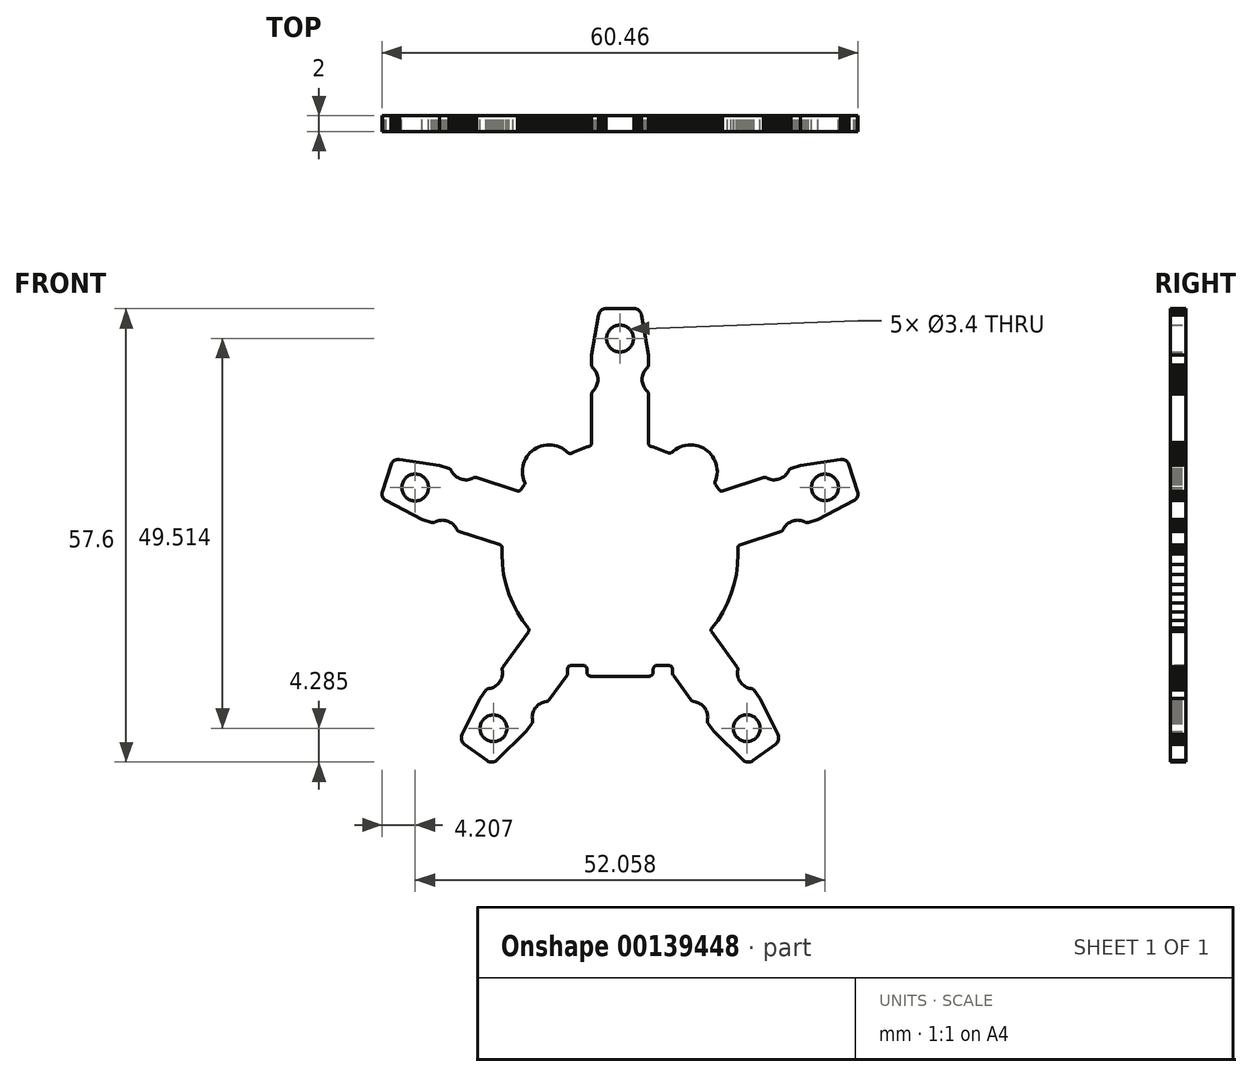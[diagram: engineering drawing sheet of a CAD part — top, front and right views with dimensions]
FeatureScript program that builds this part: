
annotation { "Feature Type Name" : "Feature", "Feature Type Description" : "" }
export const myFeature = defineFeature(function(context is Context, id is Id, definition is map)
    precondition{}
    {
        {
            var Q0;
            Q0=qCreatedBy(makeId("Front.planeOp"),FACE);
            var sketch = newSketch(context, id + "F0", { "sketchPlane" : qUnion([Q0])});
            skLineSegment(sketch, "E0", {"start": v(30.22, 5.42) * mm, "end": v(30.18, 5.6) * mm});
            skLineSegment(sketch, "E1", {"start": v(30.18, 5.6) * mm, "end": v(29.1, 8.94) * mm});
            skLineSegment(sketch, "E2", {"start": v(29.1, 8.94) * mm, "end": v(29.03, 9.1) * mm});
            skLineSegment(sketch, "E3", {"start": v(29.03, 9.1) * mm, "end": v(28.93, 9.25) * mm});
            skLineSegment(sketch, "E4", {"start": v(28.93, 9.25) * mm, "end": v(28.81, 9.38) * mm});
            skLineSegment(sketch, "E5", {"start": v(28.81, 9.38) * mm, "end": v(28.67, 9.48) * mm});
            skLineSegment(sketch, "E6", {"start": v(28.67, 9.48) * mm, "end": v(28.52, 9.56) * mm});
            skLineSegment(sketch, "E7", {"start": v(28.52, 9.56) * mm, "end": v(28.36, 9.6) * mm});
            skLineSegment(sketch, "E8", {"start": v(28.36, 9.6) * mm, "end": v(28.18, 9.63) * mm});
            skLineSegment(sketch, "E9", {"start": v(28.18, 9.63) * mm, "end": v(28, 9.62) * mm});
            skLineSegment(sketch, "E10", {"start": v(28, 9.62) * mm, "end": v(22.92, 8.87) * mm});
            skLineSegment(sketch, "E11", {"start": v(22.92, 8.87) * mm, "end": v(21.71, 8.48) * mm});
            skLineSegment(sketch, "E12", {"start": v(21.71, 8.48) * mm, "end": v(21.66, 8.46) * mm});
            skLineSegment(sketch, "E13", {"start": v(21.66, 8.46) * mm, "end": v(21.62, 8.44) * mm});
            skLineSegment(sketch, "E14", {"start": v(21.62, 8.44) * mm, "end": v(21.58, 8.4) * mm});
            skLineSegment(sketch, "E15", {"start": v(21.58, 8.4) * mm, "end": v(21.54, 8.38) * mm});
            skLineSegment(sketch, "E16", {"start": v(21.54, 8.38) * mm, "end": v(21.5, 8.34) * mm});
            skLineSegment(sketch, "E17", {"start": v(21.5, 8.34) * mm, "end": v(21.47, 8.3) * mm});
            skLineSegment(sketch, "E18", {"start": v(21.47, 8.3) * mm, "end": v(21.44, 8.26) * mm});
            skLineSegment(sketch, "E19", {"start": v(21.44, 8.26) * mm, "end": v(21.32, 8.03) * mm});
            skLineSegment(sketch, "E20", {"start": v(21.32, 8.03) * mm, "end": v(21.2, 7.86) * mm});
            skLineSegment(sketch, "E21", {"start": v(21.2, 7.86) * mm, "end": v(21.07, 7.7) * mm});
            skLineSegment(sketch, "E22", {"start": v(21.07, 7.7) * mm, "end": v(20.92, 7.56) * mm});
            skLineSegment(sketch, "E23", {"start": v(20.92, 7.56) * mm, "end": v(20.77, 7.43) * mm});
            skLineSegment(sketch, "E24", {"start": v(20.77, 7.43) * mm, "end": v(20.6, 7.32) * mm});
            skLineSegment(sketch, "E25", {"start": v(20.6, 7.32) * mm, "end": v(20.4, 7.22) * mm});
            skLineSegment(sketch, "E26", {"start": v(20.4, 7.22) * mm, "end": v(20.22, 7.15) * mm});
            skLineSegment(sketch, "E27", {"start": v(20.22, 7.15) * mm, "end": v(20.02, 7.1) * mm});
            skLineSegment(sketch, "E28", {"start": v(20.02, 7.1) * mm, "end": v(19.81, 7.06) * mm});
            skLineSegment(sketch, "E29", {"start": v(19.81, 7.06) * mm, "end": v(19.6, 7.05) * mm});
            skLineSegment(sketch, "E30", {"start": v(19.6, 7.05) * mm, "end": v(19.4, 7.06) * mm});
            skLineSegment(sketch, "E31", {"start": v(19.4, 7.06) * mm, "end": v(19.2, 7.1) * mm});
            skLineSegment(sketch, "E32", {"start": v(19.2, 7.1) * mm, "end": v(19, 7.14) * mm});
            skLineSegment(sketch, "E33", {"start": v(19, 7.14) * mm, "end": v(18.8, 7.21) * mm});
            skLineSegment(sketch, "E34", {"start": v(18.8, 7.21) * mm, "end": v(18.58, 7.33) * mm});
            skLineSegment(sketch, "E35", {"start": v(18.58, 7.33) * mm, "end": v(18.53, 7.35) * mm});
            skLineSegment(sketch, "E36", {"start": v(18.53, 7.35) * mm, "end": v(18.48, 7.36) * mm});
            skLineSegment(sketch, "E37", {"start": v(18.48, 7.36) * mm, "end": v(18.43, 7.37) * mm});
            skLineSegment(sketch, "E38", {"start": v(18.43, 7.37) * mm, "end": v(18.38, 7.37) * mm});
            skLineSegment(sketch, "E39", {"start": v(18.38, 7.37) * mm, "end": v(18.33, 7.37) * mm});
            skLineSegment(sketch, "E40", {"start": v(18.33, 7.37) * mm, "end": v(18.28, 7.36) * mm});
            skLineSegment(sketch, "E41", {"start": v(18.28, 7.36) * mm, "end": v(18.23, 7.34) * mm});
            skLineSegment(sketch, "E42", {"start": v(18.23, 7.34) * mm, "end": v(13.03, 5.66) * mm});
            skLineSegment(sketch, "E43", {"start": v(13.03, 5.66) * mm, "end": v(13, 5.65) * mm});
            skLineSegment(sketch, "E44", {"start": v(13, 5.65) * mm, "end": v(12.96, 5.65) * mm});
            skLineSegment(sketch, "E45", {"start": v(12.96, 5.65) * mm, "end": v(12.92, 5.64) * mm});
            skLineSegment(sketch, "E46", {"start": v(12.92, 5.64) * mm, "end": v(12.88, 5.64) * mm});
            skLineSegment(sketch, "E47", {"start": v(12.88, 5.64) * mm, "end": v(12.83, 5.64) * mm});
            skLineSegment(sketch, "E48", {"start": v(12.83, 5.64) * mm, "end": v(12.8, 5.64) * mm});
            skLineSegment(sketch, "E49", {"start": v(12.8, 5.64) * mm, "end": v(12.76, 5.65) * mm});
            skLineSegment(sketch, "E50", {"start": v(12.76, 5.65) * mm, "end": v(12.73, 5.66) * mm});
            skLineSegment(sketch, "E51", {"start": v(12.73, 5.66) * mm, "end": v(12.7, 5.68) * mm});
            skLineSegment(sketch, "E52", {"start": v(12.7, 5.68) * mm, "end": v(12.67, 5.7) * mm});
            skLineSegment(sketch, "E53", {"start": v(12.67, 5.7) * mm, "end": v(12.65, 5.72) * mm});
            skLineSegment(sketch, "E54", {"start": v(12.65, 5.72) * mm, "end": v(12.63, 5.74) * mm});
            skLineSegment(sketch, "E55", {"start": v(12.63, 5.74) * mm, "end": v(12.6, 5.77) * mm});
            skLineSegment(sketch, "E56", {"start": v(12.6, 5.77) * mm, "end": v(12.59, 5.8) * mm});
            skLineSegment(sketch, "E57", {"start": v(12.59, 5.8) * mm, "end": v(12.4, 6.07) * mm});
            skLineSegment(sketch, "E58", {"start": v(12.4, 6.07) * mm, "end": v(12.1, 6.48) * mm});
            skLineSegment(sketch, "E59", {"start": v(12.1, 6.48) * mm, "end": v(12.1, 6.5) * mm});
            skLineSegment(sketch, "E60", {"start": v(12.1, 6.5) * mm, "end": v(12.09, 6.52) * mm});
            skLineSegment(sketch, "E61", {"start": v(12.09, 6.52) * mm, "end": v(12.08, 6.54) * mm});
            skLineSegment(sketch, "E62", {"start": v(12.08, 6.54) * mm, "end": v(12.07, 6.56) * mm});
            skLineSegment(sketch, "E63", {"start": v(12.07, 6.56) * mm, "end": v(12.06, 6.58) * mm});
            skLineSegment(sketch, "E64", {"start": v(12.06, 6.58) * mm, "end": v(12.06, 6.6) * mm});
            skLineSegment(sketch, "E65", {"start": v(12.06, 6.6) * mm, "end": v(12.06, 6.63) * mm});
            skLineSegment(sketch, "E66", {"start": v(12.06, 6.63) * mm, "end": v(12.05, 6.65) * mm});
            skLineSegment(sketch, "E67", {"start": v(12.05, 6.65) * mm, "end": v(12.05, 6.67) * mm});
            skLineSegment(sketch, "E68", {"start": v(12.05, 6.67) * mm, "end": v(12.06, 6.7) * mm});
            skLineSegment(sketch, "E69", {"start": v(12.06, 6.7) * mm, "end": v(12.06, 6.71) * mm});
            skLineSegment(sketch, "E70", {"start": v(12.06, 6.71) * mm, "end": v(12.06, 6.73) * mm});
            skLineSegment(sketch, "E71", {"start": v(12.06, 6.73) * mm, "end": v(12.06, 6.73) * mm});
            skLineSegment(sketch, "E72", {"start": v(12.06, 6.73) * mm, "end": v(12.09, 6.78) * mm});
            skLineSegment(sketch, "E73", {"start": v(12.09, 6.78) * mm, "end": v(12.2, 7.09) * mm});
            skLineSegment(sketch, "E74", {"start": v(12.2, 7.09) * mm, "end": v(12.28, 7.42) * mm});
            skLineSegment(sketch, "E75", {"start": v(12.28, 7.42) * mm, "end": v(12.34, 7.75) * mm});
            skLineSegment(sketch, "E76", {"start": v(12.34, 7.75) * mm, "end": v(12.35, 8.1) * mm});
            skLineSegment(sketch, "E77", {"start": v(12.35, 8.1) * mm, "end": v(12.34, 8.45) * mm});
            skLineSegment(sketch, "E78", {"start": v(12.34, 8.45) * mm, "end": v(12.28, 8.79) * mm});
            skLineSegment(sketch, "E79", {"start": v(12.28, 8.79) * mm, "end": v(12.2, 9.11) * mm});
            skLineSegment(sketch, "E80", {"start": v(12.2, 9.11) * mm, "end": v(12.09, 9.42) * mm});
            skLineSegment(sketch, "E81", {"start": v(12.09, 9.42) * mm, "end": v(11.94, 9.72) * mm});
            skLineSegment(sketch, "E82", {"start": v(11.94, 9.72) * mm, "end": v(11.77, 10) * mm});
            skLineSegment(sketch, "E83", {"start": v(11.77, 10) * mm, "end": v(11.58, 10.26) * mm});
            skLineSegment(sketch, "E84", {"start": v(11.58, 10.26) * mm, "end": v(11.36, 10.5) * mm});
            skLineSegment(sketch, "E85", {"start": v(11.36, 10.5) * mm, "end": v(11.12, 10.72) * mm});
            skLineSegment(sketch, "E86", {"start": v(11.12, 10.72) * mm, "end": v(10.85, 10.92) * mm});
            skLineSegment(sketch, "E87", {"start": v(10.85, 10.92) * mm, "end": v(10.57, 11.09) * mm});
            skLineSegment(sketch, "E88", {"start": v(10.57, 11.09) * mm, "end": v(10.28, 11.23) * mm});
            skLineSegment(sketch, "E89", {"start": v(10.28, 11.23) * mm, "end": v(9.96, 11.35) * mm});
            skLineSegment(sketch, "E90", {"start": v(9.96, 11.35) * mm, "end": v(9.64, 11.43) * mm});
            skLineSegment(sketch, "E91", {"start": v(9.64, 11.43) * mm, "end": v(9.3, 11.48) * mm});
            skLineSegment(sketch, "E92", {"start": v(9.3, 11.48) * mm, "end": v(8.95, 11.5) * mm});
            skLineSegment(sketch, "E93", {"start": v(8.95, 11.5) * mm, "end": v(8.6, 11.48) * mm});
            skLineSegment(sketch, "E94", {"start": v(8.6, 11.48) * mm, "end": v(8.27, 11.43) * mm});
            skLineSegment(sketch, "E95", {"start": v(8.27, 11.43) * mm, "end": v(7.94, 11.35) * mm});
            skLineSegment(sketch, "E96", {"start": v(7.94, 11.35) * mm, "end": v(7.63, 11.23) * mm});
            skLineSegment(sketch, "E97", {"start": v(7.63, 11.23) * mm, "end": v(7.33, 11.1) * mm});
            skLineSegment(sketch, "E98", {"start": v(7.33, 11.1) * mm, "end": v(7.05, 10.92) * mm});
            skLineSegment(sketch, "E99", {"start": v(7.05, 10.92) * mm, "end": v(6.8, 10.72) * mm});
            skLineSegment(sketch, "E100", {"start": v(6.8, 10.72) * mm, "end": v(6.63, 10.58) * mm});
            skLineSegment(sketch, "E101", {"start": v(6.63, 10.58) * mm, "end": v(6.55, 10.51) * mm});
            skLineSegment(sketch, "E102", {"start": v(6.55, 10.51) * mm, "end": v(6.47, 10.47) * mm});
            skLineSegment(sketch, "E103", {"start": v(6.47, 10.47) * mm, "end": v(6.37, 10.44) * mm});
            skLineSegment(sketch, "E104", {"start": v(6.37, 10.44) * mm, "end": v(6.27, 10.43) * mm});
            skLineSegment(sketch, "E105", {"start": v(6.27, 10.43) * mm, "end": v(6.17, 10.44) * mm});
            skLineSegment(sketch, "E106", {"start": v(6.17, 10.44) * mm, "end": v(6.08, 10.47) * mm});
            skLineSegment(sketch, "E107", {"start": v(6.08, 10.47) * mm, "end": v(6.02, 10.5) * mm});
            skLineSegment(sketch, "E108", {"start": v(6.02, 10.5) * mm, "end": v(5.84, 10.58) * mm});
            skLineSegment(sketch, "E109", {"start": v(5.84, 10.58) * mm, "end": v(5.53, 10.72) * mm});
            skLineSegment(sketch, "E110", {"start": v(5.53, 10.72) * mm, "end": v(5.2, 10.85) * mm});
            skLineSegment(sketch, "E111", {"start": v(5.2, 10.85) * mm, "end": v(4.88, 10.97) * mm});
            skLineSegment(sketch, "E112", {"start": v(4.88, 10.97) * mm, "end": v(4.56, 11.1) * mm});
            skLineSegment(sketch, "E113", {"start": v(4.56, 11.1) * mm, "end": v(4.22, 11.2) * mm});
            skLineSegment(sketch, "E114", {"start": v(4.22, 11.2) * mm, "end": v(4.02, 11.26) * mm});
            skLineSegment(sketch, "E115", {"start": v(4.02, 11.26) * mm, "end": v(3.9, 11.29) * mm});
            skLineSegment(sketch, "E116", {"start": v(3.9, 11.29) * mm, "end": v(3.82, 11.34) * mm});
            skLineSegment(sketch, "E117", {"start": v(3.82, 11.34) * mm, "end": v(3.75, 11.4) * mm});
            skLineSegment(sketch, "E118", {"start": v(3.75, 11.4) * mm, "end": v(3.68, 11.47) * mm});
            skLineSegment(sketch, "E119", {"start": v(3.68, 11.47) * mm, "end": v(3.64, 11.56) * mm});
            skLineSegment(sketch, "E120", {"start": v(3.64, 11.56) * mm, "end": v(3.6, 11.65) * mm});
            skLineSegment(sketch, "E121", {"start": v(3.6, 11.65) * mm, "end": v(3.6, 11.76) * mm});
            skLineSegment(sketch, "E122", {"start": v(3.6, 11.76) * mm, "end": v(3.6, 17.97) * mm});
            skLineSegment(sketch, "E123", {"start": v(3.6, 17.97) * mm, "end": v(3.6, 18.02) * mm});
            skLineSegment(sketch, "E124", {"start": v(3.6, 18.02) * mm, "end": v(3.59, 18.07) * mm});
            skLineSegment(sketch, "E125", {"start": v(3.59, 18.07) * mm, "end": v(3.58, 18.12) * mm});
            skLineSegment(sketch, "E126", {"start": v(3.58, 18.12) * mm, "end": v(3.56, 18.17) * mm});
            skLineSegment(sketch, "E127", {"start": v(3.56, 18.17) * mm, "end": v(3.54, 18.21) * mm});
            skLineSegment(sketch, "E128", {"start": v(3.54, 18.21) * mm, "end": v(3.5, 18.26) * mm});
            skLineSegment(sketch, "E129", {"start": v(3.5, 18.26) * mm, "end": v(3.48, 18.3) * mm});
            skLineSegment(sketch, "E130", {"start": v(3.48, 18.3) * mm, "end": v(3.3, 18.48) * mm});
            skLineSegment(sketch, "E131", {"start": v(3.3, 18.48) * mm, "end": v(3.17, 18.65) * mm});
            skLineSegment(sketch, "E132", {"start": v(3.17, 18.65) * mm, "end": v(3.06, 18.82) * mm});
            skLineSegment(sketch, "E133", {"start": v(3.06, 18.82) * mm, "end": v(2.97, 19) * mm});
            skLineSegment(sketch, "E134", {"start": v(2.97, 19) * mm, "end": v(2.9, 19.2) * mm});
            skLineSegment(sketch, "E135", {"start": v(2.9, 19.2) * mm, "end": v(2.84, 19.4) * mm});
            skLineSegment(sketch, "E136", {"start": v(2.84, 19.4) * mm, "end": v(2.81, 19.6) * mm});
            skLineSegment(sketch, "E137", {"start": v(2.81, 19.6) * mm, "end": v(2.8, 19.8) * mm});
            skLineSegment(sketch, "E138", {"start": v(2.8, 19.8) * mm, "end": v(2.81, 20) * mm});
            skLineSegment(sketch, "E139", {"start": v(2.81, 20) * mm, "end": v(2.84, 20.21) * mm});
            skLineSegment(sketch, "E140", {"start": v(2.84, 20.21) * mm, "end": v(2.9, 20.41) * mm});
            skLineSegment(sketch, "E141", {"start": v(2.9, 20.41) * mm, "end": v(2.97, 20.6) * mm});
            skLineSegment(sketch, "E142", {"start": v(2.97, 20.6) * mm, "end": v(3.06, 20.78) * mm});
            skLineSegment(sketch, "E143", {"start": v(3.06, 20.78) * mm, "end": v(3.17, 20.96) * mm});
            skLineSegment(sketch, "E144", {"start": v(3.17, 20.96) * mm, "end": v(3.3, 21.12) * mm});
            skLineSegment(sketch, "E145", {"start": v(3.3, 21.12) * mm, "end": v(3.48, 21.3) * mm});
            skLineSegment(sketch, "E146", {"start": v(3.48, 21.3) * mm, "end": v(3.5, 21.35) * mm});
            skLineSegment(sketch, "E147", {"start": v(3.5, 21.35) * mm, "end": v(3.54, 21.39) * mm});
            skLineSegment(sketch, "E148", {"start": v(3.54, 21.39) * mm, "end": v(3.56, 21.44) * mm});
            skLineSegment(sketch, "E149", {"start": v(3.56, 21.44) * mm, "end": v(3.58, 21.48) * mm});
            skLineSegment(sketch, "E150", {"start": v(3.58, 21.48) * mm, "end": v(3.59, 21.53) * mm});
            skLineSegment(sketch, "E151", {"start": v(3.59, 21.53) * mm, "end": v(3.6, 21.58) * mm});
            skLineSegment(sketch, "E152", {"start": v(3.6, 21.58) * mm, "end": v(3.6, 21.63) * mm});
            skLineSegment(sketch, "E153", {"start": v(3.6, 21.63) * mm, "end": v(3.6, 22.9) * mm});
            skLineSegment(sketch, "E154", {"start": v(3.6, 22.9) * mm, "end": v(2.74, 27.97) * mm});
            skLineSegment(sketch, "E155", {"start": v(2.74, 27.97) * mm, "end": v(2.7, 28.14) * mm});
            skLineSegment(sketch, "E156", {"start": v(2.7, 28.14) * mm, "end": v(2.62, 28.3) * mm});
            skLineSegment(sketch, "E157", {"start": v(2.62, 28.3) * mm, "end": v(2.52, 28.44) * mm});
            skLineSegment(sketch, "E158", {"start": v(2.52, 28.44) * mm, "end": v(2.4, 28.57) * mm});
            skLineSegment(sketch, "E159", {"start": v(2.4, 28.57) * mm, "end": v(2.26, 28.67) * mm});
            skLineSegment(sketch, "E160", {"start": v(2.26, 28.67) * mm, "end": v(2.1, 28.74) * mm});
            skLineSegment(sketch, "E161", {"start": v(2.1, 28.74) * mm, "end": v(1.93, 28.79) * mm});
            skLineSegment(sketch, "E162", {"start": v(1.93, 28.79) * mm, "end": v(1.76, 28.8) * mm});
            skLineSegment(sketch, "E163", {"start": v(1.76, 28.8) * mm, "end": v(-1.4, 28.8) * mm});
            skLineSegment(sketch, "E164", {"start": v(-1.4, 28.8) * mm, "end": v(1.6, 28.8) * mm});
            skLineSegment(sketch, "E165", {"start": v(-1.4, 28.8) * mm, "end": v(-1.7, 28.8) * mm});
            skLineSegment(sketch, "E166", {"start": v(-1.7, 28.8) * mm, "end": v(-1.76, 28.8) * mm});
            skLineSegment(sketch, "E167", {"start": v(-1.76, 28.8) * mm, "end": v(-1.93, 28.79) * mm});
            skLineSegment(sketch, "E168", {"start": v(-1.93, 28.79) * mm, "end": v(-2.1, 28.74) * mm});
            skLineSegment(sketch, "E169", {"start": v(-2.1, 28.74) * mm, "end": v(-2.26, 28.67) * mm});
            skLineSegment(sketch, "E170", {"start": v(-2.26, 28.67) * mm, "end": v(-2.4, 28.57) * mm});
            skLineSegment(sketch, "E171", {"start": v(-2.4, 28.57) * mm, "end": v(-2.52, 28.44) * mm});
            skLineSegment(sketch, "E172", {"start": v(-2.52, 28.44) * mm, "end": v(-2.62, 28.3) * mm});
            skLineSegment(sketch, "E173", {"start": v(-2.62, 28.3) * mm, "end": v(-2.7, 28.14) * mm});
            skLineSegment(sketch, "E174", {"start": v(-2.7, 28.14) * mm, "end": v(-2.74, 27.97) * mm});
            skLineSegment(sketch, "E175", {"start": v(-2.74, 27.97) * mm, "end": v(-3.6, 22.9) * mm});
            skLineSegment(sketch, "E176", {"start": v(-3.6, 22.9) * mm, "end": v(-3.6, 21.63) * mm});
            skLineSegment(sketch, "E177", {"start": v(-3.6, 21.63) * mm, "end": v(-3.6, 21.58) * mm});
            skLineSegment(sketch, "E178", {"start": v(-3.6, 21.58) * mm, "end": v(-3.59, 21.53) * mm});
            skLineSegment(sketch, "E179", {"start": v(-3.59, 21.53) * mm, "end": v(-3.58, 21.48) * mm});
            skLineSegment(sketch, "E180", {"start": v(-3.58, 21.48) * mm, "end": v(-3.56, 21.44) * mm});
            skLineSegment(sketch, "E181", {"start": v(-3.56, 21.44) * mm, "end": v(-3.53, 21.39) * mm});
            skLineSegment(sketch, "E182", {"start": v(-3.53, 21.39) * mm, "end": v(-3.5, 21.35) * mm});
            skLineSegment(sketch, "E183", {"start": v(-3.5, 21.35) * mm, "end": v(-3.48, 21.3) * mm});
            skLineSegment(sketch, "E184", {"start": v(-3.48, 21.3) * mm, "end": v(-3.3, 21.12) * mm});
            skLineSegment(sketch, "E185", {"start": v(-3.3, 21.12) * mm, "end": v(-3.17, 20.96) * mm});
            skLineSegment(sketch, "E186", {"start": v(-3.17, 20.96) * mm, "end": v(-3.06, 20.78) * mm});
            skLineSegment(sketch, "E187", {"start": v(-3.06, 20.78) * mm, "end": v(-2.97, 20.6) * mm});
            skLineSegment(sketch, "E188", {"start": v(-2.97, 20.6) * mm, "end": v(-2.9, 20.41) * mm});
            skLineSegment(sketch, "E189", {"start": v(-2.9, 20.41) * mm, "end": v(-2.84, 20.21) * mm});
            skLineSegment(sketch, "E190", {"start": v(-2.84, 20.21) * mm, "end": v(-2.8, 20) * mm});
            skLineSegment(sketch, "E191", {"start": v(-2.8, 20) * mm, "end": v(-2.8, 19.8) * mm});
            skLineSegment(sketch, "E192", {"start": v(-2.8, 19.8) * mm, "end": v(-2.8, 19.6) * mm});
            skLineSegment(sketch, "E193", {"start": v(-2.8, 19.6) * mm, "end": v(-2.84, 19.4) * mm});
            skLineSegment(sketch, "E194", {"start": v(-2.84, 19.4) * mm, "end": v(-2.9, 19.2) * mm});
            skLineSegment(sketch, "E195", {"start": v(-2.9, 19.2) * mm, "end": v(-2.97, 19) * mm});
            skLineSegment(sketch, "E196", {"start": v(-2.97, 19) * mm, "end": v(-3.06, 18.82) * mm});
            skLineSegment(sketch, "E197", {"start": v(-3.06, 18.82) * mm, "end": v(-3.17, 18.65) * mm});
            skLineSegment(sketch, "E198", {"start": v(-3.17, 18.65) * mm, "end": v(-3.3, 18.48) * mm});
            skLineSegment(sketch, "E199", {"start": v(-3.3, 18.48) * mm, "end": v(-3.48, 18.3) * mm});
            skLineSegment(sketch, "E200", {"start": v(-3.48, 18.3) * mm, "end": v(-3.5, 18.26) * mm});
            skLineSegment(sketch, "E201", {"start": v(-3.5, 18.26) * mm, "end": v(-3.53, 18.21) * mm});
            skLineSegment(sketch, "E202", {"start": v(-3.53, 18.21) * mm, "end": v(-3.56, 18.17) * mm});
            skLineSegment(sketch, "E203", {"start": v(-3.56, 18.17) * mm, "end": v(-3.58, 18.12) * mm});
            skLineSegment(sketch, "E204", {"start": v(-3.58, 18.12) * mm, "end": v(-3.59, 18.07) * mm});
            skLineSegment(sketch, "E205", {"start": v(-3.59, 18.07) * mm, "end": v(-3.6, 18.02) * mm});
            skLineSegment(sketch, "E206", {"start": v(-3.6, 18.02) * mm, "end": v(-3.6, 17.97) * mm});
            skLineSegment(sketch, "E207", {"start": v(-3.6, 17.97) * mm, "end": v(-3.6, 11.83) * mm});
            skLineSegment(sketch, "E208", {"start": v(-3.6, 11.83) * mm, "end": v(-3.6, 11.66) * mm});
            skLineSegment(sketch, "E209", {"start": v(-3.6, 11.66) * mm, "end": v(-3.63, 11.56) * mm});
            skLineSegment(sketch, "E210", {"start": v(-3.63, 11.56) * mm, "end": v(-3.68, 11.48) * mm});
            skLineSegment(sketch, "E211", {"start": v(-3.68, 11.48) * mm, "end": v(-3.74, 11.4) * mm});
            skLineSegment(sketch, "E212", {"start": v(-3.74, 11.4) * mm, "end": v(-3.81, 11.34) * mm});
            skLineSegment(sketch, "E213", {"start": v(-3.81, 11.34) * mm, "end": v(-3.9, 11.3) * mm});
            skLineSegment(sketch, "E214", {"start": v(-3.9, 11.3) * mm, "end": v(-3.94, 11.28) * mm});
            skLineSegment(sketch, "E215", {"start": v(-3.94, 11.28) * mm, "end": v(-3.94, 11.28) * mm});
            skLineSegment(sketch, "E216", {"start": v(-3.94, 11.28) * mm, "end": v(-4, 11.27) * mm});
            skLineSegment(sketch, "E217", {"start": v(-4, 11.27) * mm, "end": v(-4.22, 11.2) * mm});
            skLineSegment(sketch, "E218", {"start": v(-4.22, 11.2) * mm, "end": v(-4.55, 11.1) * mm});
            skLineSegment(sketch, "E219", {"start": v(-4.55, 11.1) * mm, "end": v(-4.88, 10.97) * mm});
            skLineSegment(sketch, "E220", {"start": v(-4.88, 10.97) * mm, "end": v(-5.2, 10.85) * mm});
            skLineSegment(sketch, "E221", {"start": v(-5.2, 10.85) * mm, "end": v(-5.53, 10.72) * mm});
            skLineSegment(sketch, "E222", {"start": v(-5.53, 10.72) * mm, "end": v(-5.84, 10.58) * mm});
            skLineSegment(sketch, "E223", {"start": v(-5.84, 10.58) * mm, "end": v(-6.12, 10.45) * mm});
            skLineSegment(sketch, "E224", {"start": v(-6.12, 10.45) * mm, "end": v(-6.12, 10.45) * mm});
            skLineSegment(sketch, "E225", {"start": v(-6.12, 10.45) * mm, "end": v(-6.22, 10.42) * mm});
            skLineSegment(sketch, "E226", {"start": v(-6.22, 10.42) * mm, "end": v(-6.32, 10.41) * mm});
            skLineSegment(sketch, "E227", {"start": v(-6.32, 10.41) * mm, "end": v(-6.42, 10.42) * mm});
            skLineSegment(sketch, "E228", {"start": v(-6.42, 10.42) * mm, "end": v(-6.51, 10.45) * mm});
            skLineSegment(sketch, "E229", {"start": v(-6.51, 10.45) * mm, "end": v(-6.6, 10.5) * mm});
            skLineSegment(sketch, "E230", {"start": v(-6.6, 10.5) * mm, "end": v(-6.66, 10.55) * mm});
            skLineSegment(sketch, "E231", {"start": v(-6.66, 10.55) * mm, "end": v(-6.66, 10.55) * mm});
            skLineSegment(sketch, "E232", {"start": v(-6.66, 10.55) * mm, "end": v(-6.85, 10.72) * mm});
            skLineSegment(sketch, "E233", {"start": v(-6.85, 10.72) * mm, "end": v(-7.12, 10.92) * mm});
            skLineSegment(sketch, "E234", {"start": v(-7.12, 10.92) * mm, "end": v(-7.4, 11.09) * mm});
            skLineSegment(sketch, "E235", {"start": v(-7.4, 11.09) * mm, "end": v(-7.7, 11.23) * mm});
            skLineSegment(sketch, "E236", {"start": v(-7.7, 11.23) * mm, "end": v(-8, 11.35) * mm});
            skLineSegment(sketch, "E237", {"start": v(-8, 11.35) * mm, "end": v(-8.33, 11.43) * mm});
            skLineSegment(sketch, "E238", {"start": v(-8.33, 11.43) * mm, "end": v(-8.67, 11.48) * mm});
            skLineSegment(sketch, "E239", {"start": v(-8.67, 11.48) * mm, "end": v(-9.02, 11.5) * mm});
            skLineSegment(sketch, "E240", {"start": v(-9.02, 11.5) * mm, "end": v(-9.36, 11.48) * mm});
            skLineSegment(sketch, "E241", {"start": v(-9.36, 11.48) * mm, "end": v(-9.7, 11.43) * mm});
            skLineSegment(sketch, "E242", {"start": v(-9.7, 11.43) * mm, "end": v(-10.03, 11.35) * mm});
            skLineSegment(sketch, "E243", {"start": v(-10.03, 11.35) * mm, "end": v(-10.34, 11.23) * mm});
            skLineSegment(sketch, "E244", {"start": v(-10.34, 11.23) * mm, "end": v(-10.64, 11.09) * mm});
            skLineSegment(sketch, "E245", {"start": v(-10.64, 11.09) * mm, "end": v(-10.92, 10.92) * mm});
            skLineSegment(sketch, "E246", {"start": v(-10.92, 10.92) * mm, "end": v(-11.18, 10.72) * mm});
            skLineSegment(sketch, "E247", {"start": v(-11.18, 10.72) * mm, "end": v(-11.42, 10.5) * mm});
            skLineSegment(sketch, "E248", {"start": v(-11.42, 10.5) * mm, "end": v(-11.64, 10.26) * mm});
            skLineSegment(sketch, "E249", {"start": v(-11.64, 10.26) * mm, "end": v(-11.84, 10) * mm});
            skLineSegment(sketch, "E250", {"start": v(-11.84, 10) * mm, "end": v(-12, 9.72) * mm});
            skLineSegment(sketch, "E251", {"start": v(-12, 9.72) * mm, "end": v(-12.15, 9.42) * mm});
            skLineSegment(sketch, "E252", {"start": v(-12.15, 9.42) * mm, "end": v(-12.26, 9.11) * mm});
            skLineSegment(sketch, "E253", {"start": v(-12.26, 9.11) * mm, "end": v(-12.35, 8.79) * mm});
            skLineSegment(sketch, "E254", {"start": v(-12.35, 8.79) * mm, "end": v(-12.4, 8.45) * mm});
            skLineSegment(sketch, "E255", {"start": v(-12.4, 8.45) * mm, "end": v(-12.42, 8.1) * mm});
            skLineSegment(sketch, "E256", {"start": v(-12.42, 8.1) * mm, "end": v(-12.4, 7.75) * mm});
            skLineSegment(sketch, "E257", {"start": v(-12.4, 7.75) * mm, "end": v(-12.35, 7.42) * mm});
            skLineSegment(sketch, "E258", {"start": v(-12.35, 7.42) * mm, "end": v(-12.26, 7.09) * mm});
            skLineSegment(sketch, "E259", {"start": v(-12.26, 7.09) * mm, "end": v(-12.15, 6.78) * mm});
            skLineSegment(sketch, "E260", {"start": v(-12.15, 6.78) * mm, "end": v(-12.1, 6.67) * mm});
            skLineSegment(sketch, "E261", {"start": v(-12.1, 6.67) * mm, "end": v(-12.1, 6.67) * mm});
            skLineSegment(sketch, "E262", {"start": v(-12.1, 6.67) * mm, "end": v(-12.1, 6.64) * mm});
            skLineSegment(sketch, "E263", {"start": v(-12.1, 6.64) * mm, "end": v(-12.1, 6.61) * mm});
            skLineSegment(sketch, "E264", {"start": v(-12.1, 6.61) * mm, "end": v(-12.1, 6.58) * mm});
            skLineSegment(sketch, "E265", {"start": v(-12.1, 6.58) * mm, "end": v(-12.1, 6.56) * mm});
            skLineSegment(sketch, "E266", {"start": v(-12.1, 6.56) * mm, "end": v(-12.1, 6.53) * mm});
            skLineSegment(sketch, "E267", {"start": v(-12.1, 6.53) * mm, "end": v(-12.1, 6.51) * mm});
            skLineSegment(sketch, "E268", {"start": v(-12.1, 6.51) * mm, "end": v(-12.11, 6.5) * mm});
            skLineSegment(sketch, "E269", {"start": v(-12.11, 6.5) * mm, "end": v(-12.12, 6.47) * mm});
            skLineSegment(sketch, "E270", {"start": v(-12.12, 6.47) * mm, "end": v(-12.13, 6.45) * mm});
            skLineSegment(sketch, "E271", {"start": v(-12.13, 6.45) * mm, "end": v(-12.15, 6.43) * mm});
            skLineSegment(sketch, "E272", {"start": v(-12.15, 6.43) * mm, "end": v(-12.44, 6) * mm});
            skLineSegment(sketch, "E273", {"start": v(-12.44, 6) * mm, "end": v(-12.56, 5.83) * mm});
            skLineSegment(sketch, "E274", {"start": v(-12.56, 5.83) * mm, "end": v(-12.58, 5.8) * mm});
            skLineSegment(sketch, "E275", {"start": v(-12.58, 5.8) * mm, "end": v(-12.6, 5.77) * mm});
            skLineSegment(sketch, "E276", {"start": v(-12.6, 5.77) * mm, "end": v(-12.63, 5.74) * mm});
            skLineSegment(sketch, "E277", {"start": v(-12.63, 5.74) * mm, "end": v(-12.66, 5.71) * mm});
            skLineSegment(sketch, "E278", {"start": v(-12.66, 5.71) * mm, "end": v(-12.69, 5.7) * mm});
            skLineSegment(sketch, "E279", {"start": v(-12.69, 5.7) * mm, "end": v(-12.72, 5.67) * mm});
            skLineSegment(sketch, "E280", {"start": v(-12.72, 5.67) * mm, "end": v(-12.76, 5.66) * mm});
            skLineSegment(sketch, "E281", {"start": v(-12.76, 5.66) * mm, "end": v(-12.8, 5.65) * mm});
            skLineSegment(sketch, "E282", {"start": v(-12.8, 5.65) * mm, "end": v(-12.84, 5.64) * mm});
            skLineSegment(sketch, "E283", {"start": v(-12.84, 5.64) * mm, "end": v(-12.88, 5.64) * mm});
            skLineSegment(sketch, "E284", {"start": v(-12.88, 5.64) * mm, "end": v(-12.93, 5.65) * mm});
            skLineSegment(sketch, "E285", {"start": v(-12.93, 5.65) * mm, "end": v(-13, 5.65) * mm});
            skLineSegment(sketch, "E286", {"start": v(-13, 5.65) * mm, "end": v(-13.03, 5.66) * mm});
            skLineSegment(sketch, "E287", {"start": v(-13.03, 5.66) * mm, "end": v(-18.23, 7.34) * mm});
            skLineSegment(sketch, "E288", {"start": v(-18.23, 7.34) * mm, "end": v(-18.28, 7.36) * mm});
            skLineSegment(sketch, "E289", {"start": v(-18.28, 7.36) * mm, "end": v(-18.33, 7.37) * mm});
            skLineSegment(sketch, "E290", {"start": v(-18.33, 7.37) * mm, "end": v(-18.38, 7.37) * mm});
            skLineSegment(sketch, "E291", {"start": v(-18.38, 7.37) * mm, "end": v(-18.43, 7.37) * mm});
            skLineSegment(sketch, "E292", {"start": v(-18.43, 7.37) * mm, "end": v(-18.48, 7.36) * mm});
            skLineSegment(sketch, "E293", {"start": v(-18.48, 7.36) * mm, "end": v(-18.53, 7.35) * mm});
            skLineSegment(sketch, "E294", {"start": v(-18.53, 7.35) * mm, "end": v(-18.58, 7.33) * mm});
            skLineSegment(sketch, "E295", {"start": v(-18.58, 7.33) * mm, "end": v(-18.8, 7.21) * mm});
            skLineSegment(sketch, "E296", {"start": v(-18.8, 7.21) * mm, "end": v(-19, 7.14) * mm});
            skLineSegment(sketch, "E297", {"start": v(-19, 7.14) * mm, "end": v(-19.2, 7.1) * mm});
            skLineSegment(sketch, "E298", {"start": v(-19.2, 7.1) * mm, "end": v(-19.4, 7.06) * mm});
            skLineSegment(sketch, "E299", {"start": v(-19.4, 7.06) * mm, "end": v(-19.6, 7.05) * mm});
            skLineSegment(sketch, "E300", {"start": v(-19.6, 7.05) * mm, "end": v(-19.81, 7.06) * mm});
            skLineSegment(sketch, "E301", {"start": v(-19.81, 7.06) * mm, "end": v(-20.02, 7.1) * mm});
            skLineSegment(sketch, "E302", {"start": v(-20.02, 7.1) * mm, "end": v(-20.22, 7.15) * mm});
            skLineSegment(sketch, "E303", {"start": v(-20.22, 7.15) * mm, "end": v(-20.4, 7.22) * mm});
            skLineSegment(sketch, "E304", {"start": v(-20.4, 7.22) * mm, "end": v(-20.6, 7.32) * mm});
            skLineSegment(sketch, "E305", {"start": v(-20.6, 7.32) * mm, "end": v(-20.77, 7.43) * mm});
            skLineSegment(sketch, "E306", {"start": v(-20.77, 7.43) * mm, "end": v(-20.92, 7.56) * mm});
            skLineSegment(sketch, "E307", {"start": v(-20.92, 7.56) * mm, "end": v(-21.07, 7.7) * mm});
            skLineSegment(sketch, "E308", {"start": v(-21.07, 7.7) * mm, "end": v(-21.2, 7.86) * mm});
            skLineSegment(sketch, "E309", {"start": v(-21.2, 7.86) * mm, "end": v(-21.32, 8.03) * mm});
            skLineSegment(sketch, "E310", {"start": v(-21.32, 8.03) * mm, "end": v(-21.44, 8.26) * mm});
            skLineSegment(sketch, "E311", {"start": v(-21.44, 8.26) * mm, "end": v(-21.47, 8.3) * mm});
            skLineSegment(sketch, "E312", {"start": v(-21.47, 8.3) * mm, "end": v(-21.5, 8.34) * mm});
            skLineSegment(sketch, "E313", {"start": v(-21.5, 8.34) * mm, "end": v(-21.53, 8.38) * mm});
            skLineSegment(sketch, "E314", {"start": v(-21.53, 8.38) * mm, "end": v(-21.57, 8.4) * mm});
            skLineSegment(sketch, "E315", {"start": v(-21.57, 8.4) * mm, "end": v(-21.62, 8.44) * mm});
            skLineSegment(sketch, "E316", {"start": v(-21.62, 8.44) * mm, "end": v(-21.66, 8.46) * mm});
            skLineSegment(sketch, "E317", {"start": v(-21.66, 8.46) * mm, "end": v(-21.71, 8.48) * mm});
            skLineSegment(sketch, "E318", {"start": v(-21.71, 8.48) * mm, "end": v(-22.92, 8.87) * mm});
            skLineSegment(sketch, "E319", {"start": v(-22.92, 8.87) * mm, "end": v(-28, 9.62) * mm});
            skLineSegment(sketch, "E320", {"start": v(-28, 9.62) * mm, "end": v(-28.18, 9.63) * mm});
            skLineSegment(sketch, "E321", {"start": v(-28.18, 9.63) * mm, "end": v(-28.36, 9.6) * mm});
            skLineSegment(sketch, "E322", {"start": v(-28.36, 9.6) * mm, "end": v(-28.52, 9.56) * mm});
            skLineSegment(sketch, "E323", {"start": v(-28.52, 9.56) * mm, "end": v(-28.67, 9.48) * mm});
            skLineSegment(sketch, "E324", {"start": v(-28.67, 9.48) * mm, "end": v(-28.81, 9.37) * mm});
            skLineSegment(sketch, "E325", {"start": v(-28.81, 9.37) * mm, "end": v(-28.93, 9.25) * mm});
            skLineSegment(sketch, "E326", {"start": v(-28.93, 9.25) * mm, "end": v(-29.03, 9.1) * mm});
            skLineSegment(sketch, "E327", {"start": v(-29.03, 9.1) * mm, "end": v(-29.1, 8.94) * mm});
            skLineSegment(sketch, "E328", {"start": v(-29.1, 8.94) * mm, "end": v(-30.18, 5.6) * mm});
            skLineSegment(sketch, "E329", {"start": v(-30.18, 5.6) * mm, "end": v(-30.22, 5.42) * mm});
            skLineSegment(sketch, "E330", {"start": v(-30.22, 5.42) * mm, "end": v(-30.23, 5.25) * mm});
            skLineSegment(sketch, "E331", {"start": v(-30.23, 5.25) * mm, "end": v(-30.2, 5.08) * mm});
            skLineSegment(sketch, "E332", {"start": v(-30.2, 5.08) * mm, "end": v(-30.16, 4.91) * mm});
            skLineSegment(sketch, "E333", {"start": v(-30.16, 4.91) * mm, "end": v(-30.08, 4.76) * mm});
            skLineSegment(sketch, "E334", {"start": v(-30.08, 4.76) * mm, "end": v(-29.98, 4.62) * mm});
            skLineSegment(sketch, "E335", {"start": v(-29.98, 4.62) * mm, "end": v(-29.85, 4.5) * mm});
            skLineSegment(sketch, "E336", {"start": v(-29.85, 4.5) * mm, "end": v(-29.7, 4.4) * mm});
            skLineSegment(sketch, "E337", {"start": v(-29.7, 4.4) * mm, "end": v(-25.14, 2.02) * mm});
            skLineSegment(sketch, "E338", {"start": v(-25.14, 2.02) * mm, "end": v(-23.94, 1.63) * mm});
            skLineSegment(sketch, "E339", {"start": v(-23.94, 1.63) * mm, "end": v(-23.89, 1.62) * mm});
            skLineSegment(sketch, "E340", {"start": v(-23.89, 1.62) * mm, "end": v(-23.84, 1.6) * mm});
            skLineSegment(sketch, "E341", {"start": v(-23.84, 1.6) * mm, "end": v(-23.79, 1.6) * mm});
            skLineSegment(sketch, "E342", {"start": v(-23.79, 1.6) * mm, "end": v(-23.73, 1.6) * mm});
            skLineSegment(sketch, "E343", {"start": v(-23.73, 1.6) * mm, "end": v(-23.68, 1.61) * mm});
            skLineSegment(sketch, "E344", {"start": v(-23.68, 1.61) * mm, "end": v(-23.63, 1.63) * mm});
            skLineSegment(sketch, "E345", {"start": v(-23.63, 1.63) * mm, "end": v(-23.59, 1.65) * mm});
            skLineSegment(sketch, "E346", {"start": v(-23.59, 1.65) * mm, "end": v(-23.35, 1.76) * mm});
            skLineSegment(sketch, "E347", {"start": v(-23.35, 1.76) * mm, "end": v(-23.16, 1.83) * mm});
            skLineSegment(sketch, "E348", {"start": v(-23.16, 1.83) * mm, "end": v(-22.96, 1.88) * mm});
            skLineSegment(sketch, "E349", {"start": v(-22.96, 1.88) * mm, "end": v(-22.76, 1.91) * mm});
            skLineSegment(sketch, "E350", {"start": v(-22.76, 1.91) * mm, "end": v(-22.55, 1.92) * mm});
            skLineSegment(sketch, "E351", {"start": v(-22.55, 1.92) * mm, "end": v(-22.35, 1.91) * mm});
            skLineSegment(sketch, "E352", {"start": v(-22.35, 1.91) * mm, "end": v(-22.15, 1.88) * mm});
            skLineSegment(sketch, "E353", {"start": v(-22.15, 1.88) * mm, "end": v(-21.95, 1.82) * mm});
            skLineSegment(sketch, "E354", {"start": v(-21.95, 1.82) * mm, "end": v(-21.75, 1.75) * mm});
            skLineSegment(sketch, "E355", {"start": v(-21.75, 1.75) * mm, "end": v(-21.57, 1.66) * mm});
            skLineSegment(sketch, "E356", {"start": v(-21.57, 1.66) * mm, "end": v(-21.4, 1.55) * mm});
            skLineSegment(sketch, "E357", {"start": v(-21.4, 1.55) * mm, "end": v(-21.24, 1.42) * mm});
            skLineSegment(sketch, "E358", {"start": v(-21.24, 1.42) * mm, "end": v(-21.1, 1.27) * mm});
            skLineSegment(sketch, "E359", {"start": v(-21.1, 1.27) * mm, "end": v(-20.96, 1.12) * mm});
            skLineSegment(sketch, "E360", {"start": v(-20.96, 1.12) * mm, "end": v(-20.85, 0.95) * mm});
            skLineSegment(sketch, "E361", {"start": v(-20.85, 0.95) * mm, "end": v(-20.72, 0.72) * mm});
            skLineSegment(sketch, "E362", {"start": v(-20.72, 0.72) * mm, "end": v(-20.7, 0.67) * mm});
            skLineSegment(sketch, "E363", {"start": v(-20.7, 0.67) * mm, "end": v(-20.66, 0.63) * mm});
            skLineSegment(sketch, "E364", {"start": v(-20.66, 0.63) * mm, "end": v(-20.63, 0.6) * mm});
            skLineSegment(sketch, "E365", {"start": v(-20.63, 0.6) * mm, "end": v(-20.59, 0.57) * mm});
            skLineSegment(sketch, "E366", {"start": v(-20.59, 0.57) * mm, "end": v(-20.54, 0.54) * mm});
            skLineSegment(sketch, "E367", {"start": v(-20.54, 0.54) * mm, "end": v(-20.5, 0.52) * mm});
            skLineSegment(sketch, "E368", {"start": v(-20.5, 0.52) * mm, "end": v(-20.45, 0.5) * mm});
            skLineSegment(sketch, "E369", {"start": v(-20.45, 0.5) * mm, "end": v(-15.32, -1.17) * mm});
            skLineSegment(sketch, "E370", {"start": v(-15.32, -1.17) * mm, "end": v(-15.3, -1.18) * mm});
            skLineSegment(sketch, "E371", {"start": v(-15.3, -1.18) * mm, "end": v(-15.25, -1.2) * mm});
            skLineSegment(sketch, "E372", {"start": v(-15.25, -1.2) * mm, "end": v(-15.21, -1.21) * mm});
            skLineSegment(sketch, "E373", {"start": v(-15.21, -1.21) * mm, "end": v(-15.16, -1.23) * mm});
            skLineSegment(sketch, "E374", {"start": v(-15.16, -1.23) * mm, "end": v(-15.12, -1.26) * mm});
            skLineSegment(sketch, "E375", {"start": v(-15.12, -1.26) * mm, "end": v(-15.08, -1.29) * mm});
            skLineSegment(sketch, "E376", {"start": v(-15.08, -1.29) * mm, "end": v(-15.05, -1.32) * mm});
            skLineSegment(sketch, "E377", {"start": v(-15.05, -1.32) * mm, "end": v(-15.03, -1.35) * mm});
            skLineSegment(sketch, "E378", {"start": v(-15.03, -1.35) * mm, "end": v(-15.01, -1.39) * mm});
            skLineSegment(sketch, "E379", {"start": v(-15.01, -1.39) * mm, "end": v(-15, -1.43) * mm});
            skLineSegment(sketch, "E380", {"start": v(-15, -1.43) * mm, "end": v(-14.99, -1.46) * mm});
            skLineSegment(sketch, "E381", {"start": v(-14.99, -1.46) * mm, "end": v(-14.98, -1.5) * mm});
            skLineSegment(sketch, "E382", {"start": v(-14.98, -1.5) * mm, "end": v(-14.98, -1.54) * mm});
            skLineSegment(sketch, "E383", {"start": v(-14.98, -1.54) * mm, "end": v(-14.98, -1.58) * mm});
            skLineSegment(sketch, "E384", {"start": v(-14.98, -1.58) * mm, "end": v(-15, -2.18) * mm});
            skLineSegment(sketch, "E385", {"start": v(-15, -2.18) * mm, "end": v(-15, -2.36) * mm});
            skLineSegment(sketch, "E386", {"start": v(-15, -2.36) * mm, "end": v(-14.94, -3.7) * mm});
            skLineSegment(sketch, "E387", {"start": v(-14.94, -3.7) * mm, "end": v(-14.77, -5) * mm});
            skLineSegment(sketch, "E388", {"start": v(-14.77, -5) * mm, "end": v(-14.49, -6.26) * mm});
            skLineSegment(sketch, "E389", {"start": v(-14.49, -6.26) * mm, "end": v(-14.1, -7.48) * mm});
            skLineSegment(sketch, "E390", {"start": v(-14.1, -7.48) * mm, "end": v(-13.62, -8.65) * mm});
            skLineSegment(sketch, "E391", {"start": v(-13.62, -8.65) * mm, "end": v(-13.04, -9.77) * mm});
            skLineSegment(sketch, "E392", {"start": v(-13.04, -9.77) * mm, "end": v(-12.38, -10.84) * mm});
            skLineSegment(sketch, "E393", {"start": v(-12.38, -10.84) * mm, "end": v(-11.6, -11.86) * mm});
            skLineSegment(sketch, "E394", {"start": v(-11.6, -11.86) * mm, "end": v(-11.6, -11.88) * mm});
            skLineSegment(sketch, "E395", {"start": v(-11.6, -11.88) * mm, "end": v(-11.59, -11.9) * mm});
            skLineSegment(sketch, "E396", {"start": v(-11.59, -11.9) * mm, "end": v(-11.58, -11.93) * mm});
            skLineSegment(sketch, "E397", {"start": v(-11.58, -11.93) * mm, "end": v(-11.57, -11.95) * mm});
            skLineSegment(sketch, "E398", {"start": v(-11.57, -11.95) * mm, "end": v(-11.57, -11.98) * mm});
            skLineSegment(sketch, "E399", {"start": v(-11.57, -11.98) * mm, "end": v(-11.57, -12) * mm});
            skLineSegment(sketch, "E400", {"start": v(-11.57, -12) * mm, "end": v(-11.57, -12.03) * mm});
            skLineSegment(sketch, "E401", {"start": v(-11.57, -12.03) * mm, "end": v(-11.57, -12.06) * mm});
            skLineSegment(sketch, "E402", {"start": v(-11.57, -12.06) * mm, "end": v(-11.58, -12.1) * mm});
            skLineSegment(sketch, "E403", {"start": v(-11.58, -12.1) * mm, "end": v(-11.6, -12.14) * mm});
            skLineSegment(sketch, "E404", {"start": v(-11.6, -12.14) * mm, "end": v(-11.6, -12.18) * mm});
            skLineSegment(sketch, "E405", {"start": v(-11.6, -12.18) * mm, "end": v(-11.62, -12.22) * mm});
            skLineSegment(sketch, "E406", {"start": v(-11.62, -12.22) * mm, "end": v(-11.65, -12.27) * mm});
            skLineSegment(sketch, "E407", {"start": v(-11.65, -12.27) * mm, "end": v(-11.65, -12.28) * mm});
            skLineSegment(sketch, "E408", {"start": v(-11.65, -12.28) * mm, "end": v(-14.87, -16.7) * mm});
            skLineSegment(sketch, "E409", {"start": v(-14.87, -16.7) * mm, "end": v(-14.9, -16.75) * mm});
            skLineSegment(sketch, "E410", {"start": v(-14.9, -16.75) * mm, "end": v(-14.92, -16.8) * mm});
            skLineSegment(sketch, "E411", {"start": v(-14.92, -16.8) * mm, "end": v(-14.94, -16.84) * mm});
            skLineSegment(sketch, "E412", {"start": v(-14.94, -16.84) * mm, "end": v(-14.95, -16.89) * mm});
            skLineSegment(sketch, "E413", {"start": v(-14.95, -16.89) * mm, "end": v(-14.96, -16.94) * mm});
            skLineSegment(sketch, "E414", {"start": v(-14.96, -16.94) * mm, "end": v(-14.96, -16.99) * mm});
            skLineSegment(sketch, "E415", {"start": v(-14.96, -16.99) * mm, "end": v(-14.96, -17.04) * mm});
            skLineSegment(sketch, "E416", {"start": v(-14.96, -17.04) * mm, "end": v(-14.92, -17.3) * mm});
            skLineSegment(sketch, "E417", {"start": v(-14.92, -17.3) * mm, "end": v(-14.92, -17.5) * mm});
            skLineSegment(sketch, "E418", {"start": v(-14.92, -17.5) * mm, "end": v(-14.93, -17.7) * mm});
            skLineSegment(sketch, "E419", {"start": v(-14.93, -17.7) * mm, "end": v(-14.96, -17.9) * mm});
            skLineSegment(sketch, "E420", {"start": v(-14.96, -17.9) * mm, "end": v(-15.02, -18.1) * mm});
            skLineSegment(sketch, "E421", {"start": v(-15.02, -18.1) * mm, "end": v(-15.1, -18.3) * mm});
            skLineSegment(sketch, "E422", {"start": v(-15.1, -18.3) * mm, "end": v(-15.18, -18.48) * mm});
            skLineSegment(sketch, "E423", {"start": v(-15.18, -18.48) * mm, "end": v(-15.3, -18.65) * mm});
            skLineSegment(sketch, "E424", {"start": v(-15.3, -18.65) * mm, "end": v(-15.43, -18.82) * mm});
            skLineSegment(sketch, "E425", {"start": v(-15.43, -18.82) * mm, "end": v(-15.57, -18.96) * mm});
            skLineSegment(sketch, "E426", {"start": v(-15.57, -18.96) * mm, "end": v(-15.73, -19.1) * mm});
            skLineSegment(sketch, "E427", {"start": v(-15.73, -19.1) * mm, "end": v(-15.9, -19.2) * mm});
            skLineSegment(sketch, "E428", {"start": v(-15.9, -19.2) * mm, "end": v(-16.08, -19.3) * mm});
            skLineSegment(sketch, "E429", {"start": v(-16.08, -19.3) * mm, "end": v(-16.27, -19.37) * mm});
            skLineSegment(sketch, "E430", {"start": v(-16.27, -19.37) * mm, "end": v(-16.47, -19.43) * mm});
            skLineSegment(sketch, "E431", {"start": v(-16.47, -19.43) * mm, "end": v(-16.73, -19.47) * mm});
            skLineSegment(sketch, "E432", {"start": v(-16.73, -19.47) * mm, "end": v(-16.78, -19.49) * mm});
            skLineSegment(sketch, "E433", {"start": v(-16.78, -19.49) * mm, "end": v(-16.83, -19.5) * mm});
            skLineSegment(sketch, "E434", {"start": v(-16.83, -19.5) * mm, "end": v(-16.87, -19.53) * mm});
            skLineSegment(sketch, "E435", {"start": v(-16.87, -19.53) * mm, "end": v(-16.91, -19.56) * mm});
            skLineSegment(sketch, "E436", {"start": v(-16.91, -19.56) * mm, "end": v(-16.95, -19.6) * mm});
            skLineSegment(sketch, "E437", {"start": v(-16.95, -19.6) * mm, "end": v(-16.99, -19.63) * mm});
            skLineSegment(sketch, "E438", {"start": v(-16.99, -19.63) * mm, "end": v(-17.02, -19.67) * mm});
            skLineSegment(sketch, "E439", {"start": v(-17.02, -19.67) * mm, "end": v(-17.77, -20.7) * mm});
            skLineSegment(sketch, "E440", {"start": v(-17.77, -20.7) * mm, "end": v(-20.05, -25.3) * mm});
            skLineSegment(sketch, "E441", {"start": v(-20.05, -25.3) * mm, "end": v(-20.12, -25.46) * mm});
            skLineSegment(sketch, "E442", {"start": v(-20.12, -25.46) * mm, "end": v(-20.15, -25.64) * mm});
            skLineSegment(sketch, "E443", {"start": v(-20.15, -25.64) * mm, "end": v(-20.15, -25.8) * mm});
            skLineSegment(sketch, "E444", {"start": v(-20.15, -25.8) * mm, "end": v(-20.13, -25.98) * mm});
            skLineSegment(sketch, "E445", {"start": v(-20.13, -25.98) * mm, "end": v(-20.07, -26.14) * mm});
            skLineSegment(sketch, "E446", {"start": v(-20.07, -26.14) * mm, "end": v(-19.99, -26.3) * mm});
            skLineSegment(sketch, "E447", {"start": v(-19.99, -26.3) * mm, "end": v(-19.88, -26.43) * mm});
            skLineSegment(sketch, "E448", {"start": v(-19.88, -26.43) * mm, "end": v(-19.74, -26.55) * mm});
            skLineSegment(sketch, "E449", {"start": v(-19.74, -26.55) * mm, "end": v(-16.9, -28.61) * mm});
            skLineSegment(sketch, "E450", {"start": v(-16.9, -28.61) * mm, "end": v(-16.75, -28.7) * mm});
            skLineSegment(sketch, "E451", {"start": v(-16.75, -28.7) * mm, "end": v(-16.58, -28.77) * mm});
            skLineSegment(sketch, "E452", {"start": v(-16.58, -28.77) * mm, "end": v(-16.41, -28.8) * mm});
            skLineSegment(sketch, "E453", {"start": v(-16.41, -28.8) * mm, "end": v(-16.24, -28.8) * mm});
            skLineSegment(sketch, "E454", {"start": v(-16.24, -28.8) * mm, "end": v(-16.07, -28.78) * mm});
            skLineSegment(sketch, "E455", {"start": v(-16.07, -28.78) * mm, "end": v(-15.9, -28.72) * mm});
            skLineSegment(sketch, "E456", {"start": v(-15.9, -28.72) * mm, "end": v(-15.75, -28.63) * mm});
            skLineSegment(sketch, "E457", {"start": v(-15.75, -28.63) * mm, "end": v(-15.61, -28.52) * mm});
            skLineSegment(sketch, "E458", {"start": v(-15.61, -28.52) * mm, "end": v(-11.94, -24.92) * mm});
            skLineSegment(sketch, "E459", {"start": v(-11.94, -24.92) * mm, "end": v(-11.2, -23.9) * mm});
            skLineSegment(sketch, "E460", {"start": v(-11.2, -23.9) * mm, "end": v(-11.17, -23.86) * mm});
            skLineSegment(sketch, "E461", {"start": v(-11.17, -23.86) * mm, "end": v(-11.15, -23.81) * mm});
            skLineSegment(sketch, "E462", {"start": v(-11.15, -23.81) * mm, "end": v(-11.13, -23.76) * mm});
            skLineSegment(sketch, "E463", {"start": v(-11.13, -23.76) * mm, "end": v(-11.11, -23.71) * mm});
            skLineSegment(sketch, "E464", {"start": v(-11.11, -23.71) * mm, "end": v(-11.1, -23.66) * mm});
            skLineSegment(sketch, "E465", {"start": v(-11.1, -23.66) * mm, "end": v(-11.1, -23.61) * mm});
            skLineSegment(sketch, "E466", {"start": v(-11.1, -23.61) * mm, "end": v(-11.1, -23.56) * mm});
            skLineSegment(sketch, "E467", {"start": v(-11.1, -23.56) * mm, "end": v(-11.14, -23.3) * mm});
            skLineSegment(sketch, "E468", {"start": v(-11.14, -23.3) * mm, "end": v(-11.15, -23.1) * mm});
            skLineSegment(sketch, "E469", {"start": v(-11.15, -23.1) * mm, "end": v(-11.14, -22.9) * mm});
            skLineSegment(sketch, "E470", {"start": v(-11.14, -22.9) * mm, "end": v(-11.1, -22.7) * mm});
            skLineSegment(sketch, "E471", {"start": v(-11.1, -22.7) * mm, "end": v(-11.05, -22.5) * mm});
            skLineSegment(sketch, "E472", {"start": v(-11.05, -22.5) * mm, "end": v(-10.97, -22.3) * mm});
            skLineSegment(sketch, "E473", {"start": v(-10.97, -22.3) * mm, "end": v(-10.88, -22.12) * mm});
            skLineSegment(sketch, "E474", {"start": v(-10.88, -22.12) * mm, "end": v(-10.77, -21.95) * mm});
            skLineSegment(sketch, "E475", {"start": v(-10.77, -21.95) * mm, "end": v(-10.64, -21.78) * mm});
            skLineSegment(sketch, "E476", {"start": v(-10.64, -21.78) * mm, "end": v(-10.5, -21.64) * mm});
            skLineSegment(sketch, "E477", {"start": v(-10.5, -21.64) * mm, "end": v(-10.33, -21.51) * mm});
            skLineSegment(sketch, "E478", {"start": v(-10.33, -21.51) * mm, "end": v(-10.16, -21.4) * mm});
            skLineSegment(sketch, "E479", {"start": v(-10.16, -21.4) * mm, "end": v(-9.98, -21.3) * mm});
            skLineSegment(sketch, "E480", {"start": v(-9.98, -21.3) * mm, "end": v(-9.79, -21.23) * mm});
            skLineSegment(sketch, "E481", {"start": v(-9.79, -21.23) * mm, "end": v(-9.6, -21.17) * mm});
            skLineSegment(sketch, "E482", {"start": v(-9.6, -21.17) * mm, "end": v(-9.34, -21.13) * mm});
            skLineSegment(sketch, "E483", {"start": v(-9.34, -21.13) * mm, "end": v(-9.29, -21.11) * mm});
            skLineSegment(sketch, "E484", {"start": v(-9.29, -21.11) * mm, "end": v(-9.24, -21.1) * mm});
            skLineSegment(sketch, "E485", {"start": v(-9.24, -21.1) * mm, "end": v(-9.2, -21.07) * mm});
            skLineSegment(sketch, "E486", {"start": v(-9.2, -21.07) * mm, "end": v(-9.15, -21.04) * mm});
            skLineSegment(sketch, "E487", {"start": v(-9.15, -21.04) * mm, "end": v(-9.11, -21.01) * mm});
            skLineSegment(sketch, "E488", {"start": v(-9.11, -21.01) * mm, "end": v(-9.07, -20.97) * mm});
            skLineSegment(sketch, "E489", {"start": v(-9.07, -20.97) * mm, "end": v(-9.04, -20.93) * mm});
            skLineSegment(sketch, "E490", {"start": v(-9.04, -20.93) * mm, "end": v(-6.75, -17.8) * mm});
            skLineSegment(sketch, "E491", {"start": v(-6.75, -17.8) * mm, "end": v(-6.7, -17.7) * mm});
            skLineSegment(sketch, "E492", {"start": v(-6.7, -17.7) * mm, "end": v(-6.67, -17.6) * mm});
            skLineSegment(sketch, "E493", {"start": v(-6.67, -17.6) * mm, "end": v(-6.66, -17.52) * mm});
            skLineSegment(sketch, "E494", {"start": v(-6.66, -17.52) * mm, "end": v(-6.66, -17.02) * mm});
            skLineSegment(sketch, "E495", {"start": v(-6.66, -17.02) * mm, "end": v(-6.65, -16.9) * mm});
            skLineSegment(sketch, "E496", {"start": v(-6.65, -16.9) * mm, "end": v(-6.62, -16.8) * mm});
            skLineSegment(sketch, "E497", {"start": v(-6.62, -16.8) * mm, "end": v(-6.58, -16.72) * mm});
            skLineSegment(sketch, "E498", {"start": v(-6.58, -16.72) * mm, "end": v(-6.52, -16.65) * mm});
            skLineSegment(sketch, "E499", {"start": v(-6.52, -16.65) * mm, "end": v(-6.44, -16.59) * mm});
            skLineSegment(sketch, "E500", {"start": v(-6.44, -16.59) * mm, "end": v(-6.36, -16.54) * mm});
            skLineSegment(sketch, "E501", {"start": v(-6.36, -16.54) * mm, "end": v(-6.26, -16.51) * mm});
            skLineSegment(sketch, "E502", {"start": v(-6.26, -16.51) * mm, "end": v(-6.18, -16.5) * mm});
            skLineSegment(sketch, "E503", {"start": v(-6.18, -16.5) * mm, "end": v(-4.7, -16.5) * mm});
            skLineSegment(sketch, "E504", {"start": v(-4.7, -16.5) * mm, "end": v(-4.7, -16.5) * mm});
            skLineSegment(sketch, "E505", {"start": v(-4.7, -16.5) * mm, "end": v(-4.6, -16.51) * mm});
            skLineSegment(sketch, "E506", {"start": v(-4.6, -16.51) * mm, "end": v(-4.51, -16.54) * mm});
            skLineSegment(sketch, "E507", {"start": v(-4.51, -16.54) * mm, "end": v(-4.43, -16.59) * mm});
            skLineSegment(sketch, "E508", {"start": v(-4.43, -16.59) * mm, "end": v(-4.35, -16.65) * mm});
            skLineSegment(sketch, "E509", {"start": v(-4.35, -16.65) * mm, "end": v(-4.3, -16.72) * mm});
            skLineSegment(sketch, "E510", {"start": v(-4.3, -16.72) * mm, "end": v(-4.24, -16.8) * mm});
            skLineSegment(sketch, "E511", {"start": v(-4.24, -16.8) * mm, "end": v(-4.21, -16.9) * mm});
            skLineSegment(sketch, "E512", {"start": v(-4.21, -16.9) * mm, "end": v(-4.2, -17.05) * mm});
            skLineSegment(sketch, "E513", {"start": v(-4.2, -17.05) * mm, "end": v(-4.2, -17.37) * mm});
            skLineSegment(sketch, "E514", {"start": v(-4.2, -17.37) * mm, "end": v(-4.2, -17.5) * mm});
            skLineSegment(sketch, "E515", {"start": v(-4.2, -17.5) * mm, "end": v(-4.17, -17.59) * mm});
            skLineSegment(sketch, "E516", {"start": v(-4.17, -17.59) * mm, "end": v(-4.12, -17.67) * mm});
            skLineSegment(sketch, "E517", {"start": v(-4.12, -17.67) * mm, "end": v(-4.06, -17.75) * mm});
            skLineSegment(sketch, "E518", {"start": v(-4.06, -17.75) * mm, "end": v(-3.99, -17.8) * mm});
            skLineSegment(sketch, "E519", {"start": v(-3.99, -17.8) * mm, "end": v(-3.9, -17.85) * mm});
            skLineSegment(sketch, "E520", {"start": v(-3.9, -17.85) * mm, "end": v(-3.8, -17.88) * mm});
            skLineSegment(sketch, "E521", {"start": v(-3.8, -17.88) * mm, "end": v(-3.7, -17.9) * mm});
            skLineSegment(sketch, "E522", {"start": v(-3.7, -17.9) * mm, "end": v(3.71, -17.9) * mm});
            skLineSegment(sketch, "E523", {"start": v(3.71, -17.9) * mm, "end": v(3.81, -17.89) * mm});
            skLineSegment(sketch, "E524", {"start": v(3.81, -17.89) * mm, "end": v(3.9, -17.86) * mm});
            skLineSegment(sketch, "E525", {"start": v(3.9, -17.86) * mm, "end": v(4, -17.81) * mm});
            skLineSegment(sketch, "E526", {"start": v(4, -17.81) * mm, "end": v(4.06, -17.75) * mm});
            skLineSegment(sketch, "E527", {"start": v(4.06, -17.75) * mm, "end": v(4.13, -17.68) * mm});
            skLineSegment(sketch, "E528", {"start": v(4.13, -17.68) * mm, "end": v(4.17, -17.6) * mm});
            skLineSegment(sketch, "E529", {"start": v(4.17, -17.6) * mm, "end": v(4.2, -17.5) * mm});
            skLineSegment(sketch, "E530", {"start": v(4.2, -17.5) * mm, "end": v(4.21, -17.37) * mm});
            skLineSegment(sketch, "E531", {"start": v(4.21, -17.37) * mm, "end": v(4.21, -17) * mm});
            skLineSegment(sketch, "E532", {"start": v(4.21, -17) * mm, "end": v(4.22, -16.9) * mm});
            skLineSegment(sketch, "E533", {"start": v(4.22, -16.9) * mm, "end": v(4.25, -16.8) * mm});
            skLineSegment(sketch, "E534", {"start": v(4.25, -16.8) * mm, "end": v(4.3, -16.72) * mm});
            skLineSegment(sketch, "E535", {"start": v(4.3, -16.72) * mm, "end": v(4.36, -16.64) * mm});
            skLineSegment(sketch, "E536", {"start": v(4.36, -16.64) * mm, "end": v(4.43, -16.58) * mm});
            skLineSegment(sketch, "E537", {"start": v(4.43, -16.58) * mm, "end": v(4.52, -16.54) * mm});
            skLineSegment(sketch, "E538", {"start": v(4.52, -16.54) * mm, "end": v(4.6, -16.5) * mm});
            skLineSegment(sketch, "E539", {"start": v(4.6, -16.5) * mm, "end": v(4.71, -16.5) * mm});
            skLineSegment(sketch, "E540", {"start": v(4.71, -16.5) * mm, "end": v(4.71, -16.5) * mm});
            skLineSegment(sketch, "E541", {"start": v(4.71, -16.5) * mm, "end": v(6.16, -16.5) * mm});
            skLineSegment(sketch, "E542", {"start": v(6.16, -16.5) * mm, "end": v(6.16, -16.5) * mm});
            skLineSegment(sketch, "E543", {"start": v(6.16, -16.5) * mm, "end": v(6.26, -16.5) * mm});
            skLineSegment(sketch, "E544", {"start": v(6.26, -16.5) * mm, "end": v(6.35, -16.54) * mm});
            skLineSegment(sketch, "E545", {"start": v(6.35, -16.54) * mm, "end": v(6.44, -16.58) * mm});
            skLineSegment(sketch, "E546", {"start": v(6.44, -16.58) * mm, "end": v(6.51, -16.64) * mm});
            skLineSegment(sketch, "E547", {"start": v(6.51, -16.64) * mm, "end": v(6.57, -16.72) * mm});
            skLineSegment(sketch, "E548", {"start": v(6.57, -16.72) * mm, "end": v(6.62, -16.8) * mm});
            skLineSegment(sketch, "E549", {"start": v(6.62, -16.8) * mm, "end": v(6.65, -16.9) * mm});
            skLineSegment(sketch, "E550", {"start": v(6.65, -16.9) * mm, "end": v(6.66, -17) * mm});
            skLineSegment(sketch, "E551", {"start": v(6.66, -17) * mm, "end": v(6.66, -17) * mm});
            skLineSegment(sketch, "E552", {"start": v(6.66, -17) * mm, "end": v(6.66, -17.52) * mm});
            skLineSegment(sketch, "E553", {"start": v(6.66, -17.52) * mm, "end": v(6.67, -17.6) * mm});
            skLineSegment(sketch, "E554", {"start": v(6.67, -17.6) * mm, "end": v(6.7, -17.7) * mm});
            skLineSegment(sketch, "E555", {"start": v(6.7, -17.7) * mm, "end": v(6.75, -17.79) * mm});
            skLineSegment(sketch, "E556", {"start": v(6.75, -17.79) * mm, "end": v(6.76, -17.8) * mm});
            skLineSegment(sketch, "E557", {"start": v(6.76, -17.8) * mm, "end": v(9.04, -20.93) * mm});
            skLineSegment(sketch, "E558", {"start": v(9.04, -20.93) * mm, "end": v(9.07, -20.97) * mm});
            skLineSegment(sketch, "E559", {"start": v(9.07, -20.97) * mm, "end": v(9.1, -21) * mm});
            skLineSegment(sketch, "E560", {"start": v(9.1, -21) * mm, "end": v(9.15, -21.04) * mm});
            skLineSegment(sketch, "E561", {"start": v(9.15, -21.04) * mm, "end": v(9.2, -21.07) * mm});
            skLineSegment(sketch, "E562", {"start": v(9.2, -21.07) * mm, "end": v(9.24, -21.1) * mm});
            skLineSegment(sketch, "E563", {"start": v(9.24, -21.1) * mm, "end": v(9.29, -21.1) * mm});
            skLineSegment(sketch, "E564", {"start": v(9.29, -21.1) * mm, "end": v(9.33, -21.12) * mm});
            skLineSegment(sketch, "E565", {"start": v(9.33, -21.12) * mm, "end": v(9.59, -21.17) * mm});
            skLineSegment(sketch, "E566", {"start": v(9.59, -21.17) * mm, "end": v(9.79, -21.22) * mm});
            skLineSegment(sketch, "E567", {"start": v(9.79, -21.22) * mm, "end": v(9.98, -21.3) * mm});
            skLineSegment(sketch, "E568", {"start": v(9.98, -21.3) * mm, "end": v(10.16, -21.4) * mm});
            skLineSegment(sketch, "E569", {"start": v(10.16, -21.4) * mm, "end": v(10.33, -21.5) * mm});
            skLineSegment(sketch, "E570", {"start": v(10.33, -21.5) * mm, "end": v(10.49, -21.64) * mm});
            skLineSegment(sketch, "E571", {"start": v(10.49, -21.64) * mm, "end": v(10.63, -21.78) * mm});
            skLineSegment(sketch, "E572", {"start": v(10.63, -21.78) * mm, "end": v(10.77, -21.94) * mm});
            skLineSegment(sketch, "E573", {"start": v(10.77, -21.94) * mm, "end": v(10.88, -22.12) * mm});
            skLineSegment(sketch, "E574", {"start": v(10.88, -22.12) * mm, "end": v(10.97, -22.3) * mm});
            skLineSegment(sketch, "E575", {"start": v(10.97, -22.3) * mm, "end": v(11.05, -22.5) * mm});
            skLineSegment(sketch, "E576", {"start": v(11.05, -22.5) * mm, "end": v(11.1, -22.69) * mm});
            skLineSegment(sketch, "E577", {"start": v(11.1, -22.69) * mm, "end": v(11.13, -22.89) * mm});
            skLineSegment(sketch, "E578", {"start": v(11.13, -22.89) * mm, "end": v(11.15, -23.1) * mm});
            skLineSegment(sketch, "E579", {"start": v(11.15, -23.1) * mm, "end": v(11.14, -23.3) * mm});
            skLineSegment(sketch, "E580", {"start": v(11.14, -23.3) * mm, "end": v(11.1, -23.56) * mm});
            skLineSegment(sketch, "E581", {"start": v(11.1, -23.56) * mm, "end": v(11.1, -23.6) * mm});
            skLineSegment(sketch, "E582", {"start": v(11.1, -23.6) * mm, "end": v(11.1, -23.66) * mm});
            skLineSegment(sketch, "E583", {"start": v(11.1, -23.66) * mm, "end": v(11.11, -23.7) * mm});
            skLineSegment(sketch, "E584", {"start": v(11.11, -23.7) * mm, "end": v(11.13, -23.76) * mm});
            skLineSegment(sketch, "E585", {"start": v(11.13, -23.76) * mm, "end": v(11.14, -23.8) * mm});
            skLineSegment(sketch, "E586", {"start": v(11.14, -23.8) * mm, "end": v(11.17, -23.85) * mm});
            skLineSegment(sketch, "E587", {"start": v(11.17, -23.85) * mm, "end": v(11.2, -23.9) * mm});
            skLineSegment(sketch, "E588", {"start": v(11.2, -23.9) * mm, "end": v(11.94, -24.92) * mm});
            skLineSegment(sketch, "E589", {"start": v(11.94, -24.92) * mm, "end": v(15.61, -28.51) * mm});
            skLineSegment(sketch, "E590", {"start": v(15.61, -28.51) * mm, "end": v(15.75, -28.63) * mm});
            skLineSegment(sketch, "E591", {"start": v(15.75, -28.63) * mm, "end": v(15.9, -28.71) * mm});
            skLineSegment(sketch, "E592", {"start": v(15.9, -28.71) * mm, "end": v(16.07, -28.77) * mm});
            skLineSegment(sketch, "E593", {"start": v(16.07, -28.77) * mm, "end": v(16.24, -28.8) * mm});
            skLineSegment(sketch, "E594", {"start": v(16.24, -28.8) * mm, "end": v(16.41, -28.8) * mm});
            skLineSegment(sketch, "E595", {"start": v(16.41, -28.8) * mm, "end": v(16.58, -28.76) * mm});
            skLineSegment(sketch, "E596", {"start": v(16.58, -28.76) * mm, "end": v(16.75, -28.7) * mm});
            skLineSegment(sketch, "E597", {"start": v(16.75, -28.7) * mm, "end": v(16.9, -28.6) * mm});
            skLineSegment(sketch, "E598", {"start": v(16.9, -28.6) * mm, "end": v(19.74, -26.55) * mm});
            skLineSegment(sketch, "E599", {"start": v(19.74, -26.55) * mm, "end": v(19.88, -26.43) * mm});
            skLineSegment(sketch, "E600", {"start": v(19.88, -26.43) * mm, "end": v(19.99, -26.3) * mm});
            skLineSegment(sketch, "E601", {"start": v(19.99, -26.3) * mm, "end": v(20.07, -26.14) * mm});
            skLineSegment(sketch, "E602", {"start": v(20.07, -26.14) * mm, "end": v(20.12, -25.97) * mm});
            skLineSegment(sketch, "E603", {"start": v(20.12, -25.97) * mm, "end": v(20.15, -25.8) * mm});
            skLineSegment(sketch, "E604", {"start": v(20.15, -25.8) * mm, "end": v(20.15, -25.63) * mm});
            skLineSegment(sketch, "E605", {"start": v(20.15, -25.63) * mm, "end": v(20.11, -25.46) * mm});
            skLineSegment(sketch, "E606", {"start": v(20.11, -25.46) * mm, "end": v(20.05, -25.3) * mm});
            skLineSegment(sketch, "E607", {"start": v(20.05, -25.3) * mm, "end": v(17.76, -20.69) * mm});
            skLineSegment(sketch, "E608", {"start": v(17.76, -20.69) * mm, "end": v(17.02, -19.66) * mm});
            skLineSegment(sketch, "E609", {"start": v(17.02, -19.66) * mm, "end": v(16.99, -19.62) * mm});
            skLineSegment(sketch, "E610", {"start": v(16.99, -19.62) * mm, "end": v(16.95, -19.59) * mm});
            skLineSegment(sketch, "E611", {"start": v(16.95, -19.59) * mm, "end": v(16.91, -19.55) * mm});
            skLineSegment(sketch, "E612", {"start": v(16.91, -19.55) * mm, "end": v(16.87, -19.53) * mm});
            skLineSegment(sketch, "E613", {"start": v(16.87, -19.53) * mm, "end": v(16.82, -19.5) * mm});
            skLineSegment(sketch, "E614", {"start": v(16.82, -19.5) * mm, "end": v(16.78, -19.48) * mm});
            skLineSegment(sketch, "E615", {"start": v(16.78, -19.48) * mm, "end": v(16.73, -19.47) * mm});
            skLineSegment(sketch, "E616", {"start": v(16.73, -19.47) * mm, "end": v(16.47, -19.42) * mm});
            skLineSegment(sketch, "E617", {"start": v(16.47, -19.42) * mm, "end": v(16.27, -19.37) * mm});
            skLineSegment(sketch, "E618", {"start": v(16.27, -19.37) * mm, "end": v(16.08, -19.3) * mm});
            skLineSegment(sketch, "E619", {"start": v(16.08, -19.3) * mm, "end": v(15.9, -19.2) * mm});
            skLineSegment(sketch, "E620", {"start": v(15.9, -19.2) * mm, "end": v(15.73, -19.09) * mm});
            skLineSegment(sketch, "E621", {"start": v(15.73, -19.09) * mm, "end": v(15.57, -18.96) * mm});
            skLineSegment(sketch, "E622", {"start": v(15.57, -18.96) * mm, "end": v(15.43, -18.81) * mm});
            skLineSegment(sketch, "E623", {"start": v(15.43, -18.81) * mm, "end": v(15.3, -18.65) * mm});
            skLineSegment(sketch, "E624", {"start": v(15.3, -18.65) * mm, "end": v(15.18, -18.48) * mm});
            skLineSegment(sketch, "E625", {"start": v(15.18, -18.48) * mm, "end": v(15.09, -18.3) * mm});
            skLineSegment(sketch, "E626", {"start": v(15.09, -18.3) * mm, "end": v(15.01, -18.1) * mm});
            skLineSegment(sketch, "E627", {"start": v(15.01, -18.1) * mm, "end": v(14.96, -17.9) * mm});
            skLineSegment(sketch, "E628", {"start": v(14.96, -17.9) * mm, "end": v(14.93, -17.7) * mm});
            skLineSegment(sketch, "E629", {"start": v(14.93, -17.7) * mm, "end": v(14.91, -17.5) * mm});
            skLineSegment(sketch, "E630", {"start": v(14.91, -17.5) * mm, "end": v(14.92, -17.3) * mm});
            skLineSegment(sketch, "E631", {"start": v(14.92, -17.3) * mm, "end": v(14.96, -17.04) * mm});
            skLineSegment(sketch, "E632", {"start": v(14.96, -17.04) * mm, "end": v(14.96, -16.98) * mm});
            skLineSegment(sketch, "E633", {"start": v(14.96, -16.98) * mm, "end": v(14.96, -16.93) * mm});
            skLineSegment(sketch, "E634", {"start": v(14.96, -16.93) * mm, "end": v(14.95, -16.88) * mm});
            skLineSegment(sketch, "E635", {"start": v(14.95, -16.88) * mm, "end": v(14.94, -16.83) * mm});
            skLineSegment(sketch, "E636", {"start": v(14.94, -16.83) * mm, "end": v(14.92, -16.79) * mm});
            skLineSegment(sketch, "E637", {"start": v(14.92, -16.79) * mm, "end": v(14.9, -16.74) * mm});
            skLineSegment(sketch, "E638", {"start": v(14.9, -16.74) * mm, "end": v(14.87, -16.7) * mm});
            skLineSegment(sketch, "E639", {"start": v(14.87, -16.7) * mm, "end": v(11.63, -12.24) * mm});
            skLineSegment(sketch, "E640", {"start": v(11.63, -12.24) * mm, "end": v(11.6, -12.2) * mm});
            skLineSegment(sketch, "E641", {"start": v(11.6, -12.2) * mm, "end": v(11.6, -12.16) * mm});
            skLineSegment(sketch, "E642", {"start": v(11.6, -12.16) * mm, "end": v(11.58, -12.13) * mm});
            skLineSegment(sketch, "E643", {"start": v(11.58, -12.13) * mm, "end": v(11.57, -12.1) * mm});
            skLineSegment(sketch, "E644", {"start": v(11.57, -12.1) * mm, "end": v(11.57, -12.06) * mm});
            skLineSegment(sketch, "E645", {"start": v(11.57, -12.06) * mm, "end": v(11.57, -12.04) * mm});
            skLineSegment(sketch, "E646", {"start": v(11.57, -12.04) * mm, "end": v(11.57, -12) * mm});
            skLineSegment(sketch, "E647", {"start": v(11.57, -12) * mm, "end": v(11.57, -11.96) * mm});
            skLineSegment(sketch, "E648", {"start": v(11.57, -11.96) * mm, "end": v(11.58, -11.93) * mm});
            skLineSegment(sketch, "E649", {"start": v(11.58, -11.93) * mm, "end": v(11.6, -11.9) * mm});
            skLineSegment(sketch, "E650", {"start": v(11.6, -11.9) * mm, "end": v(11.6, -11.87) * mm});
            skLineSegment(sketch, "E651", {"start": v(11.6, -11.87) * mm, "end": v(11.63, -11.84) * mm});
            skLineSegment(sketch, "E652", {"start": v(11.63, -11.84) * mm, "end": v(11.65, -11.81) * mm});
            skLineSegment(sketch, "E653", {"start": v(11.65, -11.81) * mm, "end": v(11.67, -11.78) * mm});
            skLineSegment(sketch, "E654", {"start": v(11.67, -11.78) * mm, "end": v(12.41, -10.79) * mm});
            skLineSegment(sketch, "E655", {"start": v(12.41, -10.79) * mm, "end": v(13.07, -9.73) * mm});
            skLineSegment(sketch, "E656", {"start": v(13.07, -9.73) * mm, "end": v(13.64, -8.61) * mm});
            skLineSegment(sketch, "E657", {"start": v(13.64, -8.61) * mm, "end": v(14.12, -7.45) * mm});
            skLineSegment(sketch, "E658", {"start": v(14.12, -7.45) * mm, "end": v(14.5, -6.23) * mm});
            skLineSegment(sketch, "E659", {"start": v(14.5, -6.23) * mm, "end": v(14.77, -4.98) * mm});
            skLineSegment(sketch, "E660", {"start": v(14.77, -4.98) * mm, "end": v(14.94, -3.69) * mm});
            skLineSegment(sketch, "E661", {"start": v(14.94, -3.69) * mm, "end": v(15, -2.36) * mm});
            skLineSegment(sketch, "E662", {"start": v(15, -2.36) * mm, "end": v(15, -2) * mm});
            skLineSegment(sketch, "E663", {"start": v(15, -2) * mm, "end": v(14.98, -1.58) * mm});
            skLineSegment(sketch, "E664", {"start": v(14.98, -1.58) * mm, "end": v(14.98, -1.55) * mm});
            skLineSegment(sketch, "E665", {"start": v(14.98, -1.55) * mm, "end": v(14.98, -1.5) * mm});
            skLineSegment(sketch, "E666", {"start": v(14.98, -1.5) * mm, "end": v(14.99, -1.47) * mm});
            skLineSegment(sketch, "E667", {"start": v(14.99, -1.47) * mm, "end": v(15, -1.43) * mm});
            skLineSegment(sketch, "E668", {"start": v(15, -1.43) * mm, "end": v(15, -1.4) * mm});
            skLineSegment(sketch, "E669", {"start": v(15, -1.4) * mm, "end": v(15.02, -1.36) * mm});
            skLineSegment(sketch, "E670", {"start": v(15.02, -1.36) * mm, "end": v(15.04, -1.33) * mm});
            skLineSegment(sketch, "E671", {"start": v(15.04, -1.33) * mm, "end": v(15.06, -1.3) * mm});
            skLineSegment(sketch, "E672", {"start": v(15.06, -1.3) * mm, "end": v(15.1, -1.28) * mm});
            skLineSegment(sketch, "E673", {"start": v(15.1, -1.28) * mm, "end": v(15.12, -1.26) * mm});
            skLineSegment(sketch, "E674", {"start": v(15.12, -1.26) * mm, "end": v(15.15, -1.24) * mm});
            skLineSegment(sketch, "E675", {"start": v(15.15, -1.24) * mm, "end": v(15.18, -1.22) * mm});
            skLineSegment(sketch, "E676", {"start": v(15.18, -1.22) * mm, "end": v(15.2, -1.21) * mm});
            skLineSegment(sketch, "E677", {"start": v(15.2, -1.21) * mm, "end": v(15.23, -1.2) * mm});
            skLineSegment(sketch, "E678", {"start": v(15.23, -1.2) * mm, "end": v(20.45, 0.5) * mm});
            skLineSegment(sketch, "E679", {"start": v(20.45, 0.5) * mm, "end": v(20.5, 0.52) * mm});
            skLineSegment(sketch, "E680", {"start": v(20.5, 0.52) * mm, "end": v(20.54, 0.54) * mm});
            skLineSegment(sketch, "E681", {"start": v(20.54, 0.54) * mm, "end": v(20.59, 0.57) * mm});
            skLineSegment(sketch, "E682", {"start": v(20.59, 0.57) * mm, "end": v(20.63, 0.6) * mm});
            skLineSegment(sketch, "E683", {"start": v(20.63, 0.6) * mm, "end": v(20.66, 0.63) * mm});
            skLineSegment(sketch, "E684", {"start": v(20.66, 0.63) * mm, "end": v(20.7, 0.67) * mm});
            skLineSegment(sketch, "E685", {"start": v(20.7, 0.67) * mm, "end": v(20.73, 0.72) * mm});
            skLineSegment(sketch, "E686", {"start": v(20.73, 0.72) * mm, "end": v(20.85, 0.95) * mm});
            skLineSegment(sketch, "E687", {"start": v(20.85, 0.95) * mm, "end": v(20.96, 1.12) * mm});
            skLineSegment(sketch, "E688", {"start": v(20.96, 1.12) * mm, "end": v(21.1, 1.27) * mm});
            skLineSegment(sketch, "E689", {"start": v(21.1, 1.27) * mm, "end": v(21.24, 1.42) * mm});
            skLineSegment(sketch, "E690", {"start": v(21.24, 1.42) * mm, "end": v(21.4, 1.55) * mm});
            skLineSegment(sketch, "E691", {"start": v(21.4, 1.55) * mm, "end": v(21.57, 1.66) * mm});
            skLineSegment(sketch, "E692", {"start": v(21.57, 1.66) * mm, "end": v(21.75, 1.75) * mm});
            skLineSegment(sketch, "E693", {"start": v(21.75, 1.75) * mm, "end": v(21.95, 1.82) * mm});
            skLineSegment(sketch, "E694", {"start": v(21.95, 1.82) * mm, "end": v(22.15, 1.88) * mm});
            skLineSegment(sketch, "E695", {"start": v(22.15, 1.88) * mm, "end": v(22.35, 1.91) * mm});
            skLineSegment(sketch, "E696", {"start": v(22.35, 1.91) * mm, "end": v(22.55, 1.92) * mm});
            skLineSegment(sketch, "E697", {"start": v(22.55, 1.92) * mm, "end": v(22.76, 1.91) * mm});
            skLineSegment(sketch, "E698", {"start": v(22.76, 1.91) * mm, "end": v(22.96, 1.88) * mm});
            skLineSegment(sketch, "E699", {"start": v(22.96, 1.88) * mm, "end": v(23.16, 1.83) * mm});
            skLineSegment(sketch, "E700", {"start": v(23.16, 1.83) * mm, "end": v(23.35, 1.76) * mm});
            skLineSegment(sketch, "E701", {"start": v(23.35, 1.76) * mm, "end": v(23.59, 1.65) * mm});
            skLineSegment(sketch, "E702", {"start": v(23.59, 1.65) * mm, "end": v(23.63, 1.63) * mm});
            skLineSegment(sketch, "E703", {"start": v(23.63, 1.63) * mm, "end": v(23.68, 1.61) * mm});
            skLineSegment(sketch, "E704", {"start": v(23.68, 1.61) * mm, "end": v(23.73, 1.6) * mm});
            skLineSegment(sketch, "E705", {"start": v(23.73, 1.6) * mm, "end": v(23.79, 1.6) * mm});
            skLineSegment(sketch, "E706", {"start": v(23.79, 1.6) * mm, "end": v(23.84, 1.6) * mm});
            skLineSegment(sketch, "E707", {"start": v(23.84, 1.6) * mm, "end": v(23.89, 1.62) * mm});
            skLineSegment(sketch, "E708", {"start": v(23.89, 1.62) * mm, "end": v(23.94, 1.63) * mm});
            skLineSegment(sketch, "E709", {"start": v(23.94, 1.63) * mm, "end": v(25.14, 2.02) * mm});
            skLineSegment(sketch, "E710", {"start": v(25.14, 2.02) * mm, "end": v(29.7, 4.4) * mm});
            skLineSegment(sketch, "E711", {"start": v(29.7, 4.4) * mm, "end": v(29.85, 4.5) * mm});
            skLineSegment(sketch, "E712", {"start": v(29.85, 4.5) * mm, "end": v(29.98, 4.62) * mm});
            skLineSegment(sketch, "E713", {"start": v(29.98, 4.62) * mm, "end": v(30.08, 4.76) * mm});
            skLineSegment(sketch, "E714", {"start": v(30.08, 4.76) * mm, "end": v(30.16, 4.91) * mm});
            skLineSegment(sketch, "E715", {"start": v(30.16, 4.91) * mm, "end": v(30.2, 5.08) * mm});
            skLineSegment(sketch, "E716", {"start": v(30.2, 5.08) * mm, "end": v(30.23, 5.25) * mm});
            skLineSegment(sketch, "E717", {"start": v(30.23, 5.25) * mm, "end": v(30.22, 5.42) * mm});
            skLineSegment(sketch, "E718", {"start": v(-6.23, -2.28) * mm, "end": v(-6.23, -1.51) * mm});
            skArc(sketch, "E719", {"start": v(-6.23, -1.51) * mm, "mid": v(-6.26, -1.45) * mm, "end": v(-6.31, -1.43) * mm});
            skLineSegment(sketch, "E720", {"start": v(-6.31, -1.43) * mm, "end": v(-7.19, -1.43) * mm});
            skArc(sketch, "E721", {"start": v(-7.19, -1.43) * mm, "mid": v(-7.24, -1.45) * mm, "end": v(-7.27, -1.51) * mm});
            skLineSegment(sketch, "E722", {"start": v(-7.27, -1.51) * mm, "end": v(-7.27, -2.28) * mm});
            skArc(sketch, "E723", {"start": v(-7.27, -2.28) * mm, "mid": v(-7.24, -2.34) * mm, "end": v(-7.19, -2.37) * mm});
            skLineSegment(sketch, "E724", {"start": v(-7.19, -2.37) * mm, "end": v(-6.31, -2.37) * mm});
            skArc(sketch, "E725", {"start": v(-6.31, -2.37) * mm, "mid": v(-6.26, -2.34) * mm, "end": v(-6.23, -2.28) * mm});
            skLineSegment(sketch, "E726", {"start": v(-4.53, -2.28) * mm, "end": v(-4.53, -1.51) * mm});
            skArc(sketch, "E727", {"start": v(-4.53, -1.51) * mm, "mid": v(-4.56, -1.45) * mm, "end": v(-4.61, -1.43) * mm});
            skLineSegment(sketch, "E728", {"start": v(-4.61, -1.43) * mm, "end": v(-5.49, -1.43) * mm});
            skArc(sketch, "E729", {"start": v(-5.49, -1.43) * mm, "mid": v(-5.54, -1.45) * mm, "end": v(-5.57, -1.51) * mm});
            skLineSegment(sketch, "E730", {"start": v(-5.57, -1.51) * mm, "end": v(-5.57, -2.28) * mm});
            skArc(sketch, "E731", {"start": v(-5.57, -2.28) * mm, "mid": v(-5.54, -2.34) * mm, "end": v(-5.49, -2.37) * mm});
            skLineSegment(sketch, "E732", {"start": v(-5.49, -2.37) * mm, "end": v(-4.61, -2.37) * mm});
            skArc(sketch, "E733", {"start": v(-4.61, -2.37) * mm, "mid": v(-4.56, -2.34) * mm, "end": v(-4.53, -2.28) * mm});
            skLineSegment(sketch, "E734", {"start": v(-6.27, 1.37) * mm, "end": v(-6.27, 2.14) * mm});
            skArc(sketch, "E735", {"start": v(-6.27, 2.14) * mm, "mid": v(-6.3, 2.2) * mm, "end": v(-6.35, 2.22) * mm});
            skLineSegment(sketch, "E736", {"start": v(-6.35, 2.22) * mm, "end": v(-7.23, 2.22) * mm});
            skArc(sketch, "E737", {"start": v(-7.23, 2.22) * mm, "mid": v(-7.28, 2.2) * mm, "end": v(-7.3, 2.14) * mm});
            skLineSegment(sketch, "E738", {"start": v(-7.3, 2.14) * mm, "end": v(-7.3, 1.37) * mm});
            skArc(sketch, "E739", {"start": v(-7.3, 1.37) * mm, "mid": v(-7.28, 1.3) * mm, "end": v(-7.23, 1.28) * mm});
            skLineSegment(sketch, "E740", {"start": v(-7.23, 1.28) * mm, "end": v(-6.35, 1.28) * mm});
            skArc(sketch, "E741", {"start": v(-6.35, 1.28) * mm, "mid": v(-6.3, 1.3) * mm, "end": v(-6.27, 1.37) * mm});
            skLineSegment(sketch, "E742", {"start": v(-4.57, 1.37) * mm, "end": v(-4.57, 2.14) * mm});
            skArc(sketch, "E743", {"start": v(-4.57, 2.14) * mm, "mid": v(-4.6, 2.2) * mm, "end": v(-4.65, 2.22) * mm});
            skLineSegment(sketch, "E744", {"start": v(-4.65, 2.22) * mm, "end": v(-5.53, 2.22) * mm});
            skArc(sketch, "E745", {"start": v(-5.53, 2.22) * mm, "mid": v(-5.58, 2.2) * mm, "end": v(-5.6, 2.14) * mm});
            skLineSegment(sketch, "E746", {"start": v(-5.6, 2.14) * mm, "end": v(-5.6, 1.37) * mm});
            skArc(sketch, "E747", {"start": v(-5.6, 1.37) * mm, "mid": v(-5.58, 1.3) * mm, "end": v(-5.53, 1.28) * mm});
            skLineSegment(sketch, "E748", {"start": v(-5.53, 1.28) * mm, "end": v(-4.65, 1.28) * mm});
            skArc(sketch, "E749", {"start": v(-4.65, 1.28) * mm, "mid": v(-4.6, 1.3) * mm, "end": v(-4.57, 1.37) * mm});
            skLineSegment(sketch, "E750", {"start": v(8.02, -5.3) * mm, "end": v(8.02, -6.07) * mm});
            skArc(sketch, "E751", {"start": v(8.02, -6.07) * mm, "mid": v(8.05, -6.13) * mm, "end": v(8.1, -6.16) * mm});
            skLineSegment(sketch, "E752", {"start": v(8.1, -6.16) * mm, "end": v(8.98, -6.16) * mm});
            skArc(sketch, "E753", {"start": v(8.98, -6.16) * mm, "mid": v(9.03, -6.13) * mm, "end": v(9.06, -6.07) * mm});
            skLineSegment(sketch, "E754", {"start": v(9.06, -6.07) * mm, "end": v(9.06, -5.3) * mm});
            skArc(sketch, "E755", {"start": v(9.06, -5.3) * mm, "mid": v(9.03, -5.24) * mm, "end": v(8.98, -5.22) * mm});
            skLineSegment(sketch, "E756", {"start": v(8.98, -5.22) * mm, "end": v(8.1, -5.22) * mm});
            skArc(sketch, "E757", {"start": v(8.1, -5.22) * mm, "mid": v(8.05, -5.24) * mm, "end": v(8.02, -5.3) * mm});
            skLineSegment(sketch, "E758", {"start": v(6.32, -5.3) * mm, "end": v(6.32, -6.07) * mm});
            skArc(sketch, "E759", {"start": v(6.32, -6.07) * mm, "mid": v(6.35, -6.13) * mm, "end": v(6.4, -6.16) * mm});
            skLineSegment(sketch, "E760", {"start": v(6.4, -6.16) * mm, "end": v(7.28, -6.16) * mm});
            skArc(sketch, "E761", {"start": v(7.28, -6.16) * mm, "mid": v(7.33, -6.13) * mm, "end": v(7.36, -6.07) * mm});
            skLineSegment(sketch, "E762", {"start": v(7.36, -6.07) * mm, "end": v(7.36, -5.3) * mm});
            skArc(sketch, "E763", {"start": v(7.36, -5.3) * mm, "mid": v(7.33, -5.24) * mm, "end": v(7.28, -5.22) * mm});
            skLineSegment(sketch, "E764", {"start": v(7.28, -5.22) * mm, "end": v(6.4, -5.22) * mm});
            skArc(sketch, "E765", {"start": v(6.4, -5.22) * mm, "mid": v(6.35, -5.24) * mm, "end": v(6.32, -5.3) * mm});
            skLineSegment(sketch, "E766", {"start": v(-2.19, -9.57) * mm, "end": v(-1.41, -9.57) * mm});
            skArc(sketch, "E767", {"start": v(-1.41, -9.57) * mm, "mid": v(-1.36, -9.54) * mm, "end": v(-1.33, -9.48) * mm});
            skLineSegment(sketch, "E768", {"start": v(-1.33, -9.48) * mm, "end": v(-1.33, -8.61) * mm});
            skArc(sketch, "E769", {"start": v(-1.33, -8.61) * mm, "mid": v(-1.36, -8.55) * mm, "end": v(-1.41, -8.53) * mm});
            skLineSegment(sketch, "E770", {"start": v(-1.41, -8.53) * mm, "end": v(-2.19, -8.53) * mm});
            skArc(sketch, "E771", {"start": v(-2.19, -8.53) * mm, "mid": v(-2.24, -8.55) * mm, "end": v(-2.27, -8.61) * mm});
            skLineSegment(sketch, "E772", {"start": v(-2.27, -8.61) * mm, "end": v(-2.27, -9.48) * mm});
            skArc(sketch, "E773", {"start": v(-2.27, -9.48) * mm, "mid": v(-2.24, -9.54) * mm, "end": v(-2.19, -9.57) * mm});
            skLineSegment(sketch, "E774", {"start": v(-2.19, -11.27) * mm, "end": v(-1.41, -11.27) * mm});
            skArc(sketch, "E775", {"start": v(-1.41, -11.27) * mm, "mid": v(-1.36, -11.24) * mm, "end": v(-1.33, -11.18) * mm});
            skLineSegment(sketch, "E776", {"start": v(-1.33, -11.18) * mm, "end": v(-1.33, -10.31) * mm});
            skArc(sketch, "E777", {"start": v(-1.33, -10.31) * mm, "mid": v(-1.36, -10.25) * mm, "end": v(-1.41, -10.23) * mm});
            skLineSegment(sketch, "E778", {"start": v(-1.41, -10.23) * mm, "end": v(-2.19, -10.23) * mm});
            skArc(sketch, "E779", {"start": v(-2.19, -10.23) * mm, "mid": v(-2.24, -10.25) * mm, "end": v(-2.27, -10.31) * mm});
            skLineSegment(sketch, "E780", {"start": v(-2.27, -10.31) * mm, "end": v(-2.27, -11.18) * mm});
            skArc(sketch, "E781", {"start": v(-2.27, -11.18) * mm, "mid": v(-2.24, -11.24) * mm, "end": v(-2.19, -11.27) * mm});
            skLineSegment(sketch, "E782", {"start": v(-0.37, -9.59) * mm, "end": v(0.4, -9.59) * mm});
            skArc(sketch, "E783", {"start": v(0.4, -9.59) * mm, "mid": v(0.46, -9.56) * mm, "end": v(0.49, -9.5) * mm});
            skLineSegment(sketch, "E784", {"start": v(0.49, -9.5) * mm, "end": v(0.49, -8.63) * mm});
            skArc(sketch, "E785", {"start": v(0.49, -8.63) * mm, "mid": v(0.46, -8.57) * mm, "end": v(0.4, -8.55) * mm});
            skLineSegment(sketch, "E786", {"start": v(0.4, -8.55) * mm, "end": v(-0.37, -8.55) * mm});
            skArc(sketch, "E787", {"start": v(-0.37, -8.55) * mm, "mid": v(-0.42, -8.57) * mm, "end": v(-0.45, -8.63) * mm});
            skLineSegment(sketch, "E788", {"start": v(-0.45, -8.63) * mm, "end": v(-0.45, -9.5) * mm});
            skArc(sketch, "E789", {"start": v(-0.45, -9.5) * mm, "mid": v(-0.42, -9.56) * mm, "end": v(-0.37, -9.59) * mm});
            skLineSegment(sketch, "E790", {"start": v(-0.37, -11.29) * mm, "end": v(0.4, -11.29) * mm});
            skArc(sketch, "E791", {"start": v(0.4, -11.29) * mm, "mid": v(0.46, -11.26) * mm, "end": v(0.49, -11.2) * mm});
            skLineSegment(sketch, "E792", {"start": v(0.49, -11.2) * mm, "end": v(0.49, -10.33) * mm});
            skArc(sketch, "E793", {"start": v(0.49, -10.33) * mm, "mid": v(0.46, -10.27) * mm, "end": v(0.4, -10.25) * mm});
            skLineSegment(sketch, "E794", {"start": v(0.4, -10.25) * mm, "end": v(-0.37, -10.25) * mm});
            skArc(sketch, "E795", {"start": v(-0.37, -10.25) * mm, "mid": v(-0.42, -10.27) * mm, "end": v(-0.45, -10.33) * mm});
            skLineSegment(sketch, "E796", {"start": v(-0.45, -10.33) * mm, "end": v(-0.45, -11.2) * mm});
            skArc(sketch, "E797", {"start": v(-0.45, -11.2) * mm, "mid": v(-0.42, -11.26) * mm, "end": v(-0.37, -11.29) * mm});
            skLineSegment(sketch, "E798", {"start": v(-2.25, 18.36) * mm, "end": v(-2.23, 14.76) * mm});
            skArc(sketch, "E799", {"start": v(-2.36, 14.76) * mm, "mid": v(-2.23, 14.63) * mm, "end": v(-2.1, 14.76) * mm});
            skArc(sketch, "E800", {"start": v(-2.12, 18.36) * mm, "mid": v(-2.25, 18.48) * mm, "end": v(-2.37, 18.36) * mm});
            skLineSegment(sketch, "E801", {"start": v(-2.23, 14.76) * mm, "end": v(-2.2, 14.53) * mm});
            skArc(sketch, "E802", {"start": v(-2.32, 14.51) * mm, "mid": v(-2.18, 14.4) * mm, "end": v(-2.07, 14.55) * mm});
            skArc(sketch, "E803", {"start": v(-2.1, 14.78) * mm, "mid": v(-2.25, 14.88) * mm, "end": v(-2.36, 14.74) * mm});
            skLineSegment(sketch, "E804", {"start": v(-2.2, 14.53) * mm, "end": v(-2.14, 14.32) * mm});
            skArc(sketch, "E805", {"start": v(-2.26, 14.29) * mm, "mid": v(-2.11, 14.2) * mm, "end": v(-2.02, 14.35) * mm});
            skArc(sketch, "E806", {"start": v(-2.08, 14.56) * mm, "mid": v(-2.23, 14.65) * mm, "end": v(-2.32, 14.5) * mm});
            skLineSegment(sketch, "E807", {"start": v(-2.14, 14.32) * mm, "end": v(-2.06, 14.11) * mm});
            skArc(sketch, "E808", {"start": v(-2.18, 14.07) * mm, "mid": v(-2.02, 14) * mm, "end": v(-1.95, 14.16) * mm});
            skArc(sketch, "E809", {"start": v(-2.02, 14.36) * mm, "mid": v(-2.19, 14.43) * mm, "end": v(-2.26, 14.27) * mm});
            skLineSegment(sketch, "E810", {"start": v(-2.06, 14.11) * mm, "end": v(-1.97, 13.92) * mm});
            skArc(sketch, "E811", {"start": v(-2.08, 13.86) * mm, "mid": v(-1.91, 13.8) * mm, "end": v(-1.86, 13.97) * mm});
            skArc(sketch, "E812", {"start": v(-1.95, 14.17) * mm, "mid": v(-2.12, 14.22) * mm, "end": v(-2.18, 14.06) * mm});
            skLineSegment(sketch, "E813", {"start": v(-1.97, 13.92) * mm, "end": v(-1.86, 13.73) * mm});
            skArc(sketch, "E814", {"start": v(-1.96, 13.67) * mm, "mid": v(-1.8, 13.62) * mm, "end": v(-1.75, 13.8) * mm});
            skArc(sketch, "E815", {"start": v(-1.86, 13.98) * mm, "mid": v(-2.03, 14.02) * mm, "end": v(-2.08, 13.85) * mm});
            skLineSegment(sketch, "E816", {"start": v(-1.86, 13.73) * mm, "end": v(-1.72, 13.56) * mm});
            skArc(sketch, "E817", {"start": v(-1.82, 13.48) * mm, "mid": v(-1.65, 13.46) * mm, "end": v(-1.63, 13.63) * mm});
            skArc(sketch, "E818", {"start": v(-1.76, 13.8) * mm, "mid": v(-1.93, 13.83) * mm, "end": v(-1.96, 13.66) * mm});
            skLineSegment(sketch, "E819", {"start": v(-1.72, 13.56) * mm, "end": v(-1.58, 13.4) * mm});
            skArc(sketch, "E820", {"start": v(-1.67, 13.31) * mm, "mid": v(-1.5, 13.3) * mm, "end": v(-1.49, 13.48) * mm});
            skArc(sketch, "E821", {"start": v(-1.63, 13.64) * mm, "mid": v(-1.8, 13.65) * mm, "end": v(-1.82, 13.47) * mm});
            skLineSegment(sketch, "E822", {"start": v(-1.58, 13.4) * mm, "end": v(-1.42, 13.25) * mm});
            skArc(sketch, "E823", {"start": v(-1.5, 13.16) * mm, "mid": v(-1.33, 13.17) * mm, "end": v(-1.33, 13.35) * mm});
            skArc(sketch, "E824", {"start": v(-1.5, 13.5) * mm, "mid": v(-1.67, 13.48) * mm, "end": v(-1.66, 13.3) * mm});
            skLineSegment(sketch, "E825", {"start": v(-1.42, 13.25) * mm, "end": v(-1.24, 13.13) * mm});
            skArc(sketch, "E826", {"start": v(-1.32, 13.03) * mm, "mid": v(-1.14, 13.05) * mm, "end": v(-1.17, 13.23) * mm});
            skArc(sketch, "E827", {"start": v(-1.34, 13.36) * mm, "mid": v(-1.52, 13.33) * mm, "end": v(-1.5, 13.15) * mm});
            skLineSegment(sketch, "E828", {"start": v(-1.24, 13.13) * mm, "end": v(-1.06, 13.01) * mm});
            skArc(sketch, "E829", {"start": v(-1.12, 12.9) * mm, "mid": v(-0.95, 12.95) * mm, "end": v(-1, 13.12) * mm});
            skArc(sketch, "E830", {"start": v(-1.18, 13.23) * mm, "mid": v(-1.35, 13.2) * mm, "end": v(-1.3, 13.02) * mm});
            skLineSegment(sketch, "E831", {"start": v(-1.06, 13.01) * mm, "end": v(-0.86, 12.92) * mm});
            skArc(sketch, "E832", {"start": v(-0.91, 12.8) * mm, "mid": v(-0.75, 12.87) * mm, "end": v(-0.8, 13.03) * mm});
            skArc(sketch, "E833", {"start": v(-1, 13.13) * mm, "mid": v(-1.17, 13.07) * mm, "end": v(-1.11, 12.9) * mm});
            skLineSegment(sketch, "E834", {"start": v(-0.86, 12.92) * mm, "end": v(-0.65, 12.85) * mm});
            skArc(sketch, "E835", {"start": v(-0.7, 12.73) * mm, "mid": v(-0.54, 12.8) * mm, "end": v(-0.61, 12.96) * mm});
            skArc(sketch, "E836", {"start": v(-0.82, 13.04) * mm, "mid": v(-0.98, 12.96) * mm, "end": v(-0.9, 12.8) * mm});
            skLineSegment(sketch, "E837", {"start": v(-0.65, 12.85) * mm, "end": v(-0.44, 12.8) * mm});
            skArc(sketch, "E838", {"start": v(-0.47, 12.67) * mm, "mid": v(-0.32, 12.76) * mm, "end": v(-0.4, 12.91) * mm});
            skArc(sketch, "E839", {"start": v(-0.62, 12.97) * mm, "mid": v(-0.77, 12.88) * mm, "end": v(-0.68, 12.72) * mm});
            skLineSegment(sketch, "E840", {"start": v(-0.44, 12.8) * mm, "end": v(-0.21, 12.76) * mm});
            skArc(sketch, "E841", {"start": v(-0.23, 12.64) * mm, "mid": v(-0.1, 12.74) * mm, "end": v(-0.2, 12.88) * mm});
            skArc(sketch, "E842", {"start": v(-0.42, 12.92) * mm, "mid": v(-0.56, 12.8) * mm, "end": v(-0.46, 12.67) * mm});
            skLineSegment(sketch, "E843", {"start": v(-0.21, 12.76) * mm, "end": v(0, 12.75) * mm});
            skArc(sketch, "E844", {"start": v(0, 12.62) * mm, "mid": v(0.13, 12.74) * mm, "end": v(0, 12.87) * mm});
            skArc(sketch, "E845", {"start": v(-0.2, 12.88) * mm, "mid": v(-0.34, 12.76) * mm, "end": v(-0.22, 12.63) * mm});
            skLineSegment(sketch, "E846", {"start": v(0, 12.75) * mm, "end": v(0.25, 12.76) * mm});
            skArc(sketch, "E847", {"start": v(0.25, 12.64) * mm, "mid": v(0.37, 12.77) * mm, "end": v(0.24, 12.89) * mm});
            skArc(sketch, "E848", {"start": v(0, 12.87) * mm, "mid": v(-0.12, 12.74) * mm, "end": v(0, 12.62) * mm});
            skLineSegment(sketch, "E849", {"start": v(0.25, 12.76) * mm, "end": v(0.47, 12.8) * mm});
            skArc(sketch, "E850", {"start": v(0.49, 12.67) * mm, "mid": v(0.6, 12.82) * mm, "end": v(0.45, 12.92) * mm});
            skArc(sketch, "E851", {"start": v(0.23, 12.88) * mm, "mid": v(0.12, 12.74) * mm, "end": v(0.27, 12.64) * mm});
            skLineSegment(sketch, "E852", {"start": v(0.47, 12.8) * mm, "end": v(0.69, 12.85) * mm});
            skArc(sketch, "E853", {"start": v(0.72, 12.73) * mm, "mid": v(0.8, 12.88) * mm, "end": v(0.65, 12.97) * mm});
            skArc(sketch, "E854", {"start": v(0.44, 12.92) * mm, "mid": v(0.35, 12.76) * mm, "end": v(0.5, 12.68) * mm});
            skLineSegment(sketch, "E855", {"start": v(0.69, 12.85) * mm, "end": v(0.9, 12.93) * mm});
            skArc(sketch, "E856", {"start": v(0.93, 12.81) * mm, "mid": v(1, 12.97) * mm, "end": v(0.85, 13.05) * mm});
            skArc(sketch, "E857", {"start": v(0.64, 12.97) * mm, "mid": v(0.57, 12.8) * mm, "end": v(0.73, 12.74) * mm});
            skLineSegment(sketch, "E858", {"start": v(0.9, 12.93) * mm, "end": v(1.09, 13.03) * mm});
            skArc(sketch, "E859", {"start": v(1.14, 12.91) * mm, "mid": v(1.2, 13.08) * mm, "end": v(1.03, 13.14) * mm});
            skArc(sketch, "E860", {"start": v(0.84, 13.04) * mm, "mid": v(0.78, 12.88) * mm, "end": v(0.95, 12.82) * mm});
            skLineSegment(sketch, "E861", {"start": v(1.09, 13.03) * mm, "end": v(1.27, 13.14) * mm});
            skArc(sketch, "E862", {"start": v(1.34, 13.03) * mm, "mid": v(1.38, 13.2) * mm, "end": v(1.2, 13.25) * mm});
            skArc(sketch, "E863", {"start": v(1.02, 13.13) * mm, "mid": v(0.98, 12.96) * mm, "end": v(1.15, 12.92) * mm});
            skLineSegment(sketch, "E864", {"start": v(1.27, 13.14) * mm, "end": v(1.44, 13.27) * mm});
            skArc(sketch, "E865", {"start": v(1.52, 13.17) * mm, "mid": v(1.54, 13.35) * mm, "end": v(1.37, 13.37) * mm});
            skArc(sketch, "E866", {"start": v(1.2, 13.24) * mm, "mid": v(1.17, 13.06) * mm, "end": v(1.35, 13.04) * mm});
            skLineSegment(sketch, "E867", {"start": v(1.44, 13.27) * mm, "end": v(1.6, 13.42) * mm});
            skArc(sketch, "E868", {"start": v(1.69, 13.32) * mm, "mid": v(1.7, 13.5) * mm, "end": v(1.52, 13.5) * mm});
            skArc(sketch, "E869", {"start": v(1.36, 13.36) * mm, "mid": v(1.35, 13.19) * mm, "end": v(1.53, 13.18) * mm});
            skLineSegment(sketch, "E870", {"start": v(1.6, 13.42) * mm, "end": v(1.75, 13.58) * mm});
            skArc(sketch, "E871", {"start": v(1.84, 13.5) * mm, "mid": v(1.83, 13.67) * mm, "end": v(1.65, 13.66) * mm});
            skArc(sketch, "E872", {"start": v(1.51, 13.5) * mm, "mid": v(1.52, 13.32) * mm, "end": v(1.7, 13.33) * mm});
            skLineSegment(sketch, "E873", {"start": v(1.75, 13.58) * mm, "end": v(1.88, 13.75) * mm});
            skArc(sketch, "E874", {"start": v(1.98, 13.68) * mm, "mid": v(1.95, 13.85) * mm, "end": v(1.78, 13.82) * mm});
            skArc(sketch, "E875", {"start": v(1.65, 13.65) * mm, "mid": v(1.67, 13.48) * mm, "end": v(1.85, 13.5) * mm});
            skLineSegment(sketch, "E876", {"start": v(1.88, 13.75) * mm, "end": v(1.99, 13.94) * mm});
            skArc(sketch, "E877", {"start": v(2.1, 13.87) * mm, "mid": v(2.05, 14.04) * mm, "end": v(1.88, 14) * mm});
            skArc(sketch, "E878", {"start": v(1.77, 13.81) * mm, "mid": v(1.81, 13.64) * mm, "end": v(1.98, 13.69) * mm});
            skLineSegment(sketch, "E879", {"start": v(1.99, 13.94) * mm, "end": v(2.08, 14.13) * mm});
            skArc(sketch, "E880", {"start": v(2.2, 14.08) * mm, "mid": v(2.14, 14.25) * mm, "end": v(1.97, 14.19) * mm});
            skArc(sketch, "E881", {"start": v(1.88, 14) * mm, "mid": v(1.94, 13.82) * mm, "end": v(2.1, 13.88) * mm});
            skLineSegment(sketch, "E882", {"start": v(2.08, 14.13) * mm, "end": v(2.16, 14.34) * mm});
            skArc(sketch, "E883", {"start": v(2.27, 14.3) * mm, "mid": v(2.2, 14.46) * mm, "end": v(2.04, 14.38) * mm});
            skArc(sketch, "E884", {"start": v(1.96, 14.18) * mm, "mid": v(2.04, 14.02) * mm, "end": v(2.2, 14.1) * mm});
            skLineSegment(sketch, "E885", {"start": v(2.16, 14.34) * mm, "end": v(2.21, 14.56) * mm});
            skArc(sketch, "E886", {"start": v(2.33, 14.53) * mm, "mid": v(2.24, 14.68) * mm, "end": v(2.09, 14.59) * mm});
            skArc(sketch, "E887", {"start": v(2.04, 14.37) * mm, "mid": v(2.13, 14.22) * mm, "end": v(2.28, 14.31) * mm});
            skLineSegment(sketch, "E888", {"start": v(2.21, 14.56) * mm, "end": v(2.24, 14.78) * mm});
            skArc(sketch, "E889", {"start": v(2.37, 14.76) * mm, "mid": v(2.26, 14.9) * mm, "end": v(2.12, 14.8) * mm});
            skArc(sketch, "E890", {"start": v(2.09, 14.58) * mm, "mid": v(2.2, 14.43) * mm, "end": v(2.33, 14.54) * mm});
            skLineSegment(sketch, "E891", {"start": v(2.24, 14.78) * mm, "end": v(2.25, 15.03) * mm});
            skArc(sketch, "E892", {"start": v(2.38, 15.02) * mm, "mid": v(2.26, 15.15) * mm, "end": v(2.13, 15.03) * mm});
            skArc(sketch, "E893", {"start": v(2.12, 14.79) * mm, "mid": v(2.24, 14.66) * mm, "end": v(2.37, 14.78) * mm});
            skLineSegment(sketch, "E894", {"start": v(2.25, 15.03) * mm, "end": v(2.25, 18.36) * mm});
            skArc(sketch, "E895", {"start": v(2.38, 18.36) * mm, "mid": v(2.25, 18.48) * mm, "end": v(2.13, 18.36) * mm});
            skArc(sketch, "E896", {"start": v(2.13, 15.03) * mm, "mid": v(2.25, 14.9) * mm, "end": v(2.38, 15.03) * mm});
            skLineSegment(sketch, "E897", {"start": v(2.25, 18.36) * mm, "end": v(1.53, 20.57) * mm});
            skArc(sketch, "E898", {"start": v(1.65, 20.61) * mm, "mid": v(1.5, 20.7) * mm, "end": v(1.41, 20.54) * mm});
            skArc(sketch, "E899", {"start": v(2.14, 18.32) * mm, "mid": v(2.3, 18.24) * mm, "end": v(2.37, 18.4) * mm});
            skLineSegment(sketch, "E900", {"start": v(1.53, 20.57) * mm, "end": v(0.96, 21.46) * mm});
            skArc(sketch, "E901", {"start": v(1.06, 21.53) * mm, "mid": v(0.9, 21.56) * mm, "end": v(0.85, 21.4) * mm});
            skArc(sketch, "E902", {"start": v(1.43, 20.5) * mm, "mid": v(1.6, 20.47) * mm, "end": v(1.64, 20.64) * mm});
            skLineSegment(sketch, "E903", {"start": v(0.96, 21.46) * mm, "end": v(-0.95, 21.46) * mm});
            skArc(sketch, "E904", {"start": v(-0.95, 21.58) * mm, "mid": v(-1.07, 21.46) * mm, "end": v(-0.95, 21.33) * mm});
            skArc(sketch, "E905", {"start": v(0.96, 21.33) * mm, "mid": v(1.08, 21.46) * mm, "end": v(0.96, 21.58) * mm});
            skLineSegment(sketch, "E906", {"start": v(-0.95, 21.46) * mm, "end": v(-1.52, 20.57) * mm});
            skArc(sketch, "E907", {"start": v(-1.63, 20.64) * mm, "mid": v(-1.6, 20.47) * mm, "end": v(-1.42, 20.5) * mm});
            skArc(sketch, "E908", {"start": v(-0.84, 21.4) * mm, "mid": v(-0.88, 21.56) * mm, "end": v(-1.05, 21.53) * mm});
            skLineSegment(sketch, "E909", {"start": v(-1.52, 20.57) * mm, "end": v(-2.25, 18.36) * mm});
            skArc(sketch, "E910", {"start": v(-2.36, 18.4) * mm, "mid": v(-2.28, 18.24) * mm, "end": v(-2.13, 18.32) * mm});
            skArc(sketch, "E911", {"start": v(-1.4, 20.54) * mm, "mid": v(-1.49, 20.7) * mm, "end": v(-1.64, 20.61) * mm});
            skLineSegment(sketch, "E912", {"start": v(-1.03, 13) * mm, "end": v(1.03, 13) * mm});
            skArc(sketch, "E913", {"start": v(1.03, 12.87) * mm, "mid": v(1.16, 13) * mm, "end": v(1.03, 13.12) * mm});
            skArc(sketch, "E914", {"start": v(-1.03, 13.12) * mm, "mid": v(-1.15, 13) * mm, "end": v(-1.03, 12.87) * mm});
            skLineSegment(sketch, "E915", {"start": v(-1.67, 13.5) * mm, "end": v(1.68, 13.5) * mm});
            skArc(sketch, "E916", {"start": v(1.68, 13.37) * mm, "mid": v(1.8, 13.5) * mm, "end": v(1.68, 13.62) * mm});
            skArc(sketch, "E917", {"start": v(-1.67, 13.62) * mm, "mid": v(-1.8, 13.5) * mm, "end": v(-1.67, 13.37) * mm});
            skLineSegment(sketch, "E918", {"start": v(-2, 14) * mm, "end": v(2.02, 14) * mm});
            skArc(sketch, "E919", {"start": v(2.02, 13.87) * mm, "mid": v(2.14, 14) * mm, "end": v(2.02, 14.12) * mm});
            skArc(sketch, "E920", {"start": v(-2, 14.12) * mm, "mid": v(-2.13, 14) * mm, "end": v(-2, 13.87) * mm});
            skLineSegment(sketch, "E921", {"start": v(-2.19, 14.5) * mm, "end": v(2.2, 14.5) * mm});
            skArc(sketch, "E922", {"start": v(2.2, 14.37) * mm, "mid": v(2.32, 14.5) * mm, "end": v(2.2, 14.62) * mm});
            skArc(sketch, "E923", {"start": v(-2.19, 14.62) * mm, "mid": v(-2.31, 14.5) * mm, "end": v(-2.19, 14.37) * mm});
            skLineSegment(sketch, "E924", {"start": v(-2.23, 15) * mm, "end": v(2.25, 15) * mm});
            skArc(sketch, "E925", {"start": v(2.25, 14.87) * mm, "mid": v(2.38, 15) * mm, "end": v(2.25, 15.12) * mm});
            skArc(sketch, "E926", {"start": v(-2.23, 15.12) * mm, "mid": v(-2.36, 15) * mm, "end": v(-2.23, 14.87) * mm});
            skLineSegment(sketch, "E927", {"start": v(-2.24, 15.5) * mm, "end": v(2.25, 15.5) * mm});
            skArc(sketch, "E928", {"start": v(2.25, 15.37) * mm, "mid": v(2.38, 15.5) * mm, "end": v(2.25, 15.62) * mm});
            skArc(sketch, "E929", {"start": v(-2.24, 15.62) * mm, "mid": v(-2.36, 15.5) * mm, "end": v(-2.24, 15.37) * mm});
            skLineSegment(sketch, "E930", {"start": v(-2.24, 16) * mm, "end": v(2.25, 16) * mm});
            skArc(sketch, "E931", {"start": v(2.25, 15.87) * mm, "mid": v(2.38, 16) * mm, "end": v(2.25, 16.12) * mm});
            skArc(sketch, "E932", {"start": v(-2.24, 16.12) * mm, "mid": v(-2.36, 16) * mm, "end": v(-2.24, 15.87) * mm});
            skLineSegment(sketch, "E933", {"start": v(-2.24, 16.5) * mm, "end": v(2.25, 16.5) * mm});
            skArc(sketch, "E934", {"start": v(2.25, 16.37) * mm, "mid": v(2.38, 16.5) * mm, "end": v(2.25, 16.62) * mm});
            skArc(sketch, "E935", {"start": v(-2.24, 16.62) * mm, "mid": v(-2.36, 16.5) * mm, "end": v(-2.24, 16.37) * mm});
            skLineSegment(sketch, "E936", {"start": v(-2.24, 17) * mm, "end": v(2.25, 17) * mm});
            skArc(sketch, "E937", {"start": v(2.25, 16.87) * mm, "mid": v(2.38, 17) * mm, "end": v(2.25, 17.12) * mm});
            skArc(sketch, "E938", {"start": v(-2.24, 17.12) * mm, "mid": v(-2.37, 17) * mm, "end": v(-2.24, 16.87) * mm});
            skLineSegment(sketch, "E939", {"start": v(-2.24, 17.5) * mm, "end": v(2.25, 17.5) * mm});
            skArc(sketch, "E940", {"start": v(2.25, 17.37) * mm, "mid": v(2.38, 17.5) * mm, "end": v(2.25, 17.62) * mm});
            skArc(sketch, "E941", {"start": v(-2.24, 17.62) * mm, "mid": v(-2.37, 17.5) * mm, "end": v(-2.24, 17.37) * mm});
            skLineSegment(sketch, "E942", {"start": v(-2.24, 18) * mm, "end": v(2.25, 18) * mm});
            skArc(sketch, "E943", {"start": v(2.25, 17.87) * mm, "mid": v(2.38, 18) * mm, "end": v(2.25, 18.12) * mm});
            skArc(sketch, "E944", {"start": v(-2.24, 18.12) * mm, "mid": v(-2.37, 18) * mm, "end": v(-2.24, 17.87) * mm});
            skLineSegment(sketch, "E945", {"start": v(-2.2, 18.5) * mm, "end": v(2.2, 18.5) * mm});
            skArc(sketch, "E946", {"start": v(2.2, 18.37) * mm, "mid": v(2.33, 18.5) * mm, "end": v(2.2, 18.62) * mm});
            skArc(sketch, "E947", {"start": v(-2.2, 18.62) * mm, "mid": v(-2.32, 18.5) * mm, "end": v(-2.2, 18.37) * mm});
            skLineSegment(sketch, "E948", {"start": v(-2.04, 19) * mm, "end": v(2.05, 19) * mm});
            skArc(sketch, "E949", {"start": v(2.05, 18.87) * mm, "mid": v(2.17, 19) * mm, "end": v(2.05, 19.12) * mm});
            skArc(sketch, "E950", {"start": v(-2.04, 19.12) * mm, "mid": v(-2.16, 19) * mm, "end": v(-2.04, 18.87) * mm});
            skLineSegment(sketch, "E951", {"start": v(-1.87, 19.5) * mm, "end": v(1.88, 19.5) * mm});
            skArc(sketch, "E952", {"start": v(1.88, 19.37) * mm, "mid": v(2, 19.5) * mm, "end": v(1.88, 19.62) * mm});
            skArc(sketch, "E953", {"start": v(-1.87, 19.62) * mm, "mid": v(-2, 19.5) * mm, "end": v(-1.87, 19.37) * mm});
            skLineSegment(sketch, "E954", {"start": v(-1.71, 20) * mm, "end": v(1.72, 20) * mm});
            skArc(sketch, "E955", {"start": v(1.72, 19.87) * mm, "mid": v(1.85, 20) * mm, "end": v(1.72, 20.12) * mm});
            skArc(sketch, "E956", {"start": v(-1.71, 20.12) * mm, "mid": v(-1.84, 20) * mm, "end": v(-1.71, 19.87) * mm});
            skLineSegment(sketch, "E957", {"start": v(-1.55, 20.5) * mm, "end": v(1.56, 20.5) * mm});
            skArc(sketch, "E958", {"start": v(1.56, 20.37) * mm, "mid": v(1.68, 20.5) * mm, "end": v(1.56, 20.62) * mm});
            skArc(sketch, "E959", {"start": v(-1.55, 20.62) * mm, "mid": v(-1.67, 20.5) * mm, "end": v(-1.55, 20.37) * mm});
            skLineSegment(sketch, "E960", {"start": v(-1.25, 21) * mm, "end": v(1.26, 21) * mm});
            skArc(sketch, "E961", {"start": v(1.26, 20.87) * mm, "mid": v(1.38, 21) * mm, "end": v(1.26, 21.12) * mm});
            skArc(sketch, "E962", {"start": v(-1.25, 21.12) * mm, "mid": v(-1.37, 21) * mm, "end": v(-1.25, 20.87) * mm});
            skLineSegment(sketch, "E963", {"start": v(-2.43, 28.4) * mm, "end": v(-2.33, 28.3) * mm});
            skArc(sketch, "E964", {"start": v(-2.36, 28.26) * mm, "mid": v(-2.3, 28.26) * mm, "end": v(-2.3, 28.33) * mm});
            skArc(sketch, "E965", {"start": v(-2.4, 28.43) * mm, "mid": v(-2.47, 28.43) * mm, "end": v(-2.47, 28.36) * mm});
            skLineSegment(sketch, "E966", {"start": v(-2.33, 28.3) * mm, "end": v(-2.2, 28.2) * mm});
            skArc(sketch, "E967", {"start": v(-2.23, 28.16) * mm, "mid": v(-2.16, 28.18) * mm, "end": v(-2.17, 28.25) * mm});
            skArc(sketch, "E968", {"start": v(-2.3, 28.34) * mm, "mid": v(-2.37, 28.32) * mm, "end": v(-2.36, 28.25) * mm});
            skLineSegment(sketch, "E969", {"start": v(-2.2, 28.2) * mm, "end": v(-2.06, 28.14) * mm});
            skArc(sketch, "E970", {"start": v(-2.08, 28.1) * mm, "mid": v(-2.02, 28.12) * mm, "end": v(-2.04, 28.18) * mm});
            skArc(sketch, "E971", {"start": v(-2.18, 28.25) * mm, "mid": v(-2.25, 28.23) * mm, "end": v(-2.22, 28.16) * mm});
            skLineSegment(sketch, "E972", {"start": v(-2.06, 28.14) * mm, "end": v(-1.9, 28.1) * mm});
            skArc(sketch, "E973", {"start": v(-1.92, 28.05) * mm, "mid": v(-1.86, 28.09) * mm, "end": v(-1.9, 28.15) * mm});
            skArc(sketch, "E974", {"start": v(-2.05, 28.19) * mm, "mid": v(-2.11, 28.15) * mm, "end": v(-2.07, 28.1) * mm});
            skLineSegment(sketch, "E975", {"start": v(-1.9, 28.1) * mm, "end": v(-1.83, 28.09) * mm});
            skArc(sketch, "E976", {"start": v(-1.84, 28.04) * mm, "mid": v(-1.78, 28.08) * mm, "end": v(-1.82, 28.14) * mm});
            skArc(sketch, "E977", {"start": v(-1.9, 28.15) * mm, "mid": v(-1.96, 28.1) * mm, "end": v(-1.92, 28.05) * mm});
            skLineSegment(sketch, "E978", {"start": v(-1.83, 28.09) * mm, "end": v(1.92, 28.1) * mm});
            skArc(sketch, "E979", {"start": v(1.92, 28.05) * mm, "mid": v(1.97, 28.1) * mm, "end": v(1.92, 28.15) * mm});
            skArc(sketch, "E980", {"start": v(-1.83, 28.14) * mm, "mid": v(-1.88, 28.09) * mm, "end": v(-1.83, 28.04) * mm});
            skLineSegment(sketch, "E981", {"start": v(1.92, 28.1) * mm, "end": v(2.08, 28.14) * mm});
            skArc(sketch, "E982", {"start": v(2.1, 28.1) * mm, "mid": v(2.12, 28.16) * mm, "end": v(2.06, 28.2) * mm});
            skArc(sketch, "E983", {"start": v(1.91, 28.15) * mm, "mid": v(1.88, 28.09) * mm, "end": v(1.94, 28.05) * mm});
            skLineSegment(sketch, "E984", {"start": v(2.08, 28.14) * mm, "end": v(2.22, 28.2) * mm});
            skArc(sketch, "E985", {"start": v(2.24, 28.16) * mm, "mid": v(2.26, 28.23) * mm, "end": v(2.2, 28.25) * mm});
            skArc(sketch, "E986", {"start": v(2.05, 28.19) * mm, "mid": v(2.03, 28.12) * mm, "end": v(2.1, 28.1) * mm});
            skLineSegment(sketch, "E987", {"start": v(2.22, 28.2) * mm, "end": v(2.34, 28.3) * mm});
            skArc(sketch, "E988", {"start": v(2.37, 28.26) * mm, "mid": v(2.38, 28.33) * mm, "end": v(2.31, 28.34) * mm});
            skArc(sketch, "E989", {"start": v(2.19, 28.25) * mm, "mid": v(2.18, 28.18) * mm, "end": v(2.25, 28.17) * mm});
            skLineSegment(sketch, "E990", {"start": v(2.34, 28.3) * mm, "end": v(2.44, 28.4) * mm});
            skArc(sketch, "E991", {"start": v(2.47, 28.36) * mm, "mid": v(2.47, 28.43) * mm, "end": v(2.4, 28.43) * mm});
            skArc(sketch, "E992", {"start": v(2.3, 28.34) * mm, "mid": v(2.3, 28.26) * mm, "end": v(2.38, 28.26) * mm});
            skLineSegment(sketch, "E993", {"start": v(2.44, 28.4) * mm, "end": v(2.34, 28.5) * mm});
            skArc(sketch, "E994", {"start": v(2.37, 28.53) * mm, "mid": v(2.3, 28.53) * mm, "end": v(2.3, 28.46) * mm});
            skArc(sketch, "E995", {"start": v(2.4, 28.36) * mm, "mid": v(2.47, 28.36) * mm, "end": v(2.47, 28.43) * mm});
            skLineSegment(sketch, "E996", {"start": v(2.34, 28.5) * mm, "end": v(2.2, 28.58) * mm});
            skArc(sketch, "E997", {"start": v(2.24, 28.62) * mm, "mid": v(2.17, 28.6) * mm, "end": v(2.18, 28.54) * mm});
            skArc(sketch, "E998", {"start": v(2.3, 28.45) * mm, "mid": v(2.38, 28.46) * mm, "end": v(2.36, 28.53) * mm});
            skLineSegment(sketch, "E999", {"start": v(2.2, 28.58) * mm, "end": v(2.07, 28.65) * mm});
            skArc(sketch, "E1000", {"start": v(2.09, 28.7) * mm, "mid": v(2.02, 28.67) * mm, "end": v(2.05, 28.6) * mm});
            skArc(sketch, "E1001", {"start": v(2.19, 28.54) * mm, "mid": v(2.25, 28.56) * mm, "end": v(2.23, 28.63) * mm});
            skLineSegment(sketch, "E1002", {"start": v(2.07, 28.65) * mm, "end": v(1.91, 28.69) * mm});
            skArc(sketch, "E1003", {"start": v(1.93, 28.74) * mm, "mid": v(1.87, 28.7) * mm, "end": v(1.9, 28.64) * mm});
            skArc(sketch, "E1004", {"start": v(2.05, 28.6) * mm, "mid": v(2.12, 28.63) * mm, "end": v(2.08, 28.7) * mm});
            skLineSegment(sketch, "E1005", {"start": v(1.91, 28.69) * mm, "end": v(1.84, 28.7) * mm});
            skArc(sketch, "E1006", {"start": v(1.84, 28.75) * mm, "mid": v(1.79, 28.7) * mm, "end": v(1.83, 28.65) * mm});
            skArc(sketch, "E1007", {"start": v(1.9, 28.64) * mm, "mid": v(1.96, 28.68) * mm, "end": v(1.92, 28.74) * mm});
            skLineSegment(sketch, "E1008", {"start": v(1.84, 28.7) * mm, "end": v(-1.92, 28.69) * mm});
            skArc(sketch, "E1009", {"start": v(-1.92, 28.74) * mm, "mid": v(-1.97, 28.69) * mm, "end": v(-1.92, 28.64) * mm});
            skArc(sketch, "E1010", {"start": v(1.84, 28.65) * mm, "mid": v(1.88, 28.7) * mm, "end": v(1.83, 28.75) * mm});
            skLineSegment(sketch, "E1011", {"start": v(-1.92, 28.69) * mm, "end": v(-2.07, 28.64) * mm});
            skArc(sketch, "E1012", {"start": v(-2.08, 28.7) * mm, "mid": v(-2.12, 28.63) * mm, "end": v(-2.06, 28.6) * mm});
            skArc(sketch, "E1013", {"start": v(-1.9, 28.64) * mm, "mid": v(-1.87, 28.7) * mm, "end": v(-1.93, 28.74) * mm});
            skLineSegment(sketch, "E1014", {"start": v(-2.07, 28.64) * mm, "end": v(-2.21, 28.58) * mm});
            skArc(sketch, "E1015", {"start": v(-2.23, 28.62) * mm, "mid": v(-2.26, 28.56) * mm, "end": v(-2.19, 28.53) * mm});
            skArc(sketch, "E1016", {"start": v(-2.05, 28.6) * mm, "mid": v(-2.03, 28.67) * mm, "end": v(-2.1, 28.69) * mm});
            skLineSegment(sketch, "E1017", {"start": v(-2.21, 28.58) * mm, "end": v(-2.34, 28.49) * mm});
            skArc(sketch, "E1018", {"start": v(-2.37, 28.53) * mm, "mid": v(-2.38, 28.46) * mm, "end": v(-2.3, 28.45) * mm});
            skArc(sketch, "E1019", {"start": v(-2.18, 28.54) * mm, "mid": v(-2.17, 28.6) * mm, "end": v(-2.24, 28.62) * mm});
            skLineSegment(sketch, "E1020", {"start": v(-2.34, 28.49) * mm, "end": v(-2.43, 28.4) * mm});
            skArc(sketch, "E1021", {"start": v(-2.47, 28.43) * mm, "mid": v(-2.47, 28.36) * mm, "end": v(-2.4, 28.36) * mm});
            skArc(sketch, "E1022", {"start": v(-2.3, 28.45) * mm, "mid": v(-2.3, 28.52) * mm, "end": v(-2.37, 28.52) * mm});
            skLineSegment(sketch, "E1023", {"start": v(-2.19, 28.2) * mm, "end": v(2.2, 28.2) * mm});
            skArc(sketch, "E1024", {"start": v(2.2, 28.15) * mm, "mid": v(2.24, 28.2) * mm, "end": v(2.2, 28.25) * mm});
            skArc(sketch, "E1025", {"start": v(-2.19, 28.25) * mm, "mid": v(-2.24, 28.2) * mm, "end": v(-2.19, 28.15) * mm});
            skLineSegment(sketch, "E1026", {"start": v(-2.43, 28.4) * mm, "end": v(2.43, 28.4) * mm});
            skArc(sketch, "E1027", {"start": v(2.43, 28.35) * mm, "mid": v(2.48, 28.4) * mm, "end": v(2.43, 28.45) * mm});
            skArc(sketch, "E1028", {"start": v(-2.43, 28.45) * mm, "mid": v(-2.48, 28.4) * mm, "end": v(-2.43, 28.35) * mm});
            skLineSegment(sketch, "E1029", {"start": v(-2.17, 28.6) * mm, "end": v(2.17, 28.6) * mm});
            skArc(sketch, "E1030", {"start": v(2.17, 28.55) * mm, "mid": v(2.22, 28.6) * mm, "end": v(2.17, 28.65) * mm});
            skArc(sketch, "E1031", {"start": v(-2.17, 28.65) * mm, "mid": v(-2.22, 28.6) * mm, "end": v(-2.17, 28.55) * mm});
            skCircle(sketch, "E1032", {"center": v(0, 15) * mm, "radius": 1.7 * mm});
            skArc(sketch, "E1033", {"start": v(0, 14.12) * mm, "mid": v(0.88, 15) * mm, "end": v(0, 15.87) * mm});
            skArc(sketch, "E1034", {"start": v(0, 15.87) * mm, "mid": v(-0.87, 15) * mm, "end": v(0, 14.12) * mm});
            skCircle(sketch, "E1035", {"center": v(0, 25) * mm, "radius": 1.7 * mm});
            skArc(sketch, "E1036", {"start": v(0, 24.12) * mm, "mid": v(0.88, 25) * mm, "end": v(0, 25.87) * mm});
            skArc(sketch, "E1037", {"start": v(0, 25.87) * mm, "mid": v(-0.87, 25) * mm, "end": v(0, 24.12) * mm});
            skLineSegment(sketch, "E1038", {"start": v(-3.8, 0.7) * mm, "end": v(-3.8, 0.5) * mm});
            skArc(sketch, "E1039", {"start": v(-3.8, 0.5) * mm, "mid": v(-3.78, 0.47) * mm, "end": v(-3.75, 0.45) * mm});
            skLineSegment(sketch, "E1040", {"start": v(-3.75, 0.45) * mm, "end": v(-3.05, 0.45) * mm});
            skArc(sketch, "E1041", {"start": v(-3.05, 0.45) * mm, "mid": v(-3.02, 0.47) * mm, "end": v(-3, 0.5) * mm});
            skLineSegment(sketch, "E1042", {"start": v(-3, 0.5) * mm, "end": v(-3, 0.7) * mm});
            skArc(sketch, "E1043", {"start": v(-3, 0.7) * mm, "mid": v(-3.02, 0.74) * mm, "end": v(-3.05, 0.75) * mm});
            skLineSegment(sketch, "E1044", {"start": v(-3.05, 0.75) * mm, "end": v(-3.75, 0.75) * mm});
            skArc(sketch, "E1045", {"start": v(-3.75, 0.75) * mm, "mid": v(-3.78, 0.74) * mm, "end": v(-3.8, 0.7) * mm});
            skLineSegment(sketch, "E1046", {"start": v(-3.8, 0.2) * mm, "end": v(-3.8, 0) * mm});
            skArc(sketch, "E1047", {"start": v(-3.8, 0) * mm, "mid": v(-3.78, -0.03) * mm, "end": v(-3.75, -0.05) * mm});
            skLineSegment(sketch, "E1048", {"start": v(-3.75, -0.05) * mm, "end": v(-3.05, -0.05) * mm});
            skArc(sketch, "E1049", {"start": v(-3.05, -0.05) * mm, "mid": v(-3.02, -0.03) * mm, "end": v(-3, 0) * mm});
            skLineSegment(sketch, "E1050", {"start": v(-3, 0) * mm, "end": v(-3, 0.2) * mm});
            skArc(sketch, "E1051", {"start": v(-3, 0.2) * mm, "mid": v(-3.02, 0.24) * mm, "end": v(-3.05, 0.25) * mm});
            skLineSegment(sketch, "E1052", {"start": v(-3.05, 0.25) * mm, "end": v(-3.75, 0.25) * mm});
            skArc(sketch, "E1053", {"start": v(-3.75, 0.25) * mm, "mid": v(-3.78, 0.24) * mm, "end": v(-3.8, 0.2) * mm});
            skLineSegment(sketch, "E1054", {"start": v(-3.8, -0.3) * mm, "end": v(-3.8, -0.5) * mm});
            skArc(sketch, "E1055", {"start": v(-3.8, -0.5) * mm, "mid": v(-3.78, -0.53) * mm, "end": v(-3.75, -0.55) * mm});
            skLineSegment(sketch, "E1056", {"start": v(-3.75, -0.55) * mm, "end": v(-3.05, -0.55) * mm});
            skArc(sketch, "E1057", {"start": v(-3.05, -0.55) * mm, "mid": v(-3.02, -0.53) * mm, "end": v(-3, -0.5) * mm});
            skLineSegment(sketch, "E1058", {"start": v(-3, -0.5) * mm, "end": v(-3, -0.3) * mm});
            skArc(sketch, "E1059", {"start": v(-3, -0.3) * mm, "mid": v(-3.02, -0.26) * mm, "end": v(-3.05, -0.25) * mm});
            skLineSegment(sketch, "E1060", {"start": v(-3.05, -0.25) * mm, "end": v(-3.75, -0.25) * mm});
            skArc(sketch, "E1061", {"start": v(-3.75, -0.25) * mm, "mid": v(-3.78, -0.26) * mm, "end": v(-3.8, -0.3) * mm});
            skLineSegment(sketch, "E1062", {"start": v(-3.8, -0.8) * mm, "end": v(-3.8, -1) * mm});
            skArc(sketch, "E1063", {"start": v(-3.8, -1) * mm, "mid": v(-3.78, -1.03) * mm, "end": v(-3.75, -1.05) * mm});
            skLineSegment(sketch, "E1064", {"start": v(-3.75, -1.05) * mm, "end": v(-3.05, -1.05) * mm});
            skArc(sketch, "E1065", {"start": v(-3.05, -1.05) * mm, "mid": v(-3.02, -1.03) * mm, "end": v(-3, -1) * mm});
            skLineSegment(sketch, "E1066", {"start": v(-3, -1) * mm, "end": v(-3, -0.8) * mm});
            skArc(sketch, "E1067", {"start": v(-3, -0.8) * mm, "mid": v(-3.02, -0.76) * mm, "end": v(-3.05, -0.75) * mm});
            skLineSegment(sketch, "E1068", {"start": v(-3.05, -0.75) * mm, "end": v(-3.75, -0.75) * mm});
            skArc(sketch, "E1069", {"start": v(-3.75, -0.75) * mm, "mid": v(-3.78, -0.76) * mm, "end": v(-3.8, -0.8) * mm});
            skLineSegment(sketch, "E1070", {"start": v(-3.8, -1.3) * mm, "end": v(-3.8, -1.5) * mm});
            skArc(sketch, "E1071", {"start": v(-3.8, -1.5) * mm, "mid": v(-3.78, -1.53) * mm, "end": v(-3.75, -1.55) * mm});
            skLineSegment(sketch, "E1072", {"start": v(-3.75, -1.55) * mm, "end": v(-3.05, -1.55) * mm});
            skArc(sketch, "E1073", {"start": v(-3.05, -1.55) * mm, "mid": v(-3.02, -1.53) * mm, "end": v(-3, -1.5) * mm});
            skLineSegment(sketch, "E1074", {"start": v(-3, -1.5) * mm, "end": v(-3, -1.3) * mm});
            skArc(sketch, "E1075", {"start": v(-3, -1.3) * mm, "mid": v(-3.02, -1.26) * mm, "end": v(-3.05, -1.25) * mm});
            skLineSegment(sketch, "E1076", {"start": v(-3.05, -1.25) * mm, "end": v(-3.75, -1.25) * mm});
            skArc(sketch, "E1077", {"start": v(-3.75, -1.25) * mm, "mid": v(-3.78, -1.26) * mm, "end": v(-3.8, -1.3) * mm});
            skLineSegment(sketch, "E1078", {"start": v(-3.8, -1.8) * mm, "end": v(-3.8, -2) * mm});
            skArc(sketch, "E1079", {"start": v(-3.8, -2) * mm, "mid": v(-3.78, -2.03) * mm, "end": v(-3.75, -2.05) * mm});
            skLineSegment(sketch, "E1080", {"start": v(-3.75, -2.05) * mm, "end": v(-3.05, -2.05) * mm});
            skArc(sketch, "E1081", {"start": v(-3.05, -2.05) * mm, "mid": v(-3.02, -2.03) * mm, "end": v(-3, -2) * mm});
            skLineSegment(sketch, "E1082", {"start": v(-3, -2) * mm, "end": v(-3, -1.8) * mm});
            skArc(sketch, "E1083", {"start": v(-3, -1.8) * mm, "mid": v(-3.02, -1.76) * mm, "end": v(-3.05, -1.75) * mm});
            skLineSegment(sketch, "E1084", {"start": v(-3.05, -1.75) * mm, "end": v(-3.75, -1.75) * mm});
            skArc(sketch, "E1085", {"start": v(-3.75, -1.75) * mm, "mid": v(-3.78, -1.76) * mm, "end": v(-3.8, -1.8) * mm});
            skLineSegment(sketch, "E1086", {"start": v(-3, -2.5) * mm, "end": v(-3, -2.3) * mm});
            skArc(sketch, "E1087", {"start": v(-3, -2.3) * mm, "mid": v(-3.02, -2.26) * mm, "end": v(-3.05, -2.25) * mm});
            skLineSegment(sketch, "E1088", {"start": v(-3.05, -2.25) * mm, "end": v(-3.75, -2.25) * mm});
            skArc(sketch, "E1089", {"start": v(-3.75, -2.25) * mm, "mid": v(-3.78, -2.26) * mm, "end": v(-3.8, -2.3) * mm});
            skLineSegment(sketch, "E1090", {"start": v(-3.8, -2.3) * mm, "end": v(-3.8, -2.5) * mm});
            skArc(sketch, "E1091", {"start": v(-3.8, -2.5) * mm, "mid": v(-3.78, -2.53) * mm, "end": v(-3.75, -2.55) * mm});
            skLineSegment(sketch, "E1092", {"start": v(-3.75, -2.55) * mm, "end": v(-3.05, -2.55) * mm});
            skArc(sketch, "E1093", {"start": v(-3.05, -2.55) * mm, "mid": v(-3.02, -2.53) * mm, "end": v(-3, -2.5) * mm});
            skLineSegment(sketch, "E1094", {"start": v(-3, -3) * mm, "end": v(-3, -2.8) * mm});
            skArc(sketch, "E1095", {"start": v(-3, -2.8) * mm, "mid": v(-3.02, -2.76) * mm, "end": v(-3.05, -2.75) * mm});
            skLineSegment(sketch, "E1096", {"start": v(-3.05, -2.75) * mm, "end": v(-3.75, -2.75) * mm});
            skArc(sketch, "E1097", {"start": v(-3.75, -2.75) * mm, "mid": v(-3.78, -2.76) * mm, "end": v(-3.8, -2.8) * mm});
            skLineSegment(sketch, "E1098", {"start": v(-3.8, -2.8) * mm, "end": v(-3.8, -3) * mm});
            skArc(sketch, "E1099", {"start": v(-3.8, -3) * mm, "mid": v(-3.78, -3.03) * mm, "end": v(-3.75, -3.05) * mm});
            skLineSegment(sketch, "E1100", {"start": v(-3.75, -3.05) * mm, "end": v(-3.05, -3.05) * mm});
            skArc(sketch, "E1101", {"start": v(-3.05, -3.05) * mm, "mid": v(-3.02, -3.03) * mm, "end": v(-3, -3) * mm});
            skLineSegment(sketch, "E1102", {"start": v(-3, -3.5) * mm, "end": v(-3, -3.3) * mm});
            skArc(sketch, "E1103", {"start": v(-3, -3.3) * mm, "mid": v(-3.02, -3.26) * mm, "end": v(-3.05, -3.25) * mm});
            skLineSegment(sketch, "E1104", {"start": v(-3.05, -3.25) * mm, "end": v(-3.75, -3.25) * mm});
            skArc(sketch, "E1105", {"start": v(-3.75, -3.25) * mm, "mid": v(-3.78, -3.26) * mm, "end": v(-3.8, -3.3) * mm});
            skLineSegment(sketch, "E1106", {"start": v(-3.8, -3.3) * mm, "end": v(-3.8, -3.5) * mm});
            skArc(sketch, "E1107", {"start": v(-3.8, -3.5) * mm, "mid": v(-3.78, -3.53) * mm, "end": v(-3.75, -3.55) * mm});
            skLineSegment(sketch, "E1108", {"start": v(-3.75, -3.55) * mm, "end": v(-3.05, -3.55) * mm});
            skArc(sketch, "E1109", {"start": v(-3.05, -3.55) * mm, "mid": v(-3.02, -3.53) * mm, "end": v(-3, -3.5) * mm});
            skLineSegment(sketch, "E1110", {"start": v(-3, -4) * mm, "end": v(-3, -3.8) * mm});
            skArc(sketch, "E1111", {"start": v(-3, -3.8) * mm, "mid": v(-3.02, -3.76) * mm, "end": v(-3.05, -3.75) * mm});
            skLineSegment(sketch, "E1112", {"start": v(-3.05, -3.75) * mm, "end": v(-3.75, -3.75) * mm});
            skArc(sketch, "E1113", {"start": v(-3.75, -3.75) * mm, "mid": v(-3.78, -3.76) * mm, "end": v(-3.8, -3.8) * mm});
            skLineSegment(sketch, "E1114", {"start": v(-3.8, -3.8) * mm, "end": v(-3.8, -4) * mm});
            skArc(sketch, "E1115", {"start": v(-3.8, -4) * mm, "mid": v(-3.78, -4.03) * mm, "end": v(-3.75, -4.05) * mm});
            skLineSegment(sketch, "E1116", {"start": v(-3.75, -4.05) * mm, "end": v(-3.05, -4.05) * mm});
            skArc(sketch, "E1117", {"start": v(-3.05, -4.05) * mm, "mid": v(-3.02, -4.03) * mm, "end": v(-3, -4) * mm});
            skLineSegment(sketch, "E1118", {"start": v(-3, -4.5) * mm, "end": v(-3, -4.3) * mm});
            skArc(sketch, "E1119", {"start": v(-3, -4.3) * mm, "mid": v(-3.02, -4.26) * mm, "end": v(-3.05, -4.25) * mm});
            skLineSegment(sketch, "E1120", {"start": v(-3.05, -4.25) * mm, "end": v(-3.75, -4.25) * mm});
            skArc(sketch, "E1121", {"start": v(-3.75, -4.25) * mm, "mid": v(-3.78, -4.26) * mm, "end": v(-3.8, -4.3) * mm});
            skLineSegment(sketch, "E1122", {"start": v(-3.8, -4.3) * mm, "end": v(-3.8, -4.5) * mm});
            skArc(sketch, "E1123", {"start": v(-3.8, -4.5) * mm, "mid": v(-3.78, -4.53) * mm, "end": v(-3.75, -4.55) * mm});
            skLineSegment(sketch, "E1124", {"start": v(-3.75, -4.55) * mm, "end": v(-3.05, -4.55) * mm});
            skArc(sketch, "E1125", {"start": v(-3.05, -4.55) * mm, "mid": v(-3.02, -4.53) * mm, "end": v(-3, -4.5) * mm});
            skLineSegment(sketch, "E1126", {"start": v(-2.6, -5.7) * mm, "end": v(-2.4, -5.7) * mm});
            skArc(sketch, "E1127", {"start": v(-2.4, -5.7) * mm, "mid": v(-2.37, -5.68) * mm, "end": v(-2.35, -5.65) * mm});
            skLineSegment(sketch, "E1128", {"start": v(-2.35, -5.65) * mm, "end": v(-2.35, -4.95) * mm});
            skArc(sketch, "E1129", {"start": v(-2.35, -4.95) * mm, "mid": v(-2.37, -4.91) * mm, "end": v(-2.4, -4.9) * mm});
            skLineSegment(sketch, "E1130", {"start": v(-2.4, -4.9) * mm, "end": v(-2.6, -4.9) * mm});
            skArc(sketch, "E1131", {"start": v(-2.6, -4.9) * mm, "mid": v(-2.63, -4.91) * mm, "end": v(-2.65, -4.95) * mm});
            skLineSegment(sketch, "E1132", {"start": v(-2.65, -4.95) * mm, "end": v(-2.65, -5.65) * mm});
            skArc(sketch, "E1133", {"start": v(-2.65, -5.65) * mm, "mid": v(-2.63, -5.68) * mm, "end": v(-2.6, -5.7) * mm});
            skLineSegment(sketch, "E1134", {"start": v(-2.1, -5.7) * mm, "end": v(-1.9, -5.7) * mm});
            skArc(sketch, "E1135", {"start": v(-1.9, -5.7) * mm, "mid": v(-1.87, -5.68) * mm, "end": v(-1.85, -5.65) * mm});
            skLineSegment(sketch, "E1136", {"start": v(-1.85, -5.65) * mm, "end": v(-1.85, -4.95) * mm});
            skArc(sketch, "E1137", {"start": v(-1.85, -4.95) * mm, "mid": v(-1.87, -4.91) * mm, "end": v(-1.9, -4.9) * mm});
            skLineSegment(sketch, "E1138", {"start": v(-1.9, -4.9) * mm, "end": v(-2.1, -4.9) * mm});
            skArc(sketch, "E1139", {"start": v(-2.1, -4.9) * mm, "mid": v(-2.13, -4.91) * mm, "end": v(-2.15, -4.95) * mm});
            skLineSegment(sketch, "E1140", {"start": v(-2.15, -4.95) * mm, "end": v(-2.15, -5.65) * mm});
            skArc(sketch, "E1141", {"start": v(-2.15, -5.65) * mm, "mid": v(-2.13, -5.68) * mm, "end": v(-2.1, -5.7) * mm});
            skLineSegment(sketch, "E1142", {"start": v(-1.6, -5.7) * mm, "end": v(-1.4, -5.7) * mm});
            skArc(sketch, "E1143", {"start": v(-1.4, -5.7) * mm, "mid": v(-1.37, -5.68) * mm, "end": v(-1.35, -5.65) * mm});
            skLineSegment(sketch, "E1144", {"start": v(-1.35, -5.65) * mm, "end": v(-1.35, -4.95) * mm});
            skArc(sketch, "E1145", {"start": v(-1.35, -4.95) * mm, "mid": v(-1.37, -4.91) * mm, "end": v(-1.4, -4.9) * mm});
            skLineSegment(sketch, "E1146", {"start": v(-1.4, -4.9) * mm, "end": v(-1.6, -4.9) * mm});
            skArc(sketch, "E1147", {"start": v(-1.6, -4.9) * mm, "mid": v(-1.63, -4.91) * mm, "end": v(-1.65, -4.95) * mm});
            skLineSegment(sketch, "E1148", {"start": v(-1.65, -4.95) * mm, "end": v(-1.65, -5.65) * mm});
            skArc(sketch, "E1149", {"start": v(-1.65, -5.65) * mm, "mid": v(-1.63, -5.68) * mm, "end": v(-1.6, -5.7) * mm});
            skLineSegment(sketch, "E1150", {"start": v(-1.1, -5.7) * mm, "end": v(-0.9, -5.7) * mm});
            skArc(sketch, "E1151", {"start": v(-0.9, -5.7) * mm, "mid": v(-0.87, -5.68) * mm, "end": v(-0.85, -5.65) * mm});
            skLineSegment(sketch, "E1152", {"start": v(-0.85, -5.65) * mm, "end": v(-0.85, -4.95) * mm});
            skArc(sketch, "E1153", {"start": v(-0.85, -4.95) * mm, "mid": v(-0.87, -4.91) * mm, "end": v(-0.9, -4.9) * mm});
            skLineSegment(sketch, "E1154", {"start": v(-0.9, -4.9) * mm, "end": v(-1.1, -4.9) * mm});
            skArc(sketch, "E1155", {"start": v(-1.1, -4.9) * mm, "mid": v(-1.13, -4.91) * mm, "end": v(-1.15, -4.95) * mm});
            skLineSegment(sketch, "E1156", {"start": v(-1.15, -4.95) * mm, "end": v(-1.15, -5.65) * mm});
            skArc(sketch, "E1157", {"start": v(-1.15, -5.65) * mm, "mid": v(-1.13, -5.68) * mm, "end": v(-1.1, -5.7) * mm});
            skLineSegment(sketch, "E1158", {"start": v(-0.6, -5.7) * mm, "end": v(-0.4, -5.7) * mm});
            skArc(sketch, "E1159", {"start": v(-0.4, -5.7) * mm, "mid": v(-0.37, -5.68) * mm, "end": v(-0.35, -5.65) * mm});
            skLineSegment(sketch, "E1160", {"start": v(-0.35, -5.65) * mm, "end": v(-0.35, -4.95) * mm});
            skArc(sketch, "E1161", {"start": v(-0.35, -4.95) * mm, "mid": v(-0.37, -4.91) * mm, "end": v(-0.4, -4.9) * mm});
            skLineSegment(sketch, "E1162", {"start": v(-0.4, -4.9) * mm, "end": v(-0.6, -4.9) * mm});
            skArc(sketch, "E1163", {"start": v(-0.6, -4.9) * mm, "mid": v(-0.63, -4.91) * mm, "end": v(-0.65, -4.95) * mm});
            skLineSegment(sketch, "E1164", {"start": v(-0.65, -4.95) * mm, "end": v(-0.65, -5.65) * mm});
            skArc(sketch, "E1165", {"start": v(-0.65, -5.65) * mm, "mid": v(-0.63, -5.68) * mm, "end": v(-0.6, -5.7) * mm});
            skLineSegment(sketch, "E1166", {"start": v(-0.1, -5.7) * mm, "end": v(0.1, -5.7) * mm});
            skArc(sketch, "E1167", {"start": v(0.1, -5.7) * mm, "mid": v(0.13, -5.68) * mm, "end": v(0.15, -5.65) * mm});
            skLineSegment(sketch, "E1168", {"start": v(0.15, -5.65) * mm, "end": v(0.15, -4.95) * mm});
            skArc(sketch, "E1169", {"start": v(0.15, -4.95) * mm, "mid": v(0.13, -4.91) * mm, "end": v(0.1, -4.9) * mm});
            skLineSegment(sketch, "E1170", {"start": v(0.1, -4.9) * mm, "end": v(-0.1, -4.9) * mm});
            skArc(sketch, "E1171", {"start": v(-0.1, -4.9) * mm, "mid": v(-0.13, -4.91) * mm, "end": v(-0.15, -4.95) * mm});
            skLineSegment(sketch, "E1172", {"start": v(-0.15, -4.95) * mm, "end": v(-0.15, -5.65) * mm});
            skArc(sketch, "E1173", {"start": v(-0.15, -5.65) * mm, "mid": v(-0.13, -5.68) * mm, "end": v(-0.1, -5.7) * mm});
            skLineSegment(sketch, "E1174", {"start": v(0.6, -4.9) * mm, "end": v(0.4, -4.9) * mm});
            skArc(sketch, "E1175", {"start": v(0.4, -4.9) * mm, "mid": v(0.37, -4.91) * mm, "end": v(0.35, -4.95) * mm});
            skLineSegment(sketch, "E1176", {"start": v(0.35, -4.95) * mm, "end": v(0.35, -5.65) * mm});
            skArc(sketch, "E1177", {"start": v(0.35, -5.65) * mm, "mid": v(0.37, -5.68) * mm, "end": v(0.4, -5.7) * mm});
            skLineSegment(sketch, "E1178", {"start": v(0.4, -5.7) * mm, "end": v(0.6, -5.7) * mm});
            skArc(sketch, "E1179", {"start": v(0.6, -5.7) * mm, "mid": v(0.63, -5.68) * mm, "end": v(0.65, -5.65) * mm});
            skLineSegment(sketch, "E1180", {"start": v(0.65, -5.65) * mm, "end": v(0.65, -4.95) * mm});
            skArc(sketch, "E1181", {"start": v(0.65, -4.95) * mm, "mid": v(0.63, -4.91) * mm, "end": v(0.6, -4.9) * mm});
            skLineSegment(sketch, "E1182", {"start": v(1.1, -4.9) * mm, "end": v(0.9, -4.9) * mm});
            skArc(sketch, "E1183", {"start": v(0.9, -4.9) * mm, "mid": v(0.87, -4.91) * mm, "end": v(0.85, -4.95) * mm});
            skLineSegment(sketch, "E1184", {"start": v(0.85, -4.95) * mm, "end": v(0.85, -5.65) * mm});
            skArc(sketch, "E1185", {"start": v(0.85, -5.65) * mm, "mid": v(0.87, -5.68) * mm, "end": v(0.9, -5.7) * mm});
            skLineSegment(sketch, "E1186", {"start": v(0.9, -5.7) * mm, "end": v(1.1, -5.7) * mm});
            skArc(sketch, "E1187", {"start": v(1.1, -5.7) * mm, "mid": v(1.13, -5.68) * mm, "end": v(1.15, -5.65) * mm});
            skLineSegment(sketch, "E1188", {"start": v(1.15, -5.65) * mm, "end": v(1.15, -4.95) * mm});
            skArc(sketch, "E1189", {"start": v(1.15, -4.95) * mm, "mid": v(1.13, -4.91) * mm, "end": v(1.1, -4.9) * mm});
            skLineSegment(sketch, "E1190", {"start": v(1.6, -4.9) * mm, "end": v(1.4, -4.9) * mm});
            skArc(sketch, "E1191", {"start": v(1.4, -4.9) * mm, "mid": v(1.37, -4.91) * mm, "end": v(1.35, -4.95) * mm});
            skLineSegment(sketch, "E1192", {"start": v(1.35, -4.95) * mm, "end": v(1.35, -5.65) * mm});
            skArc(sketch, "E1193", {"start": v(1.35, -5.65) * mm, "mid": v(1.37, -5.68) * mm, "end": v(1.4, -5.7) * mm});
            skLineSegment(sketch, "E1194", {"start": v(1.4, -5.7) * mm, "end": v(1.6, -5.7) * mm});
            skArc(sketch, "E1195", {"start": v(1.6, -5.7) * mm, "mid": v(1.63, -5.68) * mm, "end": v(1.65, -5.65) * mm});
            skLineSegment(sketch, "E1196", {"start": v(1.65, -5.65) * mm, "end": v(1.65, -4.95) * mm});
            skArc(sketch, "E1197", {"start": v(1.65, -4.95) * mm, "mid": v(1.63, -4.91) * mm, "end": v(1.6, -4.9) * mm});
            skLineSegment(sketch, "E1198", {"start": v(2.1, -4.9) * mm, "end": v(1.9, -4.9) * mm});
            skArc(sketch, "E1199", {"start": v(1.9, -4.9) * mm, "mid": v(1.87, -4.91) * mm, "end": v(1.85, -4.95) * mm});
            skLineSegment(sketch, "E1200", {"start": v(1.85, -4.95) * mm, "end": v(1.85, -5.65) * mm});
            skArc(sketch, "E1201", {"start": v(1.85, -5.65) * mm, "mid": v(1.87, -5.68) * mm, "end": v(1.9, -5.7) * mm});
            skLineSegment(sketch, "E1202", {"start": v(1.9, -5.7) * mm, "end": v(2.1, -5.7) * mm});
            skArc(sketch, "E1203", {"start": v(2.1, -5.7) * mm, "mid": v(2.13, -5.68) * mm, "end": v(2.15, -5.65) * mm});
            skLineSegment(sketch, "E1204", {"start": v(2.15, -5.65) * mm, "end": v(2.15, -4.95) * mm});
            skArc(sketch, "E1205", {"start": v(2.15, -4.95) * mm, "mid": v(2.13, -4.91) * mm, "end": v(2.1, -4.9) * mm});
            skLineSegment(sketch, "E1206", {"start": v(2.6, -4.9) * mm, "end": v(2.4, -4.9) * mm});
            skArc(sketch, "E1207", {"start": v(2.4, -4.9) * mm, "mid": v(2.37, -4.91) * mm, "end": v(2.35, -4.95) * mm});
            skLineSegment(sketch, "E1208", {"start": v(2.35, -4.95) * mm, "end": v(2.35, -5.65) * mm});
            skArc(sketch, "E1209", {"start": v(2.35, -5.65) * mm, "mid": v(2.37, -5.68) * mm, "end": v(2.4, -5.7) * mm});
            skLineSegment(sketch, "E1210", {"start": v(2.4, -5.7) * mm, "end": v(2.6, -5.7) * mm});
            skArc(sketch, "E1211", {"start": v(2.6, -5.7) * mm, "mid": v(2.63, -5.68) * mm, "end": v(2.65, -5.65) * mm});
            skLineSegment(sketch, "E1212", {"start": v(2.65, -5.65) * mm, "end": v(2.65, -4.95) * mm});
            skArc(sketch, "E1213", {"start": v(2.65, -4.95) * mm, "mid": v(2.63, -4.91) * mm, "end": v(2.6, -4.9) * mm});
            skLineSegment(sketch, "E1214", {"start": v(3.8, -4.5) * mm, "end": v(3.8, -4.3) * mm});
            skArc(sketch, "E1215", {"start": v(3.8, -4.3) * mm, "mid": v(3.78, -4.26) * mm, "end": v(3.75, -4.25) * mm});
            skLineSegment(sketch, "E1216", {"start": v(3.75, -4.25) * mm, "end": v(3.05, -4.25) * mm});
            skArc(sketch, "E1217", {"start": v(3.05, -4.25) * mm, "mid": v(3.02, -4.26) * mm, "end": v(3, -4.3) * mm});
            skLineSegment(sketch, "E1218", {"start": v(3, -4.3) * mm, "end": v(3, -4.5) * mm});
            skArc(sketch, "E1219", {"start": v(3, -4.5) * mm, "mid": v(3.02, -4.53) * mm, "end": v(3.05, -4.55) * mm});
            skLineSegment(sketch, "E1220", {"start": v(3.05, -4.55) * mm, "end": v(3.75, -4.55) * mm});
            skArc(sketch, "E1221", {"start": v(3.75, -4.55) * mm, "mid": v(3.78, -4.53) * mm, "end": v(3.8, -4.5) * mm});
            skLineSegment(sketch, "E1222", {"start": v(3.8, -4) * mm, "end": v(3.8, -3.8) * mm});
            skArc(sketch, "E1223", {"start": v(3.8, -3.8) * mm, "mid": v(3.78, -3.76) * mm, "end": v(3.75, -3.75) * mm});
            skLineSegment(sketch, "E1224", {"start": v(3.75, -3.75) * mm, "end": v(3.05, -3.75) * mm});
            skArc(sketch, "E1225", {"start": v(3.05, -3.75) * mm, "mid": v(3.02, -3.76) * mm, "end": v(3, -3.8) * mm});
            skLineSegment(sketch, "E1226", {"start": v(3, -3.8) * mm, "end": v(3, -4) * mm});
            skArc(sketch, "E1227", {"start": v(3, -4) * mm, "mid": v(3.02, -4.03) * mm, "end": v(3.05, -4.05) * mm});
            skLineSegment(sketch, "E1228", {"start": v(3.05, -4.05) * mm, "end": v(3.75, -4.05) * mm});
            skArc(sketch, "E1229", {"start": v(3.75, -4.05) * mm, "mid": v(3.78, -4.03) * mm, "end": v(3.8, -4) * mm});
            skLineSegment(sketch, "E1230", {"start": v(3.8, -3.5) * mm, "end": v(3.8, -3.3) * mm});
            skArc(sketch, "E1231", {"start": v(3.8, -3.3) * mm, "mid": v(3.78, -3.26) * mm, "end": v(3.75, -3.25) * mm});
            skLineSegment(sketch, "E1232", {"start": v(3.75, -3.25) * mm, "end": v(3.05, -3.25) * mm});
            skArc(sketch, "E1233", {"start": v(3.05, -3.25) * mm, "mid": v(3.02, -3.26) * mm, "end": v(3, -3.3) * mm});
            skLineSegment(sketch, "E1234", {"start": v(3, -3.3) * mm, "end": v(3, -3.5) * mm});
            skArc(sketch, "E1235", {"start": v(3, -3.5) * mm, "mid": v(3.02, -3.53) * mm, "end": v(3.05, -3.55) * mm});
            skLineSegment(sketch, "E1236", {"start": v(3.05, -3.55) * mm, "end": v(3.75, -3.55) * mm});
            skArc(sketch, "E1237", {"start": v(3.75, -3.55) * mm, "mid": v(3.78, -3.53) * mm, "end": v(3.8, -3.5) * mm});
            skLineSegment(sketch, "E1238", {"start": v(3.8, -3) * mm, "end": v(3.8, -2.8) * mm});
            skArc(sketch, "E1239", {"start": v(3.8, -2.8) * mm, "mid": v(3.78, -2.76) * mm, "end": v(3.75, -2.75) * mm});
            skLineSegment(sketch, "E1240", {"start": v(3.75, -2.75) * mm, "end": v(3.05, -2.75) * mm});
            skArc(sketch, "E1241", {"start": v(3.05, -2.75) * mm, "mid": v(3.02, -2.76) * mm, "end": v(3, -2.8) * mm});
            skLineSegment(sketch, "E1242", {"start": v(3, -2.8) * mm, "end": v(3, -3) * mm});
            skArc(sketch, "E1243", {"start": v(3, -3) * mm, "mid": v(3.02, -3.03) * mm, "end": v(3.05, -3.05) * mm});
            skLineSegment(sketch, "E1244", {"start": v(3.05, -3.05) * mm, "end": v(3.75, -3.05) * mm});
            skArc(sketch, "E1245", {"start": v(3.75, -3.05) * mm, "mid": v(3.78, -3.03) * mm, "end": v(3.8, -3) * mm});
            skLineSegment(sketch, "E1246", {"start": v(3.8, -2.5) * mm, "end": v(3.8, -2.3) * mm});
            skArc(sketch, "E1247", {"start": v(3.8, -2.3) * mm, "mid": v(3.78, -2.26) * mm, "end": v(3.75, -2.25) * mm});
            skLineSegment(sketch, "E1248", {"start": v(3.75, -2.25) * mm, "end": v(3.05, -2.25) * mm});
            skArc(sketch, "E1249", {"start": v(3.05, -2.25) * mm, "mid": v(3.02, -2.26) * mm, "end": v(3, -2.3) * mm});
            skLineSegment(sketch, "E1250", {"start": v(3, -2.3) * mm, "end": v(3, -2.5) * mm});
            skArc(sketch, "E1251", {"start": v(3, -2.5) * mm, "mid": v(3.02, -2.53) * mm, "end": v(3.05, -2.55) * mm});
            skLineSegment(sketch, "E1252", {"start": v(3.05, -2.55) * mm, "end": v(3.75, -2.55) * mm});
            skArc(sketch, "E1253", {"start": v(3.75, -2.55) * mm, "mid": v(3.78, -2.53) * mm, "end": v(3.8, -2.5) * mm});
            skLineSegment(sketch, "E1254", {"start": v(3.8, -2) * mm, "end": v(3.8, -1.8) * mm});
            skArc(sketch, "E1255", {"start": v(3.8, -1.8) * mm, "mid": v(3.78, -1.76) * mm, "end": v(3.75, -1.75) * mm});
            skLineSegment(sketch, "E1256", {"start": v(3.75, -1.75) * mm, "end": v(3.05, -1.75) * mm});
            skArc(sketch, "E1257", {"start": v(3.05, -1.75) * mm, "mid": v(3.02, -1.76) * mm, "end": v(3, -1.8) * mm});
            skLineSegment(sketch, "E1258", {"start": v(3, -1.8) * mm, "end": v(3, -2) * mm});
            skArc(sketch, "E1259", {"start": v(3, -2) * mm, "mid": v(3.02, -2.03) * mm, "end": v(3.05, -2.05) * mm});
            skLineSegment(sketch, "E1260", {"start": v(3.05, -2.05) * mm, "end": v(3.75, -2.05) * mm});
            skArc(sketch, "E1261", {"start": v(3.75, -2.05) * mm, "mid": v(3.78, -2.03) * mm, "end": v(3.8, -2) * mm});
            skLineSegment(sketch, "E1262", {"start": v(3, -1.3) * mm, "end": v(3, -1.5) * mm});
            skArc(sketch, "E1263", {"start": v(3, -1.5) * mm, "mid": v(3.02, -1.53) * mm, "end": v(3.05, -1.55) * mm});
            skLineSegment(sketch, "E1264", {"start": v(3.05, -1.55) * mm, "end": v(3.75, -1.55) * mm});
            skArc(sketch, "E1265", {"start": v(3.75, -1.55) * mm, "mid": v(3.78, -1.53) * mm, "end": v(3.8, -1.5) * mm});
            skLineSegment(sketch, "E1266", {"start": v(3.8, -1.5) * mm, "end": v(3.8, -1.3) * mm});
            skArc(sketch, "E1267", {"start": v(3.8, -1.3) * mm, "mid": v(3.78, -1.26) * mm, "end": v(3.75, -1.25) * mm});
            skLineSegment(sketch, "E1268", {"start": v(3.75, -1.25) * mm, "end": v(3.05, -1.25) * mm});
            skArc(sketch, "E1269", {"start": v(3.05, -1.25) * mm, "mid": v(3.02, -1.26) * mm, "end": v(3, -1.3) * mm});
            skLineSegment(sketch, "E1270", {"start": v(3, -0.8) * mm, "end": v(3, -1) * mm});
            skArc(sketch, "E1271", {"start": v(3, -1) * mm, "mid": v(3.02, -1.03) * mm, "end": v(3.05, -1.05) * mm});
            skLineSegment(sketch, "E1272", {"start": v(3.05, -1.05) * mm, "end": v(3.75, -1.05) * mm});
            skArc(sketch, "E1273", {"start": v(3.75, -1.05) * mm, "mid": v(3.78, -1.03) * mm, "end": v(3.8, -1) * mm});
            skLineSegment(sketch, "E1274", {"start": v(3.8, -1) * mm, "end": v(3.8, -0.8) * mm});
            skArc(sketch, "E1275", {"start": v(3.8, -0.8) * mm, "mid": v(3.78, -0.76) * mm, "end": v(3.75, -0.75) * mm});
            skLineSegment(sketch, "E1276", {"start": v(3.75, -0.75) * mm, "end": v(3.05, -0.75) * mm});
            skArc(sketch, "E1277", {"start": v(3.05, -0.75) * mm, "mid": v(3.02, -0.76) * mm, "end": v(3, -0.8) * mm});
            skLineSegment(sketch, "E1278", {"start": v(3, -0.3) * mm, "end": v(3, -0.5) * mm});
            skArc(sketch, "E1279", {"start": v(3, -0.5) * mm, "mid": v(3.02, -0.53) * mm, "end": v(3.05, -0.55) * mm});
            skLineSegment(sketch, "E1280", {"start": v(3.05, -0.55) * mm, "end": v(3.75, -0.55) * mm});
            skArc(sketch, "E1281", {"start": v(3.75, -0.55) * mm, "mid": v(3.78, -0.53) * mm, "end": v(3.8, -0.5) * mm});
            skLineSegment(sketch, "E1282", {"start": v(3.8, -0.5) * mm, "end": v(3.8, -0.3) * mm});
            skArc(sketch, "E1283", {"start": v(3.8, -0.3) * mm, "mid": v(3.78, -0.26) * mm, "end": v(3.75, -0.25) * mm});
            skLineSegment(sketch, "E1284", {"start": v(3.75, -0.25) * mm, "end": v(3.05, -0.25) * mm});
            skArc(sketch, "E1285", {"start": v(3.05, -0.25) * mm, "mid": v(3.02, -0.26) * mm, "end": v(3, -0.3) * mm});
            skLineSegment(sketch, "E1286", {"start": v(3, 0.2) * mm, "end": v(3, 0) * mm});
            skArc(sketch, "E1287", {"start": v(3, 0) * mm, "mid": v(3.02, -0.03) * mm, "end": v(3.05, -0.05) * mm});
            skLineSegment(sketch, "E1288", {"start": v(3.05, -0.05) * mm, "end": v(3.75, -0.05) * mm});
            skArc(sketch, "E1289", {"start": v(3.75, -0.05) * mm, "mid": v(3.78, -0.03) * mm, "end": v(3.8, 0) * mm});
            skLineSegment(sketch, "E1290", {"start": v(3.8, 0) * mm, "end": v(3.8, 0.2) * mm});
            skArc(sketch, "E1291", {"start": v(3.8, 0.2) * mm, "mid": v(3.78, 0.24) * mm, "end": v(3.75, 0.25) * mm});
            skLineSegment(sketch, "E1292", {"start": v(3.75, 0.25) * mm, "end": v(3.05, 0.25) * mm});
            skArc(sketch, "E1293", {"start": v(3.05, 0.25) * mm, "mid": v(3.02, 0.24) * mm, "end": v(3, 0.2) * mm});
            skLineSegment(sketch, "E1294", {"start": v(3, 0.7) * mm, "end": v(3, 0.5) * mm});
            skArc(sketch, "E1295", {"start": v(3, 0.5) * mm, "mid": v(3.02, 0.47) * mm, "end": v(3.05, 0.45) * mm});
            skLineSegment(sketch, "E1296", {"start": v(3.05, 0.45) * mm, "end": v(3.75, 0.45) * mm});
            skArc(sketch, "E1297", {"start": v(3.75, 0.45) * mm, "mid": v(3.78, 0.47) * mm, "end": v(3.8, 0.5) * mm});
            skLineSegment(sketch, "E1298", {"start": v(3.8, 0.5) * mm, "end": v(3.8, 0.7) * mm});
            skArc(sketch, "E1299", {"start": v(3.8, 0.7) * mm, "mid": v(3.78, 0.74) * mm, "end": v(3.75, 0.75) * mm});
            skLineSegment(sketch, "E1300", {"start": v(3.75, 0.75) * mm, "end": v(3.05, 0.75) * mm});
            skArc(sketch, "E1301", {"start": v(3.05, 0.75) * mm, "mid": v(3.02, 0.74) * mm, "end": v(3, 0.7) * mm});
            skLineSegment(sketch, "E1302", {"start": v(2.6, 1.9) * mm, "end": v(2.4, 1.9) * mm});
            skArc(sketch, "E1303", {"start": v(2.4, 1.9) * mm, "mid": v(2.37, 1.89) * mm, "end": v(2.35, 1.85) * mm});
            skLineSegment(sketch, "E1304", {"start": v(2.35, 1.85) * mm, "end": v(2.35, 1.15) * mm});
            skArc(sketch, "E1305", {"start": v(2.35, 1.15) * mm, "mid": v(2.37, 1.12) * mm, "end": v(2.4, 1.1) * mm});
            skLineSegment(sketch, "E1306", {"start": v(2.4, 1.1) * mm, "end": v(2.6, 1.1) * mm});
            skArc(sketch, "E1307", {"start": v(2.6, 1.1) * mm, "mid": v(2.63, 1.12) * mm, "end": v(2.65, 1.15) * mm});
            skLineSegment(sketch, "E1308", {"start": v(2.65, 1.15) * mm, "end": v(2.65, 1.85) * mm});
            skArc(sketch, "E1309", {"start": v(2.65, 1.85) * mm, "mid": v(2.63, 1.89) * mm, "end": v(2.6, 1.9) * mm});
            skLineSegment(sketch, "E1310", {"start": v(2.1, 1.9) * mm, "end": v(1.9, 1.9) * mm});
            skArc(sketch, "E1311", {"start": v(1.9, 1.9) * mm, "mid": v(1.87, 1.89) * mm, "end": v(1.85, 1.85) * mm});
            skLineSegment(sketch, "E1312", {"start": v(1.85, 1.85) * mm, "end": v(1.85, 1.15) * mm});
            skArc(sketch, "E1313", {"start": v(1.85, 1.15) * mm, "mid": v(1.87, 1.12) * mm, "end": v(1.9, 1.1) * mm});
            skLineSegment(sketch, "E1314", {"start": v(1.9, 1.1) * mm, "end": v(2.1, 1.1) * mm});
            skArc(sketch, "E1315", {"start": v(2.1, 1.1) * mm, "mid": v(2.13, 1.12) * mm, "end": v(2.15, 1.15) * mm});
            skLineSegment(sketch, "E1316", {"start": v(2.15, 1.15) * mm, "end": v(2.15, 1.85) * mm});
            skArc(sketch, "E1317", {"start": v(2.15, 1.85) * mm, "mid": v(2.13, 1.89) * mm, "end": v(2.1, 1.9) * mm});
            skLineSegment(sketch, "E1318", {"start": v(1.6, 1.9) * mm, "end": v(1.4, 1.9) * mm});
            skArc(sketch, "E1319", {"start": v(1.4, 1.9) * mm, "mid": v(1.37, 1.89) * mm, "end": v(1.35, 1.85) * mm});
            skLineSegment(sketch, "E1320", {"start": v(1.35, 1.85) * mm, "end": v(1.35, 1.15) * mm});
            skArc(sketch, "E1321", {"start": v(1.35, 1.15) * mm, "mid": v(1.37, 1.12) * mm, "end": v(1.4, 1.1) * mm});
            skLineSegment(sketch, "E1322", {"start": v(1.4, 1.1) * mm, "end": v(1.6, 1.1) * mm});
            skArc(sketch, "E1323", {"start": v(1.6, 1.1) * mm, "mid": v(1.63, 1.12) * mm, "end": v(1.65, 1.15) * mm});
            skLineSegment(sketch, "E1324", {"start": v(1.65, 1.15) * mm, "end": v(1.65, 1.85) * mm});
            skArc(sketch, "E1325", {"start": v(1.65, 1.85) * mm, "mid": v(1.63, 1.89) * mm, "end": v(1.6, 1.9) * mm});
            skLineSegment(sketch, "E1326", {"start": v(1.1, 1.9) * mm, "end": v(0.9, 1.9) * mm});
            skArc(sketch, "E1327", {"start": v(0.9, 1.9) * mm, "mid": v(0.87, 1.89) * mm, "end": v(0.85, 1.85) * mm});
            skLineSegment(sketch, "E1328", {"start": v(0.85, 1.85) * mm, "end": v(0.85, 1.15) * mm});
            skArc(sketch, "E1329", {"start": v(0.85, 1.15) * mm, "mid": v(0.87, 1.12) * mm, "end": v(0.9, 1.1) * mm});
            skLineSegment(sketch, "E1330", {"start": v(0.9, 1.1) * mm, "end": v(1.1, 1.1) * mm});
            skArc(sketch, "E1331", {"start": v(1.1, 1.1) * mm, "mid": v(1.13, 1.12) * mm, "end": v(1.15, 1.15) * mm});
            skLineSegment(sketch, "E1332", {"start": v(1.15, 1.15) * mm, "end": v(1.15, 1.85) * mm});
            skArc(sketch, "E1333", {"start": v(1.15, 1.85) * mm, "mid": v(1.13, 1.89) * mm, "end": v(1.1, 1.9) * mm});
            skLineSegment(sketch, "E1334", {"start": v(0.6, 1.9) * mm, "end": v(0.4, 1.9) * mm});
            skArc(sketch, "E1335", {"start": v(0.4, 1.9) * mm, "mid": v(0.37, 1.89) * mm, "end": v(0.35, 1.85) * mm});
            skLineSegment(sketch, "E1336", {"start": v(0.35, 1.85) * mm, "end": v(0.35, 1.15) * mm});
            skArc(sketch, "E1337", {"start": v(0.35, 1.15) * mm, "mid": v(0.37, 1.12) * mm, "end": v(0.4, 1.1) * mm});
            skLineSegment(sketch, "E1338", {"start": v(0.4, 1.1) * mm, "end": v(0.6, 1.1) * mm});
            skArc(sketch, "E1339", {"start": v(0.6, 1.1) * mm, "mid": v(0.63, 1.12) * mm, "end": v(0.65, 1.15) * mm});
            skLineSegment(sketch, "E1340", {"start": v(0.65, 1.15) * mm, "end": v(0.65, 1.85) * mm});
            skArc(sketch, "E1341", {"start": v(0.65, 1.85) * mm, "mid": v(0.63, 1.89) * mm, "end": v(0.6, 1.9) * mm});
            skLineSegment(sketch, "E1342", {"start": v(0.1, 1.9) * mm, "end": v(-0.1, 1.9) * mm});
            skArc(sketch, "E1343", {"start": v(-0.1, 1.9) * mm, "mid": v(-0.13, 1.89) * mm, "end": v(-0.15, 1.85) * mm});
            skLineSegment(sketch, "E1344", {"start": v(-0.15, 1.85) * mm, "end": v(-0.15, 1.15) * mm});
            skArc(sketch, "E1345", {"start": v(-0.15, 1.15) * mm, "mid": v(-0.13, 1.12) * mm, "end": v(-0.1, 1.1) * mm});
            skLineSegment(sketch, "E1346", {"start": v(-0.1, 1.1) * mm, "end": v(0.1, 1.1) * mm});
            skArc(sketch, "E1347", {"start": v(0.1, 1.1) * mm, "mid": v(0.13, 1.12) * mm, "end": v(0.15, 1.15) * mm});
            skLineSegment(sketch, "E1348", {"start": v(0.15, 1.15) * mm, "end": v(0.15, 1.85) * mm});
            skArc(sketch, "E1349", {"start": v(0.15, 1.85) * mm, "mid": v(0.13, 1.89) * mm, "end": v(0.1, 1.9) * mm});
            skLineSegment(sketch, "E1350", {"start": v(-0.6, 1.1) * mm, "end": v(-0.4, 1.1) * mm});
            skArc(sketch, "E1351", {"start": v(-0.4, 1.1) * mm, "mid": v(-0.37, 1.12) * mm, "end": v(-0.35, 1.15) * mm});
            skLineSegment(sketch, "E1352", {"start": v(-0.35, 1.15) * mm, "end": v(-0.35, 1.85) * mm});
            skArc(sketch, "E1353", {"start": v(-0.35, 1.85) * mm, "mid": v(-0.37, 1.89) * mm, "end": v(-0.4, 1.9) * mm});
            skLineSegment(sketch, "E1354", {"start": v(-0.4, 1.9) * mm, "end": v(-0.6, 1.9) * mm});
            skArc(sketch, "E1355", {"start": v(-0.6, 1.9) * mm, "mid": v(-0.63, 1.89) * mm, "end": v(-0.65, 1.85) * mm});
            skLineSegment(sketch, "E1356", {"start": v(-0.65, 1.85) * mm, "end": v(-0.65, 1.15) * mm});
            skArc(sketch, "E1357", {"start": v(-0.65, 1.15) * mm, "mid": v(-0.63, 1.12) * mm, "end": v(-0.6, 1.1) * mm});
            skLineSegment(sketch, "E1358", {"start": v(-1.1, 1.1) * mm, "end": v(-0.9, 1.1) * mm});
            skArc(sketch, "E1359", {"start": v(-0.9, 1.1) * mm, "mid": v(-0.87, 1.12) * mm, "end": v(-0.85, 1.15) * mm});
            skLineSegment(sketch, "E1360", {"start": v(-0.85, 1.15) * mm, "end": v(-0.85, 1.85) * mm});
            skArc(sketch, "E1361", {"start": v(-0.85, 1.85) * mm, "mid": v(-0.87, 1.89) * mm, "end": v(-0.9, 1.9) * mm});
            skLineSegment(sketch, "E1362", {"start": v(-0.9, 1.9) * mm, "end": v(-1.1, 1.9) * mm});
            skArc(sketch, "E1363", {"start": v(-1.1, 1.9) * mm, "mid": v(-1.13, 1.89) * mm, "end": v(-1.15, 1.85) * mm});
            skLineSegment(sketch, "E1364", {"start": v(-1.15, 1.85) * mm, "end": v(-1.15, 1.15) * mm});
            skArc(sketch, "E1365", {"start": v(-1.15, 1.15) * mm, "mid": v(-1.13, 1.12) * mm, "end": v(-1.1, 1.1) * mm});
            skLineSegment(sketch, "E1366", {"start": v(-1.6, 1.1) * mm, "end": v(-1.4, 1.1) * mm});
            skArc(sketch, "E1367", {"start": v(-1.4, 1.1) * mm, "mid": v(-1.37, 1.12) * mm, "end": v(-1.35, 1.15) * mm});
            skLineSegment(sketch, "E1368", {"start": v(-1.35, 1.15) * mm, "end": v(-1.35, 1.85) * mm});
            skArc(sketch, "E1369", {"start": v(-1.35, 1.85) * mm, "mid": v(-1.37, 1.89) * mm, "end": v(-1.4, 1.9) * mm});
            skLineSegment(sketch, "E1370", {"start": v(-1.4, 1.9) * mm, "end": v(-1.6, 1.9) * mm});
            skArc(sketch, "E1371", {"start": v(-1.6, 1.9) * mm, "mid": v(-1.63, 1.89) * mm, "end": v(-1.65, 1.85) * mm});
            skLineSegment(sketch, "E1372", {"start": v(-1.65, 1.85) * mm, "end": v(-1.65, 1.15) * mm});
            skArc(sketch, "E1373", {"start": v(-1.65, 1.15) * mm, "mid": v(-1.63, 1.12) * mm, "end": v(-1.6, 1.1) * mm});
            skLineSegment(sketch, "E1374", {"start": v(-2.1, 1.1) * mm, "end": v(-1.9, 1.1) * mm});
            skArc(sketch, "E1375", {"start": v(-1.9, 1.1) * mm, "mid": v(-1.87, 1.12) * mm, "end": v(-1.85, 1.15) * mm});
            skLineSegment(sketch, "E1376", {"start": v(-1.85, 1.15) * mm, "end": v(-1.85, 1.85) * mm});
            skArc(sketch, "E1377", {"start": v(-1.85, 1.85) * mm, "mid": v(-1.87, 1.89) * mm, "end": v(-1.9, 1.9) * mm});
            skLineSegment(sketch, "E1378", {"start": v(-1.9, 1.9) * mm, "end": v(-2.1, 1.9) * mm});
            skArc(sketch, "E1379", {"start": v(-2.1, 1.9) * mm, "mid": v(-2.13, 1.89) * mm, "end": v(-2.15, 1.85) * mm});
            skLineSegment(sketch, "E1380", {"start": v(-2.15, 1.85) * mm, "end": v(-2.15, 1.15) * mm});
            skArc(sketch, "E1381", {"start": v(-2.15, 1.15) * mm, "mid": v(-2.13, 1.12) * mm, "end": v(-2.1, 1.1) * mm});
            skLineSegment(sketch, "E1382", {"start": v(-2.6, 1.1) * mm, "end": v(-2.4, 1.1) * mm});
            skArc(sketch, "E1383", {"start": v(-2.4, 1.1) * mm, "mid": v(-2.37, 1.12) * mm, "end": v(-2.35, 1.15) * mm});
            skLineSegment(sketch, "E1384", {"start": v(-2.35, 1.15) * mm, "end": v(-2.35, 1.85) * mm});
            skArc(sketch, "E1385", {"start": v(-2.35, 1.85) * mm, "mid": v(-2.37, 1.89) * mm, "end": v(-2.4, 1.9) * mm});
            skLineSegment(sketch, "E1386", {"start": v(-2.4, 1.9) * mm, "end": v(-2.6, 1.9) * mm});
            skArc(sketch, "E1387", {"start": v(-2.6, 1.9) * mm, "mid": v(-2.63, 1.89) * mm, "end": v(-2.65, 1.85) * mm});
            skLineSegment(sketch, "E1388", {"start": v(-2.65, 1.85) * mm, "end": v(-2.65, 1.15) * mm});
            skArc(sketch, "E1389", {"start": v(-2.65, 1.15) * mm, "mid": v(-2.63, 1.12) * mm, "end": v(-2.6, 1.1) * mm});
            skLineSegment(sketch, "E1390", {"start": v(2.94, -8.5) * mm, "end": v(2.94, -9.6) * mm});
            skArc(sketch, "E1391", {"start": v(2.94, -9.6) * mm, "mid": v(2.96, -9.64) * mm, "end": v(3, -9.65) * mm});
            skLineSegment(sketch, "E1392", {"start": v(3, -9.65) * mm, "end": v(3.45, -9.65) * mm});
            skArc(sketch, "E1393", {"start": v(3.45, -9.65) * mm, "mid": v(3.48, -9.64) * mm, "end": v(3.5, -9.6) * mm});
            skLineSegment(sketch, "E1394", {"start": v(3.5, -9.6) * mm, "end": v(3.5, -8.5) * mm});
            skArc(sketch, "E1395", {"start": v(3.5, -8.5) * mm, "mid": v(3.48, -8.46) * mm, "end": v(3.45, -8.45) * mm});
            skLineSegment(sketch, "E1396", {"start": v(3.45, -8.45) * mm, "end": v(3, -8.45) * mm});
            skArc(sketch, "E1397", {"start": v(3, -8.45) * mm, "mid": v(2.96, -8.46) * mm, "end": v(2.94, -8.5) * mm});
            skLineSegment(sketch, "E1398", {"start": v(2, -8.5) * mm, "end": v(2, -9.6) * mm});
            skArc(sketch, "E1399", {"start": v(2, -9.6) * mm, "mid": v(2, -9.64) * mm, "end": v(2.04, -9.65) * mm});
            skLineSegment(sketch, "E1400", {"start": v(2.04, -9.65) * mm, "end": v(2.5, -9.65) * mm});
            skArc(sketch, "E1401", {"start": v(2.5, -9.65) * mm, "mid": v(2.53, -9.64) * mm, "end": v(2.55, -9.6) * mm});
            skLineSegment(sketch, "E1402", {"start": v(2.55, -9.6) * mm, "end": v(2.55, -8.5) * mm});
            skArc(sketch, "E1403", {"start": v(2.55, -8.5) * mm, "mid": v(2.53, -8.46) * mm, "end": v(2.5, -8.45) * mm});
            skLineSegment(sketch, "E1404", {"start": v(2.5, -8.45) * mm, "end": v(2.04, -8.45) * mm});
            skArc(sketch, "E1405", {"start": v(2.04, -8.45) * mm, "mid": v(2, -8.46) * mm, "end": v(2, -8.5) * mm});
            skLineSegment(sketch, "E1406", {"start": v(1.04, -8.5) * mm, "end": v(1.04, -9.6) * mm});
            skArc(sketch, "E1407", {"start": v(1.04, -9.6) * mm, "mid": v(1.06, -9.64) * mm, "end": v(1.1, -9.65) * mm});
            skLineSegment(sketch, "E1408", {"start": v(1.1, -9.65) * mm, "end": v(1.55, -9.65) * mm});
            skArc(sketch, "E1409", {"start": v(1.55, -9.65) * mm, "mid": v(1.58, -9.64) * mm, "end": v(1.6, -9.6) * mm});
            skLineSegment(sketch, "E1410", {"start": v(1.6, -9.6) * mm, "end": v(1.6, -8.5) * mm});
            skArc(sketch, "E1411", {"start": v(1.6, -8.5) * mm, "mid": v(1.58, -8.46) * mm, "end": v(1.55, -8.45) * mm});
            skLineSegment(sketch, "E1412", {"start": v(1.55, -8.45) * mm, "end": v(1.1, -8.45) * mm});
            skArc(sketch, "E1413", {"start": v(1.1, -8.45) * mm, "mid": v(1.06, -8.46) * mm, "end": v(1.04, -8.5) * mm});
            skLineSegment(sketch, "E1414", {"start": v(1.04, -11.1) * mm, "end": v(1.04, -12.2) * mm});
            skArc(sketch, "E1415", {"start": v(1.04, -12.2) * mm, "mid": v(1.06, -12.24) * mm, "end": v(1.1, -12.25) * mm});
            skLineSegment(sketch, "E1416", {"start": v(1.1, -12.25) * mm, "end": v(1.55, -12.25) * mm});
            skArc(sketch, "E1417", {"start": v(1.55, -12.25) * mm, "mid": v(1.58, -12.24) * mm, "end": v(1.6, -12.2) * mm});
            skLineSegment(sketch, "E1418", {"start": v(1.6, -12.2) * mm, "end": v(1.6, -11.1) * mm});
            skArc(sketch, "E1419", {"start": v(1.6, -11.1) * mm, "mid": v(1.58, -11.06) * mm, "end": v(1.55, -11.05) * mm});
            skLineSegment(sketch, "E1420", {"start": v(1.55, -11.05) * mm, "end": v(1.1, -11.05) * mm});
            skArc(sketch, "E1421", {"start": v(1.1, -11.05) * mm, "mid": v(1.06, -11.06) * mm, "end": v(1.04, -11.1) * mm});
            skLineSegment(sketch, "E1422", {"start": v(2.94, -11.1) * mm, "end": v(2.94, -12.2) * mm});
            skArc(sketch, "E1423", {"start": v(2.94, -12.2) * mm, "mid": v(2.96, -12.24) * mm, "end": v(3, -12.25) * mm});
            skLineSegment(sketch, "E1424", {"start": v(3, -12.25) * mm, "end": v(3.45, -12.25) * mm});
            skArc(sketch, "E1425", {"start": v(3.45, -12.25) * mm, "mid": v(3.48, -12.24) * mm, "end": v(3.5, -12.2) * mm});
            skLineSegment(sketch, "E1426", {"start": v(3.5, -12.2) * mm, "end": v(3.5, -11.1) * mm});
            skArc(sketch, "E1427", {"start": v(3.5, -11.1) * mm, "mid": v(3.48, -11.06) * mm, "end": v(3.45, -11.05) * mm});
            skLineSegment(sketch, "E1428", {"start": v(3.45, -11.05) * mm, "end": v(3, -11.05) * mm});
            skArc(sketch, "E1429", {"start": v(3, -11.05) * mm, "mid": v(2.96, -11.06) * mm, "end": v(2.94, -11.1) * mm});
            skLineSegment(sketch, "E1430", {"start": v(6.07, -8.91) * mm, "end": v(5.43, -8.91) * mm});
            skArc(sketch, "E1431", {"start": v(5.43, -8.91) * mm, "mid": v(5.39, -8.93) * mm, "end": v(5.37, -8.98) * mm});
            skLineSegment(sketch, "E1432", {"start": v(5.37, -8.98) * mm, "end": v(5.37, -9.61) * mm});
            skArc(sketch, "E1433", {"start": v(5.37, -9.61) * mm, "mid": v(5.39, -9.66) * mm, "end": v(5.43, -9.68) * mm});
            skLineSegment(sketch, "E1434", {"start": v(5.43, -9.68) * mm, "end": v(6.07, -9.68) * mm});
            skArc(sketch, "E1435", {"start": v(6.07, -9.68) * mm, "mid": v(6.11, -9.66) * mm, "end": v(6.13, -9.61) * mm});
            skLineSegment(sketch, "E1436", {"start": v(6.13, -9.61) * mm, "end": v(6.13, -8.98) * mm});
            skArc(sketch, "E1437", {"start": v(6.13, -8.98) * mm, "mid": v(6.11, -8.93) * mm, "end": v(6.07, -8.91) * mm});
            skLineSegment(sketch, "E1438", {"start": v(4.57, -8.91) * mm, "end": v(3.93, -8.91) * mm});
            skArc(sketch, "E1439", {"start": v(3.93, -8.91) * mm, "mid": v(3.89, -8.93) * mm, "end": v(3.87, -8.98) * mm});
            skLineSegment(sketch, "E1440", {"start": v(3.87, -8.98) * mm, "end": v(3.87, -9.61) * mm});
            skArc(sketch, "E1441", {"start": v(3.87, -9.61) * mm, "mid": v(3.89, -9.66) * mm, "end": v(3.93, -9.68) * mm});
            skLineSegment(sketch, "E1442", {"start": v(3.93, -9.68) * mm, "end": v(4.57, -9.68) * mm});
            skArc(sketch, "E1443", {"start": v(4.57, -9.68) * mm, "mid": v(4.61, -9.66) * mm, "end": v(4.63, -9.61) * mm});
            skLineSegment(sketch, "E1444", {"start": v(4.63, -9.61) * mm, "end": v(4.63, -8.98) * mm});
            skArc(sketch, "E1445", {"start": v(4.63, -8.98) * mm, "mid": v(4.61, -8.93) * mm, "end": v(4.57, -8.91) * mm});
            skLineSegment(sketch, "E1446", {"start": v(4.27, -7.21) * mm, "end": v(3.63, -7.21) * mm});
            skArc(sketch, "E1447", {"start": v(3.63, -7.21) * mm, "mid": v(3.59, -7.23) * mm, "end": v(3.57, -7.28) * mm});
            skLineSegment(sketch, "E1448", {"start": v(3.57, -7.28) * mm, "end": v(3.57, -7.91) * mm});
            skArc(sketch, "E1449", {"start": v(3.57, -7.91) * mm, "mid": v(3.59, -7.96) * mm, "end": v(3.63, -7.98) * mm});
            skLineSegment(sketch, "E1450", {"start": v(3.63, -7.98) * mm, "end": v(4.27, -7.98) * mm});
            skArc(sketch, "E1451", {"start": v(4.27, -7.98) * mm, "mid": v(4.31, -7.96) * mm, "end": v(4.33, -7.91) * mm});
            skLineSegment(sketch, "E1452", {"start": v(4.33, -7.91) * mm, "end": v(4.33, -7.28) * mm});
            skArc(sketch, "E1453", {"start": v(4.33, -7.28) * mm, "mid": v(4.31, -7.23) * mm, "end": v(4.27, -7.21) * mm});
            skLineSegment(sketch, "E1454", {"start": v(2.77, -7.21) * mm, "end": v(2.13, -7.21) * mm});
            skArc(sketch, "E1455", {"start": v(2.13, -7.21) * mm, "mid": v(2.09, -7.23) * mm, "end": v(2.07, -7.28) * mm});
            skLineSegment(sketch, "E1456", {"start": v(2.07, -7.28) * mm, "end": v(2.07, -7.91) * mm});
            skArc(sketch, "E1457", {"start": v(2.07, -7.91) * mm, "mid": v(2.09, -7.96) * mm, "end": v(2.13, -7.98) * mm});
            skLineSegment(sketch, "E1458", {"start": v(2.13, -7.98) * mm, "end": v(2.77, -7.98) * mm});
            skArc(sketch, "E1459", {"start": v(2.77, -7.98) * mm, "mid": v(2.81, -7.96) * mm, "end": v(2.83, -7.91) * mm});
            skLineSegment(sketch, "E1460", {"start": v(2.83, -7.91) * mm, "end": v(2.83, -7.28) * mm});
            skArc(sketch, "E1461", {"start": v(2.83, -7.28) * mm, "mid": v(2.81, -7.23) * mm, "end": v(2.77, -7.21) * mm});
            skLineSegment(sketch, "E1462", {"start": v(-4.27, -7.98) * mm, "end": v(-3.63, -7.98) * mm});
            skArc(sketch, "E1463", {"start": v(-3.63, -7.98) * mm, "mid": v(-3.59, -7.96) * mm, "end": v(-3.57, -7.91) * mm});
            skLineSegment(sketch, "E1464", {"start": v(-3.57, -7.91) * mm, "end": v(-3.57, -7.28) * mm});
            skArc(sketch, "E1465", {"start": v(-3.57, -7.28) * mm, "mid": v(-3.59, -7.23) * mm, "end": v(-3.63, -7.21) * mm});
            skLineSegment(sketch, "E1466", {"start": v(-3.63, -7.21) * mm, "end": v(-4.27, -7.21) * mm});
            skArc(sketch, "E1467", {"start": v(-4.27, -7.21) * mm, "mid": v(-4.31, -7.23) * mm, "end": v(-4.33, -7.28) * mm});
            skLineSegment(sketch, "E1468", {"start": v(-4.33, -7.28) * mm, "end": v(-4.33, -7.91) * mm});
            skArc(sketch, "E1469", {"start": v(-4.33, -7.91) * mm, "mid": v(-4.31, -7.96) * mm, "end": v(-4.27, -7.98) * mm});
            skLineSegment(sketch, "E1470", {"start": v(-2.77, -7.98) * mm, "end": v(-2.13, -7.98) * mm});
            skArc(sketch, "E1471", {"start": v(-2.13, -7.98) * mm, "mid": v(-2.09, -7.96) * mm, "end": v(-2.07, -7.91) * mm});
            skLineSegment(sketch, "E1472", {"start": v(-2.07, -7.91) * mm, "end": v(-2.07, -7.28) * mm});
            skArc(sketch, "E1473", {"start": v(-2.07, -7.28) * mm, "mid": v(-2.09, -7.23) * mm, "end": v(-2.13, -7.21) * mm});
            skLineSegment(sketch, "E1474", {"start": v(-2.13, -7.21) * mm, "end": v(-2.77, -7.21) * mm});
            skArc(sketch, "E1475", {"start": v(-2.77, -7.21) * mm, "mid": v(-2.81, -7.23) * mm, "end": v(-2.83, -7.28) * mm});
            skLineSegment(sketch, "E1476", {"start": v(-2.83, -7.28) * mm, "end": v(-2.83, -7.91) * mm});
            skArc(sketch, "E1477", {"start": v(-2.83, -7.91) * mm, "mid": v(-2.81, -7.96) * mm, "end": v(-2.77, -7.98) * mm});
            skLineSegment(sketch, "E1478", {"start": v(-5.8, 7.32) * mm, "end": v(-6.11, 6.77) * mm});
            skArc(sketch, "E1479", {"start": v(-6.11, 6.77) * mm, "mid": v(-6.12, 6.72) * mm, "end": v(-6.09, 6.68) * mm});
            skLineSegment(sketch, "E1480", {"start": v(-6.09, 6.68) * mm, "end": v(-5.54, 6.36) * mm});
            skArc(sketch, "E1481", {"start": v(-5.54, 6.36) * mm, "mid": v(-5.5, 6.36) * mm, "end": v(-5.45, 6.39) * mm});
            skLineSegment(sketch, "E1482", {"start": v(-5.45, 6.39) * mm, "end": v(-5.14, 6.93) * mm});
            skArc(sketch, "E1483", {"start": v(-5.14, 6.93) * mm, "mid": v(-5.13, 6.98) * mm, "end": v(-5.16, 7.03) * mm});
            skLineSegment(sketch, "E1484", {"start": v(-5.16, 7.03) * mm, "end": v(-5.7, 7.34) * mm});
            skArc(sketch, "E1485", {"start": v(-5.7, 7.34) * mm, "mid": v(-5.76, 7.35) * mm, "end": v(-5.8, 7.32) * mm});
            skLineSegment(sketch, "E1486", {"start": v(-6.55, 6.02) * mm, "end": v(-6.86, 5.47) * mm});
            skArc(sketch, "E1487", {"start": v(-6.86, 5.47) * mm, "mid": v(-6.87, 5.42) * mm, "end": v(-6.84, 5.38) * mm});
            skLineSegment(sketch, "E1488", {"start": v(-6.84, 5.38) * mm, "end": v(-6.3, 5.06) * mm});
            skArc(sketch, "E1489", {"start": v(-6.3, 5.06) * mm, "mid": v(-6.24, 5.06) * mm, "end": v(-6.2, 5.09) * mm});
            skLineSegment(sketch, "E1490", {"start": v(-6.2, 5.09) * mm, "end": v(-5.89, 5.63) * mm});
            skArc(sketch, "E1491", {"start": v(-5.89, 5.63) * mm, "mid": v(-5.88, 5.69) * mm, "end": v(-5.91, 5.73) * mm});
            skLineSegment(sketch, "E1492", {"start": v(-5.91, 5.73) * mm, "end": v(-6.46, 6.04) * mm});
            skArc(sketch, "E1493", {"start": v(-6.46, 6.04) * mm, "mid": v(-6.5, 6.05) * mm, "end": v(-6.55, 6.02) * mm});
            skLineSegment(sketch, "E1494", {"start": v(6.86, 5.47) * mm, "end": v(6.55, 6.02) * mm});
            skArc(sketch, "E1495", {"start": v(6.55, 6.02) * mm, "mid": v(6.5, 6.05) * mm, "end": v(6.46, 6.04) * mm});
            skLineSegment(sketch, "E1496", {"start": v(6.46, 6.04) * mm, "end": v(5.91, 5.73) * mm});
            skArc(sketch, "E1497", {"start": v(5.91, 5.73) * mm, "mid": v(5.88, 5.69) * mm, "end": v(5.89, 5.63) * mm});
            skLineSegment(sketch, "E1498", {"start": v(5.89, 5.63) * mm, "end": v(6.2, 5.09) * mm});
            skArc(sketch, "E1499", {"start": v(6.2, 5.09) * mm, "mid": v(6.24, 5.06) * mm, "end": v(6.3, 5.06) * mm});
            skLineSegment(sketch, "E1500", {"start": v(6.3, 5.06) * mm, "end": v(6.84, 5.38) * mm});
            skArc(sketch, "E1501", {"start": v(6.84, 5.38) * mm, "mid": v(6.87, 5.42) * mm, "end": v(6.86, 5.47) * mm});
            skLineSegment(sketch, "E1502", {"start": v(6.11, 6.77) * mm, "end": v(5.8, 7.32) * mm});
            skArc(sketch, "E1503", {"start": v(5.8, 7.32) * mm, "mid": v(5.76, 7.35) * mm, "end": v(5.7, 7.34) * mm});
            skLineSegment(sketch, "E1504", {"start": v(5.7, 7.34) * mm, "end": v(5.16, 7.03) * mm});
            skArc(sketch, "E1505", {"start": v(5.16, 7.03) * mm, "mid": v(5.13, 6.98) * mm, "end": v(5.14, 6.93) * mm});
            skLineSegment(sketch, "E1506", {"start": v(5.14, 6.93) * mm, "end": v(5.45, 6.39) * mm});
            skArc(sketch, "E1507", {"start": v(5.45, 6.39) * mm, "mid": v(5.5, 6.36) * mm, "end": v(5.54, 6.36) * mm});
            skLineSegment(sketch, "E1508", {"start": v(5.54, 6.36) * mm, "end": v(6.09, 6.68) * mm});
            skArc(sketch, "E1509", {"start": v(6.09, 6.68) * mm, "mid": v(6.12, 6.72) * mm, "end": v(6.11, 6.77) * mm});
            skLineSegment(sketch, "E1510", {"start": v(19.02, 6.17) * mm, "end": v(15.6, 5.05) * mm});
            skArc(sketch, "E1511", {"start": v(15.56, 5.17) * mm, "mid": v(15.48, 5) * mm, "end": v(15.64, 4.93) * mm});
            skArc(sketch, "E1512", {"start": v(19.06, 6.05) * mm, "mid": v(19.14, 6.21) * mm, "end": v(18.98, 6.3) * mm});
            skLineSegment(sketch, "E1513", {"start": v(15.6, 5.05) * mm, "end": v(15.4, 4.95) * mm});
            skArc(sketch, "E1514", {"start": v(15.34, 5.06) * mm, "mid": v(15.29, 4.89) * mm, "end": v(15.46, 4.83) * mm});
            skArc(sketch, "E1515", {"start": v(15.66, 4.94) * mm, "mid": v(15.71, 5.1) * mm, "end": v(15.55, 5.16) * mm});
            skLineSegment(sketch, "E1516", {"start": v(15.4, 4.95) * mm, "end": v(15.21, 4.83) * mm});
            skArc(sketch, "E1517", {"start": v(15.15, 4.93) * mm, "mid": v(15.1, 4.76) * mm, "end": v(15.28, 4.72) * mm});
            skArc(sketch, "E1518", {"start": v(15.47, 4.84) * mm, "mid": v(15.5, 5.01) * mm, "end": v(15.33, 5.05) * mm});
            skLineSegment(sketch, "E1519", {"start": v(15.21, 4.83) * mm, "end": v(15.04, 4.69) * mm});
            skArc(sketch, "E1520", {"start": v(14.96, 4.79) * mm, "mid": v(14.94, 4.61) * mm, "end": v(15.12, 4.6) * mm});
            skArc(sketch, "E1521", {"start": v(15.3, 4.73) * mm, "mid": v(15.31, 4.9) * mm, "end": v(15.14, 4.92) * mm});
            skLineSegment(sketch, "E1522", {"start": v(15.04, 4.69) * mm, "end": v(14.88, 4.54) * mm});
            skArc(sketch, "E1523", {"start": v(14.8, 4.63) * mm, "mid": v(14.8, 4.45) * mm, "end": v(14.97, 4.45) * mm});
            skArc(sketch, "E1524", {"start": v(15.13, 4.6) * mm, "mid": v(15.13, 4.78) * mm, "end": v(14.95, 4.78) * mm});
            skLineSegment(sketch, "E1525", {"start": v(14.88, 4.54) * mm, "end": v(14.74, 4.37) * mm});
            skArc(sketch, "E1526", {"start": v(14.65, 4.45) * mm, "mid": v(14.66, 4.28) * mm, "end": v(14.84, 4.3) * mm});
            skArc(sketch, "E1527", {"start": v(14.98, 4.46) * mm, "mid": v(14.97, 4.63) * mm, "end": v(14.79, 4.62) * mm});
            skLineSegment(sketch, "E1528", {"start": v(14.74, 4.37) * mm, "end": v(14.62, 4.2) * mm});
            skArc(sketch, "E1529", {"start": v(14.52, 4.27) * mm, "mid": v(14.55, 4.1) * mm, "end": v(14.72, 4.12) * mm});
            skArc(sketch, "E1530", {"start": v(14.85, 4.3) * mm, "mid": v(14.82, 4.47) * mm, "end": v(14.64, 4.44) * mm});
            skLineSegment(sketch, "E1531", {"start": v(14.62, 4.2) * mm, "end": v(14.51, 4) * mm});
            skArc(sketch, "E1532", {"start": v(14.4, 4.07) * mm, "mid": v(14.45, 3.9) * mm, "end": v(14.62, 3.94) * mm});
            skArc(sketch, "E1533", {"start": v(14.73, 4.13) * mm, "mid": v(14.68, 4.3) * mm, "end": v(14.51, 4.26) * mm});
            skLineSegment(sketch, "E1534", {"start": v(14.51, 4) * mm, "end": v(14.43, 3.8) * mm});
            skArc(sketch, "E1535", {"start": v(14.31, 3.86) * mm, "mid": v(14.38, 3.7) * mm, "end": v(14.54, 3.76) * mm});
            skArc(sketch, "E1536", {"start": v(14.63, 3.96) * mm, "mid": v(14.56, 4.12) * mm, "end": v(14.4, 4.06) * mm});
            skLineSegment(sketch, "E1537", {"start": v(14.43, 3.8) * mm, "end": v(14.36, 3.6) * mm});
            skArc(sketch, "E1538", {"start": v(14.24, 3.64) * mm, "mid": v(14.32, 3.48) * mm, "end": v(14.48, 3.56) * mm});
            skArc(sketch, "E1539", {"start": v(14.54, 3.77) * mm, "mid": v(14.47, 3.93) * mm, "end": v(14.3, 3.85) * mm});
            skLineSegment(sketch, "E1540", {"start": v(14.36, 3.6) * mm, "end": v(14.3, 3.4) * mm});
            skArc(sketch, "E1541", {"start": v(14.19, 3.42) * mm, "mid": v(14.28, 3.27) * mm, "end": v(14.43, 3.36) * mm});
            skArc(sketch, "E1542", {"start": v(14.48, 3.57) * mm, "mid": v(14.39, 3.72) * mm, "end": v(14.24, 3.63) * mm});
            skLineSegment(sketch, "E1543", {"start": v(14.3, 3.4) * mm, "end": v(14.28, 3.18) * mm});
            skArc(sketch, "E1544", {"start": v(14.16, 3.2) * mm, "mid": v(14.26, 3.05) * mm, "end": v(14.4, 3.16) * mm});
            skArc(sketch, "E1545", {"start": v(14.43, 3.38) * mm, "mid": v(14.32, 3.52) * mm, "end": v(14.18, 3.4) * mm});
            skLineSegment(sketch, "E1546", {"start": v(14.28, 3.18) * mm, "end": v(14.27, 2.95) * mm});
            skArc(sketch, "E1547", {"start": v(14.15, 2.96) * mm, "mid": v(14.27, 2.83) * mm, "end": v(14.4, 2.95) * mm});
            skArc(sketch, "E1548", {"start": v(14.4, 3.17) * mm, "mid": v(14.28, 3.3) * mm, "end": v(14.16, 3.18) * mm});
            skLineSegment(sketch, "E1549", {"start": v(14.27, 2.95) * mm, "end": v(14.29, 2.73) * mm});
            skArc(sketch, "E1550", {"start": v(14.16, 2.72) * mm, "mid": v(14.3, 2.6) * mm, "end": v(14.41, 2.74) * mm});
            skArc(sketch, "E1551", {"start": v(14.4, 2.96) * mm, "mid": v(14.27, 3.08) * mm, "end": v(14.15, 2.95) * mm});
            skLineSegment(sketch, "E1552", {"start": v(14.29, 2.73) * mm, "end": v(14.33, 2.5) * mm});
            skArc(sketch, "E1553", {"start": v(14.2, 2.49) * mm, "mid": v(14.35, 2.39) * mm, "end": v(14.45, 2.53) * mm});
            skArc(sketch, "E1554", {"start": v(14.41, 2.75) * mm, "mid": v(14.27, 2.86) * mm, "end": v(14.17, 2.71) * mm});
            skLineSegment(sketch, "E1555", {"start": v(14.33, 2.5) * mm, "end": v(14.38, 2.3) * mm});
            skArc(sketch, "E1556", {"start": v(14.26, 2.27) * mm, "mid": v(14.42, 2.18) * mm, "end": v(14.5, 2.33) * mm});
            skArc(sketch, "E1557", {"start": v(14.45, 2.54) * mm, "mid": v(14.3, 2.63) * mm, "end": v(14.2, 2.48) * mm});
            skLineSegment(sketch, "E1558", {"start": v(14.38, 2.3) * mm, "end": v(14.47, 2.07) * mm});
            skArc(sketch, "E1559", {"start": v(14.35, 2.03) * mm, "mid": v(14.52, 1.96) * mm, "end": v(14.59, 2.12) * mm});
            skArc(sketch, "E1560", {"start": v(14.5, 2.35) * mm, "mid": v(14.34, 2.42) * mm, "end": v(14.27, 2.26) * mm});
            skLineSegment(sketch, "E1561", {"start": v(14.47, 2.07) * mm, "end": v(14.57, 1.87) * mm});
            skArc(sketch, "E1562", {"start": v(14.46, 1.81) * mm, "mid": v(14.63, 1.76) * mm, "end": v(14.69, 1.93) * mm});
            skArc(sketch, "E1563", {"start": v(14.58, 2.13) * mm, "mid": v(14.41, 2.18) * mm, "end": v(14.36, 2.02) * mm});
            skLineSegment(sketch, "E1564", {"start": v(14.57, 1.87) * mm, "end": v(14.7, 1.68) * mm});
            skArc(sketch, "E1565", {"start": v(14.59, 1.62) * mm, "mid": v(14.76, 1.58) * mm, "end": v(14.8, 1.75) * mm});
            skArc(sketch, "E1566", {"start": v(14.68, 1.94) * mm, "mid": v(14.5, 1.98) * mm, "end": v(14.47, 1.8) * mm});
            skLineSegment(sketch, "E1567", {"start": v(14.7, 1.68) * mm, "end": v(14.83, 1.51) * mm});
            skArc(sketch, "E1568", {"start": v(14.73, 1.43) * mm, "mid": v(14.9, 1.41) * mm, "end": v(14.93, 1.6) * mm});
            skArc(sketch, "E1569", {"start": v(14.8, 1.76) * mm, "mid": v(14.62, 1.78) * mm, "end": v(14.6, 1.6) * mm});
            skLineSegment(sketch, "E1570", {"start": v(14.83, 1.51) * mm, "end": v(14.98, 1.36) * mm});
            skArc(sketch, "E1571", {"start": v(14.9, 1.27) * mm, "mid": v(15.07, 1.27) * mm, "end": v(15.07, 1.44) * mm});
            skArc(sketch, "E1572", {"start": v(14.92, 1.6) * mm, "mid": v(14.74, 1.6) * mm, "end": v(14.74, 1.43) * mm});
            skLineSegment(sketch, "E1573", {"start": v(14.98, 1.36) * mm, "end": v(15.15, 1.21) * mm});
            skArc(sketch, "E1574", {"start": v(15.07, 1.12) * mm, "mid": v(15.24, 1.13) * mm, "end": v(15.23, 1.3) * mm});
            skArc(sketch, "E1575", {"start": v(15.06, 1.45) * mm, "mid": v(14.89, 1.44) * mm, "end": v(14.9, 1.26) * mm});
            skLineSegment(sketch, "E1576", {"start": v(15.15, 1.21) * mm, "end": v(15.33, 1.1) * mm});
            skArc(sketch, "E1577", {"start": v(15.25, 0.99) * mm, "mid": v(15.43, 1.02) * mm, "end": v(15.4, 1.2) * mm});
            skArc(sketch, "E1578", {"start": v(15.22, 1.32) * mm, "mid": v(15.05, 1.29) * mm, "end": v(15.08, 1.11) * mm});
            skLineSegment(sketch, "E1579", {"start": v(15.33, 1.1) * mm, "end": v(15.51, 0.98) * mm});
            skArc(sketch, "E1580", {"start": v(15.45, 0.88) * mm, "mid": v(15.62, 0.92) * mm, "end": v(15.57, 1.1) * mm});
            skArc(sketch, "E1581", {"start": v(15.39, 1.2) * mm, "mid": v(15.22, 1.15) * mm, "end": v(15.26, 0.98) * mm});
            skLineSegment(sketch, "E1582", {"start": v(15.51, 0.98) * mm, "end": v(15.71, 0.9) * mm});
            skArc(sketch, "E1583", {"start": v(15.66, 0.78) * mm, "mid": v(15.83, 0.85) * mm, "end": v(15.76, 1.01) * mm});
            skArc(sketch, "E1584", {"start": v(15.56, 1.1) * mm, "mid": v(15.4, 1.04) * mm, "end": v(15.46, 0.87) * mm});
            skLineSegment(sketch, "E1585", {"start": v(15.71, 0.9) * mm, "end": v(15.92, 0.83) * mm});
            skArc(sketch, "E1586", {"start": v(15.88, 0.7) * mm, "mid": v(16.03, 0.79) * mm, "end": v(15.96, 0.95) * mm});
            skArc(sketch, "E1587", {"start": v(15.75, 1.02) * mm, "mid": v(15.6, 0.94) * mm, "end": v(15.67, 0.78) * mm});
            skLineSegment(sketch, "E1588", {"start": v(15.92, 0.83) * mm, "end": v(16.13, 0.78) * mm});
            skArc(sketch, "E1589", {"start": v(16.1, 0.66) * mm, "mid": v(16.25, 0.75) * mm, "end": v(16.16, 0.9) * mm});
            skArc(sketch, "E1590", {"start": v(15.94, 0.95) * mm, "mid": v(15.8, 0.86) * mm, "end": v(15.89, 0.7) * mm});
            skLineSegment(sketch, "E1591", {"start": v(16.13, 0.78) * mm, "end": v(16.34, 0.75) * mm});
            skArc(sketch, "E1592", {"start": v(16.33, 0.63) * mm, "mid": v(16.47, 0.74) * mm, "end": v(16.36, 0.88) * mm});
            skArc(sketch, "E1593", {"start": v(16.14, 0.9) * mm, "mid": v(16, 0.8) * mm, "end": v(16.11, 0.66) * mm});
            skLineSegment(sketch, "E1594", {"start": v(16.34, 0.75) * mm, "end": v(16.56, 0.74) * mm});
            skArc(sketch, "E1595", {"start": v(16.56, 0.62) * mm, "mid": v(16.69, 0.74) * mm, "end": v(16.57, 0.87) * mm});
            skArc(sketch, "E1596", {"start": v(16.35, 0.88) * mm, "mid": v(16.22, 0.76) * mm, "end": v(16.34, 0.63) * mm});
            skLineSegment(sketch, "E1597", {"start": v(16.56, 0.74) * mm, "end": v(16.79, 0.76) * mm});
            skArc(sketch, "E1598", {"start": v(16.8, 0.63) * mm, "mid": v(16.91, 0.77) * mm, "end": v(16.78, 0.88) * mm});
            skArc(sketch, "E1599", {"start": v(16.56, 0.87) * mm, "mid": v(16.44, 0.74) * mm, "end": v(16.57, 0.62) * mm});
            skLineSegment(sketch, "E1600", {"start": v(16.79, 0.76) * mm, "end": v(17, 0.8) * mm});
            skArc(sketch, "E1601", {"start": v(17.03, 0.67) * mm, "mid": v(17.13, 0.82) * mm, "end": v(16.99, 0.92) * mm});
            skArc(sketch, "E1602", {"start": v(16.77, 0.88) * mm, "mid": v(16.66, 0.74) * mm, "end": v(16.8, 0.64) * mm});
            skLineSegment(sketch, "E1603", {"start": v(17, 0.8) * mm, "end": v(17.25, 0.86) * mm});
            skArc(sketch, "E1604", {"start": v(17.28, 0.74) * mm, "mid": v(17.37, 0.9) * mm, "end": v(17.22, 0.98) * mm});
            skArc(sketch, "E1605", {"start": v(16.98, 0.92) * mm, "mid": v(16.89, 0.76) * mm, "end": v(17.04, 0.68) * mm});
            skLineSegment(sketch, "E1606", {"start": v(17.25, 0.86) * mm, "end": v(20.41, 1.9) * mm});
            skArc(sketch, "E1607", {"start": v(20.45, 1.77) * mm, "mid": v(20.53, 1.93) * mm, "end": v(20.38, 2.01) * mm});
            skArc(sketch, "E1608", {"start": v(17.2, 0.98) * mm, "mid": v(17.13, 0.82) * mm, "end": v(17.29, 0.74) * mm});
            skLineSegment(sketch, "E1609", {"start": v(20.41, 1.9) * mm, "end": v(22.3, 3.26) * mm});
            skArc(sketch, "E1610", {"start": v(22.37, 3.16) * mm, "mid": v(22.4, 3.34) * mm, "end": v(22.23, 3.36) * mm});
            skArc(sketch, "E1611", {"start": v(20.34, 2) * mm, "mid": v(20.31, 1.82) * mm, "end": v(20.49, 1.8) * mm});
            skLineSegment(sketch, "E1612", {"start": v(22.3, 3.26) * mm, "end": v(22.96, 4.08) * mm});
            skArc(sketch, "E1613", {"start": v(23.06, 4) * mm, "mid": v(23.04, 4.18) * mm, "end": v(22.87, 4.16) * mm});
            skArc(sketch, "E1614", {"start": v(22.2, 3.34) * mm, "mid": v(22.22, 3.17) * mm, "end": v(22.4, 3.18) * mm});
            skLineSegment(sketch, "E1615", {"start": v(22.96, 4.08) * mm, "end": v(22.38, 5.9) * mm});
            skArc(sketch, "E1616", {"start": v(22.5, 5.94) * mm, "mid": v(22.34, 6.02) * mm, "end": v(22.26, 5.86) * mm});
            skArc(sketch, "E1617", {"start": v(22.85, 4.05) * mm, "mid": v(23, 3.97) * mm, "end": v(23.08, 4.12) * mm});
            skLineSegment(sketch, "E1618", {"start": v(22.38, 5.9) * mm, "end": v(21.35, 6.17) * mm});
            skArc(sketch, "E1619", {"start": v(21.39, 6.3) * mm, "mid": v(21.23, 6.2) * mm, "end": v(21.32, 6.05) * mm});
            skArc(sketch, "E1620", {"start": v(22.34, 5.78) * mm, "mid": v(22.5, 5.86) * mm, "end": v(22.4, 6.02) * mm});
            skLineSegment(sketch, "E1621", {"start": v(21.35, 6.17) * mm, "end": v(19.02, 6.17) * mm});
            skArc(sketch, "E1622", {"start": v(19.02, 6.3) * mm, "mid": v(18.9, 6.17) * mm, "end": v(19.02, 6.05) * mm});
            skArc(sketch, "E1623", {"start": v(21.35, 6.05) * mm, "mid": v(21.48, 6.17) * mm, "end": v(21.35, 6.3) * mm});
            skLineSegment(sketch, "E1624", {"start": v(14.3, 3.36) * mm, "end": v(14.94, 1.4) * mm});
            skArc(sketch, "E1625", {"start": v(14.82, 1.36) * mm, "mid": v(14.98, 1.28) * mm, "end": v(15.06, 1.44) * mm});
            skArc(sketch, "E1626", {"start": v(14.42, 3.4) * mm, "mid": v(14.27, 3.48) * mm, "end": v(14.19, 3.32) * mm});
            skLineSegment(sketch, "E1627", {"start": v(14.58, 4.12) * mm, "end": v(15.62, 0.94) * mm});
            skArc(sketch, "E1628", {"start": v(15.5, 0.9) * mm, "mid": v(15.65, 0.82) * mm, "end": v(15.73, 0.98) * mm});
            skArc(sketch, "E1629", {"start": v(14.7, 4.16) * mm, "mid": v(14.54, 4.24) * mm, "end": v(14.46, 4.09) * mm});
            skLineSegment(sketch, "E1630", {"start": v(14.95, 4.6) * mm, "end": v(16.2, 0.77) * mm});
            skArc(sketch, "E1631", {"start": v(16.08, 0.73) * mm, "mid": v(16.23, 0.65) * mm, "end": v(16.32, 0.8) * mm});
            skArc(sketch, "E1632", {"start": v(15.07, 4.64) * mm, "mid": v(14.91, 4.72) * mm, "end": v(14.83, 4.56) * mm});
            skLineSegment(sketch, "E1633", {"start": v(15.37, 4.93) * mm, "end": v(16.73, 0.76) * mm});
            skArc(sketch, "E1634", {"start": v(16.6, 0.72) * mm, "mid": v(16.77, 0.64) * mm, "end": v(16.85, 0.8) * mm});
            skArc(sketch, "E1635", {"start": v(15.5, 4.97) * mm, "mid": v(15.33, 5.05) * mm, "end": v(15.25, 4.89) * mm});
            skLineSegment(sketch, "E1636", {"start": v(15.83, 5.12) * mm, "end": v(17.22, 0.86) * mm});
            skArc(sketch, "E1637", {"start": v(17.1, 0.82) * mm, "mid": v(17.26, 0.74) * mm, "end": v(17.34, 0.9) * mm});
            skArc(sketch, "E1638", {"start": v(15.95, 5.16) * mm, "mid": v(15.8, 5.24) * mm, "end": v(15.71, 5.09) * mm});
            skLineSegment(sketch, "E1639", {"start": v(16.3, 5.28) * mm, "end": v(17.7, 1) * mm});
            skArc(sketch, "E1640", {"start": v(17.58, 0.97) * mm, "mid": v(17.73, 0.89) * mm, "end": v(17.81, 1.05) * mm});
            skArc(sketch, "E1641", {"start": v(16.43, 5.32) * mm, "mid": v(16.27, 5.4) * mm, "end": v(16.19, 5.24) * mm});
            skLineSegment(sketch, "E1642", {"start": v(16.78, 5.44) * mm, "end": v(18.17, 1.16) * mm});
            skArc(sketch, "E1643", {"start": v(18.05, 1.12) * mm, "mid": v(18.21, 1.04) * mm, "end": v(18.3, 1.2) * mm});
            skArc(sketch, "E1644", {"start": v(16.9, 5.47) * mm, "mid": v(16.74, 5.55) * mm, "end": v(16.66, 5.4) * mm});
            skLineSegment(sketch, "E1645", {"start": v(17.26, 5.6) * mm, "end": v(18.65, 1.32) * mm});
            skArc(sketch, "E1646", {"start": v(18.53, 1.28) * mm, "mid": v(18.69, 1.2) * mm, "end": v(18.77, 1.36) * mm});
            skArc(sketch, "E1647", {"start": v(17.38, 5.63) * mm, "mid": v(17.22, 5.71) * mm, "end": v(17.14, 5.55) * mm});
            skLineSegment(sketch, "E1648", {"start": v(17.73, 5.75) * mm, "end": v(19.12, 1.47) * mm});
            skArc(sketch, "E1649", {"start": v(19, 1.43) * mm, "mid": v(19.16, 1.35) * mm, "end": v(19.24, 1.51) * mm});
            skArc(sketch, "E1650", {"start": v(17.85, 5.79) * mm, "mid": v(17.7, 5.87) * mm, "end": v(17.61, 5.7) * mm});
            skLineSegment(sketch, "E1651", {"start": v(18.2, 5.9) * mm, "end": v(19.6, 1.63) * mm});
            skArc(sketch, "E1652", {"start": v(19.48, 1.59) * mm, "mid": v(19.64, 1.5) * mm, "end": v(19.72, 1.67) * mm});
            skArc(sketch, "E1653", {"start": v(18.33, 5.94) * mm, "mid": v(18.17, 6.02) * mm, "end": v(18.09, 5.87) * mm});
            skLineSegment(sketch, "E1654", {"start": v(18.68, 6.06) * mm, "end": v(20.07, 1.78) * mm});
            skArc(sketch, "E1655", {"start": v(19.95, 1.74) * mm, "mid": v(20.11, 1.66) * mm, "end": v(20.2, 1.82) * mm});
            skArc(sketch, "E1656", {"start": v(18.8, 6.1) * mm, "mid": v(18.64, 6.18) * mm, "end": v(18.56, 6.02) * mm});
            skLineSegment(sketch, "E1657", {"start": v(19.17, 6.17) * mm, "end": v(20.53, 1.98) * mm});
            skArc(sketch, "E1658", {"start": v(20.42, 1.94) * mm, "mid": v(20.57, 1.86) * mm, "end": v(20.65, 2.02) * mm});
            skArc(sketch, "E1659", {"start": v(19.3, 6.21) * mm, "mid": v(19.13, 6.3) * mm, "end": v(19.05, 6.13) * mm});
            skLineSegment(sketch, "E1660", {"start": v(19.7, 6.17) * mm, "end": v(20.96, 2.29) * mm});
            skArc(sketch, "E1661", {"start": v(20.84, 2.25) * mm, "mid": v(21, 2.17) * mm, "end": v(21.08, 2.33) * mm});
            skArc(sketch, "E1662", {"start": v(19.82, 6.21) * mm, "mid": v(19.66, 6.3) * mm, "end": v(19.58, 6.13) * mm});
            skLineSegment(sketch, "E1663", {"start": v(20.22, 6.17) * mm, "end": v(21.39, 2.6) * mm});
            skArc(sketch, "E1664", {"start": v(21.27, 2.56) * mm, "mid": v(21.42, 2.48) * mm, "end": v(21.5, 2.64) * mm});
            skArc(sketch, "E1665", {"start": v(20.34, 6.2) * mm, "mid": v(20.19, 6.3) * mm, "end": v(20.1, 6.13) * mm});
            skLineSegment(sketch, "E1666", {"start": v(20.75, 6.17) * mm, "end": v(21.81, 2.9) * mm});
            skArc(sketch, "E1667", {"start": v(21.7, 2.87) * mm, "mid": v(21.85, 2.79) * mm, "end": v(21.93, 2.95) * mm});
            skArc(sketch, "E1668", {"start": v(20.87, 6.2) * mm, "mid": v(20.71, 6.29) * mm, "end": v(20.63, 6.13) * mm});
            skLineSegment(sketch, "E1669", {"start": v(21.28, 6.17) * mm, "end": v(22.24, 3.22) * mm});
            skArc(sketch, "E1670", {"start": v(22.12, 3.18) * mm, "mid": v(22.27, 3.1) * mm, "end": v(22.35, 3.26) * mm});
            skArc(sketch, "E1671", {"start": v(21.4, 6.2) * mm, "mid": v(21.24, 6.29) * mm, "end": v(21.16, 6.13) * mm});
            skLineSegment(sketch, "E1672", {"start": v(21.84, 6.04) * mm, "end": v(22.62, 3.66) * mm});
            skArc(sketch, "E1673", {"start": v(22.5, 3.62) * mm, "mid": v(22.66, 3.54) * mm, "end": v(22.74, 3.7) * mm});
            skArc(sketch, "E1674", {"start": v(21.96, 6.08) * mm, "mid": v(21.8, 6.16) * mm, "end": v(21.73, 6) * mm});
            skLineSegment(sketch, "E1675", {"start": v(28.51, 9.45) * mm, "end": v(28.45, 9.32) * mm});
            skArc(sketch, "E1676", {"start": v(28.4, 9.35) * mm, "mid": v(28.43, 9.28) * mm, "end": v(28.5, 9.3) * mm});
            skArc(sketch, "E1677", {"start": v(28.56, 9.43) * mm, "mid": v(28.53, 9.5) * mm, "end": v(28.47, 9.47) * mm});
            skLineSegment(sketch, "E1678", {"start": v(28.45, 9.32) * mm, "end": v(28.4, 9.18) * mm});
            skArc(sketch, "E1679", {"start": v(28.36, 9.19) * mm, "mid": v(28.39, 9.13) * mm, "end": v(28.45, 9.16) * mm});
            skArc(sketch, "E1680", {"start": v(28.5, 9.3) * mm, "mid": v(28.46, 9.37) * mm, "end": v(28.4, 9.34) * mm});
            skLineSegment(sketch, "E1681", {"start": v(28.4, 9.18) * mm, "end": v(28.38, 9.02) * mm});
            skArc(sketch, "E1682", {"start": v(28.33, 9.03) * mm, "mid": v(28.38, 8.97) * mm, "end": v(28.43, 9.01) * mm});
            skArc(sketch, "E1683", {"start": v(28.45, 9.17) * mm, "mid": v(28.4, 9.22) * mm, "end": v(28.35, 9.18) * mm});
            skLineSegment(sketch, "E1684", {"start": v(28.38, 9.02) * mm, "end": v(28.4, 8.86) * mm});
            skArc(sketch, "E1685", {"start": v(28.34, 8.86) * mm, "mid": v(28.4, 8.81) * mm, "end": v(28.44, 8.86) * mm});
            skArc(sketch, "E1686", {"start": v(28.43, 9.02) * mm, "mid": v(28.38, 9.07) * mm, "end": v(28.33, 9.02) * mm});
            skLineSegment(sketch, "E1687", {"start": v(28.4, 8.86) * mm, "end": v(28.4, 8.78) * mm});
            skArc(sketch, "E1688", {"start": v(28.36, 8.77) * mm, "mid": v(28.42, 8.73) * mm, "end": v(28.46, 8.8) * mm});
            skArc(sketch, "E1689", {"start": v(28.44, 8.87) * mm, "mid": v(28.38, 8.91) * mm, "end": v(28.34, 8.85) * mm});
            skLineSegment(sketch, "E1690", {"start": v(28.4, 8.78) * mm, "end": v(29.58, 5.22) * mm});
            skArc(sketch, "E1691", {"start": v(29.53, 5.2) * mm, "mid": v(29.6, 5.17) * mm, "end": v(29.63, 5.23) * mm});
            skArc(sketch, "E1692", {"start": v(28.45, 8.8) * mm, "mid": v(28.4, 8.83) * mm, "end": v(28.36, 8.77) * mm});
            skLineSegment(sketch, "E1693", {"start": v(29.58, 5.22) * mm, "end": v(29.67, 5.09) * mm});
            skArc(sketch, "E1694", {"start": v(29.62, 5.06) * mm, "mid": v(29.7, 5.04) * mm, "end": v(29.7, 5.11) * mm});
            skArc(sketch, "E1695", {"start": v(29.62, 5.24) * mm, "mid": v(29.55, 5.26) * mm, "end": v(29.54, 5.19) * mm});
            skLineSegment(sketch, "E1696", {"start": v(29.67, 5.09) * mm, "end": v(29.77, 4.97) * mm});
            skArc(sketch, "E1697", {"start": v(29.74, 4.94) * mm, "mid": v(29.8, 4.94) * mm, "end": v(29.8, 5) * mm});
            skArc(sketch, "E1698", {"start": v(29.7, 5.12) * mm, "mid": v(29.63, 5.12) * mm, "end": v(29.63, 5.05) * mm});
            skLineSegment(sketch, "E1699", {"start": v(29.77, 4.97) * mm, "end": v(29.9, 4.88) * mm});
            skArc(sketch, "E1700", {"start": v(29.87, 4.84) * mm, "mid": v(29.94, 4.85) * mm, "end": v(29.93, 4.92) * mm});
            skArc(sketch, "E1701", {"start": v(29.8, 5.01) * mm, "mid": v(29.73, 5) * mm, "end": v(29.74, 4.93) * mm});
            skLineSegment(sketch, "E1702", {"start": v(29.9, 4.88) * mm, "end": v(30.01, 4.82) * mm});
            skArc(sketch, "E1703", {"start": v(30, 4.78) * mm, "mid": v(30.06, 4.8) * mm, "end": v(30.04, 4.87) * mm});
            skArc(sketch, "E1704", {"start": v(29.92, 4.93) * mm, "mid": v(29.85, 4.9) * mm, "end": v(29.87, 4.84) * mm});
            skLineSegment(sketch, "E1705", {"start": v(30.01, 4.82) * mm, "end": v(30.08, 4.95) * mm});
            skArc(sketch, "E1706", {"start": v(30.12, 4.92) * mm, "mid": v(30.1, 5) * mm, "end": v(30.03, 4.97) * mm});
            skArc(sketch, "E1707", {"start": v(29.97, 4.84) * mm, "mid": v(30, 4.78) * mm, "end": v(30.06, 4.8) * mm});
            skLineSegment(sketch, "E1708", {"start": v(30.08, 4.95) * mm, "end": v(30.12, 5.1) * mm});
            skArc(sketch, "E1709", {"start": v(30.17, 5.08) * mm, "mid": v(30.14, 5.14) * mm, "end": v(30.08, 5.11) * mm});
            skArc(sketch, "E1710", {"start": v(30.03, 4.96) * mm, "mid": v(30.06, 4.9) * mm, "end": v(30.13, 4.93) * mm});
            skLineSegment(sketch, "E1711", {"start": v(30.12, 5.1) * mm, "end": v(30.14, 5.25) * mm});
            skArc(sketch, "E1712", {"start": v(30.2, 5.24) * mm, "mid": v(30.15, 5.3) * mm, "end": v(30.1, 5.26) * mm});
            skArc(sketch, "E1713", {"start": v(30.07, 5.1) * mm, "mid": v(30.12, 5.05) * mm, "end": v(30.17, 5.09) * mm});
            skLineSegment(sketch, "E1714", {"start": v(30.14, 5.25) * mm, "end": v(30.13, 5.4) * mm});
            skArc(sketch, "E1715", {"start": v(30.18, 5.41) * mm, "mid": v(30.13, 5.46) * mm, "end": v(30.08, 5.4) * mm});
            skArc(sketch, "E1716", {"start": v(30.1, 5.25) * mm, "mid": v(30.15, 5.2) * mm, "end": v(30.2, 5.25) * mm});
            skLineSegment(sketch, "E1717", {"start": v(30.13, 5.4) * mm, "end": v(30.12, 5.49) * mm});
            skArc(sketch, "E1718", {"start": v(30.17, 5.5) * mm, "mid": v(30.11, 5.54) * mm, "end": v(30.07, 5.48) * mm});
            skArc(sketch, "E1719", {"start": v(30.09, 5.4) * mm, "mid": v(30.14, 5.36) * mm, "end": v(30.18, 5.42) * mm});
            skLineSegment(sketch, "E1720", {"start": v(30.12, 5.49) * mm, "end": v(28.95, 9.05) * mm});
            skArc(sketch, "E1721", {"start": v(29, 9.07) * mm, "mid": v(28.93, 9.1) * mm, "end": v(28.9, 9.04) * mm});
            skArc(sketch, "E1722", {"start": v(30.07, 5.47) * mm, "mid": v(30.14, 5.44) * mm, "end": v(30.17, 5.5) * mm});
            skLineSegment(sketch, "E1723", {"start": v(28.95, 9.05) * mm, "end": v(28.86, 9.19) * mm});
            skArc(sketch, "E1724", {"start": v(28.9, 9.21) * mm, "mid": v(28.83, 9.23) * mm, "end": v(28.82, 9.16) * mm});
            skArc(sketch, "E1725", {"start": v(28.9, 9.03) * mm, "mid": v(28.98, 9.01) * mm, "end": v(29, 9.08) * mm});
            skLineSegment(sketch, "E1726", {"start": v(28.86, 9.19) * mm, "end": v(28.75, 9.3) * mm});
            skArc(sketch, "E1727", {"start": v(28.79, 9.33) * mm, "mid": v(28.72, 9.33) * mm, "end": v(28.72, 9.26) * mm});
            skArc(sketch, "E1728", {"start": v(28.82, 9.15) * mm, "mid": v(28.9, 9.15) * mm, "end": v(28.9, 9.22) * mm});
            skLineSegment(sketch, "E1729", {"start": v(28.75, 9.3) * mm, "end": v(28.63, 9.39) * mm});
            skArc(sketch, "E1730", {"start": v(28.66, 9.43) * mm, "mid": v(28.59, 9.42) * mm, "end": v(28.6, 9.35) * mm});
            skArc(sketch, "E1731", {"start": v(28.72, 9.26) * mm, "mid": v(28.8, 9.27) * mm, "end": v(28.78, 9.34) * mm});
            skLineSegment(sketch, "E1732", {"start": v(28.63, 9.39) * mm, "end": v(28.51, 9.45) * mm});
            skArc(sketch, "E1733", {"start": v(28.53, 9.5) * mm, "mid": v(28.47, 9.47) * mm, "end": v(28.49, 9.4) * mm});
            skArc(sketch, "E1734", {"start": v(28.6, 9.35) * mm, "mid": v(28.67, 9.37) * mm, "end": v(28.65, 9.43) * mm});
            skLineSegment(sketch, "E1735", {"start": v(28.4, 9.16) * mm, "end": v(29.76, 5) * mm});
            skArc(sketch, "E1736", {"start": v(29.7, 4.98) * mm, "mid": v(29.77, 4.94) * mm, "end": v(29.8, 5) * mm});
            skArc(sketch, "E1737", {"start": v(28.45, 9.18) * mm, "mid": v(28.39, 9.2) * mm, "end": v(28.35, 9.14) * mm});
            skLineSegment(sketch, "E1738", {"start": v(28.52, 9.45) * mm, "end": v(30.02, 4.83) * mm});
            skArc(sketch, "E1739", {"start": v(29.97, 4.81) * mm, "mid": v(30.03, 4.78) * mm, "end": v(30.07, 4.84) * mm});
            skArc(sketch, "E1740", {"start": v(28.57, 9.46) * mm, "mid": v(28.5, 9.5) * mm, "end": v(28.47, 9.43) * mm});
            skLineSegment(sketch, "E1741", {"start": v(28.79, 9.26) * mm, "end": v(30.13, 5.14) * mm});
            skArc(sketch, "E1742", {"start": v(30.08, 5.12) * mm, "mid": v(30.14, 5.09) * mm, "end": v(30.18, 5.15) * mm});
            skArc(sketch, "E1743", {"start": v(28.84, 9.28) * mm, "mid": v(28.77, 9.3) * mm, "end": v(28.74, 9.25) * mm});
            skCircle(sketch, "E1744", {"center": v(16.52, 3) * mm, "radius": 1.7 * mm});
            skArc(sketch, "E1745", {"start": v(16.52, 2.12) * mm, "mid": v(17.4, 3) * mm, "end": v(16.52, 3.87) * mm});
            skArc(sketch, "E1746", {"start": v(16.52, 3.87) * mm, "mid": v(15.65, 3) * mm, "end": v(16.52, 2.12) * mm});
            skCircle(sketch, "E1747", {"center": v(26.03, 6.09) * mm, "radius": 1.7 * mm});
            skArc(sketch, "E1748", {"start": v(26.03, 5.21) * mm, "mid": v(26.91, 6.09) * mm, "end": v(26.03, 6.96) * mm});
            skArc(sketch, "E1749", {"start": v(26.03, 6.96) * mm, "mid": v(25.16, 6.09) * mm, "end": v(26.03, 5.21) * mm});
            skLineSegment(sketch, "E1750", {"start": v(14.01, -17.8) * mm, "end": v(11.89, -14.9) * mm});
            skArc(sketch, "E1751", {"start": v(11.99, -14.83) * mm, "mid": v(11.81, -14.8) * mm, "end": v(11.79, -14.97) * mm});
            skArc(sketch, "E1752", {"start": v(13.91, -17.88) * mm, "mid": v(14.09, -17.9) * mm, "end": v(14.12, -17.73) * mm});
            skLineSegment(sketch, "E1753", {"start": v(11.89, -14.9) * mm, "end": v(11.73, -14.74) * mm});
            skArc(sketch, "E1754", {"start": v(11.82, -14.65) * mm, "mid": v(11.64, -14.65) * mm, "end": v(11.64, -14.83) * mm});
            skArc(sketch, "E1755", {"start": v(11.8, -14.99) * mm, "mid": v(11.98, -14.99) * mm, "end": v(11.98, -14.81) * mm});
            skLineSegment(sketch, "E1756", {"start": v(11.73, -14.74) * mm, "end": v(11.56, -14.6) * mm});
            skArc(sketch, "E1757", {"start": v(11.64, -14.5) * mm, "mid": v(11.46, -14.52) * mm, "end": v(11.48, -14.7) * mm});
            skArc(sketch, "E1758", {"start": v(11.65, -14.84) * mm, "mid": v(11.83, -14.82) * mm, "end": v(11.8, -14.64) * mm});
            skLineSegment(sketch, "E1759", {"start": v(11.56, -14.6) * mm, "end": v(11.37, -14.48) * mm});
            skArc(sketch, "E1760", {"start": v(11.44, -14.37) * mm, "mid": v(11.27, -14.4) * mm, "end": v(11.3, -14.58) * mm});
            skArc(sketch, "E1761", {"start": v(11.49, -14.7) * mm, "mid": v(11.66, -14.67) * mm, "end": v(11.63, -14.5) * mm});
            skLineSegment(sketch, "E1762", {"start": v(11.37, -14.48) * mm, "end": v(11.18, -14.38) * mm});
            skArc(sketch, "E1763", {"start": v(11.24, -14.27) * mm, "mid": v(11.07, -14.32) * mm, "end": v(11.12, -14.49) * mm});
            skArc(sketch, "E1764", {"start": v(11.31, -14.59) * mm, "mid": v(11.48, -14.54) * mm, "end": v(11.43, -14.37) * mm});
            skLineSegment(sketch, "E1765", {"start": v(11.18, -14.38) * mm, "end": v(10.98, -14.3) * mm});
            skArc(sketch, "E1766", {"start": v(11.03, -14.18) * mm, "mid": v(10.86, -14.25) * mm, "end": v(10.93, -14.4) * mm});
            skArc(sketch, "E1767", {"start": v(11.13, -14.5) * mm, "mid": v(11.3, -14.42) * mm, "end": v(11.23, -14.26) * mm});
            skLineSegment(sketch, "E1768", {"start": v(10.98, -14.3) * mm, "end": v(10.77, -14.23) * mm});
            skArc(sketch, "E1769", {"start": v(10.8, -14.11) * mm, "mid": v(10.65, -14.2) * mm, "end": v(10.74, -14.35) * mm});
            skArc(sketch, "E1770", {"start": v(10.94, -14.41) * mm, "mid": v(11.1, -14.33) * mm, "end": v(11.02, -14.17) * mm});
            skLineSegment(sketch, "E1771", {"start": v(10.77, -14.23) * mm, "end": v(10.56, -14.19) * mm});
            skArc(sketch, "E1772", {"start": v(10.59, -14.06) * mm, "mid": v(10.44, -14.16) * mm, "end": v(10.54, -14.3) * mm});
            skArc(sketch, "E1773", {"start": v(10.75, -14.35) * mm, "mid": v(10.9, -14.25) * mm, "end": v(10.8, -14.1) * mm});
            skLineSegment(sketch, "E1774", {"start": v(10.56, -14.19) * mm, "end": v(10.35, -14.16) * mm});
            skArc(sketch, "E1775", {"start": v(10.36, -14.04) * mm, "mid": v(10.22, -14.15) * mm, "end": v(10.33, -14.29) * mm});
            skArc(sketch, "E1776", {"start": v(10.55, -14.31) * mm, "mid": v(10.69, -14.2) * mm, "end": v(10.57, -14.06) * mm});
            skLineSegment(sketch, "E1777", {"start": v(10.35, -14.16) * mm, "end": v(10.13, -14.16) * mm});
            skArc(sketch, "E1778", {"start": v(10.13, -14.04) * mm, "mid": v(10, -14.16) * mm, "end": v(10.13, -14.29) * mm});
            skArc(sketch, "E1779", {"start": v(10.35, -14.29) * mm, "mid": v(10.47, -14.17) * mm, "end": v(10.35, -14.04) * mm});
            skLineSegment(sketch, "E1780", {"start": v(10.13, -14.16) * mm, "end": v(9.91, -14.18) * mm});
            skArc(sketch, "E1781", {"start": v(9.9, -14.06) * mm, "mid": v(9.79, -14.2) * mm, "end": v(9.92, -14.3) * mm});
            skArc(sketch, "E1782", {"start": v(10.14, -14.29) * mm, "mid": v(10.25, -14.15) * mm, "end": v(10.12, -14.04) * mm});
            skLineSegment(sketch, "E1783", {"start": v(9.91, -14.18) * mm, "end": v(9.7, -14.22) * mm});
            skArc(sketch, "E1784", {"start": v(9.68, -14.1) * mm, "mid": v(9.58, -14.25) * mm, "end": v(9.72, -14.34) * mm});
            skArc(sketch, "E1785", {"start": v(9.94, -14.3) * mm, "mid": v(10.04, -14.16) * mm, "end": v(9.9, -14.06) * mm});
            skLineSegment(sketch, "E1786", {"start": v(9.7, -14.22) * mm, "end": v(9.49, -14.28) * mm});
            skArc(sketch, "E1787", {"start": v(9.45, -14.16) * mm, "mid": v(9.37, -14.32) * mm, "end": v(9.52, -14.4) * mm});
            skArc(sketch, "E1788", {"start": v(9.73, -14.34) * mm, "mid": v(9.82, -14.19) * mm, "end": v(9.66, -14.1) * mm});
            skLineSegment(sketch, "E1789", {"start": v(9.49, -14.28) * mm, "end": v(9.28, -14.37) * mm});
            skArc(sketch, "E1790", {"start": v(9.23, -14.25) * mm, "mid": v(9.16, -14.41) * mm, "end": v(9.33, -14.48) * mm});
            skArc(sketch, "E1791", {"start": v(9.53, -14.4) * mm, "mid": v(9.6, -14.24) * mm, "end": v(9.44, -14.17) * mm});
            skLineSegment(sketch, "E1792", {"start": v(9.28, -14.37) * mm, "end": v(9.08, -14.47) * mm});
            skArc(sketch, "E1793", {"start": v(9.02, -14.36) * mm, "mid": v(8.97, -14.53) * mm, "end": v(9.14, -14.58) * mm});
            skArc(sketch, "E1794", {"start": v(9.34, -14.48) * mm, "mid": v(9.4, -14.3) * mm, "end": v(9.22, -14.26) * mm});
            skLineSegment(sketch, "E1795", {"start": v(9.08, -14.47) * mm, "end": v(8.9, -14.6) * mm});
            skArc(sketch, "E1796", {"start": v(8.83, -14.49) * mm, "mid": v(8.8, -14.66) * mm, "end": v(8.97, -14.7) * mm});
            skArc(sketch, "E1797", {"start": v(9.15, -14.58) * mm, "mid": v(9.18, -14.4) * mm, "end": v(9.01, -14.37) * mm});
            skLineSegment(sketch, "E1798", {"start": v(8.9, -14.6) * mm, "end": v(8.7, -14.74) * mm});
            skArc(sketch, "E1799", {"start": v(8.63, -14.65) * mm, "mid": v(8.61, -14.82) * mm, "end": v(8.79, -14.84) * mm});
            skArc(sketch, "E1800", {"start": v(8.98, -14.69) * mm, "mid": v(9, -14.51) * mm, "end": v(8.82, -14.5) * mm});
            skLineSegment(sketch, "E1801", {"start": v(8.7, -14.74) * mm, "end": v(8.55, -14.9) * mm});
            skArc(sketch, "E1802", {"start": v(8.46, -14.82) * mm, "mid": v(8.46, -15) * mm, "end": v(8.64, -15) * mm});
            skArc(sketch, "E1803", {"start": v(8.8, -14.83) * mm, "mid": v(8.8, -14.66) * mm, "end": v(8.62, -14.66) * mm});
            skLineSegment(sketch, "E1804", {"start": v(8.55, -14.9) * mm, "end": v(8.4, -15.08) * mm});
            skArc(sketch, "E1805", {"start": v(8.31, -15) * mm, "mid": v(8.33, -15.17) * mm, "end": v(8.5, -15.16) * mm});
            skArc(sketch, "E1806", {"start": v(8.65, -14.98) * mm, "mid": v(8.63, -14.8) * mm, "end": v(8.45, -14.82) * mm});
            skLineSegment(sketch, "E1807", {"start": v(8.4, -15.08) * mm, "end": v(8.29, -15.26) * mm});
            skArc(sketch, "E1808", {"start": v(8.18, -15.2) * mm, "mid": v(8.22, -15.36) * mm, "end": v(8.4, -15.33) * mm});
            skArc(sketch, "E1809", {"start": v(8.51, -15.15) * mm, "mid": v(8.48, -14.97) * mm, "end": v(8.3, -15) * mm});
            skLineSegment(sketch, "E1810", {"start": v(8.29, -15.26) * mm, "end": v(8.18, -15.45) * mm});
            skArc(sketch, "E1811", {"start": v(8.07, -15.4) * mm, "mid": v(8.13, -15.56) * mm, "end": v(8.3, -15.51) * mm});
            skArc(sketch, "E1812", {"start": v(8.4, -15.32) * mm, "mid": v(8.35, -15.15) * mm, "end": v(8.18, -15.2) * mm});
            skLineSegment(sketch, "E1813", {"start": v(8.18, -15.45) * mm, "end": v(8.1, -15.65) * mm});
            skArc(sketch, "E1814", {"start": v(7.99, -15.6) * mm, "mid": v(8.05, -15.77) * mm, "end": v(8.22, -15.7) * mm});
            skArc(sketch, "E1815", {"start": v(8.3, -15.5) * mm, "mid": v(8.23, -15.34) * mm, "end": v(8.07, -15.4) * mm});
            skLineSegment(sketch, "E1816", {"start": v(8.1, -15.65) * mm, "end": v(8.04, -15.86) * mm});
            skArc(sketch, "E1817", {"start": v(7.92, -15.82) * mm, "mid": v(8, -15.98) * mm, "end": v(8.16, -15.9) * mm});
            skArc(sketch, "E1818", {"start": v(8.22, -15.69) * mm, "mid": v(8.14, -15.53) * mm, "end": v(7.98, -15.62) * mm});
            skLineSegment(sketch, "E1819", {"start": v(8.04, -15.86) * mm, "end": v(8, -16.07) * mm});
            skArc(sketch, "E1820", {"start": v(7.87, -16.05) * mm, "mid": v(7.97, -16.2) * mm, "end": v(8.12, -16.1) * mm});
            skArc(sketch, "E1821", {"start": v(8.16, -15.88) * mm, "mid": v(8.06, -15.74) * mm, "end": v(7.92, -15.84) * mm});
            skLineSegment(sketch, "E1822", {"start": v(8, -16.07) * mm, "end": v(7.97, -16.29) * mm});
            skArc(sketch, "E1823", {"start": v(7.85, -16.27) * mm, "mid": v(7.96, -16.41) * mm, "end": v(8.1, -16.3) * mm});
            skArc(sketch, "E1824", {"start": v(8.12, -16.08) * mm, "mid": v(8, -15.95) * mm, "end": v(7.87, -16.06) * mm});
            skLineSegment(sketch, "E1825", {"start": v(7.97, -16.29) * mm, "end": v(7.97, -16.5) * mm});
            skArc(sketch, "E1826", {"start": v(7.85, -16.5) * mm, "mid": v(7.97, -16.63) * mm, "end": v(8.1, -16.5) * mm});
            skArc(sketch, "E1827", {"start": v(8.1, -16.29) * mm, "mid": v(7.98, -16.16) * mm, "end": v(7.85, -16.29) * mm});
            skLineSegment(sketch, "E1828", {"start": v(7.97, -16.5) * mm, "end": v(8, -16.72) * mm});
            skArc(sketch, "E1829", {"start": v(7.87, -16.73) * mm, "mid": v(8, -16.84) * mm, "end": v(8.12, -16.7) * mm});
            skArc(sketch, "E1830", {"start": v(8.1, -16.5) * mm, "mid": v(7.96, -16.38) * mm, "end": v(7.85, -16.51) * mm});
            skLineSegment(sketch, "E1831", {"start": v(8, -16.72) * mm, "end": v(8.03, -16.93) * mm});
            skArc(sketch, "E1832", {"start": v(7.9, -16.96) * mm, "mid": v(8.05, -17.06) * mm, "end": v(8.15, -16.91) * mm});
            skArc(sketch, "E1833", {"start": v(8.11, -16.7) * mm, "mid": v(7.97, -16.6) * mm, "end": v(7.87, -16.74) * mm});
            skLineSegment(sketch, "E1834", {"start": v(8.03, -16.93) * mm, "end": v(8.1, -17.15) * mm});
            skArc(sketch, "E1835", {"start": v(7.97, -17.18) * mm, "mid": v(8.13, -17.27) * mm, "end": v(8.21, -17.11) * mm});
            skArc(sketch, "E1836", {"start": v(8.15, -16.9) * mm, "mid": v(8, -16.81) * mm, "end": v(7.91, -16.97) * mm});
            skLineSegment(sketch, "E1837", {"start": v(8.1, -17.15) * mm, "end": v(8.18, -17.35) * mm});
            skArc(sketch, "E1838", {"start": v(8.06, -17.4) * mm, "mid": v(8.22, -17.47) * mm, "end": v(8.3, -17.3) * mm});
            skArc(sketch, "E1839", {"start": v(8.2, -17.1) * mm, "mid": v(8.05, -17.03) * mm, "end": v(7.98, -17.2) * mm});
            skLineSegment(sketch, "E1840", {"start": v(8.18, -17.35) * mm, "end": v(8.28, -17.55) * mm});
            skArc(sketch, "E1841", {"start": v(8.17, -17.6) * mm, "mid": v(8.34, -17.66) * mm, "end": v(8.4, -17.5) * mm});
            skArc(sketch, "E1842", {"start": v(8.29, -17.3) * mm, "mid": v(8.12, -17.24) * mm, "end": v(8.06, -17.4) * mm});
            skLineSegment(sketch, "E1843", {"start": v(8.28, -17.55) * mm, "end": v(8.42, -17.76) * mm});
            skArc(sketch, "E1844", {"start": v(8.31, -17.83) * mm, "mid": v(8.49, -17.86) * mm, "end": v(8.52, -17.7) * mm});
            skArc(sketch, "E1845", {"start": v(8.38, -17.48) * mm, "mid": v(8.21, -17.45) * mm, "end": v(8.18, -17.62) * mm});
            skLineSegment(sketch, "E1846", {"start": v(8.42, -17.76) * mm, "end": v(10.37, -20.45) * mm});
            skArc(sketch, "E1847", {"start": v(10.27, -20.53) * mm, "mid": v(10.45, -20.55) * mm, "end": v(10.48, -20.38) * mm});
            skArc(sketch, "E1848", {"start": v(8.52, -17.69) * mm, "mid": v(8.34, -17.66) * mm, "end": v(8.32, -17.83) * mm});
            skLineSegment(sketch, "E1849", {"start": v(10.37, -20.45) * mm, "end": v(12.26, -21.82) * mm});
            skArc(sketch, "E1850", {"start": v(12.19, -21.92) * mm, "mid": v(12.36, -21.9) * mm, "end": v(12.33, -21.72) * mm});
            skArc(sketch, "E1851", {"start": v(10.45, -20.35) * mm, "mid": v(10.27, -20.38) * mm, "end": v(10.3, -20.55) * mm});
            skLineSegment(sketch, "E1852", {"start": v(12.26, -21.82) * mm, "end": v(13.25, -22.2) * mm});
            skArc(sketch, "E1853", {"start": v(13.2, -22.32) * mm, "mid": v(13.36, -22.24) * mm, "end": v(13.3, -22.08) * mm});
            skArc(sketch, "E1854", {"start": v(12.3, -21.7) * mm, "mid": v(12.14, -21.78) * mm, "end": v(12.22, -21.94) * mm});
            skLineSegment(sketch, "E1855", {"start": v(13.25, -22.2) * mm, "end": v(14.79, -21.08) * mm});
            skArc(sketch, "E1856", {"start": v(14.86, -21.18) * mm, "mid": v(14.89, -21) * mm, "end": v(14.72, -20.98) * mm});
            skArc(sketch, "E1857", {"start": v(13.17, -22.1) * mm, "mid": v(13.15, -22.27) * mm, "end": v(13.32, -22.3) * mm});
            skLineSegment(sketch, "E1858", {"start": v(14.79, -21.08) * mm, "end": v(14.73, -20.02) * mm});
            skArc(sketch, "E1859", {"start": v(14.86, -20.02) * mm, "mid": v(14.73, -19.9) * mm, "end": v(14.6, -20.03) * mm});
            skArc(sketch, "E1860", {"start": v(14.66, -21.09) * mm, "mid": v(14.8, -21.2) * mm, "end": v(14.91, -21.07) * mm});
            skLineSegment(sketch, "E1861", {"start": v(14.73, -20.02) * mm, "end": v(14.01, -17.8) * mm});
            skArc(sketch, "E1862", {"start": v(14.13, -17.77) * mm, "mid": v(13.98, -17.69) * mm, "end": v(13.9, -17.85) * mm});
            skArc(sketch, "E1863", {"start": v(14.61, -20.06) * mm, "mid": v(14.77, -20.14) * mm, "end": v(14.85, -19.99) * mm});
            skLineSegment(sketch, "E1864", {"start": v(9.88, -14.19) * mm, "end": v(8.21, -15.4) * mm});
            skArc(sketch, "E1865", {"start": v(8.14, -15.3) * mm, "mid": v(8.11, -15.47) * mm, "end": v(8.29, -15.5) * mm});
            skArc(sketch, "E1866", {"start": v(9.95, -14.29) * mm, "mid": v(9.98, -14.11) * mm, "end": v(9.8, -14.09) * mm});
            skLineSegment(sketch, "E1867", {"start": v(10.7, -14.21) * mm, "end": v(7.98, -16.18) * mm});
            skArc(sketch, "E1868", {"start": v(7.91, -16.08) * mm, "mid": v(7.88, -16.26) * mm, "end": v(8.06, -16.28) * mm});
            skArc(sketch, "E1869", {"start": v(10.77, -14.32) * mm, "mid": v(10.8, -14.14) * mm, "end": v(10.62, -14.11) * mm});
            skLineSegment(sketch, "E1870", {"start": v(11.26, -14.42) * mm, "end": v(8, -16.79) * mm});
            skArc(sketch, "E1871", {"start": v(7.93, -16.69) * mm, "mid": v(7.9, -16.86) * mm, "end": v(8.08, -16.89) * mm});
            skArc(sketch, "E1872", {"start": v(11.34, -14.52) * mm, "mid": v(11.36, -14.35) * mm, "end": v(11.19, -14.32) * mm});
            skLineSegment(sketch, "E1873", {"start": v(11.7, -14.72) * mm, "end": v(8.15, -17.3) * mm});
            skArc(sketch, "E1874", {"start": v(8.08, -17.2) * mm, "mid": v(8.05, -17.37) * mm, "end": v(8.23, -17.4) * mm});
            skArc(sketch, "E1875", {"start": v(11.77, -14.82) * mm, "mid": v(11.8, -14.64) * mm, "end": v(11.63, -14.62) * mm});
            skLineSegment(sketch, "E1876", {"start": v(12.03, -15.1) * mm, "end": v(8.4, -17.73) * mm});
            skArc(sketch, "E1877", {"start": v(8.33, -17.63) * mm, "mid": v(8.3, -17.8) * mm, "end": v(8.47, -17.84) * mm});
            skArc(sketch, "E1878", {"start": v(12.1, -15.2) * mm, "mid": v(12.13, -15.02) * mm, "end": v(11.96, -15) * mm});
            skLineSegment(sketch, "E1879", {"start": v(12.33, -15.5) * mm, "end": v(8.7, -18.14) * mm});
            skArc(sketch, "E1880", {"start": v(8.62, -18.04) * mm, "mid": v(8.6, -18.21) * mm, "end": v(8.77, -18.24) * mm});
            skArc(sketch, "E1881", {"start": v(12.4, -15.6) * mm, "mid": v(12.43, -15.43) * mm, "end": v(12.25, -15.4) * mm});
            skLineSegment(sketch, "E1882", {"start": v(12.62, -15.9) * mm, "end": v(8.99, -18.54) * mm});
            skArc(sketch, "E1883", {"start": v(8.91, -18.44) * mm, "mid": v(8.89, -18.62) * mm, "end": v(9.06, -18.65) * mm});
            skArc(sketch, "E1884", {"start": v(12.7, -16) * mm, "mid": v(12.72, -15.83) * mm, "end": v(12.55, -15.8) * mm});
            skLineSegment(sketch, "E1885", {"start": v(12.92, -16.3) * mm, "end": v(9.28, -18.95) * mm});
            skArc(sketch, "E1886", {"start": v(9.2, -18.85) * mm, "mid": v(9.18, -19.02) * mm, "end": v(9.35, -19.05) * mm});
            skArc(sketch, "E1887", {"start": v(13, -16.4) * mm, "mid": v(13.02, -16.23) * mm, "end": v(12.84, -16.2) * mm});
            skLineSegment(sketch, "E1888", {"start": v(13.21, -16.71) * mm, "end": v(9.58, -19.35) * mm});
            skArc(sketch, "E1889", {"start": v(9.5, -19.25) * mm, "mid": v(9.47, -19.43) * mm, "end": v(9.65, -19.45) * mm});
            skArc(sketch, "E1890", {"start": v(13.29, -16.81) * mm, "mid": v(13.31, -16.64) * mm, "end": v(13.14, -16.6) * mm});
            skLineSegment(sketch, "E1891", {"start": v(13.5, -17.11) * mm, "end": v(9.87, -19.76) * mm});
            skArc(sketch, "E1892", {"start": v(9.8, -19.66) * mm, "mid": v(9.77, -19.83) * mm, "end": v(9.94, -19.86) * mm});
            skArc(sketch, "E1893", {"start": v(13.58, -17.22) * mm, "mid": v(13.6, -17.04) * mm, "end": v(13.43, -17.01) * mm});
            skLineSegment(sketch, "E1894", {"start": v(13.8, -17.52) * mm, "end": v(10.16, -20.16) * mm});
            skArc(sketch, "E1895", {"start": v(10.09, -20.06) * mm, "mid": v(10.06, -20.24) * mm, "end": v(10.24, -20.26) * mm});
            skArc(sketch, "E1896", {"start": v(13.88, -17.62) * mm, "mid": v(13.9, -17.44) * mm, "end": v(13.73, -17.42) * mm});
            skLineSegment(sketch, "E1897", {"start": v(14.06, -17.95) * mm, "end": v(10.5, -20.54) * mm});
            skArc(sketch, "E1898", {"start": v(10.42, -20.44) * mm, "mid": v(10.4, -20.61) * mm, "end": v(10.57, -20.64) * mm});
            skArc(sketch, "E1899", {"start": v(14.13, -18.05) * mm, "mid": v(14.16, -17.88) * mm, "end": v(13.99, -17.85) * mm});
            skLineSegment(sketch, "E1900", {"start": v(14.22, -18.45) * mm, "end": v(10.92, -20.85) * mm});
            skArc(sketch, "E1901", {"start": v(10.85, -20.75) * mm, "mid": v(10.82, -20.92) * mm, "end": v(11, -20.95) * mm});
            skArc(sketch, "E1902", {"start": v(14.3, -18.55) * mm, "mid": v(14.32, -18.38) * mm, "end": v(14.15, -18.35) * mm});
            skLineSegment(sketch, "E1903", {"start": v(14.38, -18.95) * mm, "end": v(11.35, -21.16) * mm});
            skArc(sketch, "E1904", {"start": v(11.27, -21.06) * mm, "mid": v(11.24, -21.23) * mm, "end": v(11.42, -21.26) * mm});
            skArc(sketch, "E1905", {"start": v(14.46, -19.05) * mm, "mid": v(14.49, -18.88) * mm, "end": v(14.31, -18.85) * mm});
            skLineSegment(sketch, "E1906", {"start": v(14.55, -19.45) * mm, "end": v(11.77, -21.47) * mm});
            skArc(sketch, "E1907", {"start": v(11.7, -21.36) * mm, "mid": v(11.67, -21.54) * mm, "end": v(11.84, -21.57) * mm});
            skArc(sketch, "E1908", {"start": v(14.62, -19.55) * mm, "mid": v(14.65, -19.38) * mm, "end": v(14.47, -19.35) * mm});
            skLineSegment(sketch, "E1909", {"start": v(14.7, -19.95) * mm, "end": v(12.2, -21.77) * mm});
            skArc(sketch, "E1910", {"start": v(12.12, -21.67) * mm, "mid": v(12.1, -21.85) * mm, "end": v(12.27, -21.88) * mm});
            skArc(sketch, "E1911", {"start": v(14.78, -20.05) * mm, "mid": v(14.81, -19.88) * mm, "end": v(14.64, -19.85) * mm});
            skLineSegment(sketch, "E1912", {"start": v(14.76, -20.53) * mm, "end": v(12.73, -22) * mm});
            skArc(sketch, "E1913", {"start": v(12.66, -21.9) * mm, "mid": v(12.63, -22.08) * mm, "end": v(12.8, -22.1) * mm});
            skArc(sketch, "E1914", {"start": v(14.83, -20.63) * mm, "mid": v(14.86, -20.46) * mm, "end": v(14.69, -20.43) * mm});
            skLineSegment(sketch, "E1915", {"start": v(20.06, -25.82) * mm, "end": v(19.92, -25.8) * mm});
            skArc(sketch, "E1916", {"start": v(19.93, -25.75) * mm, "mid": v(19.87, -25.79) * mm, "end": v(19.92, -25.85) * mm});
            skArc(sketch, "E1917", {"start": v(20.06, -25.87) * mm, "mid": v(20.11, -25.83) * mm, "end": v(20.07, -25.77) * mm});
            skLineSegment(sketch, "E1918", {"start": v(19.92, -25.8) * mm, "end": v(19.77, -25.8) * mm});
            skArc(sketch, "E1919", {"start": v(19.77, -25.75) * mm, "mid": v(19.72, -25.8) * mm, "end": v(19.77, -25.85) * mm});
            skArc(sketch, "E1920", {"start": v(19.92, -25.85) * mm, "mid": v(19.97, -25.8) * mm, "end": v(19.92, -25.75) * mm});
            skLineSegment(sketch, "E1921", {"start": v(19.77, -25.8) * mm, "end": v(19.62, -25.83) * mm});
            skArc(sketch, "E1922", {"start": v(19.6, -25.78) * mm, "mid": v(19.57, -25.84) * mm, "end": v(19.63, -25.88) * mm});
            skArc(sketch, "E1923", {"start": v(19.78, -25.85) * mm, "mid": v(19.82, -25.79) * mm, "end": v(19.76, -25.75) * mm});
            skLineSegment(sketch, "E1924", {"start": v(19.62, -25.83) * mm, "end": v(19.47, -25.88) * mm});
            skArc(sketch, "E1925", {"start": v(19.45, -25.84) * mm, "mid": v(19.42, -25.9) * mm, "end": v(19.49, -25.93) * mm});
            skArc(sketch, "E1926", {"start": v(19.63, -25.88) * mm, "mid": v(19.66, -25.81) * mm, "end": v(19.6, -25.78) * mm});
            skLineSegment(sketch, "E1927", {"start": v(19.47, -25.88) * mm, "end": v(19.4, -25.92) * mm});
            skArc(sketch, "E1928", {"start": v(19.37, -25.88) * mm, "mid": v(19.35, -25.95) * mm, "end": v(19.42, -25.97) * mm});
            skArc(sketch, "E1929", {"start": v(19.5, -25.93) * mm, "mid": v(19.51, -25.86) * mm, "end": v(19.44, -25.84) * mm});
            skLineSegment(sketch, "E1930", {"start": v(19.4, -25.92) * mm, "end": v(16.37, -28.14) * mm});
            skArc(sketch, "E1931", {"start": v(16.34, -28.1) * mm, "mid": v(16.33, -28.17) * mm, "end": v(16.4, -28.18) * mm});
            skArc(sketch, "E1932", {"start": v(19.43, -25.96) * mm, "mid": v(19.44, -25.9) * mm, "end": v(19.37, -25.88) * mm});
            skLineSegment(sketch, "E1933", {"start": v(16.37, -28.14) * mm, "end": v(16.27, -28.26) * mm});
            skArc(sketch, "E1934", {"start": v(16.23, -28.23) * mm, "mid": v(16.24, -28.3) * mm, "end": v(16.3, -28.3) * mm});
            skArc(sketch, "E1935", {"start": v(16.4, -28.17) * mm, "mid": v(16.4, -28.1) * mm, "end": v(16.33, -28.1) * mm});
            skLineSegment(sketch, "E1936", {"start": v(16.27, -28.26) * mm, "end": v(16.2, -28.4) * mm});
            skArc(sketch, "E1937", {"start": v(16.15, -28.38) * mm, "mid": v(16.17, -28.44) * mm, "end": v(16.24, -28.42) * mm});
            skArc(sketch, "E1938", {"start": v(16.31, -28.29) * mm, "mid": v(16.3, -28.22) * mm, "end": v(16.23, -28.24) * mm});
            skLineSegment(sketch, "E1939", {"start": v(16.2, -28.4) * mm, "end": v(16.15, -28.55) * mm});
            skArc(sketch, "E1940", {"start": v(16.1, -28.53) * mm, "mid": v(16.13, -28.6) * mm, "end": v(16.2, -28.56) * mm});
            skArc(sketch, "E1941", {"start": v(16.24, -28.42) * mm, "mid": v(16.21, -28.35) * mm, "end": v(16.15, -28.38) * mm});
            skLineSegment(sketch, "E1942", {"start": v(16.15, -28.55) * mm, "end": v(16.13, -28.68) * mm});
            skArc(sketch, "E1943", {"start": v(16.08, -28.67) * mm, "mid": v(16.12, -28.73) * mm, "end": v(16.18, -28.69) * mm});
            skArc(sketch, "E1944", {"start": v(16.2, -28.56) * mm, "mid": v(16.15, -28.5) * mm, "end": v(16.1, -28.54) * mm});
            skLineSegment(sketch, "E1945", {"start": v(16.13, -28.68) * mm, "end": v(16.27, -28.7) * mm});
            skArc(sketch, "E1946", {"start": v(16.26, -28.75) * mm, "mid": v(16.32, -28.7) * mm, "end": v(16.27, -28.65) * mm});
            skArc(sketch, "E1947", {"start": v(16.13, -28.63) * mm, "mid": v(16.08, -28.67) * mm, "end": v(16.12, -28.73) * mm});
            skLineSegment(sketch, "E1948", {"start": v(16.27, -28.7) * mm, "end": v(16.42, -28.7) * mm});
            skArc(sketch, "E1949", {"start": v(16.42, -28.75) * mm, "mid": v(16.47, -28.7) * mm, "end": v(16.42, -28.65) * mm});
            skArc(sketch, "E1950", {"start": v(16.26, -28.65) * mm, "mid": v(16.22, -28.7) * mm, "end": v(16.27, -28.75) * mm});
            skLineSegment(sketch, "E1951", {"start": v(16.42, -28.7) * mm, "end": v(16.57, -28.67) * mm});
            skArc(sketch, "E1952", {"start": v(16.58, -28.72) * mm, "mid": v(16.62, -28.66) * mm, "end": v(16.56, -28.62) * mm});
            skArc(sketch, "E1953", {"start": v(16.41, -28.65) * mm, "mid": v(16.37, -28.7) * mm, "end": v(16.43, -28.75) * mm});
            skLineSegment(sketch, "E1954", {"start": v(16.57, -28.67) * mm, "end": v(16.72, -28.61) * mm});
            skArc(sketch, "E1955", {"start": v(16.74, -28.66) * mm, "mid": v(16.77, -28.6) * mm, "end": v(16.7, -28.56) * mm});
            skArc(sketch, "E1956", {"start": v(16.56, -28.62) * mm, "mid": v(16.53, -28.68) * mm, "end": v(16.6, -28.71) * mm});
            skLineSegment(sketch, "E1957", {"start": v(16.72, -28.61) * mm, "end": v(16.8, -28.57) * mm});
            skArc(sketch, "E1958", {"start": v(16.82, -28.62) * mm, "mid": v(16.84, -28.55) * mm, "end": v(16.77, -28.53) * mm});
            skArc(sketch, "E1959", {"start": v(16.7, -28.57) * mm, "mid": v(16.68, -28.63) * mm, "end": v(16.75, -28.65) * mm});
            skLineSegment(sketch, "E1960", {"start": v(16.8, -28.57) * mm, "end": v(19.82, -26.36) * mm});
            skArc(sketch, "E1961", {"start": v(19.85, -26.4) * mm, "mid": v(19.86, -26.33) * mm, "end": v(19.8, -26.32) * mm});
            skArc(sketch, "E1962", {"start": v(16.76, -28.53) * mm, "mid": v(16.75, -28.6) * mm, "end": v(16.82, -28.61) * mm});
            skLineSegment(sketch, "E1963", {"start": v(19.82, -26.36) * mm, "end": v(19.92, -26.23) * mm});
            skArc(sketch, "E1964", {"start": v(19.96, -26.26) * mm, "mid": v(19.95, -26.2) * mm, "end": v(19.88, -26.2) * mm});
            skArc(sketch, "E1965", {"start": v(19.78, -26.32) * mm, "mid": v(19.8, -26.4) * mm, "end": v(19.86, -26.39) * mm});
            skLineSegment(sketch, "E1966", {"start": v(19.92, -26.23) * mm, "end": v(20, -26.1) * mm});
            skArc(sketch, "E1967", {"start": v(20.04, -26.12) * mm, "mid": v(20.02, -26.05) * mm, "end": v(19.95, -26.07) * mm});
            skArc(sketch, "E1968", {"start": v(19.88, -26.2) * mm, "mid": v(19.9, -26.28) * mm, "end": v(19.96, -26.26) * mm});
            skLineSegment(sketch, "E1969", {"start": v(20, -26.1) * mm, "end": v(20.04, -25.95) * mm});
            skArc(sketch, "E1970", {"start": v(20.1, -25.96) * mm, "mid": v(20.06, -25.9) * mm, "end": v(20, -25.93) * mm});
            skArc(sketch, "E1971", {"start": v(19.95, -26.08) * mm, "mid": v(19.98, -26.14) * mm, "end": v(20.04, -26.11) * mm});
            skLineSegment(sketch, "E1972", {"start": v(20.04, -25.95) * mm, "end": v(20.06, -25.82) * mm});
            skArc(sketch, "E1973", {"start": v(20.11, -25.83) * mm, "mid": v(20.07, -25.77) * mm, "end": v(20.01, -25.8) * mm});
            skArc(sketch, "E1974", {"start": v(20, -25.94) * mm, "mid": v(20.04, -26) * mm, "end": v(20.1, -25.96) * mm});
            skLineSegment(sketch, "E1975", {"start": v(19.75, -25.8) * mm, "end": v(16.2, -28.38) * mm});
            skArc(sketch, "E1976", {"start": v(16.18, -28.34) * mm, "mid": v(16.17, -28.4) * mm, "end": v(16.24, -28.42) * mm});
            skArc(sketch, "E1977", {"start": v(19.78, -25.84) * mm, "mid": v(19.8, -25.77) * mm, "end": v(19.72, -25.76) * mm});
            skLineSegment(sketch, "E1978", {"start": v(20.06, -25.82) * mm, "end": v(16.13, -28.68) * mm});
            skArc(sketch, "E1979", {"start": v(16.1, -28.64) * mm, "mid": v(16.1, -28.7) * mm, "end": v(16.16, -28.72) * mm});
            skArc(sketch, "E1980", {"start": v(20.1, -25.87) * mm, "mid": v(20.1, -25.8) * mm, "end": v(20.03, -25.78) * mm});
            skLineSegment(sketch, "E1981", {"start": v(19.97, -26.14) * mm, "end": v(16.46, -28.69) * mm});
            skArc(sketch, "E1982", {"start": v(16.43, -28.65) * mm, "mid": v(16.42, -28.72) * mm, "end": v(16.5, -28.73) * mm});
            skArc(sketch, "E1983", {"start": v(20, -26.18) * mm, "mid": v(20.01, -26.11) * mm, "end": v(19.94, -26.1) * mm});
            skCircle(sketch, "E1984", {"center": v(10.22, -16.41) * mm, "radius": 1.7 * mm});
            skArc(sketch, "E1985", {"start": v(10.22, -17.29) * mm, "mid": v(11.1, -16.41) * mm, "end": v(10.22, -15.54) * mm});
            skArc(sketch, "E1986", {"start": v(10.22, -15.54) * mm, "mid": v(9.35, -16.41) * mm, "end": v(10.22, -17.29) * mm});
            skCircle(sketch, "E1987", {"center": v(16.1, -24.5) * mm, "radius": 1.7 * mm});
            skArc(sketch, "E1988", {"start": v(16.1, -25.38) * mm, "mid": v(16.98, -24.5) * mm, "end": v(16.1, -23.63) * mm});
            skArc(sketch, "E1989", {"start": v(16.1, -23.63) * mm, "mid": v(15.22, -24.5) * mm, "end": v(16.1, -25.38) * mm});
            skLineSegment(sketch, "E1990", {"start": v(-4.8, -10.73) * mm, "end": v(-4.8, -10.27) * mm});
            skArc(sketch, "E1991", {"start": v(-4.8, -10.27) * mm, "mid": v(-4.8, -10.23) * mm, "end": v(-4.84, -10.22) * mm});
            skLineSegment(sketch, "E1992", {"start": v(-4.84, -10.22) * mm, "end": v(-5.24, -10.22) * mm});
            skArc(sketch, "E1993", {"start": v(-5.24, -10.22) * mm, "mid": v(-5.27, -10.23) * mm, "end": v(-5.28, -10.27) * mm});
            skLineSegment(sketch, "E1994", {"start": v(-5.28, -10.27) * mm, "end": v(-5.28, -10.73) * mm});
            skArc(sketch, "E1995", {"start": v(-5.28, -10.73) * mm, "mid": v(-5.27, -10.76) * mm, "end": v(-5.24, -10.78) * mm});
            skLineSegment(sketch, "E1996", {"start": v(-5.24, -10.78) * mm, "end": v(-4.84, -10.78) * mm});
            skArc(sketch, "E1997", {"start": v(-4.84, -10.78) * mm, "mid": v(-4.8, -10.76) * mm, "end": v(-4.8, -10.73) * mm});
            skLineSegment(sketch, "E1998", {"start": v(-3.92, -10.73) * mm, "end": v(-3.92, -10.27) * mm});
            skArc(sketch, "E1999", {"start": v(-3.92, -10.27) * mm, "mid": v(-3.93, -10.23) * mm, "end": v(-3.96, -10.22) * mm});
            skLineSegment(sketch, "E2000", {"start": v(-3.96, -10.22) * mm, "end": v(-4.36, -10.22) * mm});
            skArc(sketch, "E2001", {"start": v(-4.36, -10.22) * mm, "mid": v(-4.4, -10.23) * mm, "end": v(-4.4, -10.27) * mm});
            skLineSegment(sketch, "E2002", {"start": v(-4.4, -10.27) * mm, "end": v(-4.4, -10.73) * mm});
            skArc(sketch, "E2003", {"start": v(-4.4, -10.73) * mm, "mid": v(-4.4, -10.76) * mm, "end": v(-4.36, -10.78) * mm});
            skLineSegment(sketch, "E2004", {"start": v(-4.36, -10.78) * mm, "end": v(-3.96, -10.78) * mm});
            skArc(sketch, "E2005", {"start": v(-3.96, -10.78) * mm, "mid": v(-3.93, -10.76) * mm, "end": v(-3.92, -10.73) * mm});
            skLineSegment(sketch, "E2006", {"start": v(-4.8, -11.93) * mm, "end": v(-4.8, -11.47) * mm});
            skArc(sketch, "E2007", {"start": v(-4.8, -11.47) * mm, "mid": v(-4.8, -11.43) * mm, "end": v(-4.84, -11.42) * mm});
            skLineSegment(sketch, "E2008", {"start": v(-4.84, -11.42) * mm, "end": v(-5.24, -11.42) * mm});
            skArc(sketch, "E2009", {"start": v(-5.24, -11.42) * mm, "mid": v(-5.27, -11.43) * mm, "end": v(-5.28, -11.47) * mm});
            skLineSegment(sketch, "E2010", {"start": v(-5.28, -11.47) * mm, "end": v(-5.28, -11.93) * mm});
            skArc(sketch, "E2011", {"start": v(-5.28, -11.93) * mm, "mid": v(-5.27, -11.96) * mm, "end": v(-5.24, -11.98) * mm});
            skLineSegment(sketch, "E2012", {"start": v(-5.24, -11.98) * mm, "end": v(-4.84, -11.98) * mm});
            skArc(sketch, "E2013", {"start": v(-4.84, -11.98) * mm, "mid": v(-4.8, -11.96) * mm, "end": v(-4.8, -11.93) * mm});
            skLineSegment(sketch, "E2014", {"start": v(-3.92, -11.93) * mm, "end": v(-3.92, -11.47) * mm});
            skArc(sketch, "E2015", {"start": v(-3.92, -11.47) * mm, "mid": v(-3.93, -11.43) * mm, "end": v(-3.96, -11.42) * mm});
            skLineSegment(sketch, "E2016", {"start": v(-3.96, -11.42) * mm, "end": v(-4.36, -11.42) * mm});
            skArc(sketch, "E2017", {"start": v(-4.36, -11.42) * mm, "mid": v(-4.4, -11.43) * mm, "end": v(-4.4, -11.47) * mm});
            skLineSegment(sketch, "E2018", {"start": v(-4.4, -11.47) * mm, "end": v(-4.4, -11.93) * mm});
            skArc(sketch, "E2019", {"start": v(-4.4, -11.93) * mm, "mid": v(-4.4, -11.96) * mm, "end": v(-4.36, -11.98) * mm});
            skLineSegment(sketch, "E2020", {"start": v(-4.36, -11.98) * mm, "end": v(-3.96, -11.98) * mm});
            skArc(sketch, "E2021", {"start": v(-3.96, -11.98) * mm, "mid": v(-3.93, -11.96) * mm, "end": v(-3.92, -11.93) * mm});
            skLineSegment(sketch, "E2022", {"start": v(9.92, -10.64) * mm, "end": v(10.2, -11.02) * mm});
            skArc(sketch, "E2023", {"start": v(10.2, -11.02) * mm, "mid": v(10.23, -11.04) * mm, "end": v(10.26, -11.03) * mm});
            skLineSegment(sketch, "E2024", {"start": v(10.26, -11.03) * mm, "end": v(10.58, -10.8) * mm});
            skArc(sketch, "E2025", {"start": v(10.58, -10.8) * mm, "mid": v(10.6, -10.77) * mm, "end": v(10.6, -10.73) * mm});
            skLineSegment(sketch, "E2026", {"start": v(10.6, -10.73) * mm, "end": v(10.32, -10.36) * mm});
            skArc(sketch, "E2027", {"start": v(10.32, -10.36) * mm, "mid": v(10.29, -10.34) * mm, "end": v(10.25, -10.35) * mm});
            skLineSegment(sketch, "E2028", {"start": v(10.25, -10.35) * mm, "end": v(9.93, -10.58) * mm});
            skArc(sketch, "E2029", {"start": v(9.93, -10.58) * mm, "mid": v(9.91, -10.6) * mm, "end": v(9.92, -10.64) * mm});
            skLineSegment(sketch, "E2030", {"start": v(9.2, -11.16) * mm, "end": v(9.48, -11.54) * mm});
            skArc(sketch, "E2031", {"start": v(9.48, -11.54) * mm, "mid": v(9.51, -11.56) * mm, "end": v(9.55, -11.55) * mm});
            skLineSegment(sketch, "E2032", {"start": v(9.55, -11.55) * mm, "end": v(9.87, -11.32) * mm});
            skArc(sketch, "E2033", {"start": v(9.87, -11.32) * mm, "mid": v(9.89, -11.29) * mm, "end": v(9.88, -11.25) * mm});
            skLineSegment(sketch, "E2034", {"start": v(9.88, -11.25) * mm, "end": v(9.6, -10.87) * mm});
            skArc(sketch, "E2035", {"start": v(9.6, -10.87) * mm, "mid": v(9.57, -10.86) * mm, "end": v(9.54, -10.86) * mm});
            skLineSegment(sketch, "E2036", {"start": v(9.54, -10.86) * mm, "end": v(9.22, -11.1) * mm});
            skArc(sketch, "E2037", {"start": v(9.22, -11.1) * mm, "mid": v(9.2, -11.13) * mm, "end": v(9.2, -11.16) * mm});
            skLineSegment(sketch, "E2038", {"start": v(11.02, 4.12) * mm, "end": v(11.46, 4.26) * mm});
            skArc(sketch, "E2039", {"start": v(11.46, 4.26) * mm, "mid": v(11.49, 4.28) * mm, "end": v(11.5, 4.32) * mm});
            skLineSegment(sketch, "E2040", {"start": v(11.5, 4.32) * mm, "end": v(11.37, 4.7) * mm});
            skArc(sketch, "E2041", {"start": v(11.37, 4.7) * mm, "mid": v(11.35, 4.72) * mm, "end": v(11.3, 4.73) * mm});
            skLineSegment(sketch, "E2042", {"start": v(11.3, 4.73) * mm, "end": v(10.87, 4.58) * mm});
            skArc(sketch, "E2043", {"start": v(10.87, 4.58) * mm, "mid": v(10.84, 4.56) * mm, "end": v(10.84, 4.52) * mm});
            skLineSegment(sketch, "E2044", {"start": v(10.84, 4.52) * mm, "end": v(10.96, 4.15) * mm});
            skArc(sketch, "E2045", {"start": v(10.96, 4.15) * mm, "mid": v(10.98, 4.12) * mm, "end": v(11.02, 4.12) * mm});
            skLineSegment(sketch, "E2046", {"start": v(11.3, 3.28) * mm, "end": v(11.73, 3.42) * mm});
            skArc(sketch, "E2047", {"start": v(11.73, 3.42) * mm, "mid": v(11.76, 3.45) * mm, "end": v(11.76, 3.48) * mm});
            skLineSegment(sketch, "E2048", {"start": v(11.76, 3.48) * mm, "end": v(11.64, 3.86) * mm});
            skArc(sketch, "E2049", {"start": v(11.64, 3.86) * mm, "mid": v(11.62, 3.89) * mm, "end": v(11.58, 3.89) * mm});
            skLineSegment(sketch, "E2050", {"start": v(11.58, 3.89) * mm, "end": v(11.14, 3.74) * mm});
            skArc(sketch, "E2051", {"start": v(11.14, 3.74) * mm, "mid": v(11.11, 3.72) * mm, "end": v(11.1, 3.69) * mm});
            skLineSegment(sketch, "E2052", {"start": v(11.1, 3.69) * mm, "end": v(11.23, 3.3) * mm});
            skArc(sketch, "E2053", {"start": v(11.23, 3.3) * mm, "mid": v(11.25, 3.28) * mm, "end": v(11.3, 3.28) * mm});
            skLineSegment(sketch, "E2054", {"start": v(1.7, 5.33) * mm, "end": v(1.7, 4.87) * mm});
            skArc(sketch, "E2055", {"start": v(1.7, 4.87) * mm, "mid": v(1.7, 4.83) * mm, "end": v(1.74, 4.82) * mm});
            skLineSegment(sketch, "E2056", {"start": v(1.74, 4.82) * mm, "end": v(2.14, 4.82) * mm});
            skArc(sketch, "E2057", {"start": v(2.14, 4.82) * mm, "mid": v(2.17, 4.83) * mm, "end": v(2.18, 4.87) * mm});
            skLineSegment(sketch, "E2058", {"start": v(2.18, 4.87) * mm, "end": v(2.18, 5.33) * mm});
            skArc(sketch, "E2059", {"start": v(2.18, 5.33) * mm, "mid": v(2.17, 5.36) * mm, "end": v(2.14, 5.38) * mm});
            skLineSegment(sketch, "E2060", {"start": v(2.14, 5.38) * mm, "end": v(1.74, 5.38) * mm});
            skArc(sketch, "E2061", {"start": v(1.74, 5.38) * mm, "mid": v(1.7, 5.36) * mm, "end": v(1.7, 5.33) * mm});
            skLineSegment(sketch, "E2062", {"start": v(0.82, 5.33) * mm, "end": v(0.82, 4.87) * mm});
            skArc(sketch, "E2063", {"start": v(0.82, 4.87) * mm, "mid": v(0.83, 4.83) * mm, "end": v(0.86, 4.82) * mm});
            skLineSegment(sketch, "E2064", {"start": v(0.86, 4.82) * mm, "end": v(1.26, 4.82) * mm});
            skArc(sketch, "E2065", {"start": v(1.26, 4.82) * mm, "mid": v(1.3, 4.83) * mm, "end": v(1.3, 4.87) * mm});
            skLineSegment(sketch, "E2066", {"start": v(1.3, 4.87) * mm, "end": v(1.3, 5.33) * mm});
            skArc(sketch, "E2067", {"start": v(1.3, 5.33) * mm, "mid": v(1.3, 5.36) * mm, "end": v(1.26, 5.38) * mm});
            skLineSegment(sketch, "E2068", {"start": v(1.26, 5.38) * mm, "end": v(0.86, 5.38) * mm});
            skArc(sketch, "E2069", {"start": v(0.86, 5.38) * mm, "mid": v(0.83, 5.36) * mm, "end": v(0.82, 5.33) * mm});
            skLineSegment(sketch, "E2070", {"start": v(-11.42, 4.25) * mm, "end": v(-10.98, 4.1) * mm});
            skArc(sketch, "E2071", {"start": v(-10.98, 4.1) * mm, "mid": v(-10.94, 4.1) * mm, "end": v(-10.92, 4.14) * mm});
            skLineSegment(sketch, "E2072", {"start": v(-10.92, 4.14) * mm, "end": v(-10.8, 4.51) * mm});
            skArc(sketch, "E2073", {"start": v(-10.8, 4.51) * mm, "mid": v(-10.8, 4.55) * mm, "end": v(-10.83, 4.57) * mm});
            skLineSegment(sketch, "E2074", {"start": v(-10.83, 4.57) * mm, "end": v(-11.27, 4.72) * mm});
            skArc(sketch, "E2075", {"start": v(-11.27, 4.72) * mm, "mid": v(-11.3, 4.71) * mm, "end": v(-11.33, 4.69) * mm});
            skLineSegment(sketch, "E2076", {"start": v(-11.33, 4.69) * mm, "end": v(-11.45, 4.3) * mm});
            skArc(sketch, "E2077", {"start": v(-11.45, 4.3) * mm, "mid": v(-11.45, 4.27) * mm, "end": v(-11.42, 4.25) * mm});
            skLineSegment(sketch, "E2078", {"start": v(-11.7, 3.41) * mm, "end": v(-11.25, 3.27) * mm});
            skArc(sketch, "E2079", {"start": v(-11.25, 3.27) * mm, "mid": v(-11.21, 3.27) * mm, "end": v(-11.2, 3.3) * mm});
            skLineSegment(sketch, "E2080", {"start": v(-11.2, 3.3) * mm, "end": v(-11.07, 3.68) * mm});
            skArc(sketch, "E2081", {"start": v(-11.07, 3.68) * mm, "mid": v(-11.07, 3.71) * mm, "end": v(-11.1, 3.73) * mm});
            skLineSegment(sketch, "E2082", {"start": v(-11.1, 3.73) * mm, "end": v(-11.54, 3.88) * mm});
            skArc(sketch, "E2083", {"start": v(-11.54, 3.88) * mm, "mid": v(-11.58, 3.88) * mm, "end": v(-11.6, 3.85) * mm});
            skLineSegment(sketch, "E2084", {"start": v(-11.6, 3.85) * mm, "end": v(-11.72, 3.47) * mm});
            skArc(sketch, "E2085", {"start": v(-11.72, 3.47) * mm, "mid": v(-11.72, 3.44) * mm, "end": v(-11.7, 3.41) * mm});
            skLineSegment(sketch, "E2086", {"start": v(-10.05, -11.12) * mm, "end": v(-9.77, -10.74) * mm});
            skArc(sketch, "E2087", {"start": v(-9.77, -10.74) * mm, "mid": v(-9.76, -10.7) * mm, "end": v(-9.78, -10.68) * mm});
            skLineSegment(sketch, "E2088", {"start": v(-9.78, -10.68) * mm, "end": v(-10.1, -10.45) * mm});
            skArc(sketch, "E2089", {"start": v(-10.1, -10.45) * mm, "mid": v(-10.14, -10.44) * mm, "end": v(-10.17, -10.46) * mm});
            skLineSegment(sketch, "E2090", {"start": v(-10.17, -10.46) * mm, "end": v(-10.44, -10.83) * mm});
            skArc(sketch, "E2091", {"start": v(-10.44, -10.83) * mm, "mid": v(-10.45, -10.87) * mm, "end": v(-10.43, -10.9) * mm});
            skLineSegment(sketch, "E2092", {"start": v(-10.43, -10.9) * mm, "end": v(-10.11, -11.13) * mm});
            skArc(sketch, "E2093", {"start": v(-10.11, -11.13) * mm, "mid": v(-10.08, -11.14) * mm, "end": v(-10.05, -11.12) * mm});
            skLineSegment(sketch, "E2094", {"start": v(-9.33, -11.64) * mm, "end": v(-9.06, -11.26) * mm});
            skArc(sketch, "E2095", {"start": v(-9.06, -11.26) * mm, "mid": v(-9.05, -11.23) * mm, "end": v(-9.07, -11.2) * mm});
            skLineSegment(sketch, "E2096", {"start": v(-9.07, -11.2) * mm, "end": v(-9.39, -10.96) * mm});
            skArc(sketch, "E2097", {"start": v(-9.39, -10.96) * mm, "mid": v(-9.42, -10.96) * mm, "end": v(-9.45, -10.97) * mm});
            skLineSegment(sketch, "E2098", {"start": v(-9.45, -10.97) * mm, "end": v(-9.73, -11.35) * mm});
            skArc(sketch, "E2099", {"start": v(-9.73, -11.35) * mm, "mid": v(-9.74, -11.39) * mm, "end": v(-9.72, -11.42) * mm});
            skLineSegment(sketch, "E2100", {"start": v(-9.72, -11.42) * mm, "end": v(-9.4, -11.65) * mm});
            skArc(sketch, "E2101", {"start": v(-9.4, -11.65) * mm, "mid": v(-9.36, -11.66) * mm, "end": v(-9.33, -11.64) * mm});
            skLineSegment(sketch, "E2102", {"start": v(7.82, -12.14) * mm, "end": v(8.1, -12.52) * mm});
            skArc(sketch, "E2103", {"start": v(8.1, -12.52) * mm, "mid": v(8.13, -12.54) * mm, "end": v(8.16, -12.53) * mm});
            skLineSegment(sketch, "E2104", {"start": v(8.16, -12.53) * mm, "end": v(8.48, -12.3) * mm});
            skArc(sketch, "E2105", {"start": v(8.48, -12.3) * mm, "mid": v(8.5, -12.27) * mm, "end": v(8.5, -12.23) * mm});
            skLineSegment(sketch, "E2106", {"start": v(8.5, -12.23) * mm, "end": v(8.22, -11.86) * mm});
            skArc(sketch, "E2107", {"start": v(8.22, -11.86) * mm, "mid": v(8.19, -11.84) * mm, "end": v(8.15, -11.85) * mm});
            skLineSegment(sketch, "E2108", {"start": v(8.15, -11.85) * mm, "end": v(7.83, -12.08) * mm});
            skArc(sketch, "E2109", {"start": v(7.83, -12.08) * mm, "mid": v(7.81, -12.1) * mm, "end": v(7.82, -12.14) * mm});
            skLineSegment(sketch, "E2110", {"start": v(7.1, -12.66) * mm, "end": v(7.38, -13.04) * mm});
            skArc(sketch, "E2111", {"start": v(7.38, -13.04) * mm, "mid": v(7.41, -13.06) * mm, "end": v(7.45, -13.05) * mm});
            skLineSegment(sketch, "E2112", {"start": v(7.45, -13.05) * mm, "end": v(7.77, -12.82) * mm});
            skArc(sketch, "E2113", {"start": v(7.77, -12.82) * mm, "mid": v(7.79, -12.79) * mm, "end": v(7.78, -12.75) * mm});
            skLineSegment(sketch, "E2114", {"start": v(7.78, -12.75) * mm, "end": v(7.5, -12.37) * mm});
            skArc(sketch, "E2115", {"start": v(7.5, -12.37) * mm, "mid": v(7.47, -12.36) * mm, "end": v(7.44, -12.36) * mm});
            skLineSegment(sketch, "E2116", {"start": v(7.44, -12.36) * mm, "end": v(7.12, -12.6) * mm});
            skArc(sketch, "E2117", {"start": v(7.12, -12.6) * mm, "mid": v(7.1, -12.63) * mm, "end": v(7.1, -12.66) * mm});
            skLineSegment(sketch, "E2118", {"start": v(11.85, 1.72) * mm, "end": v(12.3, 1.86) * mm});
            skArc(sketch, "E2119", {"start": v(12.3, 1.86) * mm, "mid": v(12.32, 1.88) * mm, "end": v(12.32, 1.92) * mm});
            skLineSegment(sketch, "E2120", {"start": v(12.32, 1.92) * mm, "end": v(12.2, 2.3) * mm});
            skArc(sketch, "E2121", {"start": v(12.2, 2.3) * mm, "mid": v(12.18, 2.32) * mm, "end": v(12.14, 2.33) * mm});
            skLineSegment(sketch, "E2122", {"start": v(12.14, 2.33) * mm, "end": v(11.7, 2.18) * mm});
            skArc(sketch, "E2123", {"start": v(11.7, 2.18) * mm, "mid": v(11.67, 2.16) * mm, "end": v(11.67, 2.12) * mm});
            skLineSegment(sketch, "E2124", {"start": v(11.67, 2.12) * mm, "end": v(11.79, 1.75) * mm});
            skArc(sketch, "E2125", {"start": v(11.79, 1.75) * mm, "mid": v(11.81, 1.72) * mm, "end": v(11.85, 1.72) * mm});
            skLineSegment(sketch, "E2126", {"start": v(12.12, 0.88) * mm, "end": v(12.56, 1.02) * mm});
            skArc(sketch, "E2127", {"start": v(12.56, 1.02) * mm, "mid": v(12.59, 1.05) * mm, "end": v(12.6, 1.08) * mm});
            skLineSegment(sketch, "E2128", {"start": v(12.6, 1.08) * mm, "end": v(12.47, 1.46) * mm});
            skArc(sketch, "E2129", {"start": v(12.47, 1.46) * mm, "mid": v(12.45, 1.49) * mm, "end": v(12.41, 1.49) * mm});
            skLineSegment(sketch, "E2130", {"start": v(12.41, 1.49) * mm, "end": v(11.97, 1.34) * mm});
            skArc(sketch, "E2131", {"start": v(11.97, 1.34) * mm, "mid": v(11.94, 1.32) * mm, "end": v(11.94, 1.29) * mm});
            skLineSegment(sketch, "E2132", {"start": v(11.94, 1.29) * mm, "end": v(12.06, 0.9) * mm});
            skArc(sketch, "E2133", {"start": v(12.06, 0.9) * mm, "mid": v(12.08, 0.88) * mm, "end": v(12.12, 0.88) * mm});
            skLineSegment(sketch, "E2134", {"start": v(-1.3, 5.33) * mm, "end": v(-1.3, 4.87) * mm});
            skArc(sketch, "E2135", {"start": v(-1.3, 4.87) * mm, "mid": v(-1.3, 4.83) * mm, "end": v(-1.26, 4.82) * mm});
            skLineSegment(sketch, "E2136", {"start": v(-1.26, 4.82) * mm, "end": v(-0.86, 4.82) * mm});
            skArc(sketch, "E2137", {"start": v(-0.86, 4.82) * mm, "mid": v(-0.83, 4.83) * mm, "end": v(-0.82, 4.87) * mm});
            skLineSegment(sketch, "E2138", {"start": v(-0.82, 4.87) * mm, "end": v(-0.82, 5.33) * mm});
            skArc(sketch, "E2139", {"start": v(-0.82, 5.33) * mm, "mid": v(-0.83, 5.36) * mm, "end": v(-0.86, 5.38) * mm});
            skLineSegment(sketch, "E2140", {"start": v(-0.86, 5.38) * mm, "end": v(-1.26, 5.38) * mm});
            skArc(sketch, "E2141", {"start": v(-1.26, 5.38) * mm, "mid": v(-1.3, 5.36) * mm, "end": v(-1.3, 5.33) * mm});
            skLineSegment(sketch, "E2142", {"start": v(-2.18, 5.33) * mm, "end": v(-2.18, 4.87) * mm});
            skArc(sketch, "E2143", {"start": v(-2.18, 4.87) * mm, "mid": v(-2.17, 4.83) * mm, "end": v(-2.14, 4.82) * mm});
            skLineSegment(sketch, "E2144", {"start": v(-2.14, 4.82) * mm, "end": v(-1.74, 4.82) * mm});
            skArc(sketch, "E2145", {"start": v(-1.74, 4.82) * mm, "mid": v(-1.7, 4.83) * mm, "end": v(-1.7, 4.87) * mm});
            skLineSegment(sketch, "E2146", {"start": v(-1.7, 4.87) * mm, "end": v(-1.7, 5.33) * mm});
            skArc(sketch, "E2147", {"start": v(-1.7, 5.33) * mm, "mid": v(-1.7, 5.36) * mm, "end": v(-1.74, 5.38) * mm});
            skLineSegment(sketch, "E2148", {"start": v(-1.74, 5.38) * mm, "end": v(-2.14, 5.38) * mm});
            skArc(sketch, "E2149", {"start": v(-2.14, 5.38) * mm, "mid": v(-2.17, 5.36) * mm, "end": v(-2.18, 5.33) * mm});
            skLineSegment(sketch, "E2150", {"start": v(-12.16, 1.86) * mm, "end": v(-11.72, 1.72) * mm});
            skArc(sketch, "E2151", {"start": v(-11.72, 1.72) * mm, "mid": v(-11.68, 1.72) * mm, "end": v(-11.66, 1.75) * mm});
            skLineSegment(sketch, "E2152", {"start": v(-11.66, 1.75) * mm, "end": v(-11.54, 2.12) * mm});
            skArc(sketch, "E2153", {"start": v(-11.54, 2.12) * mm, "mid": v(-11.54, 2.16) * mm, "end": v(-11.57, 2.18) * mm});
            skLineSegment(sketch, "E2154", {"start": v(-11.57, 2.18) * mm, "end": v(-12, 2.33) * mm});
            skArc(sketch, "E2155", {"start": v(-12, 2.33) * mm, "mid": v(-12.05, 2.32) * mm, "end": v(-12.07, 2.3) * mm});
            skLineSegment(sketch, "E2156", {"start": v(-12.07, 2.3) * mm, "end": v(-12.2, 1.92) * mm});
            skArc(sketch, "E2157", {"start": v(-12.2, 1.92) * mm, "mid": v(-12.19, 1.88) * mm, "end": v(-12.16, 1.86) * mm});
            skLineSegment(sketch, "E2158", {"start": v(-12.43, 1.02) * mm, "end": v(-12, 0.88) * mm});
            skArc(sketch, "E2159", {"start": v(-12, 0.88) * mm, "mid": v(-11.95, 0.88) * mm, "end": v(-11.93, 0.9) * mm});
            skLineSegment(sketch, "E2160", {"start": v(-11.93, 0.9) * mm, "end": v(-11.8, 1.29) * mm});
            skArc(sketch, "E2161", {"start": v(-11.8, 1.29) * mm, "mid": v(-11.81, 1.32) * mm, "end": v(-11.84, 1.34) * mm});
            skLineSegment(sketch, "E2162", {"start": v(-11.84, 1.34) * mm, "end": v(-12.28, 1.49) * mm});
            skArc(sketch, "E2163", {"start": v(-12.28, 1.49) * mm, "mid": v(-12.32, 1.49) * mm, "end": v(-12.34, 1.46) * mm});
            skLineSegment(sketch, "E2164", {"start": v(-12.34, 1.46) * mm, "end": v(-12.46, 1.08) * mm});
            skArc(sketch, "E2165", {"start": v(-12.46, 1.08) * mm, "mid": v(-12.46, 1.05) * mm, "end": v(-12.43, 1.02) * mm});
            skLineSegment(sketch, "E2166", {"start": v(-8.05, -12.52) * mm, "end": v(-7.77, -12.14) * mm});
            skArc(sketch, "E2167", {"start": v(-7.77, -12.14) * mm, "mid": v(-7.76, -12.1) * mm, "end": v(-7.78, -12.08) * mm});
            skLineSegment(sketch, "E2168", {"start": v(-7.78, -12.08) * mm, "end": v(-8.1, -11.85) * mm});
            skArc(sketch, "E2169", {"start": v(-8.1, -11.85) * mm, "mid": v(-8.14, -11.84) * mm, "end": v(-8.17, -11.86) * mm});
            skLineSegment(sketch, "E2170", {"start": v(-8.17, -11.86) * mm, "end": v(-8.44, -12.23) * mm});
            skArc(sketch, "E2171", {"start": v(-8.44, -12.23) * mm, "mid": v(-8.45, -12.27) * mm, "end": v(-8.43, -12.3) * mm});
            skLineSegment(sketch, "E2172", {"start": v(-8.43, -12.3) * mm, "end": v(-8.11, -12.53) * mm});
            skArc(sketch, "E2173", {"start": v(-8.11, -12.53) * mm, "mid": v(-8.08, -12.54) * mm, "end": v(-8.05, -12.52) * mm});
            skLineSegment(sketch, "E2174", {"start": v(-7.33, -13.04) * mm, "end": v(-7.06, -12.66) * mm});
            skArc(sketch, "E2175", {"start": v(-7.06, -12.66) * mm, "mid": v(-7.05, -12.63) * mm, "end": v(-7.07, -12.6) * mm});
            skLineSegment(sketch, "E2176", {"start": v(-7.07, -12.6) * mm, "end": v(-7.39, -12.36) * mm});
            skArc(sketch, "E2177", {"start": v(-7.39, -12.36) * mm, "mid": v(-7.42, -12.36) * mm, "end": v(-7.45, -12.37) * mm});
            skLineSegment(sketch, "E2178", {"start": v(-7.45, -12.37) * mm, "end": v(-7.73, -12.75) * mm});
            skArc(sketch, "E2179", {"start": v(-7.73, -12.75) * mm, "mid": v(-7.74, -12.79) * mm, "end": v(-7.72, -12.82) * mm});
            skLineSegment(sketch, "E2180", {"start": v(-7.72, -12.82) * mm, "end": v(-7.4, -13.05) * mm});
            skArc(sketch, "E2181", {"start": v(-7.4, -13.05) * mm, "mid": v(-7.36, -13.06) * mm, "end": v(-7.33, -13.04) * mm});
            skLineSegment(sketch, "E2182", {"start": v(4.6, -10.73) * mm, "end": v(4.6, -10.27) * mm});
            skArc(sketch, "E2183", {"start": v(4.6, -10.27) * mm, "mid": v(4.6, -10.23) * mm, "end": v(4.56, -10.22) * mm});
            skLineSegment(sketch, "E2184", {"start": v(4.56, -10.22) * mm, "end": v(4.16, -10.22) * mm});
            skArc(sketch, "E2185", {"start": v(4.16, -10.22) * mm, "mid": v(4.13, -10.23) * mm, "end": v(4.12, -10.27) * mm});
            skLineSegment(sketch, "E2186", {"start": v(4.12, -10.27) * mm, "end": v(4.12, -10.73) * mm});
            skArc(sketch, "E2187", {"start": v(4.12, -10.73) * mm, "mid": v(4.13, -10.76) * mm, "end": v(4.16, -10.78) * mm});
            skLineSegment(sketch, "E2188", {"start": v(4.16, -10.78) * mm, "end": v(4.56, -10.78) * mm});
            skArc(sketch, "E2189", {"start": v(4.56, -10.78) * mm, "mid": v(4.6, -10.76) * mm, "end": v(4.6, -10.73) * mm});
            skLineSegment(sketch, "E2190", {"start": v(5.48, -10.73) * mm, "end": v(5.48, -10.27) * mm});
            skArc(sketch, "E2191", {"start": v(5.48, -10.27) * mm, "mid": v(5.47, -10.23) * mm, "end": v(5.44, -10.22) * mm});
            skLineSegment(sketch, "E2192", {"start": v(5.44, -10.22) * mm, "end": v(5.04, -10.22) * mm});
            skArc(sketch, "E2193", {"start": v(5.04, -10.22) * mm, "mid": v(5, -10.23) * mm, "end": v(5, -10.27) * mm});
            skLineSegment(sketch, "E2194", {"start": v(5, -10.27) * mm, "end": v(5, -10.73) * mm});
            skArc(sketch, "E2195", {"start": v(5, -10.73) * mm, "mid": v(5, -10.76) * mm, "end": v(5.04, -10.78) * mm});
            skLineSegment(sketch, "E2196", {"start": v(5.04, -10.78) * mm, "end": v(5.44, -10.78) * mm});
            skArc(sketch, "E2197", {"start": v(5.44, -10.78) * mm, "mid": v(5.47, -10.76) * mm, "end": v(5.48, -10.73) * mm});
            skLineSegment(sketch, "E2198", {"start": v(4.97, -7.4) * mm, "end": v(5.43, -7.4) * mm});
            skArc(sketch, "E2199", {"start": v(5.43, -7.4) * mm, "mid": v(5.47, -7.39) * mm, "end": v(5.48, -7.36) * mm});
            skLineSegment(sketch, "E2200", {"start": v(5.48, -7.36) * mm, "end": v(5.48, -6.96) * mm});
            skArc(sketch, "E2201", {"start": v(5.48, -6.96) * mm, "mid": v(5.47, -6.93) * mm, "end": v(5.43, -6.91) * mm});
            skLineSegment(sketch, "E2202", {"start": v(5.43, -6.91) * mm, "end": v(4.97, -6.91) * mm});
            skArc(sketch, "E2203", {"start": v(4.97, -6.91) * mm, "mid": v(4.93, -6.93) * mm, "end": v(4.92, -6.96) * mm});
            skLineSegment(sketch, "E2204", {"start": v(4.92, -6.96) * mm, "end": v(4.92, -7.36) * mm});
            skArc(sketch, "E2205", {"start": v(4.92, -7.36) * mm, "mid": v(4.93, -7.39) * mm, "end": v(4.97, -7.4) * mm});
            skLineSegment(sketch, "E2206", {"start": v(4.97, -8.28) * mm, "end": v(5.43, -8.28) * mm});
            skArc(sketch, "E2207", {"start": v(5.43, -8.28) * mm, "mid": v(5.47, -8.27) * mm, "end": v(5.48, -8.24) * mm});
            skLineSegment(sketch, "E2208", {"start": v(5.48, -8.24) * mm, "end": v(5.48, -7.84) * mm});
            skArc(sketch, "E2209", {"start": v(5.48, -7.84) * mm, "mid": v(5.47, -7.8) * mm, "end": v(5.43, -7.8) * mm});
            skLineSegment(sketch, "E2210", {"start": v(5.43, -7.8) * mm, "end": v(4.97, -7.8) * mm});
            skArc(sketch, "E2211", {"start": v(4.97, -7.8) * mm, "mid": v(4.93, -7.8) * mm, "end": v(4.92, -7.84) * mm});
            skLineSegment(sketch, "E2212", {"start": v(4.92, -7.84) * mm, "end": v(4.92, -8.24) * mm});
            skArc(sketch, "E2213", {"start": v(4.92, -8.24) * mm, "mid": v(4.93, -8.27) * mm, "end": v(4.97, -8.28) * mm});
            skLineSegment(sketch, "E2214", {"start": v(-7.87, -1.6) * mm, "end": v(-8.33, -1.6) * mm});
            skArc(sketch, "E2215", {"start": v(-8.33, -1.6) * mm, "mid": v(-8.37, -1.6) * mm, "end": v(-8.38, -1.64) * mm});
            skLineSegment(sketch, "E2216", {"start": v(-8.38, -1.64) * mm, "end": v(-8.38, -2.04) * mm});
            skArc(sketch, "E2217", {"start": v(-8.38, -2.04) * mm, "mid": v(-8.37, -2.07) * mm, "end": v(-8.33, -2.08) * mm});
            skLineSegment(sketch, "E2218", {"start": v(-8.33, -2.08) * mm, "end": v(-7.87, -2.08) * mm});
            skArc(sketch, "E2219", {"start": v(-7.87, -2.08) * mm, "mid": v(-7.83, -2.07) * mm, "end": v(-7.82, -2.04) * mm});
            skLineSegment(sketch, "E2220", {"start": v(-7.82, -2.04) * mm, "end": v(-7.82, -1.64) * mm});
            skArc(sketch, "E2221", {"start": v(-7.82, -1.64) * mm, "mid": v(-7.83, -1.6) * mm, "end": v(-7.87, -1.6) * mm});
            skLineSegment(sketch, "E2222", {"start": v(-7.87, -0.71) * mm, "end": v(-8.33, -0.71) * mm});
            skArc(sketch, "E2223", {"start": v(-8.33, -0.71) * mm, "mid": v(-8.37, -0.73) * mm, "end": v(-8.38, -0.76) * mm});
            skLineSegment(sketch, "E2224", {"start": v(-8.38, -0.76) * mm, "end": v(-8.38, -1.16) * mm});
            skArc(sketch, "E2225", {"start": v(-8.38, -1.16) * mm, "mid": v(-8.37, -1.19) * mm, "end": v(-8.33, -1.2) * mm});
            skLineSegment(sketch, "E2226", {"start": v(-8.33, -1.2) * mm, "end": v(-7.87, -1.2) * mm});
            skArc(sketch, "E2227", {"start": v(-7.87, -1.2) * mm, "mid": v(-7.83, -1.19) * mm, "end": v(-7.82, -1.16) * mm});
            skLineSegment(sketch, "E2228", {"start": v(-7.82, -1.16) * mm, "end": v(-7.82, -0.76) * mm});
            skArc(sketch, "E2229", {"start": v(-7.82, -0.76) * mm, "mid": v(-7.83, -0.73) * mm, "end": v(-7.87, -0.71) * mm});
            skLineSegment(sketch, "E2230", {"start": v(-5.13, 8.8) * mm, "end": v(-4.67, 8.8) * mm});
            skArc(sketch, "E2231", {"start": v(-4.67, 8.8) * mm, "mid": v(-4.63, 8.81) * mm, "end": v(-4.62, 8.84) * mm});
            skLineSegment(sketch, "E2232", {"start": v(-4.62, 8.84) * mm, "end": v(-4.62, 9.24) * mm});
            skArc(sketch, "E2233", {"start": v(-4.62, 9.24) * mm, "mid": v(-4.63, 9.27) * mm, "end": v(-4.67, 9.29) * mm});
            skLineSegment(sketch, "E2234", {"start": v(-4.67, 9.29) * mm, "end": v(-5.13, 9.29) * mm});
            skArc(sketch, "E2235", {"start": v(-5.13, 9.29) * mm, "mid": v(-5.17, 9.27) * mm, "end": v(-5.18, 9.24) * mm});
            skLineSegment(sketch, "E2236", {"start": v(-5.18, 9.24) * mm, "end": v(-5.18, 8.84) * mm});
            skArc(sketch, "E2237", {"start": v(-5.18, 8.84) * mm, "mid": v(-5.17, 8.81) * mm, "end": v(-5.13, 8.8) * mm});
            skLineSegment(sketch, "E2238", {"start": v(-5.13, 7.92) * mm, "end": v(-4.67, 7.92) * mm});
            skArc(sketch, "E2239", {"start": v(-4.67, 7.92) * mm, "mid": v(-4.63, 7.93) * mm, "end": v(-4.62, 7.96) * mm});
            skLineSegment(sketch, "E2240", {"start": v(-4.62, 7.96) * mm, "end": v(-4.62, 8.36) * mm});
            skArc(sketch, "E2241", {"start": v(-4.62, 8.36) * mm, "mid": v(-4.63, 8.4) * mm, "end": v(-4.67, 8.4) * mm});
            skLineSegment(sketch, "E2242", {"start": v(-4.67, 8.4) * mm, "end": v(-5.13, 8.4) * mm});
            skArc(sketch, "E2243", {"start": v(-5.13, 8.4) * mm, "mid": v(-5.17, 8.4) * mm, "end": v(-5.18, 8.36) * mm});
            skLineSegment(sketch, "E2244", {"start": v(-5.18, 8.36) * mm, "end": v(-5.18, 7.96) * mm});
            skArc(sketch, "E2245", {"start": v(-5.18, 7.96) * mm, "mid": v(-5.17, 7.93) * mm, "end": v(-5.13, 7.92) * mm});
            skLineSegment(sketch, "E2246", {"start": v(5.13, 8.4) * mm, "end": v(4.67, 8.4) * mm});
            skArc(sketch, "E2247", {"start": v(4.67, 8.4) * mm, "mid": v(4.63, 8.4) * mm, "end": v(4.62, 8.36) * mm});
            skLineSegment(sketch, "E2248", {"start": v(4.62, 8.36) * mm, "end": v(4.62, 7.96) * mm});
            skArc(sketch, "E2249", {"start": v(4.62, 7.96) * mm, "mid": v(4.63, 7.93) * mm, "end": v(4.67, 7.92) * mm});
            skLineSegment(sketch, "E2250", {"start": v(4.67, 7.92) * mm, "end": v(5.13, 7.92) * mm});
            skArc(sketch, "E2251", {"start": v(5.13, 7.92) * mm, "mid": v(5.17, 7.93) * mm, "end": v(5.18, 7.96) * mm});
            skLineSegment(sketch, "E2252", {"start": v(5.18, 7.96) * mm, "end": v(5.18, 8.36) * mm});
            skArc(sketch, "E2253", {"start": v(5.18, 8.36) * mm, "mid": v(5.17, 8.4) * mm, "end": v(5.13, 8.4) * mm});
            skLineSegment(sketch, "E2254", {"start": v(5.13, 9.29) * mm, "end": v(4.67, 9.29) * mm});
            skArc(sketch, "E2255", {"start": v(4.67, 9.29) * mm, "mid": v(4.63, 9.27) * mm, "end": v(4.62, 9.24) * mm});
            skLineSegment(sketch, "E2256", {"start": v(4.62, 9.24) * mm, "end": v(4.62, 8.84) * mm});
            skArc(sketch, "E2257", {"start": v(4.62, 8.84) * mm, "mid": v(4.63, 8.81) * mm, "end": v(4.67, 8.8) * mm});
            skLineSegment(sketch, "E2258", {"start": v(4.67, 8.8) * mm, "end": v(5.13, 8.8) * mm});
            skArc(sketch, "E2259", {"start": v(5.13, 8.8) * mm, "mid": v(5.17, 8.81) * mm, "end": v(5.18, 8.84) * mm});
            skLineSegment(sketch, "E2260", {"start": v(5.18, 8.84) * mm, "end": v(5.18, 9.24) * mm});
            skArc(sketch, "E2261", {"start": v(5.18, 9.24) * mm, "mid": v(5.17, 9.27) * mm, "end": v(5.13, 9.29) * mm});
            skLineSegment(sketch, "E2262", {"start": v(5, -11.47) * mm, "end": v(5, -11.93) * mm});
            skArc(sketch, "E2263", {"start": v(5, -11.93) * mm, "mid": v(5, -11.96) * mm, "end": v(5.04, -11.98) * mm});
            skLineSegment(sketch, "E2264", {"start": v(5.04, -11.98) * mm, "end": v(5.44, -11.98) * mm});
            skArc(sketch, "E2265", {"start": v(5.44, -11.98) * mm, "mid": v(5.47, -11.96) * mm, "end": v(5.48, -11.93) * mm});
            skLineSegment(sketch, "E2266", {"start": v(5.48, -11.93) * mm, "end": v(5.48, -11.47) * mm});
            skArc(sketch, "E2267", {"start": v(5.48, -11.47) * mm, "mid": v(5.47, -11.43) * mm, "end": v(5.44, -11.42) * mm});
            skLineSegment(sketch, "E2268", {"start": v(5.44, -11.42) * mm, "end": v(5.04, -11.42) * mm});
            skArc(sketch, "E2269", {"start": v(5.04, -11.42) * mm, "mid": v(5, -11.43) * mm, "end": v(5, -11.47) * mm});
            skLineSegment(sketch, "E2270", {"start": v(4.12, -11.47) * mm, "end": v(4.12, -11.93) * mm});
            skArc(sketch, "E2271", {"start": v(4.12, -11.93) * mm, "mid": v(4.13, -11.96) * mm, "end": v(4.16, -11.98) * mm});
            skLineSegment(sketch, "E2272", {"start": v(4.16, -11.98) * mm, "end": v(4.56, -11.98) * mm});
            skArc(sketch, "E2273", {"start": v(4.56, -11.98) * mm, "mid": v(4.6, -11.96) * mm, "end": v(4.6, -11.93) * mm});
            skLineSegment(sketch, "E2274", {"start": v(4.6, -11.93) * mm, "end": v(4.6, -11.47) * mm});
            skArc(sketch, "E2275", {"start": v(4.6, -11.47) * mm, "mid": v(4.6, -11.43) * mm, "end": v(4.56, -11.42) * mm});
            skLineSegment(sketch, "E2276", {"start": v(4.56, -11.42) * mm, "end": v(4.16, -11.42) * mm});
            skArc(sketch, "E2277", {"start": v(4.16, -11.42) * mm, "mid": v(4.13, -11.43) * mm, "end": v(4.12, -11.47) * mm});
            skLineSegment(sketch, "E2278", {"start": v(-5.43, -7.4) * mm, "end": v(-4.97, -7.4) * mm});
            skArc(sketch, "E2279", {"start": v(-4.97, -7.4) * mm, "mid": v(-4.93, -7.39) * mm, "end": v(-4.92, -7.36) * mm});
            skLineSegment(sketch, "E2280", {"start": v(-4.92, -7.36) * mm, "end": v(-4.92, -6.96) * mm});
            skArc(sketch, "E2281", {"start": v(-4.92, -6.96) * mm, "mid": v(-4.93, -6.93) * mm, "end": v(-4.97, -6.91) * mm});
            skLineSegment(sketch, "E2282", {"start": v(-4.97, -6.91) * mm, "end": v(-5.43, -6.91) * mm});
            skArc(sketch, "E2283", {"start": v(-5.43, -6.91) * mm, "mid": v(-5.47, -6.93) * mm, "end": v(-5.48, -6.96) * mm});
            skLineSegment(sketch, "E2284", {"start": v(-5.48, -6.96) * mm, "end": v(-5.48, -7.36) * mm});
            skArc(sketch, "E2285", {"start": v(-5.48, -7.36) * mm, "mid": v(-5.47, -7.39) * mm, "end": v(-5.43, -7.4) * mm});
            skLineSegment(sketch, "E2286", {"start": v(-5.43, -8.28) * mm, "end": v(-4.97, -8.28) * mm});
            skArc(sketch, "E2287", {"start": v(-4.97, -8.28) * mm, "mid": v(-4.93, -8.27) * mm, "end": v(-4.92, -8.24) * mm});
            skLineSegment(sketch, "E2288", {"start": v(-4.92, -8.24) * mm, "end": v(-4.92, -7.84) * mm});
            skArc(sketch, "E2289", {"start": v(-4.92, -7.84) * mm, "mid": v(-4.93, -7.8) * mm, "end": v(-4.97, -7.8) * mm});
            skLineSegment(sketch, "E2290", {"start": v(-4.97, -7.8) * mm, "end": v(-5.43, -7.8) * mm});
            skArc(sketch, "E2291", {"start": v(-5.43, -7.8) * mm, "mid": v(-5.47, -7.8) * mm, "end": v(-5.48, -7.84) * mm});
            skLineSegment(sketch, "E2292", {"start": v(-5.48, -7.84) * mm, "end": v(-5.48, -8.24) * mm});
            skArc(sketch, "E2293", {"start": v(-5.48, -8.24) * mm, "mid": v(-5.47, -8.27) * mm, "end": v(-5.43, -8.28) * mm});
            skLineSegment(sketch, "E2294", {"start": v(5.87, -13.6) * mm, "end": v(6.15, -13.97) * mm});
            skArc(sketch, "E2295", {"start": v(6.15, -13.97) * mm, "mid": v(6.18, -13.99) * mm, "end": v(6.21, -13.98) * mm});
            skLineSegment(sketch, "E2296", {"start": v(6.21, -13.98) * mm, "end": v(6.53, -13.75) * mm});
            skArc(sketch, "E2297", {"start": v(6.53, -13.75) * mm, "mid": v(6.55, -13.72) * mm, "end": v(6.54, -13.68) * mm});
            skLineSegment(sketch, "E2298", {"start": v(6.54, -13.68) * mm, "end": v(6.27, -13.3) * mm});
            skArc(sketch, "E2299", {"start": v(6.27, -13.3) * mm, "mid": v(6.24, -13.29) * mm, "end": v(6.2, -13.3) * mm});
            skLineSegment(sketch, "E2300", {"start": v(6.2, -13.3) * mm, "end": v(5.88, -13.53) * mm});
            skArc(sketch, "E2301", {"start": v(5.88, -13.53) * mm, "mid": v(5.86, -13.56) * mm, "end": v(5.87, -13.6) * mm});
            skLineSegment(sketch, "E2302", {"start": v(5.16, -14.11) * mm, "end": v(5.43, -14.49) * mm});
            skArc(sketch, "E2303", {"start": v(5.43, -14.49) * mm, "mid": v(5.46, -14.5) * mm, "end": v(5.5, -14.5) * mm});
            skLineSegment(sketch, "E2304", {"start": v(5.5, -14.5) * mm, "end": v(5.82, -14.27) * mm});
            skArc(sketch, "E2305", {"start": v(5.82, -14.27) * mm, "mid": v(5.84, -14.24) * mm, "end": v(5.83, -14.2) * mm});
            skLineSegment(sketch, "E2306", {"start": v(5.83, -14.2) * mm, "end": v(5.55, -13.82) * mm});
            skArc(sketch, "E2307", {"start": v(5.55, -13.82) * mm, "mid": v(5.52, -13.8) * mm, "end": v(5.49, -13.81) * mm});
            skLineSegment(sketch, "E2308", {"start": v(5.49, -13.81) * mm, "end": v(5.17, -14.05) * mm});
            skArc(sketch, "E2309", {"start": v(5.17, -14.05) * mm, "mid": v(5.15, -14.08) * mm, "end": v(5.16, -14.11) * mm});
            skLineSegment(sketch, "E2310", {"start": v(12.6, -0.61) * mm, "end": v(13.04, -0.47) * mm});
            skArc(sketch, "E2311", {"start": v(13.04, -0.47) * mm, "mid": v(13.07, -0.45) * mm, "end": v(13.07, -0.41) * mm});
            skLineSegment(sketch, "E2312", {"start": v(13.07, -0.41) * mm, "end": v(12.95, -0.03) * mm});
            skArc(sketch, "E2313", {"start": v(12.95, -0.03) * mm, "mid": v(12.93, 0) * mm, "end": v(12.89, 0) * mm});
            skLineSegment(sketch, "E2314", {"start": v(12.89, 0) * mm, "end": v(12.45, -0.15) * mm});
            skArc(sketch, "E2315", {"start": v(12.45, -0.15) * mm, "mid": v(12.42, -0.17) * mm, "end": v(12.42, -0.2) * mm});
            skLineSegment(sketch, "E2316", {"start": v(12.42, -0.2) * mm, "end": v(12.54, -0.58) * mm});
            skArc(sketch, "E2317", {"start": v(12.54, -0.58) * mm, "mid": v(12.56, -0.61) * mm, "end": v(12.6, -0.61) * mm});
            skLineSegment(sketch, "E2318", {"start": v(12.87, -1.45) * mm, "end": v(13.31, -1.3) * mm});
            skArc(sketch, "E2319", {"start": v(13.31, -1.3) * mm, "mid": v(13.34, -1.28) * mm, "end": v(13.34, -1.25) * mm});
            skLineSegment(sketch, "E2320", {"start": v(13.34, -1.25) * mm, "end": v(13.22, -0.87) * mm});
            skArc(sketch, "E2321", {"start": v(13.22, -0.87) * mm, "mid": v(13.2, -0.84) * mm, "end": v(13.16, -0.84) * mm});
            skLineSegment(sketch, "E2322", {"start": v(13.16, -0.84) * mm, "end": v(12.72, -0.99) * mm});
            skArc(sketch, "E2323", {"start": v(12.72, -0.99) * mm, "mid": v(12.7, -1) * mm, "end": v(12.69, -1.04) * mm});
            skLineSegment(sketch, "E2324", {"start": v(12.69, -1.04) * mm, "end": v(12.81, -1.42) * mm});
            skArc(sketch, "E2325", {"start": v(12.81, -1.42) * mm, "mid": v(12.83, -1.45) * mm, "end": v(12.87, -1.45) * mm});
            skLineSegment(sketch, "E2326", {"start": v(-3.7, 5.33) * mm, "end": v(-3.7, 4.87) * mm});
            skArc(sketch, "E2327", {"start": v(-3.7, 4.87) * mm, "mid": v(-3.7, 4.83) * mm, "end": v(-3.66, 4.82) * mm});
            skLineSegment(sketch, "E2328", {"start": v(-3.66, 4.82) * mm, "end": v(-3.26, 4.82) * mm});
            skArc(sketch, "E2329", {"start": v(-3.26, 4.82) * mm, "mid": v(-3.23, 4.83) * mm, "end": v(-3.22, 4.87) * mm});
            skLineSegment(sketch, "E2330", {"start": v(-3.22, 4.87) * mm, "end": v(-3.22, 5.33) * mm});
            skArc(sketch, "E2331", {"start": v(-3.22, 5.33) * mm, "mid": v(-3.23, 5.36) * mm, "end": v(-3.26, 5.38) * mm});
            skLineSegment(sketch, "E2332", {"start": v(-3.26, 5.38) * mm, "end": v(-3.66, 5.38) * mm});
            skArc(sketch, "E2333", {"start": v(-3.66, 5.38) * mm, "mid": v(-3.7, 5.36) * mm, "end": v(-3.7, 5.33) * mm});
            skLineSegment(sketch, "E2334", {"start": v(-4.58, 5.33) * mm, "end": v(-4.58, 4.87) * mm});
            skArc(sketch, "E2335", {"start": v(-4.58, 4.87) * mm, "mid": v(-4.57, 4.83) * mm, "end": v(-4.54, 4.82) * mm});
            skLineSegment(sketch, "E2336", {"start": v(-4.54, 4.82) * mm, "end": v(-4.14, 4.82) * mm});
            skArc(sketch, "E2337", {"start": v(-4.14, 4.82) * mm, "mid": v(-4.1, 4.83) * mm, "end": v(-4.1, 4.87) * mm});
            skLineSegment(sketch, "E2338", {"start": v(-4.1, 4.87) * mm, "end": v(-4.1, 5.33) * mm});
            skArc(sketch, "E2339", {"start": v(-4.1, 5.33) * mm, "mid": v(-4.1, 5.36) * mm, "end": v(-4.14, 5.38) * mm});
            skLineSegment(sketch, "E2340", {"start": v(-4.14, 5.38) * mm, "end": v(-4.54, 5.38) * mm});
            skArc(sketch, "E2341", {"start": v(-4.54, 5.38) * mm, "mid": v(-4.57, 5.36) * mm, "end": v(-4.58, 5.33) * mm});
            skLineSegment(sketch, "E2342", {"start": v(-12.96, -0.54) * mm, "end": v(-12.52, -0.68) * mm});
            skArc(sketch, "E2343", {"start": v(-12.52, -0.68) * mm, "mid": v(-12.48, -0.68) * mm, "end": v(-12.46, -0.65) * mm});
            skLineSegment(sketch, "E2344", {"start": v(-12.46, -0.65) * mm, "end": v(-12.34, -0.28) * mm});
            skArc(sketch, "E2345", {"start": v(-12.34, -0.28) * mm, "mid": v(-12.34, -0.24) * mm, "end": v(-12.37, -0.22) * mm});
            skLineSegment(sketch, "E2346", {"start": v(-12.37, -0.22) * mm, "end": v(-12.8, -0.07) * mm});
            skArc(sketch, "E2347", {"start": v(-12.8, -0.07) * mm, "mid": v(-12.85, -0.08) * mm, "end": v(-12.87, -0.1) * mm});
            skLineSegment(sketch, "E2348", {"start": v(-12.87, -0.1) * mm, "end": v(-13, -0.48) * mm});
            skArc(sketch, "E2349", {"start": v(-13, -0.48) * mm, "mid": v(-12.99, -0.52) * mm, "end": v(-12.96, -0.54) * mm});
            skLineSegment(sketch, "E2350", {"start": v(-13.23, -1.38) * mm, "end": v(-12.8, -1.52) * mm});
            skArc(sketch, "E2351", {"start": v(-12.8, -1.52) * mm, "mid": v(-12.75, -1.52) * mm, "end": v(-12.73, -1.5) * mm});
            skLineSegment(sketch, "E2352", {"start": v(-12.73, -1.5) * mm, "end": v(-12.6, -1.11) * mm});
            skArc(sketch, "E2353", {"start": v(-12.6, -1.11) * mm, "mid": v(-12.61, -1.08) * mm, "end": v(-12.64, -1.06) * mm});
            skLineSegment(sketch, "E2354", {"start": v(-12.64, -1.06) * mm, "end": v(-13.08, -0.91) * mm});
            skArc(sketch, "E2355", {"start": v(-13.08, -0.91) * mm, "mid": v(-13.12, -0.91) * mm, "end": v(-13.14, -0.94) * mm});
            skLineSegment(sketch, "E2356", {"start": v(-13.14, -0.94) * mm, "end": v(-13.26, -1.32) * mm});
            skArc(sketch, "E2357", {"start": v(-13.26, -1.32) * mm, "mid": v(-13.26, -1.35) * mm, "end": v(-13.23, -1.38) * mm});
            skLineSegment(sketch, "E2358", {"start": v(-6.13, -13.94) * mm, "end": v(-5.85, -13.56) * mm});
            skArc(sketch, "E2359", {"start": v(-5.85, -13.56) * mm, "mid": v(-5.84, -13.53) * mm, "end": v(-5.86, -13.5) * mm});
            skLineSegment(sketch, "E2360", {"start": v(-5.86, -13.5) * mm, "end": v(-6.18, -13.27) * mm});
            skArc(sketch, "E2361", {"start": v(-6.18, -13.27) * mm, "mid": v(-6.22, -13.26) * mm, "end": v(-6.25, -13.28) * mm});
            skLineSegment(sketch, "E2362", {"start": v(-6.25, -13.28) * mm, "end": v(-6.52, -13.65) * mm});
            skArc(sketch, "E2363", {"start": v(-6.52, -13.65) * mm, "mid": v(-6.53, -13.69) * mm, "end": v(-6.51, -13.72) * mm});
            skLineSegment(sketch, "E2364", {"start": v(-6.51, -13.72) * mm, "end": v(-6.2, -13.95) * mm});
            skArc(sketch, "E2365", {"start": v(-6.2, -13.95) * mm, "mid": v(-6.16, -13.96) * mm, "end": v(-6.13, -13.94) * mm});
            skLineSegment(sketch, "E2366", {"start": v(-5.41, -14.46) * mm, "end": v(-5.14, -14.08) * mm});
            skArc(sketch, "E2367", {"start": v(-5.14, -14.08) * mm, "mid": v(-5.13, -14.05) * mm, "end": v(-5.15, -14.02) * mm});
            skLineSegment(sketch, "E2368", {"start": v(-5.15, -14.02) * mm, "end": v(-5.47, -13.78) * mm});
            skArc(sketch, "E2369", {"start": v(-5.47, -13.78) * mm, "mid": v(-5.5, -13.78) * mm, "end": v(-5.53, -13.8) * mm});
            skLineSegment(sketch, "E2370", {"start": v(-5.53, -13.8) * mm, "end": v(-5.8, -14.17) * mm});
            skArc(sketch, "E2371", {"start": v(-5.8, -14.17) * mm, "mid": v(-5.82, -14.2) * mm, "end": v(-5.8, -14.24) * mm});
            skLineSegment(sketch, "E2372", {"start": v(-5.8, -14.24) * mm, "end": v(-5.48, -14.47) * mm});
            skArc(sketch, "E2373", {"start": v(-5.48, -14.47) * mm, "mid": v(-5.44, -14.48) * mm, "end": v(-5.41, -14.46) * mm});
            skLineSegment(sketch, "E2374", {"start": v(8.3, -2.97) * mm, "end": v(8.3, -3.43) * mm});
            skArc(sketch, "E2375", {"start": v(8.3, -3.43) * mm, "mid": v(8.3, -3.46) * mm, "end": v(8.34, -3.48) * mm});
            skLineSegment(sketch, "E2376", {"start": v(8.34, -3.48) * mm, "end": v(8.74, -3.48) * mm});
            skArc(sketch, "E2377", {"start": v(8.74, -3.48) * mm, "mid": v(8.77, -3.46) * mm, "end": v(8.78, -3.43) * mm});
            skLineSegment(sketch, "E2378", {"start": v(8.78, -3.43) * mm, "end": v(8.78, -2.97) * mm});
            skArc(sketch, "E2379", {"start": v(8.78, -2.97) * mm, "mid": v(8.77, -2.93) * mm, "end": v(8.74, -2.92) * mm});
            skLineSegment(sketch, "E2380", {"start": v(8.74, -2.92) * mm, "end": v(8.34, -2.92) * mm});
            skArc(sketch, "E2381", {"start": v(8.34, -2.92) * mm, "mid": v(8.3, -2.93) * mm, "end": v(8.3, -2.97) * mm});
            skLineSegment(sketch, "E2382", {"start": v(7.42, -2.97) * mm, "end": v(7.42, -3.43) * mm});
            skArc(sketch, "E2383", {"start": v(7.42, -3.43) * mm, "mid": v(7.43, -3.46) * mm, "end": v(7.46, -3.48) * mm});
            skLineSegment(sketch, "E2384", {"start": v(7.46, -3.48) * mm, "end": v(7.86, -3.48) * mm});
            skArc(sketch, "E2385", {"start": v(7.86, -3.48) * mm, "mid": v(7.9, -3.46) * mm, "end": v(7.9, -3.43) * mm});
            skLineSegment(sketch, "E2386", {"start": v(7.9, -3.43) * mm, "end": v(7.9, -2.97) * mm});
            skArc(sketch, "E2387", {"start": v(7.9, -2.97) * mm, "mid": v(7.9, -2.93) * mm, "end": v(7.86, -2.92) * mm});
            skLineSegment(sketch, "E2388", {"start": v(7.86, -2.92) * mm, "end": v(7.46, -2.92) * mm});
            skArc(sketch, "E2389", {"start": v(7.46, -2.92) * mm, "mid": v(7.43, -2.93) * mm, "end": v(7.42, -2.97) * mm});
            skLineSegment(sketch, "E2390", {"start": v(7.4, 1.67) * mm, "end": v(7.4, 2.13) * mm});
            skArc(sketch, "E2391", {"start": v(7.4, 2.13) * mm, "mid": v(7.4, 2.17) * mm, "end": v(7.36, 2.18) * mm});
            skLineSegment(sketch, "E2392", {"start": v(7.36, 2.18) * mm, "end": v(6.96, 2.18) * mm});
            skArc(sketch, "E2393", {"start": v(6.96, 2.18) * mm, "mid": v(6.93, 2.17) * mm, "end": v(6.92, 2.13) * mm});
            skLineSegment(sketch, "E2394", {"start": v(6.92, 2.13) * mm, "end": v(6.92, 1.67) * mm});
            skArc(sketch, "E2395", {"start": v(6.92, 1.67) * mm, "mid": v(6.93, 1.64) * mm, "end": v(6.96, 1.62) * mm});
            skLineSegment(sketch, "E2396", {"start": v(6.96, 1.62) * mm, "end": v(7.36, 1.62) * mm});
            skArc(sketch, "E2397", {"start": v(7.36, 1.62) * mm, "mid": v(7.4, 1.64) * mm, "end": v(7.4, 1.67) * mm});
            skLineSegment(sketch, "E2398", {"start": v(8.28, 1.67) * mm, "end": v(8.28, 2.13) * mm});
            skArc(sketch, "E2399", {"start": v(8.28, 2.13) * mm, "mid": v(8.27, 2.17) * mm, "end": v(8.24, 2.18) * mm});
            skLineSegment(sketch, "E2400", {"start": v(8.24, 2.18) * mm, "end": v(7.84, 2.18) * mm});
            skArc(sketch, "E2401", {"start": v(7.84, 2.18) * mm, "mid": v(7.8, 2.17) * mm, "end": v(7.8, 2.13) * mm});
            skLineSegment(sketch, "E2402", {"start": v(7.8, 2.13) * mm, "end": v(7.8, 1.67) * mm});
            skArc(sketch, "E2403", {"start": v(7.8, 1.67) * mm, "mid": v(7.8, 1.64) * mm, "end": v(7.84, 1.62) * mm});
            skLineSegment(sketch, "E2404", {"start": v(7.84, 1.62) * mm, "end": v(8.24, 1.62) * mm});
            skArc(sketch, "E2405", {"start": v(8.24, 1.62) * mm, "mid": v(8.27, 1.64) * mm, "end": v(8.28, 1.67) * mm});
            skLineSegment(sketch, "E2406", {"start": v(8.3, -1.77) * mm, "end": v(8.3, -2.23) * mm});
            skArc(sketch, "E2407", {"start": v(8.3, -2.23) * mm, "mid": v(8.3, -2.26) * mm, "end": v(8.34, -2.28) * mm});
            skLineSegment(sketch, "E2408", {"start": v(8.34, -2.28) * mm, "end": v(8.74, -2.28) * mm});
            skArc(sketch, "E2409", {"start": v(8.74, -2.28) * mm, "mid": v(8.77, -2.26) * mm, "end": v(8.78, -2.23) * mm});
            skLineSegment(sketch, "E2410", {"start": v(8.78, -2.23) * mm, "end": v(8.78, -1.77) * mm});
            skArc(sketch, "E2411", {"start": v(8.78, -1.77) * mm, "mid": v(8.77, -1.73) * mm, "end": v(8.74, -1.72) * mm});
            skLineSegment(sketch, "E2412", {"start": v(8.74, -1.72) * mm, "end": v(8.34, -1.72) * mm});
            skArc(sketch, "E2413", {"start": v(8.34, -1.72) * mm, "mid": v(8.3, -1.73) * mm, "end": v(8.3, -1.77) * mm});
            skLineSegment(sketch, "E2414", {"start": v(7.42, -1.77) * mm, "end": v(7.42, -2.23) * mm});
            skArc(sketch, "E2415", {"start": v(7.42, -2.23) * mm, "mid": v(7.43, -2.26) * mm, "end": v(7.46, -2.28) * mm});
            skLineSegment(sketch, "E2416", {"start": v(7.46, -2.28) * mm, "end": v(7.86, -2.28) * mm});
            skArc(sketch, "E2417", {"start": v(7.86, -2.28) * mm, "mid": v(7.9, -2.26) * mm, "end": v(7.9, -2.23) * mm});
            skLineSegment(sketch, "E2418", {"start": v(7.9, -2.23) * mm, "end": v(7.9, -1.77) * mm});
            skArc(sketch, "E2419", {"start": v(7.9, -1.77) * mm, "mid": v(7.9, -1.73) * mm, "end": v(7.86, -1.72) * mm});
            skLineSegment(sketch, "E2420", {"start": v(7.86, -1.72) * mm, "end": v(7.46, -1.72) * mm});
            skArc(sketch, "E2421", {"start": v(7.46, -1.72) * mm, "mid": v(7.43, -1.73) * mm, "end": v(7.42, -1.77) * mm});
            skLineSegment(sketch, "E2422", {"start": v(3.7, 4.87) * mm, "end": v(3.7, 5.33) * mm});
            skArc(sketch, "E2423", {"start": v(3.7, 5.33) * mm, "mid": v(3.7, 5.36) * mm, "end": v(3.66, 5.38) * mm});
            skLineSegment(sketch, "E2424", {"start": v(3.66, 5.38) * mm, "end": v(3.26, 5.38) * mm});
            skArc(sketch, "E2425", {"start": v(3.26, 5.38) * mm, "mid": v(3.23, 5.36) * mm, "end": v(3.22, 5.33) * mm});
            skLineSegment(sketch, "E2426", {"start": v(3.22, 5.33) * mm, "end": v(3.22, 4.87) * mm});
            skArc(sketch, "E2427", {"start": v(3.22, 4.87) * mm, "mid": v(3.23, 4.83) * mm, "end": v(3.26, 4.82) * mm});
            skLineSegment(sketch, "E2428", {"start": v(3.26, 4.82) * mm, "end": v(3.66, 4.82) * mm});
            skArc(sketch, "E2429", {"start": v(3.66, 4.82) * mm, "mid": v(3.7, 4.83) * mm, "end": v(3.7, 4.87) * mm});
            skLineSegment(sketch, "E2430", {"start": v(4.58, 4.87) * mm, "end": v(4.58, 5.33) * mm});
            skArc(sketch, "E2431", {"start": v(4.58, 5.33) * mm, "mid": v(4.57, 5.36) * mm, "end": v(4.54, 5.38) * mm});
            skLineSegment(sketch, "E2432", {"start": v(4.54, 5.38) * mm, "end": v(4.14, 5.38) * mm});
            skArc(sketch, "E2433", {"start": v(4.14, 5.38) * mm, "mid": v(4.1, 5.36) * mm, "end": v(4.1, 5.33) * mm});
            skLineSegment(sketch, "E2434", {"start": v(4.1, 5.33) * mm, "end": v(4.1, 4.87) * mm});
            skArc(sketch, "E2435", {"start": v(4.1, 4.87) * mm, "mid": v(4.1, 4.83) * mm, "end": v(4.14, 4.82) * mm});
            skLineSegment(sketch, "E2436", {"start": v(4.14, 4.82) * mm, "end": v(4.54, 4.82) * mm});
            skArc(sketch, "E2437", {"start": v(4.54, 4.82) * mm, "mid": v(4.57, 4.83) * mm, "end": v(4.58, 4.87) * mm});
            skLineSegment(sketch, "E2438", {"start": v(8.3, -4.17) * mm, "end": v(8.3, -4.63) * mm});
            skArc(sketch, "E2439", {"start": v(8.3, -4.63) * mm, "mid": v(8.3, -4.66) * mm, "end": v(8.34, -4.68) * mm});
            skLineSegment(sketch, "E2440", {"start": v(8.34, -4.68) * mm, "end": v(8.74, -4.68) * mm});
            skArc(sketch, "E2441", {"start": v(8.74, -4.68) * mm, "mid": v(8.77, -4.66) * mm, "end": v(8.78, -4.63) * mm});
            skLineSegment(sketch, "E2442", {"start": v(8.78, -4.63) * mm, "end": v(8.78, -4.17) * mm});
            skArc(sketch, "E2443", {"start": v(8.78, -4.17) * mm, "mid": v(8.77, -4.13) * mm, "end": v(8.74, -4.12) * mm});
            skLineSegment(sketch, "E2444", {"start": v(8.74, -4.12) * mm, "end": v(8.34, -4.12) * mm});
            skArc(sketch, "E2445", {"start": v(8.34, -4.12) * mm, "mid": v(8.3, -4.13) * mm, "end": v(8.3, -4.17) * mm});
            skLineSegment(sketch, "E2446", {"start": v(7.42, -4.17) * mm, "end": v(7.42, -4.63) * mm});
            skArc(sketch, "E2447", {"start": v(7.42, -4.63) * mm, "mid": v(7.43, -4.66) * mm, "end": v(7.46, -4.68) * mm});
            skLineSegment(sketch, "E2448", {"start": v(7.46, -4.68) * mm, "end": v(7.86, -4.68) * mm});
            skArc(sketch, "E2449", {"start": v(7.86, -4.68) * mm, "mid": v(7.9, -4.66) * mm, "end": v(7.9, -4.63) * mm});
            skLineSegment(sketch, "E2450", {"start": v(7.9, -4.63) * mm, "end": v(7.9, -4.17) * mm});
            skArc(sketch, "E2451", {"start": v(7.9, -4.17) * mm, "mid": v(7.9, -4.13) * mm, "end": v(7.86, -4.12) * mm});
            skLineSegment(sketch, "E2452", {"start": v(7.86, -4.12) * mm, "end": v(7.46, -4.12) * mm});
            skArc(sketch, "E2453", {"start": v(7.46, -4.12) * mm, "mid": v(7.43, -4.13) * mm, "end": v(7.42, -4.17) * mm});
            skLineSegment(sketch, "E2454", {"start": v(-20.4, 1.89) * mm, "end": v(-16.97, 0.79) * mm});
            skArc(sketch, "E2455", {"start": v(-17.01, 0.67) * mm, "mid": v(-16.85, 0.75) * mm, "end": v(-16.93, 0.9) * mm});
            skArc(sketch, "E2456", {"start": v(-20.36, 2) * mm, "mid": v(-20.52, 1.93) * mm, "end": v(-20.44, 1.77) * mm});
            skLineSegment(sketch, "E2457", {"start": v(-16.97, 0.79) * mm, "end": v(-16.75, 0.75) * mm});
            skArc(sketch, "E2458", {"start": v(-16.77, 0.63) * mm, "mid": v(-16.63, 0.73) * mm, "end": v(-16.73, 0.87) * mm});
            skArc(sketch, "E2459", {"start": v(-16.95, 0.9) * mm, "mid": v(-17.1, 0.8) * mm, "end": v(-17, 0.66) * mm});
            skLineSegment(sketch, "E2460", {"start": v(-16.75, 0.75) * mm, "end": v(-16.53, 0.74) * mm});
            skArc(sketch, "E2461", {"start": v(-16.53, 0.61) * mm, "mid": v(-16.4, 0.73) * mm, "end": v(-16.52, 0.86) * mm});
            skArc(sketch, "E2462", {"start": v(-16.74, 0.88) * mm, "mid": v(-16.87, 0.76) * mm, "end": v(-16.76, 0.63) * mm});
            skLineSegment(sketch, "E2463", {"start": v(-16.53, 0.74) * mm, "end": v(-16.3, 0.75) * mm});
            skArc(sketch, "E2464", {"start": v(-16.3, 0.62) * mm, "mid": v(-16.18, 0.75) * mm, "end": v(-16.31, 0.87) * mm});
            skArc(sketch, "E2465", {"start": v(-16.53, 0.86) * mm, "mid": v(-16.65, 0.73) * mm, "end": v(-16.52, 0.61) * mm});
            skLineSegment(sketch, "E2466", {"start": v(-16.3, 0.75) * mm, "end": v(-16.1, 0.78) * mm});
            skArc(sketch, "E2467", {"start": v(-16.07, 0.65) * mm, "mid": v(-15.97, 0.8) * mm, "end": v(-16.1, 0.9) * mm});
            skArc(sketch, "E2468", {"start": v(-16.32, 0.87) * mm, "mid": v(-16.43, 0.73) * mm, "end": v(-16.3, 0.62) * mm});
            skLineSegment(sketch, "E2469", {"start": v(-16.1, 0.78) * mm, "end": v(-15.88, 0.83) * mm});
            skArc(sketch, "E2470", {"start": v(-15.85, 0.7) * mm, "mid": v(-15.76, 0.86) * mm, "end": v(-15.91, 0.95) * mm});
            skArc(sketch, "E2471", {"start": v(-16.12, 0.9) * mm, "mid": v(-16.21, 0.75) * mm, "end": v(-16.06, 0.66) * mm});
            skLineSegment(sketch, "E2472", {"start": v(-15.88, 0.83) * mm, "end": v(-15.68, 0.9) * mm});
            skArc(sketch, "E2473", {"start": v(-15.64, 0.78) * mm, "mid": v(-15.56, 0.94) * mm, "end": v(-15.72, 1.02) * mm});
            skArc(sketch, "E2474", {"start": v(-15.92, 0.95) * mm, "mid": v(-16, 0.79) * mm, "end": v(-15.84, 0.71) * mm});
            skLineSegment(sketch, "E2475", {"start": v(-15.68, 0.9) * mm, "end": v(-15.48, 0.99) * mm});
            skArc(sketch, "E2476", {"start": v(-15.43, 0.88) * mm, "mid": v(-15.37, 1.04) * mm, "end": v(-15.53, 1.1) * mm});
            skArc(sketch, "E2477", {"start": v(-15.73, 1.01) * mm, "mid": v(-15.79, 0.85) * mm, "end": v(-15.62, 0.79) * mm});
            skLineSegment(sketch, "E2478", {"start": v(-15.48, 0.99) * mm, "end": v(-15.3, 1.1) * mm});
            skArc(sketch, "E2479", {"start": v(-15.23, 0.99) * mm, "mid": v(-15.18, 1.16) * mm, "end": v(-15.36, 1.2) * mm});
            skArc(sketch, "E2480", {"start": v(-15.54, 1.1) * mm, "mid": v(-15.59, 0.93) * mm, "end": v(-15.42, 0.88) * mm});
            skLineSegment(sketch, "E2481", {"start": v(-15.3, 1.1) * mm, "end": v(-15.12, 1.22) * mm});
            skArc(sketch, "E2482", {"start": v(-15.04, 1.12) * mm, "mid": v(-15.01, 1.3) * mm, "end": v(-15.19, 1.33) * mm});
            skArc(sketch, "E2483", {"start": v(-15.37, 1.2) * mm, "mid": v(-15.4, 1.02) * mm, "end": v(-15.22, 1) * mm});
            skLineSegment(sketch, "E2484", {"start": v(-15.12, 1.22) * mm, "end": v(-14.95, 1.37) * mm});
            skArc(sketch, "E2485", {"start": v(-14.87, 1.27) * mm, "mid": v(-14.86, 1.45) * mm, "end": v(-15.03, 1.46) * mm});
            skArc(sketch, "E2486", {"start": v(-15.2, 1.32) * mm, "mid": v(-15.21, 1.14) * mm, "end": v(-15.03, 1.13) * mm});
            skLineSegment(sketch, "E2487", {"start": v(-14.95, 1.37) * mm, "end": v(-14.8, 1.52) * mm});
            skArc(sketch, "E2488", {"start": v(-14.71, 1.44) * mm, "mid": v(-14.72, 1.62) * mm, "end": v(-14.9, 1.61) * mm});
            skArc(sketch, "E2489", {"start": v(-15.04, 1.45) * mm, "mid": v(-15.04, 1.27) * mm, "end": v(-14.86, 1.28) * mm});
            skLineSegment(sketch, "E2490", {"start": v(-14.8, 1.52) * mm, "end": v(-14.67, 1.7) * mm});
            skArc(sketch, "E2491", {"start": v(-14.57, 1.62) * mm, "mid": v(-14.6, 1.8) * mm, "end": v(-14.77, 1.77) * mm});
            skArc(sketch, "E2492", {"start": v(-14.9, 1.6) * mm, "mid": v(-14.88, 1.43) * mm, "end": v(-14.7, 1.45) * mm});
            skLineSegment(sketch, "E2493", {"start": v(-14.67, 1.7) * mm, "end": v(-14.55, 1.89) * mm});
            skArc(sketch, "E2494", {"start": v(-14.44, 1.82) * mm, "mid": v(-14.48, 2) * mm, "end": v(-14.66, 1.95) * mm});
            skArc(sketch, "E2495", {"start": v(-14.77, 1.76) * mm, "mid": v(-14.73, 1.6) * mm, "end": v(-14.56, 1.63) * mm});
            skLineSegment(sketch, "E2496", {"start": v(-14.55, 1.89) * mm, "end": v(-14.45, 2.09) * mm});
            skArc(sketch, "E2497", {"start": v(-14.34, 2.03) * mm, "mid": v(-14.4, 2.2) * mm, "end": v(-14.56, 2.15) * mm});
            skArc(sketch, "E2498", {"start": v(-14.66, 1.94) * mm, "mid": v(-14.6, 1.77) * mm, "end": v(-14.44, 1.83) * mm});
            skLineSegment(sketch, "E2499", {"start": v(-14.45, 2.09) * mm, "end": v(-14.37, 2.3) * mm});
            skArc(sketch, "E2500", {"start": v(-14.26, 2.25) * mm, "mid": v(-14.33, 2.4) * mm, "end": v(-14.49, 2.34) * mm});
            skArc(sketch, "E2501", {"start": v(-14.57, 2.13) * mm, "mid": v(-14.5, 1.97) * mm, "end": v(-14.33, 2.05) * mm});
            skLineSegment(sketch, "E2502", {"start": v(-14.37, 2.3) * mm, "end": v(-14.3, 2.53) * mm});
            skArc(sketch, "E2503", {"start": v(-14.19, 2.5) * mm, "mid": v(-14.28, 2.65) * mm, "end": v(-14.43, 2.56) * mm});
            skArc(sketch, "E2504", {"start": v(-14.5, 2.33) * mm, "mid": v(-14.4, 2.17) * mm, "end": v(-14.25, 2.26) * mm});
            skLineSegment(sketch, "E2505", {"start": v(-14.3, 2.53) * mm, "end": v(-14.27, 2.75) * mm});
            skArc(sketch, "E2506", {"start": v(-14.15, 2.73) * mm, "mid": v(-14.25, 2.88) * mm, "end": v(-14.4, 2.77) * mm});
            skArc(sketch, "E2507", {"start": v(-14.43, 2.55) * mm, "mid": v(-14.33, 2.4) * mm, "end": v(-14.19, 2.5) * mm});
            skLineSegment(sketch, "E2508", {"start": v(-14.27, 2.75) * mm, "end": v(-14.26, 2.97) * mm});
            skArc(sketch, "E2509", {"start": v(-14.14, 2.97) * mm, "mid": v(-14.25, 3.1) * mm, "end": v(-14.39, 2.98) * mm});
            skArc(sketch, "E2510", {"start": v(-14.4, 2.76) * mm, "mid": v(-14.28, 2.63) * mm, "end": v(-14.15, 2.74) * mm});
            skLineSegment(sketch, "E2511", {"start": v(-14.26, 2.97) * mm, "end": v(-14.27, 3.2) * mm});
            skArc(sketch, "E2512", {"start": v(-14.15, 3.2) * mm, "mid": v(-14.28, 3.32) * mm, "end": v(-14.4, 3.19) * mm});
            skArc(sketch, "E2513", {"start": v(-14.39, 2.97) * mm, "mid": v(-14.26, 2.85) * mm, "end": v(-14.14, 2.98) * mm});
            skLineSegment(sketch, "E2514", {"start": v(-14.27, 3.2) * mm, "end": v(-14.3, 3.4) * mm});
            skArc(sketch, "E2515", {"start": v(-14.18, 3.43) * mm, "mid": v(-14.32, 3.53) * mm, "end": v(-14.42, 3.4) * mm});
            skArc(sketch, "E2516", {"start": v(-14.4, 3.18) * mm, "mid": v(-14.25, 3.07) * mm, "end": v(-14.15, 3.21) * mm});
            skLineSegment(sketch, "E2517", {"start": v(-14.3, 3.4) * mm, "end": v(-14.35, 3.62) * mm});
            skArc(sketch, "E2518", {"start": v(-14.23, 3.65) * mm, "mid": v(-14.38, 3.74) * mm, "end": v(-14.47, 3.6) * mm});
            skArc(sketch, "E2519", {"start": v(-14.42, 3.38) * mm, "mid": v(-14.27, 3.29) * mm, "end": v(-14.18, 3.44) * mm});
            skLineSegment(sketch, "E2520", {"start": v(-14.35, 3.62) * mm, "end": v(-14.42, 3.82) * mm});
            skArc(sketch, "E2521", {"start": v(-14.3, 3.87) * mm, "mid": v(-14.46, 3.94) * mm, "end": v(-14.54, 3.78) * mm});
            skArc(sketch, "E2522", {"start": v(-14.47, 3.58) * mm, "mid": v(-14.31, 3.5) * mm, "end": v(-14.23, 3.66) * mm});
            skLineSegment(sketch, "E2523", {"start": v(-14.42, 3.82) * mm, "end": v(-14.51, 4.02) * mm});
            skArc(sketch, "E2524", {"start": v(-14.4, 4.07) * mm, "mid": v(-14.56, 4.13) * mm, "end": v(-14.63, 3.97) * mm});
            skArc(sketch, "E2525", {"start": v(-14.54, 3.77) * mm, "mid": v(-14.37, 3.71) * mm, "end": v(-14.3, 3.88) * mm});
            skLineSegment(sketch, "E2526", {"start": v(-14.51, 4.02) * mm, "end": v(-14.62, 4.2) * mm});
            skArc(sketch, "E2527", {"start": v(-14.51, 4.27) * mm, "mid": v(-14.68, 4.32) * mm, "end": v(-14.73, 4.15) * mm});
            skArc(sketch, "E2528", {"start": v(-14.62, 3.96) * mm, "mid": v(-14.45, 3.91) * mm, "end": v(-14.4, 4.08) * mm});
            skLineSegment(sketch, "E2529", {"start": v(-14.62, 4.2) * mm, "end": v(-14.75, 4.38) * mm});
            skArc(sketch, "E2530", {"start": v(-14.64, 4.46) * mm, "mid": v(-14.82, 4.49) * mm, "end": v(-14.85, 4.31) * mm});
            skArc(sketch, "E2531", {"start": v(-14.72, 4.14) * mm, "mid": v(-14.55, 4.1) * mm, "end": v(-14.52, 4.28) * mm});
            skLineSegment(sketch, "E2532", {"start": v(-14.75, 4.38) * mm, "end": v(-14.89, 4.55) * mm});
            skArc(sketch, "E2533", {"start": v(-14.8, 4.63) * mm, "mid": v(-14.97, 4.64) * mm, "end": v(-14.98, 4.47) * mm});
            skArc(sketch, "E2534", {"start": v(-14.84, 4.3) * mm, "mid": v(-14.66, 4.29) * mm, "end": v(-14.65, 4.47) * mm});
            skLineSegment(sketch, "E2535", {"start": v(-14.89, 4.55) * mm, "end": v(-15.05, 4.7) * mm});
            skArc(sketch, "E2536", {"start": v(-14.96, 4.79) * mm, "mid": v(-15.14, 4.78) * mm, "end": v(-15.13, 4.6) * mm});
            skArc(sketch, "E2537", {"start": v(-14.97, 4.46) * mm, "mid": v(-14.8, 4.46) * mm, "end": v(-14.8, 4.64) * mm});
            skLineSegment(sketch, "E2538", {"start": v(-15.05, 4.7) * mm, "end": v(-15.22, 4.83) * mm});
            skArc(sketch, "E2539", {"start": v(-15.14, 4.93) * mm, "mid": v(-15.32, 4.9) * mm, "end": v(-15.3, 4.73) * mm});
            skArc(sketch, "E2540", {"start": v(-15.12, 4.6) * mm, "mid": v(-14.95, 4.62) * mm, "end": v(-14.97, 4.8) * mm});
            skLineSegment(sketch, "E2541", {"start": v(-15.22, 4.83) * mm, "end": v(-15.41, 4.95) * mm});
            skArc(sketch, "E2542", {"start": v(-15.34, 5.06) * mm, "mid": v(-15.52, 5.02) * mm, "end": v(-15.48, 4.85) * mm});
            skArc(sketch, "E2543", {"start": v(-15.29, 4.73) * mm, "mid": v(-15.12, 4.77) * mm, "end": v(-15.16, 4.94) * mm});
            skLineSegment(sketch, "E2544", {"start": v(-15.41, 4.95) * mm, "end": v(-15.61, 5.05) * mm});
            skArc(sketch, "E2545", {"start": v(-15.56, 5.16) * mm, "mid": v(-15.72, 5.1) * mm, "end": v(-15.67, 4.94) * mm});
            skArc(sketch, "E2546", {"start": v(-15.47, 4.84) * mm, "mid": v(-15.3, 4.9) * mm, "end": v(-15.35, 5.06) * mm});
            skLineSegment(sketch, "E2547", {"start": v(-15.61, 5.05) * mm, "end": v(-15.84, 5.14) * mm});
            skArc(sketch, "E2548", {"start": v(-15.8, 5.26) * mm, "mid": v(-15.96, 5.18) * mm, "end": v(-15.89, 5.02) * mm});
            skArc(sketch, "E2549", {"start": v(-15.66, 4.93) * mm, "mid": v(-15.5, 5) * mm, "end": v(-15.57, 5.17) * mm});
            skLineSegment(sketch, "E2550", {"start": v(-15.84, 5.14) * mm, "end": v(-19.01, 6.17) * mm});
            skArc(sketch, "E2551", {"start": v(-18.97, 6.29) * mm, "mid": v(-19.13, 6.2) * mm, "end": v(-19.05, 6.05) * mm});
            skArc(sketch, "E2552", {"start": v(-15.88, 5.02) * mm, "mid": v(-15.73, 5.1) * mm, "end": v(-15.8, 5.26) * mm});
            skLineSegment(sketch, "E2553", {"start": v(-19.01, 6.17) * mm, "end": v(-21.34, 6.17) * mm});
            skArc(sketch, "E2554", {"start": v(-21.34, 6.3) * mm, "mid": v(-21.47, 6.17) * mm, "end": v(-21.34, 6.04) * mm});
            skArc(sketch, "E2555", {"start": v(-19.01, 6.04) * mm, "mid": v(-18.89, 6.17) * mm, "end": v(-19.01, 6.3) * mm});
            skLineSegment(sketch, "E2556", {"start": v(-21.34, 6.17) * mm, "end": v(-22.36, 5.9) * mm});
            skArc(sketch, "E2557", {"start": v(-22.4, 6.01) * mm, "mid": v(-22.48, 5.86) * mm, "end": v(-22.33, 5.77) * mm});
            skArc(sketch, "E2558", {"start": v(-21.3, 6.05) * mm, "mid": v(-21.22, 6.2) * mm, "end": v(-21.37, 6.29) * mm});
            skLineSegment(sketch, "E2559", {"start": v(-22.36, 5.9) * mm, "end": v(-22.95, 4.08) * mm});
            skArc(sketch, "E2560", {"start": v(-23.07, 4.12) * mm, "mid": v(-22.99, 3.96) * mm, "end": v(-22.83, 4.04) * mm});
            skArc(sketch, "E2561", {"start": v(-22.24, 5.85) * mm, "mid": v(-22.32, 6.01) * mm, "end": v(-22.48, 5.93) * mm});
            skLineSegment(sketch, "E2562", {"start": v(-22.95, 4.08) * mm, "end": v(-22.29, 3.26) * mm});
            skArc(sketch, "E2563", {"start": v(-22.38, 3.18) * mm, "mid": v(-22.2, 3.16) * mm, "end": v(-22.19, 3.34) * mm});
            skArc(sketch, "E2564", {"start": v(-22.85, 4.16) * mm, "mid": v(-23.03, 4.18) * mm, "end": v(-23.05, 4) * mm});
            skLineSegment(sketch, "E2565", {"start": v(-22.29, 3.26) * mm, "end": v(-20.4, 1.89) * mm});
            skArc(sketch, "E2566", {"start": v(-20.47, 1.79) * mm, "mid": v(-20.3, 1.81) * mm, "end": v(-20.33, 1.99) * mm});
            skArc(sketch, "E2567", {"start": v(-22.21, 3.36) * mm, "mid": v(-22.39, 3.33) * mm, "end": v(-22.36, 3.16) * mm});
            skLineSegment(sketch, "E2568", {"start": v(-14.93, 1.4) * mm, "end": v(-14.3, 3.35) * mm});
            skArc(sketch, "E2569", {"start": v(-14.17, 3.31) * mm, "mid": v(-14.25, 3.47) * mm, "end": v(-14.41, 3.39) * mm});
            skArc(sketch, "E2570", {"start": v(-15.05, 1.43) * mm, "mid": v(-14.97, 1.27) * mm, "end": v(-14.8, 1.35) * mm});
            skLineSegment(sketch, "E2571", {"start": v(-15.6, 0.93) * mm, "end": v(-14.57, 4.12) * mm});
            skArc(sketch, "E2572", {"start": v(-14.45, 4.08) * mm, "mid": v(-14.53, 4.24) * mm, "end": v(-14.69, 4.16) * mm});
            skArc(sketch, "E2573", {"start": v(-15.72, 0.97) * mm, "mid": v(-15.64, 0.81) * mm, "end": v(-15.48, 0.9) * mm});
            skLineSegment(sketch, "E2574", {"start": v(-16.18, 0.76) * mm, "end": v(-14.94, 4.6) * mm});
            skArc(sketch, "E2575", {"start": v(-14.82, 4.56) * mm, "mid": v(-14.9, 4.71) * mm, "end": v(-15.06, 4.63) * mm});
            skArc(sketch, "E2576", {"start": v(-16.3, 0.8) * mm, "mid": v(-16.22, 0.65) * mm, "end": v(-16.06, 0.73) * mm});
            skLineSegment(sketch, "E2577", {"start": v(-16.71, 0.75) * mm, "end": v(-15.36, 4.92) * mm});
            skArc(sketch, "E2578", {"start": v(-15.24, 4.88) * mm, "mid": v(-15.32, 5.04) * mm, "end": v(-15.48, 4.96) * mm});
            skArc(sketch, "E2579", {"start": v(-16.83, 0.79) * mm, "mid": v(-16.75, 0.63) * mm, "end": v(-16.6, 0.7) * mm});
            skLineSegment(sketch, "E2580", {"start": v(-17.2, 0.86) * mm, "end": v(-15.82, 5.13) * mm});
            skArc(sketch, "E2581", {"start": v(-15.7, 5.09) * mm, "mid": v(-15.78, 5.25) * mm, "end": v(-15.94, 5.17) * mm});
            skArc(sketch, "E2582", {"start": v(-17.32, 0.9) * mm, "mid": v(-17.24, 0.74) * mm, "end": v(-17.09, 0.82) * mm});
            skLineSegment(sketch, "E2583", {"start": v(-17.68, 1.01) * mm, "end": v(-16.3, 5.28) * mm});
            skArc(sketch, "E2584", {"start": v(-16.17, 5.25) * mm, "mid": v(-16.25, 5.4) * mm, "end": v(-16.41, 5.32) * mm});
            skArc(sketch, "E2585", {"start": v(-17.8, 1.05) * mm, "mid": v(-17.72, 0.9) * mm, "end": v(-17.56, 0.97) * mm});
            skLineSegment(sketch, "E2586", {"start": v(-18.16, 1.17) * mm, "end": v(-16.77, 5.44) * mm});
            skArc(sketch, "E2587", {"start": v(-16.65, 5.4) * mm, "mid": v(-16.73, 5.56) * mm, "end": v(-16.89, 5.48) * mm});
            skArc(sketch, "E2588", {"start": v(-18.27, 1.2) * mm, "mid": v(-18.2, 1.05) * mm, "end": v(-18.04, 1.13) * mm});
            skLineSegment(sketch, "E2589", {"start": v(-18.63, 1.32) * mm, "end": v(-17.24, 5.6) * mm});
            skArc(sketch, "E2590", {"start": v(-17.12, 5.55) * mm, "mid": v(-17.2, 5.71) * mm, "end": v(-17.36, 5.63) * mm});
            skArc(sketch, "E2591", {"start": v(-18.75, 1.36) * mm, "mid": v(-18.67, 1.2) * mm, "end": v(-18.51, 1.28) * mm});
            skLineSegment(sketch, "E2592", {"start": v(-19.1, 1.47) * mm, "end": v(-17.72, 5.75) * mm});
            skArc(sketch, "E2593", {"start": v(-17.6, 5.7) * mm, "mid": v(-17.68, 5.87) * mm, "end": v(-17.84, 5.79) * mm});
            skArc(sketch, "E2594", {"start": v(-19.23, 1.51) * mm, "mid": v(-19.15, 1.35) * mm, "end": v(-18.99, 1.43) * mm});
            skLineSegment(sketch, "E2595", {"start": v(-19.58, 1.63) * mm, "end": v(-18.2, 5.9) * mm});
            skArc(sketch, "E2596", {"start": v(-18.08, 5.86) * mm, "mid": v(-18.16, 6.02) * mm, "end": v(-18.31, 5.94) * mm});
            skArc(sketch, "E2597", {"start": v(-19.7, 1.66) * mm, "mid": v(-19.62, 1.5) * mm, "end": v(-19.47, 1.59) * mm});
            skLineSegment(sketch, "E2598", {"start": v(-20.06, 1.78) * mm, "end": v(-18.67, 6.06) * mm});
            skArc(sketch, "E2599", {"start": v(-18.55, 6.02) * mm, "mid": v(-18.63, 6.18) * mm, "end": v(-18.79, 6.1) * mm});
            skArc(sketch, "E2600", {"start": v(-20.18, 1.82) * mm, "mid": v(-20.1, 1.66) * mm, "end": v(-19.94, 1.74) * mm});
            skLineSegment(sketch, "E2601", {"start": v(-20.52, 1.98) * mm, "end": v(-19.16, 6.17) * mm});
            skArc(sketch, "E2602", {"start": v(-19.04, 6.13) * mm, "mid": v(-19.12, 6.29) * mm, "end": v(-19.28, 6.2) * mm});
            skArc(sketch, "E2603", {"start": v(-20.64, 2.01) * mm, "mid": v(-20.56, 1.86) * mm, "end": v(-20.4, 1.94) * mm});
            skLineSegment(sketch, "E2604", {"start": v(-20.95, 2.28) * mm, "end": v(-19.69, 6.17) * mm});
            skArc(sketch, "E2605", {"start": v(-19.57, 6.13) * mm, "mid": v(-19.65, 6.29) * mm, "end": v(-19.8, 6.2) * mm});
            skArc(sketch, "E2606", {"start": v(-21.07, 2.32) * mm, "mid": v(-20.99, 2.17) * mm, "end": v(-20.83, 2.25) * mm});
            skLineSegment(sketch, "E2607", {"start": v(-21.37, 2.6) * mm, "end": v(-20.21, 6.17) * mm});
            skArc(sketch, "E2608", {"start": v(-20.1, 6.13) * mm, "mid": v(-20.17, 6.29) * mm, "end": v(-20.33, 6.2) * mm});
            skArc(sketch, "E2609", {"start": v(-21.5, 2.63) * mm, "mid": v(-21.41, 2.48) * mm, "end": v(-21.25, 2.56) * mm});
            skLineSegment(sketch, "E2610", {"start": v(-21.8, 2.9) * mm, "end": v(-20.74, 6.17) * mm});
            skArc(sketch, "E2611", {"start": v(-20.62, 6.13) * mm, "mid": v(-20.7, 6.29) * mm, "end": v(-20.86, 6.2) * mm});
            skArc(sketch, "E2612", {"start": v(-21.92, 2.94) * mm, "mid": v(-21.84, 2.78) * mm, "end": v(-21.68, 2.86) * mm});
            skLineSegment(sketch, "E2613", {"start": v(-22.22, 3.21) * mm, "end": v(-21.26, 6.17) * mm});
            skArc(sketch, "E2614", {"start": v(-21.14, 6.13) * mm, "mid": v(-21.22, 6.29) * mm, "end": v(-21.38, 6.2) * mm});
            skArc(sketch, "E2615", {"start": v(-22.34, 3.25) * mm, "mid": v(-22.26, 3.1) * mm, "end": v(-22.1, 3.17) * mm});
            skLineSegment(sketch, "E2616", {"start": v(-22.6, 3.65) * mm, "end": v(-21.83, 6.04) * mm});
            skArc(sketch, "E2617", {"start": v(-21.71, 6) * mm, "mid": v(-21.8, 6.15) * mm, "end": v(-21.95, 6.07) * mm});
            skArc(sketch, "E2618", {"start": v(-22.72, 3.7) * mm, "mid": v(-22.64, 3.53) * mm, "end": v(-22.49, 3.61) * mm});
            skLineSegment(sketch, "E2619", {"start": v(-30, 4.81) * mm, "end": v(-29.88, 4.88) * mm});
            skArc(sketch, "E2620", {"start": v(-29.86, 4.83) * mm, "mid": v(-29.83, 4.9) * mm, "end": v(-29.9, 4.92) * mm});
            skArc(sketch, "E2621", {"start": v(-30.03, 4.86) * mm, "mid": v(-30.05, 4.79) * mm, "end": v(-29.98, 4.77) * mm});
            skLineSegment(sketch, "E2622", {"start": v(-29.88, 4.88) * mm, "end": v(-29.75, 4.97) * mm});
            skArc(sketch, "E2623", {"start": v(-29.72, 4.93) * mm, "mid": v(-29.71, 5) * mm, "end": v(-29.78, 5.01) * mm});
            skArc(sketch, "E2624", {"start": v(-29.9, 4.92) * mm, "mid": v(-29.92, 4.85) * mm, "end": v(-29.85, 4.84) * mm});
            skLineSegment(sketch, "E2625", {"start": v(-29.75, 4.97) * mm, "end": v(-29.65, 5.08) * mm});
            skArc(sketch, "E2626", {"start": v(-29.61, 5.05) * mm, "mid": v(-29.61, 5.12) * mm, "end": v(-29.68, 5.12) * mm});
            skArc(sketch, "E2627", {"start": v(-29.8, 5) * mm, "mid": v(-29.79, 4.93) * mm, "end": v(-29.72, 4.94) * mm});
            skLineSegment(sketch, "E2628", {"start": v(-29.65, 5.08) * mm, "end": v(-29.56, 5.22) * mm});
            skArc(sketch, "E2629", {"start": v(-29.52, 5.2) * mm, "mid": v(-29.53, 5.26) * mm, "end": v(-29.6, 5.24) * mm});
            skArc(sketch, "E2630", {"start": v(-29.69, 5.11) * mm, "mid": v(-29.68, 5.04) * mm, "end": v(-29.6, 5.06) * mm});
            skLineSegment(sketch, "E2631", {"start": v(-29.56, 5.22) * mm, "end": v(-29.53, 5.29) * mm});
            skArc(sketch, "E2632", {"start": v(-29.48, 5.27) * mm, "mid": v(-29.5, 5.34) * mm, "end": v(-29.57, 5.31) * mm});
            skArc(sketch, "E2633", {"start": v(-29.6, 5.24) * mm, "mid": v(-29.58, 5.17) * mm, "end": v(-29.52, 5.2) * mm});
            skLineSegment(sketch, "E2634", {"start": v(-29.53, 5.29) * mm, "end": v(-28.38, 8.86) * mm});
            skArc(sketch, "E2635", {"start": v(-28.33, 8.85) * mm, "mid": v(-28.36, 8.91) * mm, "end": v(-28.43, 8.88) * mm});
            skArc(sketch, "E2636", {"start": v(-29.57, 5.3) * mm, "mid": v(-29.54, 5.24) * mm, "end": v(-29.48, 5.27) * mm});
            skLineSegment(sketch, "E2637", {"start": v(-28.38, 8.86) * mm, "end": v(-28.37, 9.02) * mm});
            skArc(sketch, "E2638", {"start": v(-28.32, 9.02) * mm, "mid": v(-28.37, 9.07) * mm, "end": v(-28.42, 9.02) * mm});
            skArc(sketch, "E2639", {"start": v(-28.43, 8.87) * mm, "mid": v(-28.38, 8.81) * mm, "end": v(-28.33, 8.86) * mm});
            skLineSegment(sketch, "E2640", {"start": v(-28.37, 9.02) * mm, "end": v(-28.4, 9.18) * mm});
            skArc(sketch, "E2641", {"start": v(-28.34, 9.18) * mm, "mid": v(-28.4, 9.23) * mm, "end": v(-28.44, 9.17) * mm});
            skArc(sketch, "E2642", {"start": v(-28.42, 9.01) * mm, "mid": v(-28.37, 8.97) * mm, "end": v(-28.32, 9.03) * mm});
            skLineSegment(sketch, "E2643", {"start": v(-28.4, 9.18) * mm, "end": v(-28.44, 9.32) * mm});
            skArc(sketch, "E2644", {"start": v(-28.4, 9.34) * mm, "mid": v(-28.45, 9.37) * mm, "end": v(-28.49, 9.3) * mm});
            skArc(sketch, "E2645", {"start": v(-28.44, 9.16) * mm, "mid": v(-28.38, 9.13) * mm, "end": v(-28.35, 9.2) * mm});
            skLineSegment(sketch, "E2646", {"start": v(-28.44, 9.32) * mm, "end": v(-28.5, 9.44) * mm});
            skArc(sketch, "E2647", {"start": v(-28.45, 9.46) * mm, "mid": v(-28.52, 9.49) * mm, "end": v(-28.54, 9.42) * mm});
            skArc(sketch, "E2648", {"start": v(-28.48, 9.3) * mm, "mid": v(-28.42, 9.28) * mm, "end": v(-28.4, 9.35) * mm});
            skLineSegment(sketch, "E2649", {"start": v(-28.5, 9.44) * mm, "end": v(-28.62, 9.38) * mm});
            skArc(sketch, "E2650", {"start": v(-28.65, 9.42) * mm, "mid": v(-28.67, 9.35) * mm, "end": v(-28.6, 9.33) * mm});
            skArc(sketch, "E2651", {"start": v(-28.48, 9.4) * mm, "mid": v(-28.45, 9.46) * mm, "end": v(-28.52, 9.49) * mm});
            skLineSegment(sketch, "E2652", {"start": v(-28.62, 9.38) * mm, "end": v(-28.75, 9.28) * mm});
            skArc(sketch, "E2653", {"start": v(-28.78, 9.32) * mm, "mid": v(-28.79, 9.25) * mm, "end": v(-28.72, 9.24) * mm});
            skArc(sketch, "E2654", {"start": v(-28.6, 9.34) * mm, "mid": v(-28.58, 9.4) * mm, "end": v(-28.65, 9.42) * mm});
            skLineSegment(sketch, "E2655", {"start": v(-28.75, 9.28) * mm, "end": v(-28.86, 9.17) * mm});
            skArc(sketch, "E2656", {"start": v(-28.9, 9.2) * mm, "mid": v(-28.89, 9.13) * mm, "end": v(-28.82, 9.13) * mm});
            skArc(sketch, "E2657", {"start": v(-28.71, 9.25) * mm, "mid": v(-28.71, 9.32) * mm, "end": v(-28.79, 9.32) * mm});
            skLineSegment(sketch, "E2658", {"start": v(-28.86, 9.17) * mm, "end": v(-28.94, 9.04) * mm});
            skArc(sketch, "E2659", {"start": v(-28.98, 9.06) * mm, "mid": v(-28.97, 9) * mm, "end": v(-28.9, 9) * mm});
            skArc(sketch, "E2660", {"start": v(-28.81, 9.14) * mm, "mid": v(-28.83, 9.21) * mm, "end": v(-28.9, 9.2) * mm});
            skLineSegment(sketch, "E2661", {"start": v(-28.94, 9.04) * mm, "end": v(-28.98, 8.96) * mm});
            skArc(sketch, "E2662", {"start": v(-29.02, 8.99) * mm, "mid": v(-29, 8.92) * mm, "end": v(-28.93, 8.94) * mm});
            skArc(sketch, "E2663", {"start": v(-28.9, 9.01) * mm, "mid": v(-28.92, 9.08) * mm, "end": v(-28.99, 9.06) * mm});
            skLineSegment(sketch, "E2664", {"start": v(-28.98, 8.96) * mm, "end": v(-30.12, 5.39) * mm});
            skArc(sketch, "E2665", {"start": v(-30.17, 5.4) * mm, "mid": v(-30.14, 5.34) * mm, "end": v(-30.08, 5.37) * mm});
            skArc(sketch, "E2666", {"start": v(-28.93, 8.95) * mm, "mid": v(-28.96, 9.01) * mm, "end": v(-29.02, 8.98) * mm});
            skLineSegment(sketch, "E2667", {"start": v(-30.12, 5.39) * mm, "end": v(-30.13, 5.23) * mm});
            skArc(sketch, "E2668", {"start": v(-30.18, 5.23) * mm, "mid": v(-30.13, 5.18) * mm, "end": v(-30.08, 5.23) * mm});
            skArc(sketch, "E2669", {"start": v(-30.07, 5.39) * mm, "mid": v(-30.12, 5.44) * mm, "end": v(-30.17, 5.4) * mm});
            skLineSegment(sketch, "E2670", {"start": v(-30.13, 5.23) * mm, "end": v(-30.11, 5.08) * mm});
            skArc(sketch, "E2671", {"start": v(-30.16, 5.07) * mm, "mid": v(-30.1, 5.03) * mm, "end": v(-30.06, 5.08) * mm});
            skArc(sketch, "E2672", {"start": v(-30.08, 5.24) * mm, "mid": v(-30.14, 5.28) * mm, "end": v(-30.18, 5.23) * mm});
            skLineSegment(sketch, "E2673", {"start": v(-30.11, 5.08) * mm, "end": v(-30.06, 4.93) * mm});
            skArc(sketch, "E2674", {"start": v(-30.11, 4.92) * mm, "mid": v(-30.05, 4.88) * mm, "end": v(-30.02, 4.95) * mm});
            skArc(sketch, "E2675", {"start": v(-30.06, 5.1) * mm, "mid": v(-30.13, 5.13) * mm, "end": v(-30.16, 5.06) * mm});
            skLineSegment(sketch, "E2676", {"start": v(-30.06, 4.93) * mm, "end": v(-30, 4.81) * mm});
            skArc(sketch, "E2677", {"start": v(-30.05, 4.8) * mm, "mid": v(-29.98, 4.77) * mm, "end": v(-29.96, 4.84) * mm});
            skArc(sketch, "E2678", {"start": v(-30.02, 4.95) * mm, "mid": v(-30.09, 4.97) * mm, "end": v(-30.1, 4.9) * mm});
            skLineSegment(sketch, "E2679", {"start": v(-29.74, 4.98) * mm, "end": v(-28.39, 9.15) * mm});
            skArc(sketch, "E2680", {"start": v(-28.34, 9.14) * mm, "mid": v(-28.37, 9.2) * mm, "end": v(-28.44, 9.17) * mm});
            skArc(sketch, "E2681", {"start": v(-29.8, 5) * mm, "mid": v(-29.76, 4.93) * mm, "end": v(-29.7, 4.97) * mm});
            skLineSegment(sketch, "E2682", {"start": v(-30, 4.82) * mm, "end": v(-28.5, 9.44) * mm});
            skArc(sketch, "E2683", {"start": v(-28.46, 9.42) * mm, "mid": v(-28.5, 9.48) * mm, "end": v(-28.55, 9.45) * mm});
            skArc(sketch, "E2684", {"start": v(-30.05, 4.83) * mm, "mid": v(-30.02, 4.77) * mm, "end": v(-29.96, 4.8) * mm});
            skLineSegment(sketch, "E2685", {"start": v(-30.12, 5.13) * mm, "end": v(-28.78, 9.25) * mm});
            skArc(sketch, "E2686", {"start": v(-28.73, 9.24) * mm, "mid": v(-28.76, 9.3) * mm, "end": v(-28.82, 9.27) * mm});
            skArc(sketch, "E2687", {"start": v(-30.16, 5.14) * mm, "mid": v(-30.13, 5.08) * mm, "end": v(-30.07, 5.11) * mm});
            skCircle(sketch, "E2688", {"center": v(-16.51, 2.99) * mm, "radius": 1.7 * mm});
            skArc(sketch, "E2689", {"start": v(-16.51, 2.11) * mm, "mid": v(-15.64, 2.99) * mm, "end": v(-16.51, 3.86) * mm});
            skArc(sketch, "E2690", {"start": v(-16.51, 3.86) * mm, "mid": v(-17.39, 2.99) * mm, "end": v(-16.51, 2.11) * mm});
            skCircle(sketch, "E2691", {"center": v(-26.02, 6.08) * mm, "radius": 1.7 * mm});
            skArc(sketch, "E2692", {"start": v(-26.02, 5.2) * mm, "mid": v(-25.15, 6.08) * mm, "end": v(-26.02, 6.95) * mm});
            skArc(sketch, "E2693", {"start": v(-26.02, 6.95) * mm, "mid": v(-26.9, 6.08) * mm, "end": v(-26.02, 5.2) * mm});
            skLineSegment(sketch, "E2694", {"start": v(-10.35, -20.46) * mm, "end": v(-8.24, -17.54) * mm});
            skArc(sketch, "E2695", {"start": v(-8.14, -17.62) * mm, "mid": v(-8.17, -17.44) * mm, "end": v(-8.34, -17.47) * mm});
            skArc(sketch, "E2696", {"start": v(-10.45, -20.39) * mm, "mid": v(-10.42, -20.56) * mm, "end": v(-10.25, -20.54) * mm});
            skLineSegment(sketch, "E2697", {"start": v(-8.24, -17.54) * mm, "end": v(-8.14, -17.34) * mm});
            skArc(sketch, "E2698", {"start": v(-8.03, -17.4) * mm, "mid": v(-8.08, -17.23) * mm, "end": v(-8.25, -17.28) * mm});
            skArc(sketch, "E2699", {"start": v(-8.35, -17.49) * mm, "mid": v(-8.3, -17.65) * mm, "end": v(-8.13, -17.6) * mm});
            skLineSegment(sketch, "E2700", {"start": v(-8.14, -17.34) * mm, "end": v(-8.06, -17.13) * mm});
            skArc(sketch, "E2701", {"start": v(-7.94, -17.18) * mm, "mid": v(-8.01, -17.02) * mm, "end": v(-8.18, -17.09) * mm});
            skArc(sketch, "E2702", {"start": v(-8.26, -17.3) * mm, "mid": v(-8.19, -17.46) * mm, "end": v(-8.02, -17.39) * mm});
            skLineSegment(sketch, "E2703", {"start": v(-8.06, -17.13) * mm, "end": v(-8, -16.92) * mm});
            skArc(sketch, "E2704", {"start": v(-7.88, -16.96) * mm, "mid": v(-7.97, -16.8) * mm, "end": v(-8.12, -16.89) * mm});
            skArc(sketch, "E2705", {"start": v(-8.18, -17.1) * mm, "mid": v(-8.1, -17.25) * mm, "end": v(-7.94, -17.17) * mm});
            skLineSegment(sketch, "E2706", {"start": v(-8, -16.92) * mm, "end": v(-7.96, -16.7) * mm});
            skArc(sketch, "E2707", {"start": v(-7.84, -16.73) * mm, "mid": v(-7.94, -16.58) * mm, "end": v(-8.09, -16.69) * mm});
            skArc(sketch, "E2708", {"start": v(-8.12, -16.9) * mm, "mid": v(-8.02, -17.05) * mm, "end": v(-7.88, -16.94) * mm});
            skLineSegment(sketch, "E2709", {"start": v(-7.96, -16.7) * mm, "end": v(-7.95, -16.5) * mm});
            skArc(sketch, "E2710", {"start": v(-7.82, -16.5) * mm, "mid": v(-7.94, -16.37) * mm, "end": v(-8.07, -16.48) * mm});
            skArc(sketch, "E2711", {"start": v(-8.09, -16.7) * mm, "mid": v(-7.97, -16.83) * mm, "end": v(-7.84, -16.72) * mm});
            skLineSegment(sketch, "E2712", {"start": v(-7.95, -16.5) * mm, "end": v(-7.95, -16.27) * mm});
            skArc(sketch, "E2713", {"start": v(-7.82, -16.27) * mm, "mid": v(-7.95, -16.15) * mm, "end": v(-8.07, -16.28) * mm});
            skArc(sketch, "E2714", {"start": v(-8.07, -16.5) * mm, "mid": v(-7.94, -16.62) * mm, "end": v(-7.82, -16.49) * mm});
            skLineSegment(sketch, "E2715", {"start": v(-7.95, -16.27) * mm, "end": v(-7.97, -16.06) * mm});
            skArc(sketch, "E2716", {"start": v(-7.85, -16.05) * mm, "mid": v(-7.99, -15.94) * mm, "end": v(-8.1, -16.07) * mm});
            skArc(sketch, "E2717", {"start": v(-8.07, -16.29) * mm, "mid": v(-7.94, -16.4) * mm, "end": v(-7.83, -16.26) * mm});
            skLineSegment(sketch, "E2718", {"start": v(-7.97, -16.06) * mm, "end": v(-8.02, -15.85) * mm});
            skArc(sketch, "E2719", {"start": v(-7.9, -15.82) * mm, "mid": v(-8.05, -15.73) * mm, "end": v(-8.14, -15.87) * mm});
            skArc(sketch, "E2720", {"start": v(-8.1, -16.09) * mm, "mid": v(-7.95, -16.18) * mm, "end": v(-7.85, -16.03) * mm});
            skLineSegment(sketch, "E2721", {"start": v(-8.02, -15.85) * mm, "end": v(-8.08, -15.64) * mm});
            skArc(sketch, "E2722", {"start": v(-7.97, -15.6) * mm, "mid": v(-8.12, -15.52) * mm, "end": v(-8.2, -15.68) * mm});
            skArc(sketch, "E2723", {"start": v(-8.14, -15.89) * mm, "mid": v(-7.98, -15.97) * mm, "end": v(-7.9, -15.81) * mm});
            skLineSegment(sketch, "E2724", {"start": v(-8.08, -15.64) * mm, "end": v(-8.17, -15.44) * mm});
            skArc(sketch, "E2725", {"start": v(-8.05, -15.4) * mm, "mid": v(-8.22, -15.33) * mm, "end": v(-8.28, -15.5) * mm});
            skArc(sketch, "E2726", {"start": v(-8.2, -15.7) * mm, "mid": v(-8.04, -15.76) * mm, "end": v(-7.97, -15.6) * mm});
            skLineSegment(sketch, "E2727", {"start": v(-8.17, -15.44) * mm, "end": v(-8.27, -15.25) * mm});
            skArc(sketch, "E2728", {"start": v(-8.16, -15.2) * mm, "mid": v(-8.33, -15.14) * mm, "end": v(-8.38, -15.31) * mm});
            skArc(sketch, "E2729", {"start": v(-8.28, -15.5) * mm, "mid": v(-8.1, -15.55) * mm, "end": v(-8.06, -15.38) * mm});
            skLineSegment(sketch, "E2730", {"start": v(-8.27, -15.25) * mm, "end": v(-8.4, -15.07) * mm});
            skArc(sketch, "E2731", {"start": v(-8.3, -15) * mm, "mid": v(-8.47, -14.96) * mm, "end": v(-8.5, -15.14) * mm});
            skArc(sketch, "E2732", {"start": v(-8.38, -15.32) * mm, "mid": v(-8.2, -15.35) * mm, "end": v(-8.17, -15.18) * mm});
            skLineSegment(sketch, "E2733", {"start": v(-8.4, -15.07) * mm, "end": v(-8.54, -14.9) * mm});
            skArc(sketch, "E2734", {"start": v(-8.44, -14.82) * mm, "mid": v(-8.62, -14.8) * mm, "end": v(-8.64, -14.98) * mm});
            skArc(sketch, "E2735", {"start": v(-8.5, -15.15) * mm, "mid": v(-8.32, -15.16) * mm, "end": v(-8.3, -14.99) * mm});
            skLineSegment(sketch, "E2736", {"start": v(-8.54, -14.9) * mm, "end": v(-8.7, -14.74) * mm});
            skArc(sketch, "E2737", {"start": v(-8.62, -14.65) * mm, "mid": v(-8.8, -14.65) * mm, "end": v(-8.79, -14.83) * mm});
            skArc(sketch, "E2738", {"start": v(-8.63, -14.99) * mm, "mid": v(-8.45, -14.99) * mm, "end": v(-8.45, -14.8) * mm});
            skLineSegment(sketch, "E2739", {"start": v(-8.7, -14.74) * mm, "end": v(-8.87, -14.6) * mm});
            skArc(sketch, "E2740", {"start": v(-8.8, -14.5) * mm, "mid": v(-8.97, -14.53) * mm, "end": v(-8.95, -14.7) * mm});
            skArc(sketch, "E2741", {"start": v(-8.78, -14.84) * mm, "mid": v(-8.6, -14.82) * mm, "end": v(-8.62, -14.64) * mm});
            skLineSegment(sketch, "E2742", {"start": v(-8.87, -14.6) * mm, "end": v(-9.08, -14.47) * mm});
            skArc(sketch, "E2743", {"start": v(-9, -14.37) * mm, "mid": v(-9.18, -14.4) * mm, "end": v(-9.15, -14.58) * mm});
            skArc(sketch, "E2744", {"start": v(-8.94, -14.7) * mm, "mid": v(-8.77, -14.67) * mm, "end": v(-8.8, -14.5) * mm});
            skLineSegment(sketch, "E2745", {"start": v(-9.08, -14.47) * mm, "end": v(-9.28, -14.37) * mm});
            skArc(sketch, "E2746", {"start": v(-9.22, -14.26) * mm, "mid": v(-9.39, -14.31) * mm, "end": v(-9.33, -14.48) * mm});
            skArc(sketch, "E2747", {"start": v(-9.13, -14.58) * mm, "mid": v(-8.97, -14.53) * mm, "end": v(-9.02, -14.36) * mm});
            skLineSegment(sketch, "E2748", {"start": v(-9.28, -14.37) * mm, "end": v(-9.49, -14.29) * mm});
            skArc(sketch, "E2749", {"start": v(-9.44, -14.17) * mm, "mid": v(-9.6, -14.24) * mm, "end": v(-9.53, -14.4) * mm});
            skArc(sketch, "E2750", {"start": v(-9.32, -14.48) * mm, "mid": v(-9.16, -14.41) * mm, "end": v(-9.23, -14.25) * mm});
            skLineSegment(sketch, "E2751", {"start": v(-9.49, -14.29) * mm, "end": v(-9.7, -14.23) * mm});
            skArc(sketch, "E2752", {"start": v(-9.66, -14.1) * mm, "mid": v(-9.82, -14.2) * mm, "end": v(-9.73, -14.35) * mm});
            skArc(sketch, "E2753", {"start": v(-9.52, -14.4) * mm, "mid": v(-9.36, -14.32) * mm, "end": v(-9.45, -14.17) * mm});
            skLineSegment(sketch, "E2754", {"start": v(-9.7, -14.23) * mm, "end": v(-9.91, -14.2) * mm});
            skArc(sketch, "E2755", {"start": v(-9.9, -14.07) * mm, "mid": v(-10.03, -14.17) * mm, "end": v(-9.93, -14.31) * mm});
            skArc(sketch, "E2756", {"start": v(-9.72, -14.35) * mm, "mid": v(-9.57, -14.25) * mm, "end": v(-9.67, -14.1) * mm});
            skLineSegment(sketch, "E2757", {"start": v(-9.91, -14.2) * mm, "end": v(-10.13, -14.17) * mm});
            skArc(sketch, "E2758", {"start": v(-10.12, -14.05) * mm, "mid": v(-10.25, -14.16) * mm, "end": v(-10.14, -14.3) * mm});
            skArc(sketch, "E2759", {"start": v(-9.92, -14.32) * mm, "mid": v(-9.79, -14.2) * mm, "end": v(-9.9, -14.07) * mm});
            skLineSegment(sketch, "E2760", {"start": v(-10.13, -14.17) * mm, "end": v(-10.34, -14.18) * mm});
            skArc(sketch, "E2761", {"start": v(-10.35, -14.05) * mm, "mid": v(-10.47, -14.18) * mm, "end": v(-10.34, -14.3) * mm});
            skArc(sketch, "E2762", {"start": v(-10.13, -14.3) * mm, "mid": v(-10, -14.17) * mm, "end": v(-10.13, -14.05) * mm});
            skLineSegment(sketch, "E2763", {"start": v(-10.34, -14.18) * mm, "end": v(-10.56, -14.2) * mm});
            skArc(sketch, "E2764", {"start": v(-10.57, -14.08) * mm, "mid": v(-10.68, -14.22) * mm, "end": v(-10.54, -14.33) * mm});
            skArc(sketch, "E2765", {"start": v(-10.33, -14.3) * mm, "mid": v(-10.22, -14.16) * mm, "end": v(-10.36, -14.05) * mm});
            skLineSegment(sketch, "E2766", {"start": v(-10.56, -14.2) * mm, "end": v(-10.77, -14.25) * mm});
            skArc(sketch, "E2767", {"start": v(-10.8, -14.13) * mm, "mid": v(-10.9, -14.27) * mm, "end": v(-10.74, -14.37) * mm});
            skArc(sketch, "E2768", {"start": v(-10.53, -14.33) * mm, "mid": v(-10.44, -14.18) * mm, "end": v(-10.59, -14.08) * mm});
            skLineSegment(sketch, "E2769", {"start": v(-10.77, -14.25) * mm, "end": v(-10.98, -14.31) * mm});
            skArc(sketch, "E2770", {"start": v(-11.01, -14.2) * mm, "mid": v(-11.1, -14.35) * mm, "end": v(-10.94, -14.43) * mm});
            skArc(sketch, "E2771", {"start": v(-10.73, -14.37) * mm, "mid": v(-10.65, -14.21) * mm, "end": v(-10.8, -14.13) * mm});
            skLineSegment(sketch, "E2772", {"start": v(-10.98, -14.31) * mm, "end": v(-11.18, -14.4) * mm});
            skArc(sketch, "E2773", {"start": v(-11.23, -14.28) * mm, "mid": v(-11.3, -14.45) * mm, "end": v(-11.13, -14.51) * mm});
            skArc(sketch, "E2774", {"start": v(-10.93, -14.43) * mm, "mid": v(-10.86, -14.26) * mm, "end": v(-11.03, -14.2) * mm});
            skLineSegment(sketch, "E2775", {"start": v(-11.18, -14.4) * mm, "end": v(-11.37, -14.5) * mm});
            skArc(sketch, "E2776", {"start": v(-11.43, -14.4) * mm, "mid": v(-11.48, -14.56) * mm, "end": v(-11.3, -14.61) * mm});
            skArc(sketch, "E2777", {"start": v(-11.12, -14.5) * mm, "mid": v(-11.07, -14.34) * mm, "end": v(-11.24, -14.29) * mm});
            skLineSegment(sketch, "E2778", {"start": v(-11.37, -14.5) * mm, "end": v(-11.55, -14.63) * mm});
            skArc(sketch, "E2779", {"start": v(-11.62, -14.52) * mm, "mid": v(-11.65, -14.7) * mm, "end": v(-11.48, -14.73) * mm});
            skArc(sketch, "E2780", {"start": v(-11.3, -14.6) * mm, "mid": v(-11.26, -14.43) * mm, "end": v(-11.44, -14.4) * mm});
            skLineSegment(sketch, "E2781", {"start": v(-11.55, -14.63) * mm, "end": v(-11.72, -14.77) * mm});
            skArc(sketch, "E2782", {"start": v(-11.8, -14.67) * mm, "mid": v(-11.82, -14.85) * mm, "end": v(-11.64, -14.87) * mm});
            skArc(sketch, "E2783", {"start": v(-11.47, -14.72) * mm, "mid": v(-11.45, -14.55) * mm, "end": v(-11.63, -14.53) * mm});
            skLineSegment(sketch, "E2784", {"start": v(-11.72, -14.77) * mm, "end": v(-11.88, -14.93) * mm});
            skArc(sketch, "E2785", {"start": v(-11.97, -14.84) * mm, "mid": v(-11.97, -15.02) * mm, "end": v(-11.8, -15.02) * mm});
            skArc(sketch, "E2786", {"start": v(-11.63, -14.86) * mm, "mid": v(-11.63, -14.68) * mm, "end": v(-11.81, -14.68) * mm});
            skLineSegment(sketch, "E2787", {"start": v(-11.88, -14.93) * mm, "end": v(-12.03, -15.12) * mm});
            skArc(sketch, "E2788", {"start": v(-12.13, -15.05) * mm, "mid": v(-12.11, -15.22) * mm, "end": v(-11.94, -15.2) * mm});
            skArc(sketch, "E2789", {"start": v(-11.78, -15) * mm, "mid": v(-11.8, -14.83) * mm, "end": v(-11.98, -14.85) * mm});
            skLineSegment(sketch, "E2790", {"start": v(-12.03, -15.12) * mm, "end": v(-14, -17.82) * mm});
            skArc(sketch, "E2791", {"start": v(-14.1, -17.74) * mm, "mid": v(-14.06, -17.92) * mm, "end": v(-13.89, -17.9) * mm});
            skArc(sketch, "E2792", {"start": v(-11.93, -15.2) * mm, "mid": v(-11.96, -15.02) * mm, "end": v(-12.14, -15.05) * mm});
            skLineSegment(sketch, "E2793", {"start": v(-14, -17.82) * mm, "end": v(-14.7, -20.04) * mm});
            skArc(sketch, "E2794", {"start": v(-14.83, -20) * mm, "mid": v(-14.75, -20.15) * mm, "end": v(-14.6, -20.07) * mm});
            skArc(sketch, "E2795", {"start": v(-13.87, -17.86) * mm, "mid": v(-13.95, -17.7) * mm, "end": v(-14.1, -17.78) * mm});
            skLineSegment(sketch, "E2796", {"start": v(-14.7, -20.04) * mm, "end": v(-14.77, -21.1) * mm});
            skArc(sketch, "E2797", {"start": v(-14.89, -21.08) * mm, "mid": v(-14.77, -21.21) * mm, "end": v(-14.64, -21.1) * mm});
            skArc(sketch, "E2798", {"start": v(-14.59, -20.04) * mm, "mid": v(-14.7, -19.91) * mm, "end": v(-14.83, -20.03) * mm});
            skLineSegment(sketch, "E2799", {"start": v(-14.77, -21.1) * mm, "end": v(-13.22, -22.21) * mm});
            skArc(sketch, "E2800", {"start": v(-13.3, -22.31) * mm, "mid": v(-13.12, -22.28) * mm, "end": v(-13.15, -22.1) * mm});
            skArc(sketch, "E2801", {"start": v(-14.7, -20.99) * mm, "mid": v(-14.87, -21.02) * mm, "end": v(-14.84, -21.2) * mm});
            skLineSegment(sketch, "E2802", {"start": v(-13.22, -22.21) * mm, "end": v(-12.24, -21.83) * mm});
            skArc(sketch, "E2803", {"start": v(-12.2, -21.95) * mm, "mid": v(-12.12, -21.79) * mm, "end": v(-12.28, -21.72) * mm});
            skArc(sketch, "E2804", {"start": v(-13.27, -22.1) * mm, "mid": v(-13.34, -22.26) * mm, "end": v(-13.18, -22.33) * mm});
            skLineSegment(sketch, "E2805", {"start": v(-12.24, -21.83) * mm, "end": v(-10.35, -20.46) * mm});
            skArc(sketch, "E2806", {"start": v(-10.28, -20.56) * mm, "mid": v(-10.25, -20.39) * mm, "end": v(-10.42, -20.36) * mm});
            skArc(sketch, "E2807", {"start": v(-12.31, -21.73) * mm, "mid": v(-12.34, -21.9) * mm, "end": v(-12.16, -21.93) * mm});
            skLineSegment(sketch, "E2808", {"start": v(-8.19, -15.41) * mm, "end": v(-9.85, -14.2) * mm});
            skArc(sketch, "E2809", {"start": v(-9.78, -14.1) * mm, "mid": v(-9.95, -14.13) * mm, "end": v(-9.93, -14.3) * mm});
            skArc(sketch, "E2810", {"start": v(-8.26, -15.51) * mm, "mid": v(-8.09, -15.49) * mm, "end": v(-8.11, -15.31) * mm});
            skLineSegment(sketch, "E2811", {"start": v(-7.96, -16.2) * mm, "end": v(-10.67, -14.23) * mm});
            skArc(sketch, "E2812", {"start": v(-10.6, -14.13) * mm, "mid": v(-10.77, -14.15) * mm, "end": v(-10.74, -14.33) * mm});
            skArc(sketch, "E2813", {"start": v(-8.03, -16.3) * mm, "mid": v(-7.86, -16.27) * mm, "end": v(-7.89, -16.1) * mm});
            skLineSegment(sketch, "E2814", {"start": v(-7.98, -16.8) * mm, "end": v(-11.24, -14.43) * mm});
            skArc(sketch, "E2815", {"start": v(-11.16, -14.33) * mm, "mid": v(-11.34, -14.36) * mm, "end": v(-11.31, -14.53) * mm});
            skArc(sketch, "E2816", {"start": v(-8.05, -16.9) * mm, "mid": v(-7.88, -16.87) * mm, "end": v(-7.9, -16.7) * mm});
            skLineSegment(sketch, "E2817", {"start": v(-8.13, -17.3) * mm, "end": v(-11.68, -14.73) * mm});
            skArc(sketch, "E2818", {"start": v(-11.6, -14.63) * mm, "mid": v(-11.78, -14.66) * mm, "end": v(-11.75, -14.83) * mm});
            skArc(sketch, "E2819", {"start": v(-8.2, -17.4) * mm, "mid": v(-8.03, -17.38) * mm, "end": v(-8.05, -17.2) * mm});
            skLineSegment(sketch, "E2820", {"start": v(-8.38, -17.74) * mm, "end": v(-12.02, -15.1) * mm});
            skArc(sketch, "E2821", {"start": v(-11.94, -15) * mm, "mid": v(-12.12, -15.03) * mm, "end": v(-12.09, -15.2) * mm});
            skArc(sketch, "E2822", {"start": v(-8.46, -17.84) * mm, "mid": v(-8.28, -17.81) * mm, "end": v(-8.31, -17.64) * mm});
            skLineSegment(sketch, "E2823", {"start": v(-8.68, -18.15) * mm, "end": v(-12.31, -15.5) * mm});
            skArc(sketch, "E2824", {"start": v(-12.24, -15.4) * mm, "mid": v(-12.41, -15.43) * mm, "end": v(-12.38, -15.6) * mm});
            skArc(sketch, "E2825", {"start": v(-8.75, -18.25) * mm, "mid": v(-8.58, -18.22) * mm, "end": v(-8.6, -18.04) * mm});
            skLineSegment(sketch, "E2826", {"start": v(-8.97, -18.55) * mm, "end": v(-12.6, -15.9) * mm});
            skArc(sketch, "E2827", {"start": v(-12.53, -15.8) * mm, "mid": v(-12.7, -15.84) * mm, "end": v(-12.68, -16.01) * mm});
            skArc(sketch, "E2828", {"start": v(-9.04, -18.65) * mm, "mid": v(-8.87, -18.62) * mm, "end": v(-8.9, -18.45) * mm});
            skLineSegment(sketch, "E2829", {"start": v(-9.26, -18.96) * mm, "end": v(-12.9, -16.31) * mm});
            skArc(sketch, "E2830", {"start": v(-12.82, -16.21) * mm, "mid": v(-13, -16.24) * mm, "end": v(-12.97, -16.42) * mm});
            skArc(sketch, "E2831", {"start": v(-9.34, -19.06) * mm, "mid": v(-9.16, -19.03) * mm, "end": v(-9.19, -18.85) * mm});
            skLineSegment(sketch, "E2832", {"start": v(-9.56, -19.36) * mm, "end": v(-13.2, -16.72) * mm});
            skArc(sketch, "E2833", {"start": v(-13.12, -16.62) * mm, "mid": v(-13.3, -16.65) * mm, "end": v(-13.27, -16.82) * mm});
            skArc(sketch, "E2834", {"start": v(-9.63, -19.46) * mm, "mid": v(-9.45, -19.43) * mm, "end": v(-9.48, -19.26) * mm});
            skLineSegment(sketch, "E2835", {"start": v(-9.85, -19.77) * mm, "end": v(-13.49, -17.12) * mm});
            skArc(sketch, "E2836", {"start": v(-13.41, -17.02) * mm, "mid": v(-13.59, -17.05) * mm, "end": v(-13.56, -17.22) * mm});
            skArc(sketch, "E2837", {"start": v(-9.92, -19.87) * mm, "mid": v(-9.75, -19.84) * mm, "end": v(-9.77, -19.67) * mm});
            skLineSegment(sketch, "E2838", {"start": v(-10.14, -20.17) * mm, "end": v(-13.78, -17.53) * mm});
            skArc(sketch, "E2839", {"start": v(-13.7, -17.43) * mm, "mid": v(-13.88, -17.45) * mm, "end": v(-13.85, -17.63) * mm});
            skArc(sketch, "E2840", {"start": v(-10.21, -20.27) * mm, "mid": v(-10.04, -20.25) * mm, "end": v(-10.07, -20.07) * mm});
            skLineSegment(sketch, "E2841", {"start": v(-10.47, -20.55) * mm, "end": v(-14.04, -17.96) * mm});
            skArc(sketch, "E2842", {"start": v(-13.96, -17.86) * mm, "mid": v(-14.14, -17.89) * mm, "end": v(-14.11, -18.06) * mm});
            skArc(sketch, "E2843", {"start": v(-10.54, -20.65) * mm, "mid": v(-10.37, -20.62) * mm, "end": v(-10.4, -20.45) * mm});
            skLineSegment(sketch, "E2844", {"start": v(-10.9, -20.86) * mm, "end": v(-14.2, -18.46) * mm});
            skArc(sketch, "E2845", {"start": v(-14.13, -18.36) * mm, "mid": v(-14.3, -18.39) * mm, "end": v(-14.27, -18.56) * mm});
            skArc(sketch, "E2846", {"start": v(-10.97, -20.96) * mm, "mid": v(-10.8, -20.93) * mm, "end": v(-10.82, -20.76) * mm});
            skLineSegment(sketch, "E2847", {"start": v(-11.32, -21.17) * mm, "end": v(-14.36, -18.96) * mm});
            skArc(sketch, "E2848", {"start": v(-14.29, -18.86) * mm, "mid": v(-14.46, -18.89) * mm, "end": v(-14.43, -19.06) * mm});
            skArc(sketch, "E2849", {"start": v(-11.4, -21.27) * mm, "mid": v(-11.22, -21.24) * mm, "end": v(-11.25, -21.07) * mm});
            skLineSegment(sketch, "E2850", {"start": v(-11.75, -21.48) * mm, "end": v(-14.52, -19.46) * mm});
            skArc(sketch, "E2851", {"start": v(-14.45, -19.36) * mm, "mid": v(-14.62, -19.39) * mm, "end": v(-14.6, -19.56) * mm});
            skArc(sketch, "E2852", {"start": v(-11.82, -21.58) * mm, "mid": v(-11.65, -21.55) * mm, "end": v(-11.67, -21.38) * mm});
            skLineSegment(sketch, "E2853", {"start": v(-12.17, -21.79) * mm, "end": v(-14.69, -19.96) * mm});
            skArc(sketch, "E2854", {"start": v(-14.61, -19.86) * mm, "mid": v(-14.79, -19.89) * mm, "end": v(-14.76, -20.06) * mm});
            skArc(sketch, "E2855", {"start": v(-12.25, -21.89) * mm, "mid": v(-12.07, -21.86) * mm, "end": v(-12.1, -21.68) * mm});
            skLineSegment(sketch, "E2856", {"start": v(-12.7, -22.01) * mm, "end": v(-14.74, -20.54) * mm});
            skArc(sketch, "E2857", {"start": v(-14.66, -20.44) * mm, "mid": v(-14.84, -20.47) * mm, "end": v(-14.8, -20.64) * mm});
            skArc(sketch, "E2858", {"start": v(-12.78, -22.11) * mm, "mid": v(-12.6, -22.09) * mm, "end": v(-12.64, -21.91) * mm});
            skLineSegment(sketch, "E2859", {"start": v(-16.1, -28.7) * mm, "end": v(-16.12, -28.55) * mm});
            skArc(sketch, "E2860", {"start": v(-16.07, -28.54) * mm, "mid": v(-16.13, -28.5) * mm, "end": v(-16.17, -28.56) * mm});
            skArc(sketch, "E2861", {"start": v(-16.15, -28.7) * mm, "mid": v(-16.1, -28.74) * mm, "end": v(-16.05, -28.68) * mm});
            skLineSegment(sketch, "E2862", {"start": v(-16.12, -28.55) * mm, "end": v(-16.17, -28.4) * mm});
            skArc(sketch, "E2863", {"start": v(-16.13, -28.39) * mm, "mid": v(-16.19, -28.36) * mm, "end": v(-16.22, -28.42) * mm});
            skArc(sketch, "E2864", {"start": v(-16.17, -28.57) * mm, "mid": v(-16.1, -28.6) * mm, "end": v(-16.08, -28.54) * mm});
            skLineSegment(sketch, "E2865", {"start": v(-16.17, -28.4) * mm, "end": v(-16.25, -28.27) * mm});
            skArc(sketch, "E2866", {"start": v(-16.2, -28.24) * mm, "mid": v(-16.27, -28.23) * mm, "end": v(-16.3, -28.3) * mm});
            skArc(sketch, "E2867", {"start": v(-16.22, -28.43) * mm, "mid": v(-16.15, -28.45) * mm, "end": v(-16.13, -28.38) * mm});
            skLineSegment(sketch, "E2868", {"start": v(-16.25, -28.27) * mm, "end": v(-16.35, -28.15) * mm});
            skArc(sketch, "E2869", {"start": v(-16.3, -28.11) * mm, "mid": v(-16.38, -28.1) * mm, "end": v(-16.39, -28.18) * mm});
            skArc(sketch, "E2870", {"start": v(-16.29, -28.3) * mm, "mid": v(-16.22, -28.3) * mm, "end": v(-16.2, -28.24) * mm});
            skLineSegment(sketch, "E2871", {"start": v(-16.35, -28.15) * mm, "end": v(-16.4, -28.1) * mm});
            skArc(sketch, "E2872", {"start": v(-16.37, -28.05) * mm, "mid": v(-16.44, -28.06) * mm, "end": v(-16.44, -28.13) * mm});
            skArc(sketch, "E2873", {"start": v(-16.38, -28.18) * mm, "mid": v(-16.31, -28.18) * mm, "end": v(-16.31, -28.1) * mm});
            skLineSegment(sketch, "E2874", {"start": v(-16.4, -28.1) * mm, "end": v(-19.45, -25.9) * mm});
            skArc(sketch, "E2875", {"start": v(-19.42, -25.85) * mm, "mid": v(-19.5, -25.86) * mm, "end": v(-19.48, -25.93) * mm});
            skArc(sketch, "E2876", {"start": v(-16.43, -28.13) * mm, "mid": v(-16.37, -28.12) * mm, "end": v(-16.38, -28.05) * mm});
            skLineSegment(sketch, "E2877", {"start": v(-19.45, -25.9) * mm, "end": v(-19.6, -25.84) * mm});
            skArc(sketch, "E2878", {"start": v(-19.58, -25.8) * mm, "mid": v(-19.64, -25.82) * mm, "end": v(-19.62, -25.89) * mm});
            skArc(sketch, "E2879", {"start": v(-19.47, -25.94) * mm, "mid": v(-19.4, -25.91) * mm, "end": v(-19.43, -25.85) * mm});
            skLineSegment(sketch, "E2880", {"start": v(-19.6, -25.84) * mm, "end": v(-19.75, -25.81) * mm});
            skArc(sketch, "E2881", {"start": v(-19.74, -25.76) * mm, "mid": v(-19.8, -25.8) * mm, "end": v(-19.76, -25.86) * mm});
            skArc(sketch, "E2882", {"start": v(-19.6, -25.89) * mm, "mid": v(-19.55, -25.85) * mm, "end": v(-19.59, -25.79) * mm});
            skLineSegment(sketch, "E2883", {"start": v(-19.75, -25.81) * mm, "end": v(-19.9, -25.8) * mm});
            skArc(sketch, "E2884", {"start": v(-19.9, -25.76) * mm, "mid": v(-19.96, -25.8) * mm, "end": v(-19.9, -25.86) * mm});
            skArc(sketch, "E2885", {"start": v(-19.75, -25.86) * mm, "mid": v(-19.7, -25.81) * mm, "end": v(-19.75, -25.76) * mm});
            skLineSegment(sketch, "E2886", {"start": v(-19.9, -25.8) * mm, "end": v(-20.04, -25.83) * mm});
            skArc(sketch, "E2887", {"start": v(-20.04, -25.78) * mm, "mid": v(-20.09, -25.84) * mm, "end": v(-20.03, -25.88) * mm});
            skArc(sketch, "E2888", {"start": v(-19.9, -25.86) * mm, "mid": v(-19.86, -25.8) * mm, "end": v(-19.91, -25.76) * mm});
            skLineSegment(sketch, "E2889", {"start": v(-20.04, -25.83) * mm, "end": v(-20.01, -25.97) * mm});
            skArc(sketch, "E2890", {"start": v(-20.06, -25.98) * mm, "mid": v(-20, -26.02) * mm, "end": v(-19.96, -25.96) * mm});
            skArc(sketch, "E2891", {"start": v(-19.99, -25.82) * mm, "mid": v(-20.04, -25.78) * mm, "end": v(-20.09, -25.84) * mm});
            skLineSegment(sketch, "E2892", {"start": v(-20.01, -25.97) * mm, "end": v(-19.96, -26.12) * mm});
            skArc(sketch, "E2893", {"start": v(-20, -26.13) * mm, "mid": v(-19.95, -26.16) * mm, "end": v(-19.92, -26.1) * mm});
            skArc(sketch, "E2894", {"start": v(-19.97, -25.95) * mm, "mid": v(-20.03, -25.92) * mm, "end": v(-20.06, -25.99) * mm});
            skLineSegment(sketch, "E2895", {"start": v(-19.96, -26.12) * mm, "end": v(-19.89, -26.25) * mm});
            skArc(sketch, "E2896", {"start": v(-19.93, -26.28) * mm, "mid": v(-19.86, -26.3) * mm, "end": v(-19.84, -26.23) * mm});
            skArc(sketch, "E2897", {"start": v(-19.92, -26.1) * mm, "mid": v(-19.99, -26.07) * mm, "end": v(-20, -26.14) * mm});
            skLineSegment(sketch, "E2898", {"start": v(-19.89, -26.25) * mm, "end": v(-19.79, -26.38) * mm});
            skArc(sketch, "E2899", {"start": v(-19.83, -26.4) * mm, "mid": v(-19.76, -26.42) * mm, "end": v(-19.75, -26.34) * mm});
            skArc(sketch, "E2900", {"start": v(-19.85, -26.22) * mm, "mid": v(-19.92, -26.21) * mm, "end": v(-19.93, -26.28) * mm});
            skLineSegment(sketch, "E2901", {"start": v(-19.79, -26.38) * mm, "end": v(-19.73, -26.43) * mm});
            skArc(sketch, "E2902", {"start": v(-19.76, -26.47) * mm, "mid": v(-19.7, -26.47) * mm, "end": v(-19.7, -26.4) * mm});
            skArc(sketch, "E2903", {"start": v(-19.75, -26.34) * mm, "mid": v(-19.82, -26.34) * mm, "end": v(-19.82, -26.41) * mm});
            skLineSegment(sketch, "E2904", {"start": v(-19.73, -26.43) * mm, "end": v(-16.69, -28.63) * mm});
            skArc(sketch, "E2905", {"start": v(-16.71, -28.67) * mm, "mid": v(-16.64, -28.66) * mm, "end": v(-16.66, -28.59) * mm});
            skArc(sketch, "E2906", {"start": v(-19.7, -26.4) * mm, "mid": v(-19.77, -26.4) * mm, "end": v(-19.76, -26.47) * mm});
            skLineSegment(sketch, "E2907", {"start": v(-16.69, -28.63) * mm, "end": v(-16.54, -28.68) * mm});
            skArc(sketch, "E2908", {"start": v(-16.55, -28.73) * mm, "mid": v(-16.5, -28.7) * mm, "end": v(-16.52, -28.64) * mm});
            skArc(sketch, "E2909", {"start": v(-16.67, -28.58) * mm, "mid": v(-16.73, -28.61) * mm, "end": v(-16.7, -28.68) * mm});
            skLineSegment(sketch, "E2910", {"start": v(-16.54, -28.68) * mm, "end": v(-16.38, -28.71) * mm});
            skArc(sketch, "E2911", {"start": v(-16.4, -28.76) * mm, "mid": v(-16.34, -28.72) * mm, "end": v(-16.38, -28.66) * mm});
            skArc(sketch, "E2912", {"start": v(-16.53, -28.63) * mm, "mid": v(-16.59, -28.67) * mm, "end": v(-16.55, -28.73) * mm});
            skLineSegment(sketch, "E2913", {"start": v(-16.38, -28.71) * mm, "end": v(-16.23, -28.71) * mm});
            skArc(sketch, "E2914", {"start": v(-16.23, -28.76) * mm, "mid": v(-16.18, -28.71) * mm, "end": v(-16.23, -28.66) * mm});
            skArc(sketch, "E2915", {"start": v(-16.38, -28.66) * mm, "mid": v(-16.43, -28.71) * mm, "end": v(-16.38, -28.76) * mm});
            skLineSegment(sketch, "E2916", {"start": v(-16.23, -28.71) * mm, "end": v(-16.1, -28.7) * mm});
            skArc(sketch, "E2917", {"start": v(-16.1, -28.74) * mm, "mid": v(-16.05, -28.68) * mm, "end": v(-16.1, -28.64) * mm});
            skArc(sketch, "E2918", {"start": v(-16.24, -28.66) * mm, "mid": v(-16.28, -28.72) * mm, "end": v(-16.22, -28.76) * mm});
            skLineSegment(sketch, "E2919", {"start": v(-16.18, -28.4) * mm, "end": v(-19.73, -25.82) * mm});
            skArc(sketch, "E2920", {"start": v(-19.7, -25.78) * mm, "mid": v(-19.77, -25.79) * mm, "end": v(-19.76, -25.86) * mm});
            skArc(sketch, "E2921", {"start": v(-16.2, -28.43) * mm, "mid": v(-16.14, -28.42) * mm, "end": v(-16.15, -28.35) * mm});
            skLineSegment(sketch, "E2922", {"start": v(-16.1, -28.7) * mm, "end": v(-20.03, -25.84) * mm});
            skArc(sketch, "E2923", {"start": v(-20, -25.8) * mm, "mid": v(-20.08, -25.8) * mm, "end": v(-20.06, -25.88) * mm});
            skArc(sketch, "E2924", {"start": v(-16.14, -28.73) * mm, "mid": v(-16.07, -28.72) * mm, "end": v(-16.08, -28.65) * mm});
            skLineSegment(sketch, "E2925", {"start": v(-16.43, -28.7) * mm, "end": v(-19.94, -26.15) * mm});
            skArc(sketch, "E2926", {"start": v(-19.91, -26.11) * mm, "mid": v(-19.98, -26.12) * mm, "end": v(-19.97, -26.2) * mm});
            skArc(sketch, "E2927", {"start": v(-16.46, -28.74) * mm, "mid": v(-16.4, -28.73) * mm, "end": v(-16.4, -28.66) * mm});
            skCircle(sketch, "E2928", {"center": v(-10.2, -16.42) * mm, "radius": 1.7 * mm});
            skArc(sketch, "E2929", {"start": v(-10.2, -17.3) * mm, "mid": v(-9.32, -16.42) * mm, "end": v(-10.2, -15.55) * mm});
            skArc(sketch, "E2930", {"start": v(-10.2, -15.55) * mm, "mid": v(-11.07, -16.42) * mm, "end": v(-10.2, -17.3) * mm});
            skCircle(sketch, "E2931", {"center": v(-16.07, -24.51) * mm, "radius": 1.7 * mm});
            skArc(sketch, "E2932", {"start": v(-16.07, -25.4) * mm, "mid": v(-15.2, -24.51) * mm, "end": v(-16.07, -23.64) * mm});
            skArc(sketch, "E2933", {"start": v(-16.07, -23.64) * mm, "mid": v(-16.95, -24.51) * mm, "end": v(-16.07, -25.4) * mm});
            skLineSegment(sketch, "E2934", {"start": v(4.19, 11.1) * mm, "end": v(4.19, 11.14) * mm});
            skArc(sketch, "E2935", {"start": v(4.21, 11.14) * mm, "mid": v(4.19, 11.17) * mm, "end": v(4.16, 11.14) * mm});
            skArc(sketch, "E2936", {"start": v(4.16, 11.1) * mm, "mid": v(4.19, 11.07) * mm, "end": v(4.21, 11.1) * mm});
            skLineSegment(sketch, "E2937", {"start": v(4.19, 11.14) * mm, "end": v(3.69, 11.3) * mm});
            skArc(sketch, "E2938", {"start": v(3.7, 11.32) * mm, "mid": v(3.66, 11.3) * mm, "end": v(3.68, 11.27) * mm});
            skArc(sketch, "E2939", {"start": v(4.18, 11.12) * mm, "mid": v(4.21, 11.13) * mm, "end": v(4.2, 11.17) * mm});
            skLineSegment(sketch, "E2940", {"start": v(3.69, 11.3) * mm, "end": v(3.19, 11.3) * mm});
            skArc(sketch, "E2941", {"start": v(3.19, 11.32) * mm, "mid": v(3.16, 11.3) * mm, "end": v(3.19, 11.27) * mm});
            skArc(sketch, "E2942", {"start": v(3.69, 11.27) * mm, "mid": v(3.71, 11.3) * mm, "end": v(3.69, 11.32) * mm});
            skLineSegment(sketch, "E2943", {"start": v(3.19, 11.3) * mm, "end": v(3.19, 11.1) * mm});
            skArc(sketch, "E2944", {"start": v(3.16, 11.1) * mm, "mid": v(3.19, 11.07) * mm, "end": v(3.21, 11.1) * mm});
            skArc(sketch, "E2945", {"start": v(3.21, 11.3) * mm, "mid": v(3.19, 11.32) * mm, "end": v(3.16, 11.3) * mm});
            skLineSegment(sketch, "E2946", {"start": v(3.19, 11.1) * mm, "end": v(4.19, 11.1) * mm});
            skArc(sketch, "E2947", {"start": v(4.19, 11.07) * mm, "mid": v(4.21, 11.1) * mm, "end": v(4.19, 11.12) * mm});
            skArc(sketch, "E2948", {"start": v(3.19, 11.12) * mm, "mid": v(3.16, 11.1) * mm, "end": v(3.19, 11.07) * mm});
            skLineSegment(sketch, "E2949", {"start": v(4.02, 11.2) * mm, "end": v(3.19, 11.2) * mm});
            skArc(sketch, "E2950", {"start": v(3.19, 11.22) * mm, "mid": v(3.16, 11.2) * mm, "end": v(3.19, 11.17) * mm});
            skArc(sketch, "E2951", {"start": v(4.02, 11.17) * mm, "mid": v(4.05, 11.2) * mm, "end": v(4.02, 11.22) * mm});
            skLineSegment(sketch, "E2952", {"start": v(-4.21, 11.1) * mm, "end": v(-4.21, 11.14) * mm});
            skArc(sketch, "E2953", {"start": v(-4.19, 11.14) * mm, "mid": v(-4.21, 11.17) * mm, "end": v(-4.24, 11.14) * mm});
            skArc(sketch, "E2954", {"start": v(-4.24, 11.1) * mm, "mid": v(-4.21, 11.07) * mm, "end": v(-4.19, 11.1) * mm});
            skLineSegment(sketch, "E2955", {"start": v(-4.21, 11.14) * mm, "end": v(-3.71, 11.3) * mm});
            skArc(sketch, "E2956", {"start": v(-3.7, 11.27) * mm, "mid": v(-3.69, 11.3) * mm, "end": v(-3.72, 11.32) * mm});
            skArc(sketch, "E2957", {"start": v(-4.22, 11.17) * mm, "mid": v(-4.24, 11.13) * mm, "end": v(-4.2, 11.12) * mm});
            skLineSegment(sketch, "E2958", {"start": v(-3.71, 11.3) * mm, "end": v(-3.21, 11.3) * mm});
            skArc(sketch, "E2959", {"start": v(-3.21, 11.27) * mm, "mid": v(-3.19, 11.3) * mm, "end": v(-3.21, 11.32) * mm});
            skArc(sketch, "E2960", {"start": v(-3.71, 11.32) * mm, "mid": v(-3.74, 11.3) * mm, "end": v(-3.71, 11.27) * mm});
            skLineSegment(sketch, "E2961", {"start": v(-3.21, 11.3) * mm, "end": v(-3.21, 11.1) * mm});
            skArc(sketch, "E2962", {"start": v(-3.24, 11.1) * mm, "mid": v(-3.21, 11.07) * mm, "end": v(-3.19, 11.1) * mm});
            skArc(sketch, "E2963", {"start": v(-3.19, 11.3) * mm, "mid": v(-3.21, 11.32) * mm, "end": v(-3.24, 11.3) * mm});
            skLineSegment(sketch, "E2964", {"start": v(-3.21, 11.1) * mm, "end": v(-4.21, 11.1) * mm});
            skArc(sketch, "E2965", {"start": v(-4.21, 11.12) * mm, "mid": v(-4.24, 11.1) * mm, "end": v(-4.21, 11.07) * mm});
            skArc(sketch, "E2966", {"start": v(-3.21, 11.07) * mm, "mid": v(-3.19, 11.1) * mm, "end": v(-3.21, 11.12) * mm});
            skLineSegment(sketch, "E2967", {"start": v(-3.21, 11.3) * mm, "end": v(-3.71, 11.3) * mm});
            skLineSegment(sketch, "E2968", {"start": v(-3.21, 11.2) * mm, "end": v(-4.05, 11.2) * mm});
            skArc(sketch, "E2969", {"start": v(-4.05, 11.22) * mm, "mid": v(-4.07, 11.2) * mm, "end": v(-4.05, 11.17) * mm});
            skArc(sketch, "E2970", {"start": v(-3.21, 11.17) * mm, "mid": v(-3.19, 11.2) * mm, "end": v(-3.21, 11.22) * mm});
            skCircle(sketch, "E2971", {"center": v(1.49, 9.1) * mm, "radius": 0.45 * mm});
            skArc(sketch, "E2972", {"start": v(1.49, 8.84) * mm, "mid": v(1.74, 9.1) * mm, "end": v(1.49, 9.34) * mm});
            skArc(sketch, "E2973", {"start": v(1.49, 9.34) * mm, "mid": v(1.24, 9.1) * mm, "end": v(1.49, 8.84) * mm});
            skCircle(sketch, "E2974", {"center": v(-1.51, 9.1) * mm, "radius": 0.45 * mm});
            skArc(sketch, "E2975", {"start": v(-1.51, 8.84) * mm, "mid": v(-1.26, 9.1) * mm, "end": v(-1.51, 9.34) * mm});
            skArc(sketch, "E2976", {"start": v(-1.51, 9.34) * mm, "mid": v(-1.76, 9.1) * mm, "end": v(-1.51, 8.84) * mm});
            skLineSegment(sketch, "E2977", {"start": v(2.68, 5.86) * mm, "end": v(2.68, 7.22) * mm});
            skArc(sketch, "E2978", {"start": v(2.68, 7.22) * mm, "mid": v(2.66, 7.26) * mm, "end": v(2.62, 7.28) * mm});
            skLineSegment(sketch, "E2979", {"start": v(2.62, 7.28) * mm, "end": v(2.06, 7.28) * mm});
            skArc(sketch, "E2980", {"start": v(2.06, 7.28) * mm, "mid": v(2.01, 7.26) * mm, "end": v(2, 7.22) * mm});
            skLineSegment(sketch, "E2981", {"start": v(2, 7.22) * mm, "end": v(2, 5.86) * mm});
            skArc(sketch, "E2982", {"start": v(2, 5.86) * mm, "mid": v(2.01, 5.82) * mm, "end": v(2.06, 5.8) * mm});
            skLineSegment(sketch, "E2983", {"start": v(2.06, 5.8) * mm, "end": v(2.62, 5.8) * mm});
            skArc(sketch, "E2984", {"start": v(2.62, 5.8) * mm, "mid": v(2.66, 5.82) * mm, "end": v(2.68, 5.86) * mm});
            skLineSegment(sketch, "E2985", {"start": v(-0.42, 5.86) * mm, "end": v(-0.42, 7.22) * mm});
            skArc(sketch, "E2986", {"start": v(-0.42, 7.22) * mm, "mid": v(-0.44, 7.26) * mm, "end": v(-0.48, 7.28) * mm});
            skLineSegment(sketch, "E2987", {"start": v(-0.48, 7.28) * mm, "end": v(-1.04, 7.28) * mm});
            skArc(sketch, "E2988", {"start": v(-1.04, 7.28) * mm, "mid": v(-1.09, 7.26) * mm, "end": v(-1.1, 7.22) * mm});
            skLineSegment(sketch, "E2989", {"start": v(-1.1, 7.22) * mm, "end": v(-1.1, 5.86) * mm});
            skArc(sketch, "E2990", {"start": v(-1.1, 5.86) * mm, "mid": v(-1.09, 5.82) * mm, "end": v(-1.04, 5.8) * mm});
            skLineSegment(sketch, "E2991", {"start": v(-1.04, 5.8) * mm, "end": v(-0.48, 5.8) * mm});
            skArc(sketch, "E2992", {"start": v(-0.48, 5.8) * mm, "mid": v(-0.44, 5.82) * mm, "end": v(-0.42, 5.86) * mm});
            skLineSegment(sketch, "E2993", {"start": v(-1.92, 5.86) * mm, "end": v(-1.92, 7.22) * mm});
            skArc(sketch, "E2994", {"start": v(-1.92, 7.22) * mm, "mid": v(-1.94, 7.26) * mm, "end": v(-1.98, 7.28) * mm});
            skLineSegment(sketch, "E2995", {"start": v(-1.98, 7.28) * mm, "end": v(-2.54, 7.28) * mm});
            skArc(sketch, "E2996", {"start": v(-2.54, 7.28) * mm, "mid": v(-2.59, 7.26) * mm, "end": v(-2.6, 7.22) * mm});
            skLineSegment(sketch, "E2997", {"start": v(-2.6, 7.22) * mm, "end": v(-2.6, 5.86) * mm});
            skArc(sketch, "E2998", {"start": v(-2.6, 5.86) * mm, "mid": v(-2.59, 5.82) * mm, "end": v(-2.54, 5.8) * mm});
            skLineSegment(sketch, "E2999", {"start": v(-2.54, 5.8) * mm, "end": v(-1.98, 5.8) * mm});
            skArc(sketch, "E3000", {"start": v(-1.98, 5.8) * mm, "mid": v(-1.94, 5.82) * mm, "end": v(-1.92, 5.86) * mm});
            skLineSegment(sketch, "E3001", {"start": v(2.58, 10.96) * mm, "end": v(2.58, 12.32) * mm});
            skArc(sketch, "E3002", {"start": v(2.58, 12.32) * mm, "mid": v(2.56, 12.36) * mm, "end": v(2.52, 12.38) * mm});
            skLineSegment(sketch, "E3003", {"start": v(2.52, 12.38) * mm, "end": v(1.96, 12.38) * mm});
            skArc(sketch, "E3004", {"start": v(1.96, 12.38) * mm, "mid": v(1.91, 12.36) * mm, "end": v(1.9, 12.32) * mm});
            skLineSegment(sketch, "E3005", {"start": v(1.9, 12.32) * mm, "end": v(1.9, 10.96) * mm});
            skArc(sketch, "E3006", {"start": v(1.9, 10.96) * mm, "mid": v(1.91, 10.92) * mm, "end": v(1.96, 10.9) * mm});
            skLineSegment(sketch, "E3007", {"start": v(1.96, 10.9) * mm, "end": v(2.52, 10.9) * mm});
            skArc(sketch, "E3008", {"start": v(2.52, 10.9) * mm, "mid": v(2.56, 10.92) * mm, "end": v(2.58, 10.96) * mm});
            skLineSegment(sketch, "E3009", {"start": v(-0.42, 10.96) * mm, "end": v(-0.42, 12.32) * mm});
            skArc(sketch, "E3010", {"start": v(-0.42, 12.32) * mm, "mid": v(-0.44, 12.36) * mm, "end": v(-0.48, 12.38) * mm});
            skLineSegment(sketch, "E3011", {"start": v(-0.48, 12.38) * mm, "end": v(-1.04, 12.38) * mm});
            skArc(sketch, "E3012", {"start": v(-1.04, 12.38) * mm, "mid": v(-1.09, 12.36) * mm, "end": v(-1.1, 12.32) * mm});
            skLineSegment(sketch, "E3013", {"start": v(-1.1, 12.32) * mm, "end": v(-1.1, 10.96) * mm});
            skArc(sketch, "E3014", {"start": v(-1.1, 10.96) * mm, "mid": v(-1.09, 10.92) * mm, "end": v(-1.04, 10.9) * mm});
            skLineSegment(sketch, "E3015", {"start": v(-1.04, 10.9) * mm, "end": v(-0.48, 10.9) * mm});
            skArc(sketch, "E3016", {"start": v(-0.48, 10.9) * mm, "mid": v(-0.44, 10.92) * mm, "end": v(-0.42, 10.96) * mm});
            skLineSegment(sketch, "E3017", {"start": v(-1.92, 10.96) * mm, "end": v(-1.92, 12.32) * mm});
            skArc(sketch, "E3018", {"start": v(-1.92, 12.32) * mm, "mid": v(-1.94, 12.36) * mm, "end": v(-1.98, 12.38) * mm});
            skLineSegment(sketch, "E3019", {"start": v(-1.98, 12.38) * mm, "end": v(-2.54, 12.38) * mm});
            skArc(sketch, "E3020", {"start": v(-2.54, 12.38) * mm, "mid": v(-2.59, 12.36) * mm, "end": v(-2.6, 12.32) * mm});
            skLineSegment(sketch, "E3021", {"start": v(-2.6, 12.32) * mm, "end": v(-2.6, 10.96) * mm});
            skArc(sketch, "E3022", {"start": v(-2.6, 10.96) * mm, "mid": v(-2.59, 10.92) * mm, "end": v(-2.54, 10.9) * mm});
            skLineSegment(sketch, "E3023", {"start": v(-2.54, 10.9) * mm, "end": v(-1.98, 10.9) * mm});
            skArc(sketch, "E3024", {"start": v(-1.98, 10.9) * mm, "mid": v(-1.94, 10.92) * mm, "end": v(-1.92, 10.96) * mm});
            skLineSegment(sketch, "E3025", {"start": v(3.2, 7.6) * mm, "end": v(3.2, 6.98) * mm});
            skArc(sketch, "E3026", {"start": v(3.2, 6.98) * mm, "mid": v(3.22, 6.93) * mm, "end": v(3.27, 6.9) * mm});
            skLineSegment(sketch, "E3027", {"start": v(3.27, 6.9) * mm, "end": v(4.1, 6.9) * mm});
            skArc(sketch, "E3028", {"start": v(4.1, 6.9) * mm, "mid": v(4.15, 6.93) * mm, "end": v(4.17, 6.98) * mm});
            skLineSegment(sketch, "E3029", {"start": v(4.17, 6.98) * mm, "end": v(4.17, 7.6) * mm});
            skArc(sketch, "E3030", {"start": v(4.17, 7.6) * mm, "mid": v(4.15, 7.65) * mm, "end": v(4.1, 7.67) * mm});
            skLineSegment(sketch, "E3031", {"start": v(4.1, 7.67) * mm, "end": v(3.27, 7.67) * mm});
            skArc(sketch, "E3032", {"start": v(3.27, 7.67) * mm, "mid": v(3.22, 7.65) * mm, "end": v(3.2, 7.6) * mm});
            skLineSegment(sketch, "E3033", {"start": v(3.19, 11.04) * mm, "end": v(3.19, 10.55) * mm});
            skArc(sketch, "E3034", {"start": v(3.19, 10.55) * mm, "mid": v(3.2, 10.5) * mm, "end": v(3.24, 10.5) * mm});
            skLineSegment(sketch, "E3035", {"start": v(3.24, 10.5) * mm, "end": v(4.13, 10.5) * mm});
            skArc(sketch, "E3036", {"start": v(4.13, 10.5) * mm, "mid": v(4.17, 10.5) * mm, "end": v(4.19, 10.55) * mm});
            skLineSegment(sketch, "E3037", {"start": v(4.19, 10.55) * mm, "end": v(4.19, 11.04) * mm});
            skArc(sketch, "E3038", {"start": v(4.19, 11.04) * mm, "mid": v(4.17, 11.07) * mm, "end": v(4.13, 11.09) * mm});
            skLineSegment(sketch, "E3039", {"start": v(4.13, 11.09) * mm, "end": v(3.24, 11.09) * mm});
            skArc(sketch, "E3040", {"start": v(3.24, 11.09) * mm, "mid": v(3.2, 11.07) * mm, "end": v(3.19, 11.04) * mm});
            skLineSegment(sketch, "E3041", {"start": v(-4.2, 7.6) * mm, "end": v(-4.2, 6.98) * mm});
            skArc(sketch, "E3042", {"start": v(-4.2, 6.98) * mm, "mid": v(-4.18, 6.93) * mm, "end": v(-4.13, 6.9) * mm});
            skLineSegment(sketch, "E3043", {"start": v(-4.13, 6.9) * mm, "end": v(-3.3, 6.9) * mm});
            skArc(sketch, "E3044", {"start": v(-3.3, 6.9) * mm, "mid": v(-3.25, 6.93) * mm, "end": v(-3.23, 6.98) * mm});
            skLineSegment(sketch, "E3045", {"start": v(-3.23, 6.98) * mm, "end": v(-3.23, 7.6) * mm});
            skArc(sketch, "E3046", {"start": v(-3.23, 7.6) * mm, "mid": v(-3.25, 7.65) * mm, "end": v(-3.3, 7.67) * mm});
            skLineSegment(sketch, "E3047", {"start": v(-3.3, 7.67) * mm, "end": v(-4.13, 7.67) * mm});
            skArc(sketch, "E3048", {"start": v(-4.13, 7.67) * mm, "mid": v(-4.18, 7.65) * mm, "end": v(-4.2, 7.6) * mm});
            skLineSegment(sketch, "E3049", {"start": v(-4.21, 11.04) * mm, "end": v(-4.21, 10.55) * mm});
            skArc(sketch, "E3050", {"start": v(-4.21, 10.55) * mm, "mid": v(-4.2, 10.5) * mm, "end": v(-4.16, 10.5) * mm});
            skLineSegment(sketch, "E3051", {"start": v(-4.16, 10.5) * mm, "end": v(-3.27, 10.5) * mm});
            skArc(sketch, "E3052", {"start": v(-3.27, 10.5) * mm, "mid": v(-3.23, 10.5) * mm, "end": v(-3.21, 10.55) * mm});
            skLineSegment(sketch, "E3053", {"start": v(-3.21, 10.55) * mm, "end": v(-3.21, 11.04) * mm});
            skArc(sketch, "E3054", {"start": v(-3.21, 11.04) * mm, "mid": v(-3.23, 11.07) * mm, "end": v(-3.27, 11.09) * mm});
            skLineSegment(sketch, "E3055", {"start": v(-3.27, 11.09) * mm, "end": v(-4.16, 11.09) * mm});
            skArc(sketch, "E3056", {"start": v(-4.16, 11.09) * mm, "mid": v(-4.2, 11.07) * mm, "end": v(-4.21, 11.04) * mm});
            skLineSegment(sketch, "E3057", {"start": v(-1.48, -12.76) * mm, "end": v(-1.48, -14.14) * mm});
            skArc(sketch, "E3058", {"start": v(-1.48, -14.14) * mm, "mid": v(-1.46, -14.18) * mm, "end": v(-1.42, -14.2) * mm});
            skLineSegment(sketch, "E3059", {"start": v(-1.42, -14.2) * mm, "end": v(-1.18, -14.2) * mm});
            skArc(sketch, "E3060", {"start": v(-1.18, -14.2) * mm, "mid": v(-1.14, -14.18) * mm, "end": v(-1.12, -14.14) * mm});
            skLineSegment(sketch, "E3061", {"start": v(-1.12, -14.14) * mm, "end": v(-1.12, -12.76) * mm});
            skArc(sketch, "E3062", {"start": v(-1.12, -12.76) * mm, "mid": v(-1.14, -12.71) * mm, "end": v(-1.18, -12.7) * mm});
            skLineSegment(sketch, "E3063", {"start": v(-1.18, -12.7) * mm, "end": v(-1.42, -12.7) * mm});
            skArc(sketch, "E3064", {"start": v(-1.42, -12.7) * mm, "mid": v(-1.46, -12.71) * mm, "end": v(-1.48, -12.76) * mm});
            skLineSegment(sketch, "E3065", {"start": v(-0.83, -12.76) * mm, "end": v(-0.83, -14.14) * mm});
            skArc(sketch, "E3066", {"start": v(-0.83, -14.14) * mm, "mid": v(-0.81, -14.18) * mm, "end": v(-0.77, -14.2) * mm});
            skLineSegment(sketch, "E3067", {"start": v(-0.77, -14.2) * mm, "end": v(-0.53, -14.2) * mm});
            skArc(sketch, "E3068", {"start": v(-0.53, -14.2) * mm, "mid": v(-0.49, -14.18) * mm, "end": v(-0.47, -14.14) * mm});
            skLineSegment(sketch, "E3069", {"start": v(-0.47, -14.14) * mm, "end": v(-0.47, -12.76) * mm});
            skArc(sketch, "E3070", {"start": v(-0.47, -12.76) * mm, "mid": v(-0.49, -12.71) * mm, "end": v(-0.53, -12.7) * mm});
            skLineSegment(sketch, "E3071", {"start": v(-0.53, -12.7) * mm, "end": v(-0.77, -12.7) * mm});
            skArc(sketch, "E3072", {"start": v(-0.77, -12.7) * mm, "mid": v(-0.81, -12.71) * mm, "end": v(-0.83, -12.76) * mm});
            skLineSegment(sketch, "E3073", {"start": v(-0.18, -12.76) * mm, "end": v(-0.18, -14.14) * mm});
            skArc(sketch, "E3074", {"start": v(-0.18, -14.14) * mm, "mid": v(-0.16, -14.18) * mm, "end": v(-0.12, -14.2) * mm});
            skLineSegment(sketch, "E3075", {"start": v(-0.12, -14.2) * mm, "end": v(0.12, -14.2) * mm});
            skArc(sketch, "E3076", {"start": v(0.12, -14.2) * mm, "mid": v(0.16, -14.18) * mm, "end": v(0.18, -14.14) * mm});
            skLineSegment(sketch, "E3077", {"start": v(0.18, -14.14) * mm, "end": v(0.18, -12.76) * mm});
            skArc(sketch, "E3078", {"start": v(0.18, -12.76) * mm, "mid": v(0.16, -12.71) * mm, "end": v(0.12, -12.7) * mm});
            skLineSegment(sketch, "E3079", {"start": v(0.12, -12.7) * mm, "end": v(-0.12, -12.7) * mm});
            skArc(sketch, "E3080", {"start": v(-0.12, -12.7) * mm, "mid": v(-0.16, -12.71) * mm, "end": v(-0.18, -12.76) * mm});
            skLineSegment(sketch, "E3081", {"start": v(0.47, -12.76) * mm, "end": v(0.47, -14.14) * mm});
            skArc(sketch, "E3082", {"start": v(0.47, -14.14) * mm, "mid": v(0.49, -14.18) * mm, "end": v(0.53, -14.2) * mm});
            skLineSegment(sketch, "E3083", {"start": v(0.53, -14.2) * mm, "end": v(0.77, -14.2) * mm});
            skArc(sketch, "E3084", {"start": v(0.77, -14.2) * mm, "mid": v(0.81, -14.18) * mm, "end": v(0.83, -14.14) * mm});
            skLineSegment(sketch, "E3085", {"start": v(0.83, -14.14) * mm, "end": v(0.83, -12.76) * mm});
            skArc(sketch, "E3086", {"start": v(0.83, -12.76) * mm, "mid": v(0.81, -12.71) * mm, "end": v(0.77, -12.7) * mm});
            skLineSegment(sketch, "E3087", {"start": v(0.77, -12.7) * mm, "end": v(0.53, -12.7) * mm});
            skArc(sketch, "E3088", {"start": v(0.53, -12.7) * mm, "mid": v(0.49, -12.71) * mm, "end": v(0.47, -12.76) * mm});
            skLineSegment(sketch, "E3089", {"start": v(1.12, -12.76) * mm, "end": v(1.12, -14.14) * mm});
            skArc(sketch, "E3090", {"start": v(1.12, -14.14) * mm, "mid": v(1.14, -14.18) * mm, "end": v(1.18, -14.2) * mm});
            skLineSegment(sketch, "E3091", {"start": v(1.18, -14.2) * mm, "end": v(1.42, -14.2) * mm});
            skArc(sketch, "E3092", {"start": v(1.42, -14.2) * mm, "mid": v(1.46, -14.18) * mm, "end": v(1.48, -14.14) * mm});
            skLineSegment(sketch, "E3093", {"start": v(1.48, -14.14) * mm, "end": v(1.48, -12.76) * mm});
            skArc(sketch, "E3094", {"start": v(1.48, -12.76) * mm, "mid": v(1.46, -12.71) * mm, "end": v(1.42, -12.7) * mm});
            skLineSegment(sketch, "E3095", {"start": v(1.42, -12.7) * mm, "end": v(1.18, -12.7) * mm});
            skArc(sketch, "E3096", {"start": v(1.18, -12.7) * mm, "mid": v(1.14, -12.71) * mm, "end": v(1.12, -12.76) * mm});
            skLineSegment(sketch, "E3097", {"start": v(-2.92, -13.06) * mm, "end": v(-3.88, -13.06) * mm});
            skArc(sketch, "E3098", {"start": v(-3.88, -13.06) * mm, "mid": v(-4, -13.12) * mm, "end": v(-4.06, -13.25) * mm});
            skLineSegment(sketch, "E3099", {"start": v(-4.06, -13.25) * mm, "end": v(-4.06, -14) * mm});
            skArc(sketch, "E3100", {"start": v(-4.06, -14) * mm, "mid": v(-4, -14.13) * mm, "end": v(-3.88, -14.19) * mm});
            skLineSegment(sketch, "E3101", {"start": v(-3.88, -14.19) * mm, "end": v(-2.92, -14.19) * mm});
            skArc(sketch, "E3102", {"start": v(-2.92, -14.19) * mm, "mid": v(-2.8, -14.13) * mm, "end": v(-2.74, -14) * mm});
            skLineSegment(sketch, "E3103", {"start": v(-2.74, -14) * mm, "end": v(-2.74, -13.25) * mm});
            skArc(sketch, "E3104", {"start": v(-2.74, -13.25) * mm, "mid": v(-2.8, -13.12) * mm, "end": v(-2.92, -13.06) * mm});
            skLineSegment(sketch, "E3105", {"start": v(-3.23, -16.93) * mm, "end": v(-3.23, -15.81) * mm});
            skArc(sketch, "E3106", {"start": v(-2.98, -15.81) * mm, "mid": v(-3.23, -15.56) * mm, "end": v(-3.48, -15.81) * mm});
            skArc(sketch, "E3107", {"start": v(-3.48, -16.93) * mm, "mid": v(-3.23, -17.18) * mm, "end": v(-2.98, -16.93) * mm});
            skLineSegment(sketch, "E3108", {"start": v(-0.4, -17.1) * mm, "end": v(-0.4, -16.3) * mm});
            skArc(sketch, "E3109", {"start": v(-0.4, -16.3) * mm, "mid": v(-0.46, -16.16) * mm, "end": v(-0.6, -16.1) * mm});
            skLineSegment(sketch, "E3110", {"start": v(-0.6, -16.1) * mm, "end": v(-1.4, -16.1) * mm});
            skArc(sketch, "E3111", {"start": v(-1.4, -16.1) * mm, "mid": v(-1.54, -16.16) * mm, "end": v(-1.6, -16.3) * mm});
            skLineSegment(sketch, "E3112", {"start": v(-1.6, -16.3) * mm, "end": v(-1.6, -17.1) * mm});
            skArc(sketch, "E3113", {"start": v(-1.6, -17.1) * mm, "mid": v(-1.54, -17.24) * mm, "end": v(-1.4, -17.3) * mm});
            skLineSegment(sketch, "E3114", {"start": v(-1.4, -17.3) * mm, "end": v(-0.6, -17.3) * mm});
            skArc(sketch, "E3115", {"start": v(-0.6, -17.3) * mm, "mid": v(-0.46, -17.24) * mm, "end": v(-0.4, -17.1) * mm});
            skLineSegment(sketch, "E3116", {"start": v(1.6, -17.1) * mm, "end": v(1.6, -16.3) * mm});
            skArc(sketch, "E3117", {"start": v(1.6, -16.3) * mm, "mid": v(1.54, -16.16) * mm, "end": v(1.4, -16.1) * mm});
            skLineSegment(sketch, "E3118", {"start": v(1.4, -16.1) * mm, "end": v(0.6, -16.1) * mm});
            skArc(sketch, "E3119", {"start": v(0.6, -16.1) * mm, "mid": v(0.46, -16.16) * mm, "end": v(0.4, -16.3) * mm});
            skLineSegment(sketch, "E3120", {"start": v(0.4, -16.3) * mm, "end": v(0.4, -17.1) * mm});
            skArc(sketch, "E3121", {"start": v(0.4, -17.1) * mm, "mid": v(0.46, -17.24) * mm, "end": v(0.6, -17.3) * mm});
            skLineSegment(sketch, "E3122", {"start": v(0.6, -17.3) * mm, "end": v(1.4, -17.3) * mm});
            skArc(sketch, "E3123", {"start": v(1.4, -17.3) * mm, "mid": v(1.54, -17.24) * mm, "end": v(1.6, -17.1) * mm});
            skLineSegment(sketch, "E3124", {"start": v(3.23, -16.93) * mm, "end": v(3.23, -15.81) * mm});
            skArc(sketch, "E3125", {"start": v(3.48, -15.81) * mm, "mid": v(3.23, -15.56) * mm, "end": v(2.98, -15.81) * mm});
            skArc(sketch, "E3126", {"start": v(2.98, -16.93) * mm, "mid": v(3.23, -17.18) * mm, "end": v(3.48, -16.93) * mm});
            skLineSegment(sketch, "E3127", {"start": v(3.88, -13.06) * mm, "end": v(2.92, -13.06) * mm});
            skArc(sketch, "E3128", {"start": v(2.92, -13.06) * mm, "mid": v(2.8, -13.12) * mm, "end": v(2.74, -13.25) * mm});
            skLineSegment(sketch, "E3129", {"start": v(2.74, -13.25) * mm, "end": v(2.74, -14) * mm});
            skArc(sketch, "E3130", {"start": v(2.74, -14) * mm, "mid": v(2.8, -14.13) * mm, "end": v(2.92, -14.19) * mm});
            skLineSegment(sketch, "E3131", {"start": v(2.92, -14.19) * mm, "end": v(3.88, -14.19) * mm});
            skArc(sketch, "E3132", {"start": v(3.88, -14.19) * mm, "mid": v(4, -14.13) * mm, "end": v(4.06, -14) * mm});
            skLineSegment(sketch, "E3133", {"start": v(4.06, -14) * mm, "end": v(4.06, -13.25) * mm});
            skArc(sketch, "E3134", {"start": v(4.06, -13.25) * mm, "mid": v(4, -13.12) * mm, "end": v(3.88, -13.06) * mm});
            skLineSegment(sketch, "E3135", {"start": v(0.86, -6.42) * mm, "end": v(0.86, -7.98) * mm});
            skArc(sketch, "E3136", {"start": v(0.86, -7.98) * mm, "mid": v(0.88, -8.02) * mm, "end": v(0.92, -8.04) * mm});
            skLineSegment(sketch, "E3137", {"start": v(0.92, -8.04) * mm, "end": v(1.48, -8.04) * mm});
            skArc(sketch, "E3138", {"start": v(1.48, -8.04) * mm, "mid": v(1.52, -8.02) * mm, "end": v(1.54, -7.98) * mm});
            skLineSegment(sketch, "E3139", {"start": v(1.54, -7.98) * mm, "end": v(1.54, -6.42) * mm});
            skArc(sketch, "E3140", {"start": v(1.54, -6.42) * mm, "mid": v(1.52, -6.37) * mm, "end": v(1.48, -6.36) * mm});
            skLineSegment(sketch, "E3141", {"start": v(1.48, -6.36) * mm, "end": v(0.92, -6.36) * mm});
            skArc(sketch, "E3142", {"start": v(0.92, -6.36) * mm, "mid": v(0.88, -6.37) * mm, "end": v(0.86, -6.42) * mm});
            skLineSegment(sketch, "E3143", {"start": v(-0.34, -6.42) * mm, "end": v(-0.34, -7.98) * mm});
            skArc(sketch, "E3144", {"start": v(-0.34, -7.98) * mm, "mid": v(-0.32, -8.02) * mm, "end": v(-0.28, -8.04) * mm});
            skLineSegment(sketch, "E3145", {"start": v(-0.28, -8.04) * mm, "end": v(0.28, -8.04) * mm});
            skArc(sketch, "E3146", {"start": v(0.28, -8.04) * mm, "mid": v(0.32, -8.02) * mm, "end": v(0.34, -7.98) * mm});
            skLineSegment(sketch, "E3147", {"start": v(0.34, -7.98) * mm, "end": v(0.34, -6.42) * mm});
            skArc(sketch, "E3148", {"start": v(0.34, -6.42) * mm, "mid": v(0.32, -6.37) * mm, "end": v(0.28, -6.36) * mm});
            skLineSegment(sketch, "E3149", {"start": v(0.28, -6.36) * mm, "end": v(-0.28, -6.36) * mm});
            skArc(sketch, "E3150", {"start": v(-0.28, -6.36) * mm, "mid": v(-0.32, -6.37) * mm, "end": v(-0.34, -6.42) * mm});
            skLineSegment(sketch, "E3151", {"start": v(-1.54, -6.42) * mm, "end": v(-1.54, -7.98) * mm});
            skArc(sketch, "E3152", {"start": v(-1.54, -7.98) * mm, "mid": v(-1.52, -8.02) * mm, "end": v(-1.48, -8.04) * mm});
            skLineSegment(sketch, "E3153", {"start": v(-1.48, -8.04) * mm, "end": v(-0.92, -8.04) * mm});
            skArc(sketch, "E3154", {"start": v(-0.92, -8.04) * mm, "mid": v(-0.88, -8.02) * mm, "end": v(-0.86, -7.98) * mm});
            skLineSegment(sketch, "E3155", {"start": v(-0.86, -7.98) * mm, "end": v(-0.86, -6.42) * mm});
            skArc(sketch, "E3156", {"start": v(-0.86, -6.42) * mm, "mid": v(-0.88, -6.37) * mm, "end": v(-0.92, -6.36) * mm});
            skLineSegment(sketch, "E3157", {"start": v(-0.92, -6.36) * mm, "end": v(-1.48, -6.36) * mm});
            skArc(sketch, "E3158", {"start": v(-1.48, -6.36) * mm, "mid": v(-1.52, -6.37) * mm, "end": v(-1.54, -6.42) * mm});
            skArc(sketch, "E3159", {"start": v(-5.6, -0.65) * mm, "mid": v(-5.35, -0.4) * mm, "end": v(-5.6, -0.15) * mm});
            skArc(sketch, "E3160", {"start": v(-5.6, -0.15) * mm, "mid": v(-5.85, -0.4) * mm, "end": v(-5.6, -0.65) * mm});
            skArc(sketch, "E3161", {"start": v(-5.6, -10.55) * mm, "mid": v(-5.35, -10.3) * mm, "end": v(-5.6, -10.05) * mm});
            skArc(sketch, "E3162", {"start": v(-5.6, -10.05) * mm, "mid": v(-5.85, -10.3) * mm, "end": v(-5.6, -10.55) * mm});
            skArc(sketch, "E3163", {"start": v(-5.6, -11.75) * mm, "mid": v(-5.35, -11.5) * mm, "end": v(-5.6, -11.25) * mm});
            skArc(sketch, "E3164", {"start": v(-5.6, -11.25) * mm, "mid": v(-5.85, -11.5) * mm, "end": v(-5.6, -11.75) * mm});
            skArc(sketch, "E3165", {"start": v(-4.5, -0.35) * mm, "mid": v(-4.25, -0.1) * mm, "end": v(-4.5, 0.15) * mm});
            skArc(sketch, "E3166", {"start": v(-4.5, 0.15) * mm, "mid": v(-4.75, -0.1) * mm, "end": v(-4.5, -0.35) * mm});
            skArc(sketch, "E3167", {"start": v(13.5, -2.75) * mm, "mid": v(13.75, -2.5) * mm, "end": v(13.5, -2.25) * mm});
            skArc(sketch, "E3168", {"start": v(13.5, -2.25) * mm, "mid": v(13.25, -2.5) * mm, "end": v(13.5, -2.75) * mm});
            skArc(sketch, "E3169", {"start": v(-13.4, -2.75) * mm, "mid": v(-13.15, -2.5) * mm, "end": v(-13.4, -2.25) * mm});
            skArc(sketch, "E3170", {"start": v(-13.4, -2.25) * mm, "mid": v(-13.65, -2.5) * mm, "end": v(-13.4, -2.75) * mm});
            skArc(sketch, "E3171", {"start": v(-12.3, -5.05) * mm, "mid": v(-12.05, -4.8) * mm, "end": v(-12.3, -4.55) * mm});
            skArc(sketch, "E3172", {"start": v(-12.3, -4.55) * mm, "mid": v(-12.55, -4.8) * mm, "end": v(-12.3, -5.05) * mm});
            skArc(sketch, "E3173", {"start": v(-2.38, -0.94) * mm, "mid": v(-2.13, -0.69) * mm, "end": v(-2.38, -0.44) * mm});
            skArc(sketch, "E3174", {"start": v(-2.38, -0.44) * mm, "mid": v(-2.63, -0.69) * mm, "end": v(-2.38, -0.94) * mm});
            skArc(sketch, "E3175", {"start": v(3.6, -6.75) * mm, "mid": v(3.85, -6.5) * mm, "end": v(3.6, -6.25) * mm});
            skArc(sketch, "E3176", {"start": v(3.6, -6.25) * mm, "mid": v(3.35, -6.5) * mm, "end": v(3.6, -6.75) * mm});
            skArc(sketch, "E3177", {"start": v(-3.45, 1.91) * mm, "mid": v(-3.2, 2.16) * mm, "end": v(-3.45, 2.41) * mm});
            skArc(sketch, "E3178", {"start": v(-3.45, 2.41) * mm, "mid": v(-3.7, 2.16) * mm, "end": v(-3.45, 1.91) * mm});
            skArc(sketch, "E3179", {"start": v(-6.8, -0.95) * mm, "mid": v(-6.55, -0.7) * mm, "end": v(-6.8, -0.45) * mm});
            skArc(sketch, "E3180", {"start": v(-6.8, -0.45) * mm, "mid": v(-7.05, -0.7) * mm, "end": v(-6.8, -0.95) * mm});
            skArc(sketch, "E3181", {"start": v(10.1, -8.45) * mm, "mid": v(10.35, -8.2) * mm, "end": v(10.1, -7.95) * mm});
            skArc(sketch, "E3182", {"start": v(10.1, -7.95) * mm, "mid": v(9.85, -8.2) * mm, "end": v(10.1, -8.45) * mm});
            skArc(sketch, "E3183", {"start": v(-9, 7.85) * mm, "mid": v(-8.75, 8.1) * mm, "end": v(-9, 8.35) * mm});
            skArc(sketch, "E3184", {"start": v(-9, 8.35) * mm, "mid": v(-9.25, 8.1) * mm, "end": v(-9, 7.85) * mm});
            skArc(sketch, "E3185", {"start": v(-10, -8.65) * mm, "mid": v(-9.75, -8.4) * mm, "end": v(-10, -8.15) * mm});
            skArc(sketch, "E3186", {"start": v(-10, -8.15) * mm, "mid": v(-10.25, -8.4) * mm, "end": v(-10, -8.65) * mm});
            skArc(sketch, "E3187", {"start": v(8.6, -9.9) * mm, "mid": v(8.85, -9.65) * mm, "end": v(8.6, -9.4) * mm});
            skArc(sketch, "E3188", {"start": v(8.6, -9.4) * mm, "mid": v(8.35, -9.65) * mm, "end": v(8.6, -9.9) * mm});
            skArc(sketch, "E3189", {"start": v(10.6, -6.35) * mm, "mid": v(10.85, -6.1) * mm, "end": v(10.6, -5.85) * mm});
            skArc(sketch, "E3190", {"start": v(10.6, -5.85) * mm, "mid": v(10.35, -6.1) * mm, "end": v(10.6, -6.35) * mm});
            skArc(sketch, "E3191", {"start": v(0.96, -2.22) * mm, "mid": v(1.2, -1.97) * mm, "end": v(0.96, -1.72) * mm});
            skArc(sketch, "E3192", {"start": v(0.96, -1.72) * mm, "mid": v(0.7, -1.97) * mm, "end": v(0.96, -2.22) * mm});
            skArc(sketch, "E3193", {"start": v(-0.24, -0.23) * mm, "mid": v(0, 0.02) * mm, "end": v(-0.24, 0.27) * mm});
            skArc(sketch, "E3194", {"start": v(-0.24, 0.27) * mm, "mid": v(-0.5, 0.02) * mm, "end": v(-0.24, -0.23) * mm});
            skArc(sketch, "E3195", {"start": v(-1.25, -2.14) * mm, "mid": v(-1, -1.89) * mm, "end": v(-1.25, -1.64) * mm});
            skArc(sketch, "E3196", {"start": v(-1.25, -1.64) * mm, "mid": v(-1.5, -1.89) * mm, "end": v(-1.25, -2.14) * mm});
            skArc(sketch, "E3197", {"start": v(-4.94, -13.4) * mm, "mid": v(-4.7, -13.14) * mm, "end": v(-4.94, -12.9) * mm});
            skArc(sketch, "E3198", {"start": v(-4.94, -12.9) * mm, "mid": v(-5.2, -13.14) * mm, "end": v(-4.94, -13.4) * mm});
            skArc(sketch, "E3199", {"start": v(4.95, -13.41) * mm, "mid": v(5.2, -13.16) * mm, "end": v(4.95, -12.91) * mm});
            skArc(sketch, "E3200", {"start": v(4.95, -12.91) * mm, "mid": v(4.7, -13.16) * mm, "end": v(4.95, -13.41) * mm});
            skArc(sketch, "E3201", {"start": v(-1.07, -9.25) * mm, "mid": v(-0.82, -9) * mm, "end": v(-1.07, -8.75) * mm});
            skArc(sketch, "E3202", {"start": v(-1.07, -8.75) * mm, "mid": v(-1.32, -9) * mm, "end": v(-1.07, -9.25) * mm});
            skArc(sketch, "E3203", {"start": v(2.3, -8.49) * mm, "mid": v(2.54, -8.24) * mm, "end": v(2.3, -7.99) * mm});
            skArc(sketch, "E3204", {"start": v(2.3, -7.99) * mm, "mid": v(2.04, -8.24) * mm, "end": v(2.3, -8.49) * mm});
            skArc(sketch, "E3205", {"start": v(-2.2, -15.55) * mm, "mid": v(-1.95, -15.3) * mm, "end": v(-2.2, -15.05) * mm});
            skArc(sketch, "E3206", {"start": v(-2.2, -15.05) * mm, "mid": v(-2.45, -15.3) * mm, "end": v(-2.2, -15.55) * mm});
            skArc(sketch, "E3207", {"start": v(2.2, -15.55) * mm, "mid": v(2.45, -15.3) * mm, "end": v(2.2, -15.05) * mm});
            skArc(sketch, "E3208", {"start": v(2.2, -15.05) * mm, "mid": v(1.95, -15.3) * mm, "end": v(2.2, -15.55) * mm});
            skArc(sketch, "E3209", {"start": v(1.15, 10.65) * mm, "mid": v(1.4, 10.9) * mm, "end": v(1.15, 11.15) * mm});
            skArc(sketch, "E3210", {"start": v(1.15, 11.15) * mm, "mid": v(0.9, 10.9) * mm, "end": v(1.15, 10.65) * mm});
            skArc(sketch, "E3211", {"start": v(2.93, 6.02) * mm, "mid": v(3.18, 6.27) * mm, "end": v(2.93, 6.52) * mm});
            skArc(sketch, "E3212", {"start": v(2.93, 6.52) * mm, "mid": v(2.68, 6.27) * mm, "end": v(2.93, 6.02) * mm});
            skArc(sketch, "E3213", {"start": v(-9.9, -6.55) * mm, "mid": v(-9.65, -6.3) * mm, "end": v(-9.9, -6.05) * mm});
            skArc(sketch, "E3214", {"start": v(-9.9, -6.05) * mm, "mid": v(-10.15, -6.3) * mm, "end": v(-9.9, -6.55) * mm});
            skArc(sketch, "E3215", {"start": v(-8.5, -4.75) * mm, "mid": v(-8.25, -4.5) * mm, "end": v(-8.5, -4.25) * mm});
            skArc(sketch, "E3216", {"start": v(-8.5, -4.25) * mm, "mid": v(-8.75, -4.5) * mm, "end": v(-8.5, -4.75) * mm});
            skArc(sketch, "E3217", {"start": v(10.1, 3.55) * mm, "mid": v(10.35, 3.8) * mm, "end": v(10.1, 4.05) * mm});
            skArc(sketch, "E3218", {"start": v(10.1, 4.05) * mm, "mid": v(9.85, 3.8) * mm, "end": v(10.1, 3.55) * mm});
            skArc(sketch, "E3219", {"start": v(8.09, -11.76) * mm, "mid": v(8.34, -11.5) * mm, "end": v(8.09, -11.26) * mm});
            skArc(sketch, "E3220", {"start": v(8.09, -11.26) * mm, "mid": v(7.84, -11.5) * mm, "end": v(8.09, -11.76) * mm});
            skArc(sketch, "E3221", {"start": v(-8.05, -11.76) * mm, "mid": v(-7.8, -11.5) * mm, "end": v(-8.05, -11.26) * mm});
            skArc(sketch, "E3222", {"start": v(-8.05, -11.26) * mm, "mid": v(-8.3, -11.5) * mm, "end": v(-8.05, -11.76) * mm});
            skArc(sketch, "E3223", {"start": v(-11, 0.97) * mm, "mid": v(-10.74, 1.22) * mm, "end": v(-11, 1.47) * mm});
            skArc(sketch, "E3224", {"start": v(-11, 1.47) * mm, "mid": v(-11.24, 1.22) * mm, "end": v(-11, 0.97) * mm});
            skArc(sketch, "E3225", {"start": v(-4.4, 9.63) * mm, "mid": v(-4.14, 9.88) * mm, "end": v(-4.4, 10.13) * mm});
            skArc(sketch, "E3226", {"start": v(-4.4, 10.13) * mm, "mid": v(-4.64, 9.88) * mm, "end": v(-4.4, 9.63) * mm});
            skArc(sketch, "E3227", {"start": v(2.22, -1.16) * mm, "mid": v(2.47, -0.9) * mm, "end": v(2.22, -0.66) * mm});
            skArc(sketch, "E3228", {"start": v(2.22, -0.66) * mm, "mid": v(1.97, -0.9) * mm, "end": v(2.22, -1.16) * mm});
            skArc(sketch, "E3229", {"start": v(5.72, 4.94) * mm, "mid": v(5.97, 5.19) * mm, "end": v(5.72, 5.44) * mm});
            skArc(sketch, "E3230", {"start": v(5.72, 5.44) * mm, "mid": v(5.47, 5.19) * mm, "end": v(5.72, 4.94) * mm});
            skArc(sketch, "E3231", {"start": v(1.3, -10.1) * mm, "mid": v(1.55, -9.84) * mm, "end": v(1.3, -9.6) * mm});
            skArc(sketch, "E3232", {"start": v(1.3, -9.6) * mm, "mid": v(1.05, -9.84) * mm, "end": v(1.3, -10.1) * mm});
            skArc(sketch, "E3233", {"start": v(-2.33, 7.2) * mm, "mid": v(-2.08, 7.45) * mm, "end": v(-2.33, 7.7) * mm});
            skArc(sketch, "E3234", {"start": v(-2.33, 7.7) * mm, "mid": v(-2.58, 7.45) * mm, "end": v(-2.33, 7.2) * mm});
            skArc(sketch, "E3235", {"start": v(-2.6, 8.27) * mm, "mid": v(-2.35, 8.52) * mm, "end": v(-2.6, 8.77) * mm});
            skArc(sketch, "E3236", {"start": v(-2.6, 8.77) * mm, "mid": v(-2.85, 8.52) * mm, "end": v(-2.6, 8.27) * mm});
            skArc(sketch, "E3237", {"start": v(-1.27, 2.3) * mm, "mid": v(-1.02, 2.54) * mm, "end": v(-1.27, 2.8) * mm});
            skArc(sketch, "E3238", {"start": v(-1.27, 2.8) * mm, "mid": v(-1.52, 2.54) * mm, "end": v(-1.27, 2.3) * mm});
            skArc(sketch, "E3239", {"start": v(-8.63, -0.99) * mm, "mid": v(-8.38, -0.74) * mm, "end": v(-8.63, -0.49) * mm});
            skArc(sketch, "E3240", {"start": v(-8.63, -0.49) * mm, "mid": v(-8.88, -0.74) * mm, "end": v(-8.63, -0.99) * mm});
            skArc(sketch, "E3241", {"start": v(-5.84, -5.99) * mm, "mid": v(-5.6, -5.74) * mm, "end": v(-5.84, -5.49) * mm});
            skArc(sketch, "E3242", {"start": v(-5.84, -5.49) * mm, "mid": v(-6.1, -5.74) * mm, "end": v(-5.84, -5.99) * mm});
            skArc(sketch, "E3243", {"start": v(-3, -11.75) * mm, "mid": v(-2.75, -11.5) * mm, "end": v(-3, -11.25) * mm});
            skArc(sketch, "E3244", {"start": v(-3, -11.25) * mm, "mid": v(-3.25, -11.5) * mm, "end": v(-3, -11.75) * mm});
            skArc(sketch, "E3245", {"start": v(0, -15.15) * mm, "mid": v(0.25, -14.9) * mm, "end": v(0, -14.65) * mm});
            skArc(sketch, "E3246", {"start": v(0, -14.65) * mm, "mid": v(-0.25, -14.9) * mm, "end": v(0, -15.15) * mm});
            skArc(sketch, "E3247", {"start": v(4.4, 1.7) * mm, "mid": v(4.65, 1.95) * mm, "end": v(4.4, 2.2) * mm});
            skArc(sketch, "E3248", {"start": v(4.4, 2.2) * mm, "mid": v(4.15, 1.95) * mm, "end": v(4.4, 1.7) * mm});
            skArc(sketch, "E3249", {"start": v(4.13, 3.8) * mm, "mid": v(4.38, 4.05) * mm, "end": v(4.13, 4.3) * mm});
            skArc(sketch, "E3250", {"start": v(4.13, 4.3) * mm, "mid": v(3.88, 4.05) * mm, "end": v(4.13, 3.8) * mm});
            skArc(sketch, "E3251", {"start": v(-10.57, 4.14) * mm, "mid": v(-10.32, 4.4) * mm, "end": v(-10.57, 4.64) * mm});
            skArc(sketch, "E3252", {"start": v(-10.57, 4.64) * mm, "mid": v(-10.82, 4.4) * mm, "end": v(-10.57, 4.14) * mm});
            skArc(sketch, "E3253", {"start": v(4.24, 5.99) * mm, "mid": v(4.5, 6.24) * mm, "end": v(4.24, 6.49) * mm});
            skArc(sketch, "E3254", {"start": v(4.24, 6.49) * mm, "mid": v(4, 6.24) * mm, "end": v(4.24, 5.99) * mm});
            skArc(sketch, "E3255", {"start": v(6.4, 1.65) * mm, "mid": v(6.65, 1.9) * mm, "end": v(6.4, 2.15) * mm});
            skArc(sketch, "E3256", {"start": v(6.4, 2.15) * mm, "mid": v(6.15, 1.9) * mm, "end": v(6.4, 1.65) * mm});
            skArc(sketch, "E3257", {"start": v(11.2, 4.8) * mm, "mid": v(11.45, 5.04) * mm, "end": v(11.2, 5.3) * mm});
            skArc(sketch, "E3258", {"start": v(11.2, 5.3) * mm, "mid": v(10.95, 5.04) * mm, "end": v(11.2, 4.8) * mm});
            skArc(sketch, "E3259", {"start": v(3.4, 1.25) * mm, "mid": v(3.65, 1.5) * mm, "end": v(3.4, 1.75) * mm});
            skArc(sketch, "E3260", {"start": v(3.4, 1.75) * mm, "mid": v(3.15, 1.5) * mm, "end": v(3.4, 1.25) * mm});
            skArc(sketch, "E3261", {"start": v(3.06, 3.76) * mm, "mid": v(3.31, 4) * mm, "end": v(3.06, 4.26) * mm});
            skArc(sketch, "E3262", {"start": v(3.06, 4.26) * mm, "mid": v(2.81, 4) * mm, "end": v(3.06, 3.76) * mm});
            skArc(sketch, "E3263", {"start": v(9.23, -2.53) * mm, "mid": v(9.48, -2.28) * mm, "end": v(9.23, -2.03) * mm});
            skArc(sketch, "E3264", {"start": v(9.23, -2.03) * mm, "mid": v(8.98, -2.28) * mm, "end": v(9.23, -2.53) * mm});
            skArc(sketch, "E3265", {"start": v(11.5, -8.55) * mm, "mid": v(11.75, -8.3) * mm, "end": v(11.5, -8.05) * mm});
            skArc(sketch, "E3266", {"start": v(11.5, -8.05) * mm, "mid": v(11.25, -8.3) * mm, "end": v(11.5, -8.55) * mm});
            skArc(sketch, "E3267", {"start": v(10.8, -11.37) * mm, "mid": v(11.05, -11.12) * mm, "end": v(10.8, -10.87) * mm});
            skArc(sketch, "E3268", {"start": v(10.8, -10.87) * mm, "mid": v(10.55, -11.12) * mm, "end": v(10.8, -11.37) * mm});
            skArc(sketch, "E3269", {"start": v(-3.35, -5.54) * mm, "mid": v(-3.1, -5.29) * mm, "end": v(-3.35, -5.04) * mm});
            skArc(sketch, "E3270", {"start": v(-3.35, -5.04) * mm, "mid": v(-3.6, -5.29) * mm, "end": v(-3.35, -5.54) * mm});
            skArc(sketch, "E3271", {"start": v(-10.68, -11.48) * mm, "mid": v(-10.43, -11.23) * mm, "end": v(-10.68, -10.98) * mm});
            skArc(sketch, "E3272", {"start": v(-10.68, -10.98) * mm, "mid": v(-10.93, -11.23) * mm, "end": v(-10.68, -11.48) * mm});
            skArc(sketch, "E3273", {"start": v(6.1, -11.35) * mm, "mid": v(6.35, -11.1) * mm, "end": v(6.1, -10.85) * mm});
            skArc(sketch, "E3274", {"start": v(6.1, -10.85) * mm, "mid": v(5.85, -11.1) * mm, "end": v(6.1, -11.35) * mm});
            skArc(sketch, "E3275", {"start": v(10.35, -0.85) * mm, "mid": v(10.6, -0.6) * mm, "end": v(10.35, -0.35) * mm});
            skArc(sketch, "E3276", {"start": v(10.35, -0.35) * mm, "mid": v(10.1, -0.6) * mm, "end": v(10.35, -0.85) * mm});
            skArc(sketch, "E3277", {"start": v(8.8, 1.65) * mm, "mid": v(9.05, 1.9) * mm, "end": v(8.8, 2.15) * mm});
            skArc(sketch, "E3278", {"start": v(8.8, 2.15) * mm, "mid": v(8.55, 1.9) * mm, "end": v(8.8, 1.65) * mm});
            skArc(sketch, "E3279", {"start": v(8.9, 3.85) * mm, "mid": v(9.16, 4.1) * mm, "end": v(8.9, 4.35) * mm});
            skArc(sketch, "E3280", {"start": v(8.9, 4.35) * mm, "mid": v(8.66, 4.1) * mm, "end": v(8.9, 3.85) * mm});
            skArc(sketch, "E3281", {"start": v(-0.74, 7.09) * mm, "mid": v(-0.5, 7.34) * mm, "end": v(-0.74, 7.59) * mm});
            skArc(sketch, "E3282", {"start": v(-0.74, 7.59) * mm, "mid": v(-1, 7.34) * mm, "end": v(-0.74, 7.09) * mm});
            skArc(sketch, "E3283", {"start": v(0, -4.49) * mm, "mid": v(0.26, -4.24) * mm, "end": v(0, -3.99) * mm});
            skArc(sketch, "E3284", {"start": v(0, -3.99) * mm, "mid": v(-0.24, -4.24) * mm, "end": v(0, -4.49) * mm});
            skArc(sketch, "E3285", {"start": v(0.85, -3.72) * mm, "mid": v(1.1, -3.47) * mm, "end": v(0.85, -3.22) * mm});
            skArc(sketch, "E3286", {"start": v(0.85, -3.22) * mm, "mid": v(0.6, -3.47) * mm, "end": v(0.85, -3.72) * mm});
            skArc(sketch, "E3287", {"start": v(1.73, -2.98) * mm, "mid": v(1.98, -2.73) * mm, "end": v(1.73, -2.48) * mm});
            skArc(sketch, "E3288", {"start": v(1.73, -2.48) * mm, "mid": v(1.48, -2.73) * mm, "end": v(1.73, -2.98) * mm});
            skArc(sketch, "E3289", {"start": v(2.3, -6.75) * mm, "mid": v(2.55, -6.5) * mm, "end": v(2.3, -6.25) * mm});
            skArc(sketch, "E3290", {"start": v(2.3, -6.25) * mm, "mid": v(2.05, -6.5) * mm, "end": v(2.3, -6.75) * mm});
            skArc(sketch, "E3291", {"start": v(9.65, 0) * mm, "mid": v(9.9, 0.25) * mm, "end": v(9.65, 0.5) * mm});
            skArc(sketch, "E3292", {"start": v(9.65, 0.5) * mm, "mid": v(9.4, 0.25) * mm, "end": v(9.65, 0) * mm});
            skArc(sketch, "E3293", {"start": v(7.9, 0) * mm, "mid": v(8.15, 0.25) * mm, "end": v(7.9, 0.5) * mm});
            skArc(sketch, "E3294", {"start": v(7.9, 0.5) * mm, "mid": v(7.65, 0.25) * mm, "end": v(7.9, 0) * mm});
            skArc(sketch, "E3295", {"start": v(-7.3, -6.05) * mm, "mid": v(-7.05, -5.8) * mm, "end": v(-7.3, -5.55) * mm});
            skArc(sketch, "E3296", {"start": v(-7.3, -5.55) * mm, "mid": v(-7.55, -5.8) * mm, "end": v(-7.3, -6.05) * mm});
            skArc(sketch, "E3297", {"start": v(-5.9, -8.35) * mm, "mid": v(-5.65, -8.1) * mm, "end": v(-5.9, -7.85) * mm});
            skArc(sketch, "E3298", {"start": v(-5.9, -7.85) * mm, "mid": v(-6.15, -8.1) * mm, "end": v(-5.9, -8.35) * mm});
            skArc(sketch, "E3299", {"start": v(-9.9, -2.95) * mm, "mid": v(-9.65, -2.7) * mm, "end": v(-9.9, -2.45) * mm});
            skArc(sketch, "E3300", {"start": v(-9.9, -2.45) * mm, "mid": v(-10.15, -2.7) * mm, "end": v(-9.9, -2.95) * mm});
            skArc(sketch, "E3301", {"start": v(-2.32, -3.23) * mm, "mid": v(-2.07, -2.98) * mm, "end": v(-2.32, -2.73) * mm});
            skArc(sketch, "E3302", {"start": v(-2.32, -2.73) * mm, "mid": v(-2.57, -2.98) * mm, "end": v(-2.32, -3.23) * mm});
            skArc(sketch, "E3303", {"start": v(2.62, -10.61) * mm, "mid": v(2.87, -10.36) * mm, "end": v(2.62, -10.11) * mm});
            skArc(sketch, "E3304", {"start": v(2.62, -10.11) * mm, "mid": v(2.37, -10.36) * mm, "end": v(2.62, -10.61) * mm});
            skArc(sketch, "E3305", {"start": v(-1.2, -10.53) * mm, "mid": v(-0.96, -10.28) * mm, "end": v(-1.2, -10.03) * mm});
            skArc(sketch, "E3306", {"start": v(-1.2, -10.03) * mm, "mid": v(-1.46, -10.28) * mm, "end": v(-1.2, -10.53) * mm});
            skArc(sketch, "E3307", {"start": v(-6.7, -7.45) * mm, "mid": v(-6.45, -7.2) * mm, "end": v(-6.7, -6.95) * mm});
            skArc(sketch, "E3308", {"start": v(-6.7, -6.95) * mm, "mid": v(-6.95, -7.2) * mm, "end": v(-6.7, -7.45) * mm});
            skArc(sketch, "E3309", {"start": v(-2.24, 0.23) * mm, "mid": v(-2, 0.48) * mm, "end": v(-2.24, 0.73) * mm});
            skArc(sketch, "E3310", {"start": v(-2.24, 0.73) * mm, "mid": v(-2.5, 0.48) * mm, "end": v(-2.24, 0.23) * mm});
            skArc(sketch, "E3311", {"start": v(9, 7.85) * mm, "mid": v(9.25, 8.1) * mm, "end": v(9, 8.35) * mm});
            skArc(sketch, "E3312", {"start": v(9, 8.35) * mm, "mid": v(8.75, 8.1) * mm, "end": v(9, 7.85) * mm});
            skArc(sketch, "E3313", {"start": v(3.95, 8.43) * mm, "mid": v(4.2, 8.68) * mm, "end": v(3.95, 8.93) * mm});
            skArc(sketch, "E3314", {"start": v(3.95, 8.93) * mm, "mid": v(3.7, 8.68) * mm, "end": v(3.95, 8.43) * mm});
            skArc(sketch, "E3315", {"start": v(0.84, 6.2) * mm, "mid": v(1.09, 6.45) * mm, "end": v(0.84, 6.7) * mm});
            skArc(sketch, "E3316", {"start": v(0.84, 6.7) * mm, "mid": v(0.59, 6.45) * mm, "end": v(0.84, 6.2) * mm});
            skSolve(sketch);
        }
        {
            var Q0;
            Q0=qCreatedBy(makeId("Front.planeOp"),FACE);
            var sketch = newSketch(context, id + "F1", { "sketchPlane" : qUnion([Q0])});
            skLineSegment(sketch, "E3317.0.0", {"start": v(30.23, 5.25) * mm, "end": v(30.22, 5.42) * mm});
            skLineSegment(sketch, "E3317.0.1", {"start": v(30.22, 5.42) * mm, "end": v(30.18, 5.6) * mm});
            skLineSegment(sketch, "E3317.0.2", {"start": v(30.18, 5.6) * mm, "end": v(29.1, 8.94) * mm});
            skLineSegment(sketch, "E3317.0.3", {"start": v(29.1, 8.94) * mm, "end": v(29.03, 9.1) * mm});
            skLineSegment(sketch, "E3317.0.4", {"start": v(29.03, 9.1) * mm, "end": v(28.93, 9.25) * mm});
            skLineSegment(sketch, "E3317.0.5", {"start": v(28.93, 9.25) * mm, "end": v(28.81, 9.38) * mm});
            skLineSegment(sketch, "E3317.0.6", {"start": v(28.81, 9.38) * mm, "end": v(28.67, 9.48) * mm});
            skLineSegment(sketch, "E3317.0.7", {"start": v(28.67, 9.48) * mm, "end": v(28.52, 9.56) * mm});
            skLineSegment(sketch, "E3317.0.8", {"start": v(28.52, 9.56) * mm, "end": v(28.36, 9.6) * mm});
            skLineSegment(sketch, "E3317.0.9", {"start": v(28.36, 9.6) * mm, "end": v(28.18, 9.63) * mm});
            skLineSegment(sketch, "E3317.0.10", {"start": v(28.18, 9.63) * mm, "end": v(28, 9.62) * mm});
            skLineSegment(sketch, "E3317.0.11", {"start": v(28, 9.62) * mm, "end": v(22.92, 8.87) * mm});
            skLineSegment(sketch, "E3317.0.12", {"start": v(22.92, 8.87) * mm, "end": v(21.71, 8.48) * mm});
            skLineSegment(sketch, "E3317.0.13", {"start": v(21.71, 8.48) * mm, "end": v(21.66, 8.46) * mm});
            skLineSegment(sketch, "E3317.0.14", {"start": v(21.66, 8.46) * mm, "end": v(21.62, 8.44) * mm});
            skLineSegment(sketch, "E3317.0.15", {"start": v(21.62, 8.44) * mm, "end": v(21.58, 8.4) * mm});
            skLineSegment(sketch, "E3317.0.16", {"start": v(21.58, 8.4) * mm, "end": v(21.54, 8.38) * mm});
            skLineSegment(sketch, "E3317.0.17", {"start": v(21.54, 8.38) * mm, "end": v(21.5, 8.34) * mm});
            skLineSegment(sketch, "E3317.0.18", {"start": v(21.5, 8.34) * mm, "end": v(21.47, 8.3) * mm});
            skLineSegment(sketch, "E3317.0.19", {"start": v(21.47, 8.3) * mm, "end": v(21.44, 8.26) * mm});
            skLineSegment(sketch, "E3317.0.20", {"start": v(21.44, 8.26) * mm, "end": v(21.32, 8.03) * mm});
            skLineSegment(sketch, "E3317.0.21", {"start": v(21.32, 8.03) * mm, "end": v(21.2, 7.86) * mm});
            skLineSegment(sketch, "E3317.0.22", {"start": v(21.2, 7.86) * mm, "end": v(21.07, 7.7) * mm});
            skLineSegment(sketch, "E3317.0.23", {"start": v(21.07, 7.7) * mm, "end": v(20.92, 7.56) * mm});
            skLineSegment(sketch, "E3317.0.24", {"start": v(20.92, 7.56) * mm, "end": v(20.77, 7.43) * mm});
            skLineSegment(sketch, "E3317.0.25", {"start": v(20.77, 7.43) * mm, "end": v(20.6, 7.32) * mm});
            skLineSegment(sketch, "E3317.0.26", {"start": v(20.6, 7.32) * mm, "end": v(20.4, 7.22) * mm});
            skLineSegment(sketch, "E3317.0.27", {"start": v(20.4, 7.22) * mm, "end": v(20.22, 7.15) * mm});
            skLineSegment(sketch, "E3317.0.28", {"start": v(20.22, 7.15) * mm, "end": v(20.02, 7.1) * mm});
            skLineSegment(sketch, "E3317.0.29", {"start": v(20.02, 7.1) * mm, "end": v(19.81, 7.06) * mm});
            skLineSegment(sketch, "E3317.0.30", {"start": v(19.81, 7.06) * mm, "end": v(19.6, 7.05) * mm});
            skLineSegment(sketch, "E3317.0.31", {"start": v(19.6, 7.05) * mm, "end": v(19.4, 7.06) * mm});
            skLineSegment(sketch, "E3317.0.32", {"start": v(19.4, 7.06) * mm, "end": v(19.2, 7.1) * mm});
            skLineSegment(sketch, "E3317.0.33", {"start": v(19.2, 7.1) * mm, "end": v(19, 7.14) * mm});
            skLineSegment(sketch, "E3317.0.34", {"start": v(19, 7.14) * mm, "end": v(18.8, 7.21) * mm});
            skLineSegment(sketch, "E3317.0.35", {"start": v(18.8, 7.21) * mm, "end": v(18.58, 7.33) * mm});
            skLineSegment(sketch, "E3317.0.36", {"start": v(18.58, 7.33) * mm, "end": v(18.53, 7.35) * mm});
            skLineSegment(sketch, "E3317.0.37", {"start": v(18.53, 7.35) * mm, "end": v(18.48, 7.36) * mm});
            skLineSegment(sketch, "E3317.0.38", {"start": v(18.48, 7.36) * mm, "end": v(18.43, 7.37) * mm});
            skLineSegment(sketch, "E3317.0.39", {"start": v(18.43, 7.37) * mm, "end": v(18.38, 7.37) * mm});
            skLineSegment(sketch, "E3317.0.40", {"start": v(18.38, 7.37) * mm, "end": v(18.33, 7.37) * mm});
            skLineSegment(sketch, "E3317.0.41", {"start": v(18.33, 7.37) * mm, "end": v(18.28, 7.36) * mm});
            skLineSegment(sketch, "E3317.0.42", {"start": v(18.28, 7.36) * mm, "end": v(18.23, 7.34) * mm});
            skLineSegment(sketch, "E3317.0.43", {"start": v(18.23, 7.34) * mm, "end": v(13.03, 5.66) * mm});
            skLineSegment(sketch, "E3317.0.44", {"start": v(13.03, 5.66) * mm, "end": v(13, 5.65) * mm});
            skLineSegment(sketch, "E3317.0.45", {"start": v(13, 5.65) * mm, "end": v(12.96, 5.65) * mm});
            skLineSegment(sketch, "E3317.0.46", {"start": v(12.96, 5.65) * mm, "end": v(12.92, 5.64) * mm});
            skLineSegment(sketch, "E3317.0.47", {"start": v(12.92, 5.64) * mm, "end": v(12.88, 5.64) * mm});
            skLineSegment(sketch, "E3317.0.48", {"start": v(12.88, 5.64) * mm, "end": v(12.83, 5.64) * mm});
            skLineSegment(sketch, "E3317.0.49", {"start": v(12.83, 5.64) * mm, "end": v(12.8, 5.64) * mm});
            skLineSegment(sketch, "E3317.0.50", {"start": v(12.8, 5.64) * mm, "end": v(12.76, 5.65) * mm});
            skLineSegment(sketch, "E3317.0.51", {"start": v(12.76, 5.65) * mm, "end": v(12.73, 5.66) * mm});
            skLineSegment(sketch, "E3317.0.52", {"start": v(12.73, 5.66) * mm, "end": v(12.7, 5.68) * mm});
            skLineSegment(sketch, "E3317.0.53", {"start": v(12.7, 5.68) * mm, "end": v(12.67, 5.7) * mm});
            skLineSegment(sketch, "E3317.0.54", {"start": v(12.67, 5.7) * mm, "end": v(12.65, 5.72) * mm});
            skLineSegment(sketch, "E3317.0.55", {"start": v(12.65, 5.72) * mm, "end": v(12.63, 5.74) * mm});
            skLineSegment(sketch, "E3317.0.56", {"start": v(12.63, 5.74) * mm, "end": v(12.6, 5.77) * mm});
            skLineSegment(sketch, "E3317.0.57", {"start": v(12.6, 5.77) * mm, "end": v(12.59, 5.8) * mm});
            skLineSegment(sketch, "E3317.0.58", {"start": v(12.59, 5.8) * mm, "end": v(12.4, 6.07) * mm});
            skLineSegment(sketch, "E3317.0.59", {"start": v(12.4, 6.07) * mm, "end": v(12.1, 6.48) * mm});
            skLineSegment(sketch, "E3317.0.60", {"start": v(12.1, 6.48) * mm, "end": v(12.1, 6.5) * mm});
            skLineSegment(sketch, "E3317.0.61", {"start": v(12.1, 6.5) * mm, "end": v(12.09, 6.52) * mm});
            skLineSegment(sketch, "E3317.0.62", {"start": v(12.09, 6.52) * mm, "end": v(12.08, 6.54) * mm});
            skLineSegment(sketch, "E3317.0.63", {"start": v(12.08, 6.54) * mm, "end": v(12.07, 6.56) * mm});
            skLineSegment(sketch, "E3317.0.64", {"start": v(12.07, 6.56) * mm, "end": v(12.06, 6.58) * mm});
            skLineSegment(sketch, "E3317.0.65", {"start": v(12.06, 6.58) * mm, "end": v(12.06, 6.6) * mm});
            skLineSegment(sketch, "E3317.0.66", {"start": v(12.06, 6.6) * mm, "end": v(12.06, 6.63) * mm});
            skLineSegment(sketch, "E3317.0.67", {"start": v(12.06, 6.63) * mm, "end": v(12.05, 6.65) * mm});
            skLineSegment(sketch, "E3317.0.68", {"start": v(12.05, 6.65) * mm, "end": v(12.05, 6.67) * mm});
            skLineSegment(sketch, "E3317.0.69", {"start": v(12.05, 6.67) * mm, "end": v(12.06, 6.7) * mm});
            skLineSegment(sketch, "E3317.0.70", {"start": v(12.06, 6.7) * mm, "end": v(12.06, 6.71) * mm});
            skLineSegment(sketch, "E3317.0.71", {"start": v(12.06, 6.71) * mm, "end": v(12.06, 6.73) * mm});
            skLineSegment(sketch, "E3317.0.72", {"start": v(12.06, 6.73) * mm, "end": v(12.06, 6.73) * mm});
            skLineSegment(sketch, "E3317.0.73", {"start": v(12.06, 6.73) * mm, "end": v(12.09, 6.78) * mm});
            skLineSegment(sketch, "E3317.0.74", {"start": v(12.09, 6.78) * mm, "end": v(12.2, 7.09) * mm});
            skLineSegment(sketch, "E3317.0.75", {"start": v(12.2, 7.09) * mm, "end": v(12.28, 7.42) * mm});
            skLineSegment(sketch, "E3317.0.76", {"start": v(12.28, 7.42) * mm, "end": v(12.34, 7.75) * mm});
            skLineSegment(sketch, "E3317.0.77", {"start": v(12.34, 7.75) * mm, "end": v(12.35, 8.1) * mm});
            skLineSegment(sketch, "E3317.0.78", {"start": v(12.35, 8.1) * mm, "end": v(12.34, 8.45) * mm});
            skLineSegment(sketch, "E3317.0.79", {"start": v(12.34, 8.45) * mm, "end": v(12.28, 8.79) * mm});
            skLineSegment(sketch, "E3317.0.80", {"start": v(12.28, 8.79) * mm, "end": v(12.2, 9.11) * mm});
            skLineSegment(sketch, "E3317.0.81", {"start": v(12.2, 9.11) * mm, "end": v(12.09, 9.42) * mm});
            skLineSegment(sketch, "E3317.0.82", {"start": v(12.09, 9.42) * mm, "end": v(11.94, 9.72) * mm});
            skLineSegment(sketch, "E3317.0.83", {"start": v(11.94, 9.72) * mm, "end": v(11.77, 10) * mm});
            skLineSegment(sketch, "E3317.0.84", {"start": v(11.77, 10) * mm, "end": v(11.58, 10.26) * mm});
            skLineSegment(sketch, "E3317.0.85", {"start": v(11.58, 10.26) * mm, "end": v(11.36, 10.5) * mm});
            skLineSegment(sketch, "E3317.0.86", {"start": v(11.36, 10.5) * mm, "end": v(11.12, 10.72) * mm});
            skLineSegment(sketch, "E3317.0.87", {"start": v(11.12, 10.72) * mm, "end": v(10.85, 10.92) * mm});
            skLineSegment(sketch, "E3317.0.88", {"start": v(10.85, 10.92) * mm, "end": v(10.57, 11.09) * mm});
            skLineSegment(sketch, "E3317.0.89", {"start": v(10.57, 11.09) * mm, "end": v(10.28, 11.23) * mm});
            skLineSegment(sketch, "E3317.0.90", {"start": v(10.28, 11.23) * mm, "end": v(9.96, 11.35) * mm});
            skLineSegment(sketch, "E3317.0.91", {"start": v(9.96, 11.35) * mm, "end": v(9.64, 11.43) * mm});
            skLineSegment(sketch, "E3317.0.92", {"start": v(9.64, 11.43) * mm, "end": v(9.3, 11.48) * mm});
            skLineSegment(sketch, "E3317.0.93", {"start": v(9.3, 11.48) * mm, "end": v(8.95, 11.5) * mm});
            skLineSegment(sketch, "E3317.0.94", {"start": v(8.95, 11.5) * mm, "end": v(8.6, 11.48) * mm});
            skLineSegment(sketch, "E3317.0.95", {"start": v(8.6, 11.48) * mm, "end": v(8.27, 11.43) * mm});
            skLineSegment(sketch, "E3317.0.96", {"start": v(8.27, 11.43) * mm, "end": v(7.94, 11.35) * mm});
            skLineSegment(sketch, "E3317.0.97", {"start": v(7.94, 11.35) * mm, "end": v(7.63, 11.23) * mm});
            skLineSegment(sketch, "E3317.0.98", {"start": v(7.63, 11.23) * mm, "end": v(7.33, 11.1) * mm});
            skLineSegment(sketch, "E3317.0.99", {"start": v(7.33, 11.1) * mm, "end": v(7.05, 10.92) * mm});
            skLineSegment(sketch, "E3317.0.100", {"start": v(7.05, 10.92) * mm, "end": v(6.8, 10.72) * mm});
            skLineSegment(sketch, "E3317.0.101", {"start": v(6.8, 10.72) * mm, "end": v(6.63, 10.58) * mm});
            skLineSegment(sketch, "E3317.0.102", {"start": v(6.63, 10.58) * mm, "end": v(6.55, 10.51) * mm});
            skLineSegment(sketch, "E3317.0.103", {"start": v(6.55, 10.51) * mm, "end": v(6.47, 10.47) * mm});
            skLineSegment(sketch, "E3317.0.104", {"start": v(6.47, 10.47) * mm, "end": v(6.37, 10.44) * mm});
            skLineSegment(sketch, "E3317.0.105", {"start": v(6.37, 10.44) * mm, "end": v(6.27, 10.43) * mm});
            skLineSegment(sketch, "E3317.0.106", {"start": v(6.27, 10.43) * mm, "end": v(6.17, 10.44) * mm});
            skLineSegment(sketch, "E3317.0.107", {"start": v(6.17, 10.44) * mm, "end": v(6.08, 10.47) * mm});
            skLineSegment(sketch, "E3317.0.108", {"start": v(6.08, 10.47) * mm, "end": v(6.02, 10.5) * mm});
            skLineSegment(sketch, "E3317.0.109", {"start": v(6.02, 10.5) * mm, "end": v(5.84, 10.58) * mm});
            skLineSegment(sketch, "E3317.0.110", {"start": v(5.84, 10.58) * mm, "end": v(5.53, 10.72) * mm});
            skLineSegment(sketch, "E3317.0.111", {"start": v(5.53, 10.72) * mm, "end": v(5.2, 10.85) * mm});
            skLineSegment(sketch, "E3317.0.112", {"start": v(5.2, 10.85) * mm, "end": v(4.88, 10.97) * mm});
            skLineSegment(sketch, "E3317.0.113", {"start": v(4.88, 10.97) * mm, "end": v(4.56, 11.1) * mm});
            skLineSegment(sketch, "E3317.0.114", {"start": v(4.56, 11.1) * mm, "end": v(4.22, 11.2) * mm});
            skLineSegment(sketch, "E3317.0.115", {"start": v(4.22, 11.2) * mm, "end": v(4.02, 11.26) * mm});
            skLineSegment(sketch, "E3317.0.116", {"start": v(4.02, 11.26) * mm, "end": v(3.9, 11.29) * mm});
            skLineSegment(sketch, "E3317.0.117", {"start": v(3.9, 11.29) * mm, "end": v(3.82, 11.34) * mm});
            skLineSegment(sketch, "E3317.0.118", {"start": v(3.82, 11.34) * mm, "end": v(3.75, 11.4) * mm});
            skLineSegment(sketch, "E3317.0.119", {"start": v(3.75, 11.4) * mm, "end": v(3.68, 11.47) * mm});
            skLineSegment(sketch, "E3317.0.120", {"start": v(3.68, 11.47) * mm, "end": v(3.64, 11.56) * mm});
            skLineSegment(sketch, "E3317.0.121", {"start": v(3.64, 11.56) * mm, "end": v(3.6, 11.65) * mm});
            skLineSegment(sketch, "E3317.0.122", {"start": v(3.6, 11.65) * mm, "end": v(3.6, 11.76) * mm});
            skLineSegment(sketch, "E3317.0.123", {"start": v(3.6, 11.76) * mm, "end": v(3.6, 17.97) * mm});
            skLineSegment(sketch, "E3317.0.124", {"start": v(3.6, 17.97) * mm, "end": v(3.6, 18.02) * mm});
            skLineSegment(sketch, "E3317.0.125", {"start": v(3.6, 18.02) * mm, "end": v(3.59, 18.07) * mm});
            skLineSegment(sketch, "E3317.0.126", {"start": v(3.59, 18.07) * mm, "end": v(3.58, 18.12) * mm});
            skLineSegment(sketch, "E3317.0.127", {"start": v(3.58, 18.12) * mm, "end": v(3.56, 18.17) * mm});
            skLineSegment(sketch, "E3317.0.128", {"start": v(3.56, 18.17) * mm, "end": v(3.54, 18.21) * mm});
            skLineSegment(sketch, "E3317.0.129", {"start": v(3.54, 18.21) * mm, "end": v(3.5, 18.26) * mm});
            skLineSegment(sketch, "E3317.0.130", {"start": v(3.5, 18.26) * mm, "end": v(3.48, 18.3) * mm});
            skLineSegment(sketch, "E3317.0.131", {"start": v(3.48, 18.3) * mm, "end": v(3.3, 18.48) * mm});
            skLineSegment(sketch, "E3317.0.132", {"start": v(3.3, 18.48) * mm, "end": v(3.17, 18.65) * mm});
            skLineSegment(sketch, "E3317.0.133", {"start": v(3.17, 18.65) * mm, "end": v(3.06, 18.82) * mm});
            skLineSegment(sketch, "E3317.0.134", {"start": v(3.06, 18.82) * mm, "end": v(2.97, 19) * mm});
            skLineSegment(sketch, "E3317.0.135", {"start": v(2.97, 19) * mm, "end": v(2.9, 19.2) * mm});
            skLineSegment(sketch, "E3317.0.136", {"start": v(2.9, 19.2) * mm, "end": v(2.84, 19.4) * mm});
            skLineSegment(sketch, "E3317.0.137", {"start": v(2.84, 19.4) * mm, "end": v(2.81, 19.6) * mm});
            skLineSegment(sketch, "E3317.0.138", {"start": v(2.81, 19.6) * mm, "end": v(2.8, 19.8) * mm});
            skLineSegment(sketch, "E3317.0.139", {"start": v(2.8, 19.8) * mm, "end": v(2.81, 20) * mm});
            skLineSegment(sketch, "E3317.0.140", {"start": v(2.81, 20) * mm, "end": v(2.84, 20.21) * mm});
            skLineSegment(sketch, "E3317.0.141", {"start": v(2.84, 20.21) * mm, "end": v(2.9, 20.41) * mm});
            skLineSegment(sketch, "E3317.0.142", {"start": v(2.9, 20.41) * mm, "end": v(2.97, 20.6) * mm});
            skLineSegment(sketch, "E3317.0.143", {"start": v(2.97, 20.6) * mm, "end": v(3.06, 20.78) * mm});
            skLineSegment(sketch, "E3317.0.144", {"start": v(3.06, 20.78) * mm, "end": v(3.17, 20.96) * mm});
            skLineSegment(sketch, "E3317.0.145", {"start": v(3.17, 20.96) * mm, "end": v(3.3, 21.12) * mm});
            skLineSegment(sketch, "E3317.0.146", {"start": v(3.3, 21.12) * mm, "end": v(3.48, 21.3) * mm});
            skLineSegment(sketch, "E3317.0.147", {"start": v(3.48, 21.3) * mm, "end": v(3.5, 21.35) * mm});
            skLineSegment(sketch, "E3317.0.148", {"start": v(3.5, 21.35) * mm, "end": v(3.54, 21.39) * mm});
            skLineSegment(sketch, "E3317.0.149", {"start": v(3.54, 21.39) * mm, "end": v(3.56, 21.44) * mm});
            skLineSegment(sketch, "E3317.0.150", {"start": v(3.56, 21.44) * mm, "end": v(3.58, 21.48) * mm});
            skLineSegment(sketch, "E3317.0.151", {"start": v(3.58, 21.48) * mm, "end": v(3.59, 21.53) * mm});
            skLineSegment(sketch, "E3317.0.152", {"start": v(3.59, 21.53) * mm, "end": v(3.6, 21.58) * mm});
            skLineSegment(sketch, "E3317.0.153", {"start": v(3.6, 21.58) * mm, "end": v(3.6, 21.63) * mm});
            skLineSegment(sketch, "E3317.0.154", {"start": v(3.6, 21.63) * mm, "end": v(3.6, 22.9) * mm});
            skLineSegment(sketch, "E3317.0.155", {"start": v(3.6, 22.9) * mm, "end": v(2.74, 27.97) * mm});
            skLineSegment(sketch, "E3317.0.156", {"start": v(2.74, 27.97) * mm, "end": v(2.7, 28.14) * mm});
            skLineSegment(sketch, "E3317.0.157", {"start": v(2.7, 28.14) * mm, "end": v(2.62, 28.3) * mm});
            skLineSegment(sketch, "E3317.0.158", {"start": v(2.62, 28.3) * mm, "end": v(2.52, 28.44) * mm});
            skLineSegment(sketch, "E3317.0.159", {"start": v(2.52, 28.44) * mm, "end": v(2.4, 28.57) * mm});
            skLineSegment(sketch, "E3317.0.160", {"start": v(2.4, 28.57) * mm, "end": v(2.26, 28.67) * mm});
            skLineSegment(sketch, "E3317.0.161", {"start": v(2.26, 28.67) * mm, "end": v(2.1, 28.74) * mm});
            skLineSegment(sketch, "E3317.0.162", {"start": v(2.1, 28.74) * mm, "end": v(1.93, 28.79) * mm});
            skLineSegment(sketch, "E3317.0.163", {"start": v(1.93, 28.79) * mm, "end": v(1.76, 28.8) * mm});
            skLineSegment(sketch, "E3317.0.164", {"start": v(1.76, 28.8) * mm, "end": v(-1.4, 28.8) * mm});
            skLineSegment(sketch, "E3317.0.165", {"start": v(-1.4, 28.8) * mm, "end": v(-1.7, 28.8) * mm});
            skLineSegment(sketch, "E3317.0.166", {"start": v(-1.7, 28.8) * mm, "end": v(-1.76, 28.8) * mm});
            skLineSegment(sketch, "E3317.0.167", {"start": v(-1.76, 28.8) * mm, "end": v(-1.93, 28.79) * mm});
            skLineSegment(sketch, "E3317.0.168", {"start": v(-1.93, 28.79) * mm, "end": v(-2.1, 28.74) * mm});
            skLineSegment(sketch, "E3317.0.169", {"start": v(-2.1, 28.74) * mm, "end": v(-2.26, 28.67) * mm});
            skLineSegment(sketch, "E3317.0.170", {"start": v(-2.26, 28.67) * mm, "end": v(-2.4, 28.57) * mm});
            skLineSegment(sketch, "E3317.0.171", {"start": v(-2.4, 28.57) * mm, "end": v(-2.52, 28.44) * mm});
            skLineSegment(sketch, "E3317.0.172", {"start": v(-2.52, 28.44) * mm, "end": v(-2.62, 28.3) * mm});
            skLineSegment(sketch, "E3317.0.173", {"start": v(-2.62, 28.3) * mm, "end": v(-2.7, 28.14) * mm});
            skLineSegment(sketch, "E3317.0.174", {"start": v(-2.7, 28.14) * mm, "end": v(-2.74, 27.97) * mm});
            skLineSegment(sketch, "E3317.0.175", {"start": v(-2.74, 27.97) * mm, "end": v(-3.6, 22.9) * mm});
            skLineSegment(sketch, "E3317.0.176", {"start": v(-3.6, 22.9) * mm, "end": v(-3.6, 21.63) * mm});
            skLineSegment(sketch, "E3317.0.177", {"start": v(-3.6, 21.63) * mm, "end": v(-3.6, 21.58) * mm});
            skLineSegment(sketch, "E3317.0.178", {"start": v(-3.6, 21.58) * mm, "end": v(-3.59, 21.53) * mm});
            skLineSegment(sketch, "E3317.0.179", {"start": v(-3.59, 21.53) * mm, "end": v(-3.58, 21.48) * mm});
            skLineSegment(sketch, "E3317.0.180", {"start": v(-3.58, 21.48) * mm, "end": v(-3.56, 21.44) * mm});
            skLineSegment(sketch, "E3317.0.181", {"start": v(-3.56, 21.44) * mm, "end": v(-3.53, 21.39) * mm});
            skLineSegment(sketch, "E3317.0.182", {"start": v(-3.53, 21.39) * mm, "end": v(-3.5, 21.35) * mm});
            skLineSegment(sketch, "E3317.0.183", {"start": v(-3.5, 21.35) * mm, "end": v(-3.48, 21.3) * mm});
            skLineSegment(sketch, "E3317.0.184", {"start": v(-3.48, 21.3) * mm, "end": v(-3.3, 21.12) * mm});
            skLineSegment(sketch, "E3317.0.185", {"start": v(-3.3, 21.12) * mm, "end": v(-3.17, 20.96) * mm});
            skLineSegment(sketch, "E3317.0.186", {"start": v(-3.17, 20.96) * mm, "end": v(-3.06, 20.78) * mm});
            skLineSegment(sketch, "E3317.0.187", {"start": v(-3.06, 20.78) * mm, "end": v(-2.97, 20.6) * mm});
            skLineSegment(sketch, "E3317.0.188", {"start": v(-2.97, 20.6) * mm, "end": v(-2.9, 20.41) * mm});
            skLineSegment(sketch, "E3317.0.189", {"start": v(-2.9, 20.41) * mm, "end": v(-2.84, 20.21) * mm});
            skLineSegment(sketch, "E3317.0.190", {"start": v(-2.84, 20.21) * mm, "end": v(-2.8, 20) * mm});
            skLineSegment(sketch, "E3317.0.191", {"start": v(-2.8, 20) * mm, "end": v(-2.8, 19.8) * mm});
            skLineSegment(sketch, "E3317.0.192", {"start": v(-2.8, 19.8) * mm, "end": v(-2.8, 19.6) * mm});
            skLineSegment(sketch, "E3317.0.193", {"start": v(-2.8, 19.6) * mm, "end": v(-2.84, 19.4) * mm});
            skLineSegment(sketch, "E3317.0.194", {"start": v(-2.84, 19.4) * mm, "end": v(-2.9, 19.2) * mm});
            skLineSegment(sketch, "E3317.0.195", {"start": v(-2.9, 19.2) * mm, "end": v(-2.97, 19) * mm});
            skLineSegment(sketch, "E3317.0.196", {"start": v(-2.97, 19) * mm, "end": v(-3.06, 18.82) * mm});
            skLineSegment(sketch, "E3317.0.197", {"start": v(-3.06, 18.82) * mm, "end": v(-3.17, 18.65) * mm});
            skLineSegment(sketch, "E3317.0.198", {"start": v(-3.17, 18.65) * mm, "end": v(-3.3, 18.48) * mm});
            skLineSegment(sketch, "E3317.0.199", {"start": v(-3.3, 18.48) * mm, "end": v(-3.48, 18.3) * mm});
            skLineSegment(sketch, "E3317.0.200", {"start": v(-3.48, 18.3) * mm, "end": v(-3.5, 18.26) * mm});
            skLineSegment(sketch, "E3317.0.201", {"start": v(-3.5, 18.26) * mm, "end": v(-3.53, 18.21) * mm});
            skLineSegment(sketch, "E3317.0.202", {"start": v(-3.53, 18.21) * mm, "end": v(-3.56, 18.17) * mm});
            skLineSegment(sketch, "E3317.0.203", {"start": v(-3.56, 18.17) * mm, "end": v(-3.58, 18.12) * mm});
            skLineSegment(sketch, "E3317.0.204", {"start": v(-3.58, 18.12) * mm, "end": v(-3.59, 18.07) * mm});
            skLineSegment(sketch, "E3317.0.205", {"start": v(-3.59, 18.07) * mm, "end": v(-3.6, 18.02) * mm});
            skLineSegment(sketch, "E3317.0.206", {"start": v(-3.6, 18.02) * mm, "end": v(-3.6, 17.97) * mm});
            skLineSegment(sketch, "E3317.0.207", {"start": v(-3.6, 17.97) * mm, "end": v(-3.6, 11.83) * mm});
            skLineSegment(sketch, "E3317.0.208", {"start": v(-3.6, 11.83) * mm, "end": v(-3.6, 11.66) * mm});
            skLineSegment(sketch, "E3317.0.209", {"start": v(-3.6, 11.66) * mm, "end": v(-3.63, 11.56) * mm});
            skLineSegment(sketch, "E3317.0.210", {"start": v(-3.63, 11.56) * mm, "end": v(-3.68, 11.48) * mm});
            skLineSegment(sketch, "E3317.0.211", {"start": v(-3.68, 11.48) * mm, "end": v(-3.74, 11.4) * mm});
            skLineSegment(sketch, "E3317.0.212", {"start": v(-3.74, 11.4) * mm, "end": v(-3.81, 11.34) * mm});
            skLineSegment(sketch, "E3317.0.213", {"start": v(-3.81, 11.34) * mm, "end": v(-3.9, 11.3) * mm});
            skLineSegment(sketch, "E3317.0.214", {"start": v(-3.9, 11.3) * mm, "end": v(-3.94, 11.28) * mm});
            skLineSegment(sketch, "E3317.0.215", {"start": v(-3.94, 11.28) * mm, "end": v(-3.94, 11.28) * mm});
            skLineSegment(sketch, "E3317.0.216", {"start": v(-3.94, 11.28) * mm, "end": v(-4, 11.27) * mm});
            skLineSegment(sketch, "E3317.0.217", {"start": v(-4, 11.27) * mm, "end": v(-4.22, 11.2) * mm});
            skLineSegment(sketch, "E3317.0.218", {"start": v(-4.22, 11.2) * mm, "end": v(-4.55, 11.1) * mm});
            skLineSegment(sketch, "E3317.0.219", {"start": v(-4.55, 11.1) * mm, "end": v(-4.88, 10.97) * mm});
            skLineSegment(sketch, "E3317.0.220", {"start": v(-4.88, 10.97) * mm, "end": v(-5.2, 10.85) * mm});
            skLineSegment(sketch, "E3317.0.221", {"start": v(-5.2, 10.85) * mm, "end": v(-5.53, 10.72) * mm});
            skLineSegment(sketch, "E3317.0.222", {"start": v(-5.53, 10.72) * mm, "end": v(-5.84, 10.58) * mm});
            skLineSegment(sketch, "E3317.0.223", {"start": v(-5.84, 10.58) * mm, "end": v(-6.12, 10.45) * mm});
            skLineSegment(sketch, "E3317.0.224", {"start": v(-6.12, 10.45) * mm, "end": v(-6.12, 10.45) * mm});
            skLineSegment(sketch, "E3317.0.225", {"start": v(-6.12, 10.45) * mm, "end": v(-6.22, 10.42) * mm});
            skLineSegment(sketch, "E3317.0.226", {"start": v(-6.22, 10.42) * mm, "end": v(-6.32, 10.41) * mm});
            skLineSegment(sketch, "E3317.0.227", {"start": v(-6.32, 10.41) * mm, "end": v(-6.42, 10.42) * mm});
            skLineSegment(sketch, "E3317.0.228", {"start": v(-6.42, 10.42) * mm, "end": v(-6.51, 10.45) * mm});
            skLineSegment(sketch, "E3317.0.229", {"start": v(-6.51, 10.45) * mm, "end": v(-6.6, 10.5) * mm});
            skLineSegment(sketch, "E3317.0.230", {"start": v(-6.6, 10.5) * mm, "end": v(-6.66, 10.55) * mm});
            skLineSegment(sketch, "E3317.0.231", {"start": v(-6.66, 10.55) * mm, "end": v(-6.66, 10.55) * mm});
            skLineSegment(sketch, "E3317.0.232", {"start": v(-6.66, 10.55) * mm, "end": v(-6.85, 10.72) * mm});
            skLineSegment(sketch, "E3317.0.233", {"start": v(-6.85, 10.72) * mm, "end": v(-7.12, 10.92) * mm});
            skLineSegment(sketch, "E3317.0.234", {"start": v(-7.12, 10.92) * mm, "end": v(-7.4, 11.09) * mm});
            skLineSegment(sketch, "E3317.0.235", {"start": v(-7.4, 11.09) * mm, "end": v(-7.7, 11.23) * mm});
            skLineSegment(sketch, "E3317.0.236", {"start": v(-7.7, 11.23) * mm, "end": v(-8, 11.35) * mm});
            skLineSegment(sketch, "E3317.0.237", {"start": v(-8, 11.35) * mm, "end": v(-8.33, 11.43) * mm});
            skLineSegment(sketch, "E3317.0.238", {"start": v(-8.33, 11.43) * mm, "end": v(-8.67, 11.48) * mm});
            skLineSegment(sketch, "E3317.0.239", {"start": v(-8.67, 11.48) * mm, "end": v(-9.02, 11.5) * mm});
            skLineSegment(sketch, "E3317.0.240", {"start": v(-9.02, 11.5) * mm, "end": v(-9.36, 11.48) * mm});
            skLineSegment(sketch, "E3317.0.241", {"start": v(-9.36, 11.48) * mm, "end": v(-9.7, 11.43) * mm});
            skLineSegment(sketch, "E3317.0.242", {"start": v(-9.7, 11.43) * mm, "end": v(-10.03, 11.35) * mm});
            skLineSegment(sketch, "E3317.0.243", {"start": v(-10.03, 11.35) * mm, "end": v(-10.34, 11.23) * mm});
            skLineSegment(sketch, "E3317.0.244", {"start": v(-10.34, 11.23) * mm, "end": v(-10.64, 11.09) * mm});
            skLineSegment(sketch, "E3317.0.245", {"start": v(-10.64, 11.09) * mm, "end": v(-10.92, 10.92) * mm});
            skLineSegment(sketch, "E3317.0.246", {"start": v(-10.92, 10.92) * mm, "end": v(-11.18, 10.72) * mm});
            skLineSegment(sketch, "E3317.0.247", {"start": v(-11.18, 10.72) * mm, "end": v(-11.42, 10.5) * mm});
            skLineSegment(sketch, "E3317.0.248", {"start": v(-11.42, 10.5) * mm, "end": v(-11.64, 10.26) * mm});
            skLineSegment(sketch, "E3317.0.249", {"start": v(-11.64, 10.26) * mm, "end": v(-11.84, 10) * mm});
            skLineSegment(sketch, "E3317.0.250", {"start": v(-11.84, 10) * mm, "end": v(-12, 9.72) * mm});
            skLineSegment(sketch, "E3317.0.251", {"start": v(-12, 9.72) * mm, "end": v(-12.15, 9.42) * mm});
            skLineSegment(sketch, "E3317.0.252", {"start": v(-12.15, 9.42) * mm, "end": v(-12.26, 9.11) * mm});
            skLineSegment(sketch, "E3317.0.253", {"start": v(-12.26, 9.11) * mm, "end": v(-12.35, 8.79) * mm});
            skLineSegment(sketch, "E3317.0.254", {"start": v(-12.35, 8.79) * mm, "end": v(-12.4, 8.45) * mm});
            skLineSegment(sketch, "E3317.0.255", {"start": v(-12.4, 8.45) * mm, "end": v(-12.42, 8.1) * mm});
            skLineSegment(sketch, "E3317.0.256", {"start": v(-12.42, 8.1) * mm, "end": v(-12.4, 7.75) * mm});
            skLineSegment(sketch, "E3317.0.257", {"start": v(-12.4, 7.75) * mm, "end": v(-12.35, 7.42) * mm});
            skLineSegment(sketch, "E3317.0.258", {"start": v(-12.35, 7.42) * mm, "end": v(-12.26, 7.09) * mm});
            skLineSegment(sketch, "E3317.0.259", {"start": v(-12.26, 7.09) * mm, "end": v(-12.15, 6.78) * mm});
            skLineSegment(sketch, "E3317.0.260", {"start": v(-12.15, 6.78) * mm, "end": v(-12.1, 6.67) * mm});
            skLineSegment(sketch, "E3317.0.261", {"start": v(-12.1, 6.67) * mm, "end": v(-12.1, 6.67) * mm});
            skLineSegment(sketch, "E3317.0.262", {"start": v(-12.1, 6.67) * mm, "end": v(-12.1, 6.64) * mm});
            skLineSegment(sketch, "E3317.0.263", {"start": v(-12.1, 6.64) * mm, "end": v(-12.1, 6.61) * mm});
            skLineSegment(sketch, "E3317.0.264", {"start": v(-12.1, 6.61) * mm, "end": v(-12.1, 6.58) * mm});
            skLineSegment(sketch, "E3317.0.265", {"start": v(-12.1, 6.58) * mm, "end": v(-12.1, 6.56) * mm});
            skLineSegment(sketch, "E3317.0.266", {"start": v(-12.1, 6.56) * mm, "end": v(-12.1, 6.53) * mm});
            skLineSegment(sketch, "E3317.0.267", {"start": v(-12.1, 6.53) * mm, "end": v(-12.1, 6.51) * mm});
            skLineSegment(sketch, "E3317.0.268", {"start": v(-12.1, 6.51) * mm, "end": v(-12.11, 6.5) * mm});
            skLineSegment(sketch, "E3317.0.269", {"start": v(-12.11, 6.5) * mm, "end": v(-12.12, 6.47) * mm});
            skLineSegment(sketch, "E3317.0.270", {"start": v(-12.12, 6.47) * mm, "end": v(-12.13, 6.45) * mm});
            skLineSegment(sketch, "E3317.0.271", {"start": v(-12.13, 6.45) * mm, "end": v(-12.15, 6.43) * mm});
            skLineSegment(sketch, "E3317.0.272", {"start": v(-12.15, 6.43) * mm, "end": v(-12.44, 6) * mm});
            skLineSegment(sketch, "E3317.0.273", {"start": v(-12.44, 6) * mm, "end": v(-12.56, 5.83) * mm});
            skLineSegment(sketch, "E3317.0.274", {"start": v(-12.56, 5.83) * mm, "end": v(-12.58, 5.8) * mm});
            skLineSegment(sketch, "E3317.0.275", {"start": v(-12.58, 5.8) * mm, "end": v(-12.6, 5.77) * mm});
            skLineSegment(sketch, "E3317.0.276", {"start": v(-12.6, 5.77) * mm, "end": v(-12.63, 5.74) * mm});
            skLineSegment(sketch, "E3317.0.277", {"start": v(-12.63, 5.74) * mm, "end": v(-12.66, 5.71) * mm});
            skLineSegment(sketch, "E3317.0.278", {"start": v(-12.66, 5.71) * mm, "end": v(-12.69, 5.7) * mm});
            skLineSegment(sketch, "E3317.0.279", {"start": v(-12.69, 5.7) * mm, "end": v(-12.72, 5.67) * mm});
            skLineSegment(sketch, "E3317.0.280", {"start": v(-12.72, 5.67) * mm, "end": v(-12.76, 5.66) * mm});
            skLineSegment(sketch, "E3317.0.281", {"start": v(-12.76, 5.66) * mm, "end": v(-12.8, 5.65) * mm});
            skLineSegment(sketch, "E3317.0.282", {"start": v(-12.8, 5.65) * mm, "end": v(-12.84, 5.64) * mm});
            skLineSegment(sketch, "E3317.0.283", {"start": v(-12.84, 5.64) * mm, "end": v(-12.88, 5.64) * mm});
            skLineSegment(sketch, "E3317.0.284", {"start": v(-12.88, 5.64) * mm, "end": v(-12.93, 5.65) * mm});
            skLineSegment(sketch, "E3317.0.285", {"start": v(-12.93, 5.65) * mm, "end": v(-13, 5.65) * mm});
            skLineSegment(sketch, "E3317.0.286", {"start": v(-13, 5.65) * mm, "end": v(-13.03, 5.66) * mm});
            skLineSegment(sketch, "E3317.0.287", {"start": v(-13.03, 5.66) * mm, "end": v(-18.23, 7.34) * mm});
            skLineSegment(sketch, "E3317.0.288", {"start": v(-18.23, 7.34) * mm, "end": v(-18.28, 7.36) * mm});
            skLineSegment(sketch, "E3317.0.289", {"start": v(-18.28, 7.36) * mm, "end": v(-18.33, 7.37) * mm});
            skLineSegment(sketch, "E3317.0.290", {"start": v(-18.33, 7.37) * mm, "end": v(-18.38, 7.37) * mm});
            skLineSegment(sketch, "E3317.0.291", {"start": v(-18.38, 7.37) * mm, "end": v(-18.43, 7.37) * mm});
            skLineSegment(sketch, "E3317.0.292", {"start": v(-18.43, 7.37) * mm, "end": v(-18.48, 7.36) * mm});
            skLineSegment(sketch, "E3317.0.293", {"start": v(-18.48, 7.36) * mm, "end": v(-18.53, 7.35) * mm});
            skLineSegment(sketch, "E3317.0.294", {"start": v(-18.53, 7.35) * mm, "end": v(-18.58, 7.33) * mm});
            skLineSegment(sketch, "E3317.0.295", {"start": v(-18.58, 7.33) * mm, "end": v(-18.8, 7.21) * mm});
            skLineSegment(sketch, "E3317.0.296", {"start": v(-18.8, 7.21) * mm, "end": v(-19, 7.14) * mm});
            skLineSegment(sketch, "E3317.0.297", {"start": v(-19, 7.14) * mm, "end": v(-19.2, 7.1) * mm});
            skLineSegment(sketch, "E3317.0.298", {"start": v(-19.2, 7.1) * mm, "end": v(-19.4, 7.06) * mm});
            skLineSegment(sketch, "E3317.0.299", {"start": v(-19.4, 7.06) * mm, "end": v(-19.6, 7.05) * mm});
            skLineSegment(sketch, "E3317.0.300", {"start": v(-19.6, 7.05) * mm, "end": v(-19.81, 7.06) * mm});
            skLineSegment(sketch, "E3317.0.301", {"start": v(-19.81, 7.06) * mm, "end": v(-20.02, 7.1) * mm});
            skLineSegment(sketch, "E3317.0.302", {"start": v(-20.02, 7.1) * mm, "end": v(-20.22, 7.15) * mm});
            skLineSegment(sketch, "E3317.0.303", {"start": v(-20.22, 7.15) * mm, "end": v(-20.4, 7.22) * mm});
            skLineSegment(sketch, "E3317.0.304", {"start": v(-20.4, 7.22) * mm, "end": v(-20.6, 7.32) * mm});
            skLineSegment(sketch, "E3317.0.305", {"start": v(-20.6, 7.32) * mm, "end": v(-20.77, 7.43) * mm});
            skLineSegment(sketch, "E3317.0.306", {"start": v(-20.77, 7.43) * mm, "end": v(-20.92, 7.56) * mm});
            skLineSegment(sketch, "E3317.0.307", {"start": v(-20.92, 7.56) * mm, "end": v(-21.07, 7.7) * mm});
            skLineSegment(sketch, "E3317.0.308", {"start": v(-21.07, 7.7) * mm, "end": v(-21.2, 7.86) * mm});
            skLineSegment(sketch, "E3317.0.309", {"start": v(-21.2, 7.86) * mm, "end": v(-21.32, 8.03) * mm});
            skLineSegment(sketch, "E3317.0.310", {"start": v(-21.32, 8.03) * mm, "end": v(-21.44, 8.26) * mm});
            skLineSegment(sketch, "E3317.0.311", {"start": v(-21.44, 8.26) * mm, "end": v(-21.47, 8.3) * mm});
            skLineSegment(sketch, "E3317.0.312", {"start": v(-21.47, 8.3) * mm, "end": v(-21.5, 8.34) * mm});
            skLineSegment(sketch, "E3317.0.313", {"start": v(-21.5, 8.34) * mm, "end": v(-21.53, 8.38) * mm});
            skLineSegment(sketch, "E3317.0.314", {"start": v(-21.53, 8.38) * mm, "end": v(-21.57, 8.4) * mm});
            skLineSegment(sketch, "E3317.0.315", {"start": v(-21.57, 8.4) * mm, "end": v(-21.62, 8.44) * mm});
            skLineSegment(sketch, "E3317.0.316", {"start": v(-21.62, 8.44) * mm, "end": v(-21.66, 8.46) * mm});
            skLineSegment(sketch, "E3317.0.317", {"start": v(-21.66, 8.46) * mm, "end": v(-21.71, 8.48) * mm});
            skLineSegment(sketch, "E3317.0.318", {"start": v(-21.71, 8.48) * mm, "end": v(-22.92, 8.87) * mm});
            skLineSegment(sketch, "E3317.0.319", {"start": v(-22.92, 8.87) * mm, "end": v(-28, 9.62) * mm});
            skLineSegment(sketch, "E3317.0.320", {"start": v(-28, 9.62) * mm, "end": v(-28.18, 9.63) * mm});
            skLineSegment(sketch, "E3317.0.321", {"start": v(-28.18, 9.63) * mm, "end": v(-28.36, 9.6) * mm});
            skLineSegment(sketch, "E3317.0.322", {"start": v(-28.36, 9.6) * mm, "end": v(-28.52, 9.56) * mm});
            skLineSegment(sketch, "E3317.0.323", {"start": v(-28.52, 9.56) * mm, "end": v(-28.67, 9.48) * mm});
            skLineSegment(sketch, "E3317.0.324", {"start": v(-28.67, 9.48) * mm, "end": v(-28.81, 9.37) * mm});
            skLineSegment(sketch, "E3317.0.325", {"start": v(-28.81, 9.37) * mm, "end": v(-28.93, 9.25) * mm});
            skLineSegment(sketch, "E3317.0.326", {"start": v(-28.93, 9.25) * mm, "end": v(-29.03, 9.1) * mm});
            skLineSegment(sketch, "E3317.0.327", {"start": v(-29.03, 9.1) * mm, "end": v(-29.1, 8.94) * mm});
            skLineSegment(sketch, "E3317.0.328", {"start": v(-29.1, 8.94) * mm, "end": v(-30.18, 5.6) * mm});
            skLineSegment(sketch, "E3317.0.329", {"start": v(-30.18, 5.6) * mm, "end": v(-30.22, 5.42) * mm});
            skLineSegment(sketch, "E3317.0.330", {"start": v(-30.22, 5.42) * mm, "end": v(-30.23, 5.25) * mm});
            skLineSegment(sketch, "E3317.0.331", {"start": v(-30.23, 5.25) * mm, "end": v(-30.2, 5.08) * mm});
            skLineSegment(sketch, "E3317.0.332", {"start": v(-30.2, 5.08) * mm, "end": v(-30.16, 4.91) * mm});
            skLineSegment(sketch, "E3317.0.333", {"start": v(-30.16, 4.91) * mm, "end": v(-30.08, 4.76) * mm});
            skLineSegment(sketch, "E3317.0.334", {"start": v(-30.08, 4.76) * mm, "end": v(-29.98, 4.62) * mm});
            skLineSegment(sketch, "E3317.0.335", {"start": v(-29.98, 4.62) * mm, "end": v(-29.85, 4.5) * mm});
            skLineSegment(sketch, "E3317.0.336", {"start": v(-29.85, 4.5) * mm, "end": v(-29.7, 4.4) * mm});
            skLineSegment(sketch, "E3317.0.337", {"start": v(-29.7, 4.4) * mm, "end": v(-25.14, 2.02) * mm});
            skLineSegment(sketch, "E3317.0.338", {"start": v(-25.14, 2.02) * mm, "end": v(-23.94, 1.63) * mm});
            skLineSegment(sketch, "E3317.0.339", {"start": v(-23.94, 1.63) * mm, "end": v(-23.89, 1.62) * mm});
            skLineSegment(sketch, "E3317.0.340", {"start": v(-23.89, 1.62) * mm, "end": v(-23.84, 1.6) * mm});
            skLineSegment(sketch, "E3317.0.341", {"start": v(-23.84, 1.6) * mm, "end": v(-23.79, 1.6) * mm});
            skLineSegment(sketch, "E3317.0.342", {"start": v(-23.79, 1.6) * mm, "end": v(-23.73, 1.6) * mm});
            skLineSegment(sketch, "E3317.0.343", {"start": v(-23.73, 1.6) * mm, "end": v(-23.68, 1.61) * mm});
            skLineSegment(sketch, "E3317.0.344", {"start": v(-23.68, 1.61) * mm, "end": v(-23.63, 1.63) * mm});
            skLineSegment(sketch, "E3317.0.345", {"start": v(-23.63, 1.63) * mm, "end": v(-23.59, 1.65) * mm});
            skLineSegment(sketch, "E3317.0.346", {"start": v(-23.59, 1.65) * mm, "end": v(-23.35, 1.76) * mm});
            skLineSegment(sketch, "E3317.0.347", {"start": v(-23.35, 1.76) * mm, "end": v(-23.16, 1.83) * mm});
            skLineSegment(sketch, "E3317.0.348", {"start": v(-23.16, 1.83) * mm, "end": v(-22.96, 1.88) * mm});
            skLineSegment(sketch, "E3317.0.349", {"start": v(-22.96, 1.88) * mm, "end": v(-22.76, 1.91) * mm});
            skLineSegment(sketch, "E3317.0.350", {"start": v(-22.76, 1.91) * mm, "end": v(-22.55, 1.92) * mm});
            skLineSegment(sketch, "E3317.0.351", {"start": v(-22.55, 1.92) * mm, "end": v(-22.35, 1.91) * mm});
            skLineSegment(sketch, "E3317.0.352", {"start": v(-22.35, 1.91) * mm, "end": v(-22.15, 1.88) * mm});
            skLineSegment(sketch, "E3317.0.353", {"start": v(-22.15, 1.88) * mm, "end": v(-21.95, 1.82) * mm});
            skLineSegment(sketch, "E3317.0.354", {"start": v(-21.95, 1.82) * mm, "end": v(-21.75, 1.75) * mm});
            skLineSegment(sketch, "E3317.0.355", {"start": v(-21.75, 1.75) * mm, "end": v(-21.57, 1.66) * mm});
            skLineSegment(sketch, "E3317.0.356", {"start": v(-21.57, 1.66) * mm, "end": v(-21.4, 1.55) * mm});
            skLineSegment(sketch, "E3317.0.357", {"start": v(-21.4, 1.55) * mm, "end": v(-21.24, 1.42) * mm});
            skLineSegment(sketch, "E3317.0.358", {"start": v(-21.24, 1.42) * mm, "end": v(-21.1, 1.27) * mm});
            skLineSegment(sketch, "E3317.0.359", {"start": v(-21.1, 1.27) * mm, "end": v(-20.96, 1.12) * mm});
            skLineSegment(sketch, "E3317.0.360", {"start": v(-20.96, 1.12) * mm, "end": v(-20.85, 0.95) * mm});
            skLineSegment(sketch, "E3317.0.361", {"start": v(-20.85, 0.95) * mm, "end": v(-20.72, 0.72) * mm});
            skLineSegment(sketch, "E3317.0.362", {"start": v(-20.72, 0.72) * mm, "end": v(-20.7, 0.67) * mm});
            skLineSegment(sketch, "E3317.0.363", {"start": v(-20.7, 0.67) * mm, "end": v(-20.66, 0.63) * mm});
            skLineSegment(sketch, "E3317.0.364", {"start": v(-20.66, 0.63) * mm, "end": v(-20.63, 0.6) * mm});
            skLineSegment(sketch, "E3317.0.365", {"start": v(-20.63, 0.6) * mm, "end": v(-20.59, 0.57) * mm});
            skLineSegment(sketch, "E3317.0.366", {"start": v(-20.59, 0.57) * mm, "end": v(-20.54, 0.54) * mm});
            skLineSegment(sketch, "E3317.0.367", {"start": v(-20.54, 0.54) * mm, "end": v(-20.5, 0.52) * mm});
            skLineSegment(sketch, "E3317.0.368", {"start": v(-20.5, 0.52) * mm, "end": v(-20.45, 0.5) * mm});
            skLineSegment(sketch, "E3317.0.369", {"start": v(-20.45, 0.5) * mm, "end": v(-15.32, -1.17) * mm});
            skLineSegment(sketch, "E3317.0.370", {"start": v(-15.32, -1.17) * mm, "end": v(-15.3, -1.18) * mm});
            skLineSegment(sketch, "E3317.0.371", {"start": v(-15.3, -1.18) * mm, "end": v(-15.25, -1.2) * mm});
            skLineSegment(sketch, "E3317.0.372", {"start": v(-15.25, -1.2) * mm, "end": v(-15.21, -1.21) * mm});
            skLineSegment(sketch, "E3317.0.373", {"start": v(-15.21, -1.21) * mm, "end": v(-15.16, -1.23) * mm});
            skLineSegment(sketch, "E3317.0.374", {"start": v(-15.16, -1.23) * mm, "end": v(-15.12, -1.26) * mm});
            skLineSegment(sketch, "E3317.0.375", {"start": v(-15.12, -1.26) * mm, "end": v(-15.08, -1.29) * mm});
            skLineSegment(sketch, "E3317.0.376", {"start": v(-15.08, -1.29) * mm, "end": v(-15.05, -1.32) * mm});
            skLineSegment(sketch, "E3317.0.377", {"start": v(-15.05, -1.32) * mm, "end": v(-15.03, -1.35) * mm});
            skLineSegment(sketch, "E3317.0.378", {"start": v(-15.03, -1.35) * mm, "end": v(-15.01, -1.39) * mm});
            skLineSegment(sketch, "E3317.0.379", {"start": v(-15.01, -1.39) * mm, "end": v(-15, -1.43) * mm});
            skLineSegment(sketch, "E3317.0.380", {"start": v(-15, -1.43) * mm, "end": v(-14.99, -1.46) * mm});
            skLineSegment(sketch, "E3317.0.381", {"start": v(-14.99, -1.46) * mm, "end": v(-14.98, -1.5) * mm});
            skLineSegment(sketch, "E3317.0.382", {"start": v(-14.98, -1.5) * mm, "end": v(-14.98, -1.54) * mm});
            skLineSegment(sketch, "E3317.0.383", {"start": v(-14.98, -1.54) * mm, "end": v(-14.98, -1.58) * mm});
            skLineSegment(sketch, "E3317.0.384", {"start": v(-14.98, -1.58) * mm, "end": v(-15, -2.18) * mm});
            skLineSegment(sketch, "E3317.0.385", {"start": v(-15, -2.18) * mm, "end": v(-15, -2.36) * mm});
            skLineSegment(sketch, "E3317.0.386", {"start": v(-15, -2.36) * mm, "end": v(-14.94, -3.7) * mm});
            skLineSegment(sketch, "E3317.0.387", {"start": v(-14.94, -3.7) * mm, "end": v(-14.77, -5) * mm});
            skLineSegment(sketch, "E3317.0.388", {"start": v(-14.77, -5) * mm, "end": v(-14.49, -6.26) * mm});
            skLineSegment(sketch, "E3317.0.389", {"start": v(-14.49, -6.26) * mm, "end": v(-14.1, -7.48) * mm});
            skLineSegment(sketch, "E3317.0.390", {"start": v(-14.1, -7.48) * mm, "end": v(-13.62, -8.65) * mm});
            skLineSegment(sketch, "E3317.0.391", {"start": v(-13.62, -8.65) * mm, "end": v(-13.04, -9.77) * mm});
            skLineSegment(sketch, "E3317.0.392", {"start": v(-13.04, -9.77) * mm, "end": v(-12.38, -10.84) * mm});
            skLineSegment(sketch, "E3317.0.393", {"start": v(-12.38, -10.84) * mm, "end": v(-11.6, -11.86) * mm});
            skLineSegment(sketch, "E3317.0.394", {"start": v(-11.6, -11.86) * mm, "end": v(-11.6, -11.88) * mm});
            skLineSegment(sketch, "E3317.0.395", {"start": v(-11.6, -11.88) * mm, "end": v(-11.59, -11.9) * mm});
            skLineSegment(sketch, "E3317.0.396", {"start": v(-11.59, -11.9) * mm, "end": v(-11.58, -11.93) * mm});
            skLineSegment(sketch, "E3317.0.397", {"start": v(-11.58, -11.93) * mm, "end": v(-11.57, -11.95) * mm});
            skLineSegment(sketch, "E3317.0.398", {"start": v(-11.57, -11.95) * mm, "end": v(-11.57, -11.98) * mm});
            skLineSegment(sketch, "E3317.0.399", {"start": v(-11.57, -11.98) * mm, "end": v(-11.57, -12) * mm});
            skLineSegment(sketch, "E3317.0.400", {"start": v(-11.57, -12) * mm, "end": v(-11.57, -12.03) * mm});
            skLineSegment(sketch, "E3317.0.401", {"start": v(-11.57, -12.03) * mm, "end": v(-11.57, -12.06) * mm});
            skLineSegment(sketch, "E3317.0.402", {"start": v(-11.57, -12.06) * mm, "end": v(-11.58, -12.1) * mm});
            skLineSegment(sketch, "E3317.0.403", {"start": v(-11.58, -12.1) * mm, "end": v(-11.6, -12.14) * mm});
            skLineSegment(sketch, "E3317.0.404", {"start": v(-11.6, -12.14) * mm, "end": v(-11.6, -12.18) * mm});
            skLineSegment(sketch, "E3317.0.405", {"start": v(-11.6, -12.18) * mm, "end": v(-11.62, -12.22) * mm});
            skLineSegment(sketch, "E3317.0.406", {"start": v(-11.62, -12.22) * mm, "end": v(-11.65, -12.27) * mm});
            skLineSegment(sketch, "E3317.0.407", {"start": v(-11.65, -12.27) * mm, "end": v(-11.65, -12.28) * mm});
            skLineSegment(sketch, "E3317.0.408", {"start": v(-11.65, -12.28) * mm, "end": v(-14.87, -16.7) * mm});
            skLineSegment(sketch, "E3317.0.409", {"start": v(-14.87, -16.7) * mm, "end": v(-14.9, -16.75) * mm});
            skLineSegment(sketch, "E3317.0.410", {"start": v(-14.9, -16.75) * mm, "end": v(-14.92, -16.8) * mm});
            skLineSegment(sketch, "E3317.0.411", {"start": v(-14.92, -16.8) * mm, "end": v(-14.94, -16.84) * mm});
            skLineSegment(sketch, "E3317.0.412", {"start": v(-14.94, -16.84) * mm, "end": v(-14.95, -16.89) * mm});
            skLineSegment(sketch, "E3317.0.413", {"start": v(-14.95, -16.89) * mm, "end": v(-14.96, -16.94) * mm});
            skLineSegment(sketch, "E3317.0.414", {"start": v(-14.96, -16.94) * mm, "end": v(-14.96, -16.99) * mm});
            skLineSegment(sketch, "E3317.0.415", {"start": v(-14.96, -16.99) * mm, "end": v(-14.96, -17.04) * mm});
            skLineSegment(sketch, "E3317.0.416", {"start": v(-14.96, -17.04) * mm, "end": v(-14.92, -17.3) * mm});
            skLineSegment(sketch, "E3317.0.417", {"start": v(-14.92, -17.3) * mm, "end": v(-14.92, -17.5) * mm});
            skLineSegment(sketch, "E3317.0.418", {"start": v(-14.92, -17.5) * mm, "end": v(-14.93, -17.7) * mm});
            skLineSegment(sketch, "E3317.0.419", {"start": v(-14.93, -17.7) * mm, "end": v(-14.96, -17.9) * mm});
            skLineSegment(sketch, "E3317.0.420", {"start": v(-14.96, -17.9) * mm, "end": v(-15.02, -18.1) * mm});
            skLineSegment(sketch, "E3317.0.421", {"start": v(-15.02, -18.1) * mm, "end": v(-15.1, -18.3) * mm});
            skLineSegment(sketch, "E3317.0.422", {"start": v(-15.1, -18.3) * mm, "end": v(-15.18, -18.48) * mm});
            skLineSegment(sketch, "E3317.0.423", {"start": v(-15.18, -18.48) * mm, "end": v(-15.3, -18.65) * mm});
            skLineSegment(sketch, "E3317.0.424", {"start": v(-15.3, -18.65) * mm, "end": v(-15.43, -18.82) * mm});
            skLineSegment(sketch, "E3317.0.425", {"start": v(-15.43, -18.82) * mm, "end": v(-15.57, -18.96) * mm});
            skLineSegment(sketch, "E3317.0.426", {"start": v(-15.57, -18.96) * mm, "end": v(-15.73, -19.1) * mm});
            skLineSegment(sketch, "E3317.0.427", {"start": v(-15.73, -19.1) * mm, "end": v(-15.9, -19.2) * mm});
            skLineSegment(sketch, "E3317.0.428", {"start": v(-15.9, -19.2) * mm, "end": v(-16.08, -19.3) * mm});
            skLineSegment(sketch, "E3317.0.429", {"start": v(-16.08, -19.3) * mm, "end": v(-16.27, -19.37) * mm});
            skLineSegment(sketch, "E3317.0.430", {"start": v(-16.27, -19.37) * mm, "end": v(-16.47, -19.43) * mm});
            skLineSegment(sketch, "E3317.0.431", {"start": v(-16.47, -19.43) * mm, "end": v(-16.73, -19.47) * mm});
            skLineSegment(sketch, "E3317.0.432", {"start": v(-16.73, -19.47) * mm, "end": v(-16.78, -19.49) * mm});
            skLineSegment(sketch, "E3317.0.433", {"start": v(-16.78, -19.49) * mm, "end": v(-16.83, -19.5) * mm});
            skLineSegment(sketch, "E3317.0.434", {"start": v(-16.83, -19.5) * mm, "end": v(-16.87, -19.53) * mm});
            skLineSegment(sketch, "E3317.0.435", {"start": v(-16.87, -19.53) * mm, "end": v(-16.91, -19.56) * mm});
            skLineSegment(sketch, "E3317.0.436", {"start": v(-16.91, -19.56) * mm, "end": v(-16.95, -19.6) * mm});
            skLineSegment(sketch, "E3317.0.437", {"start": v(-16.95, -19.6) * mm, "end": v(-16.99, -19.63) * mm});
            skLineSegment(sketch, "E3317.0.438", {"start": v(-16.99, -19.63) * mm, "end": v(-17.02, -19.67) * mm});
            skLineSegment(sketch, "E3317.0.439", {"start": v(-17.02, -19.67) * mm, "end": v(-17.77, -20.7) * mm});
            skLineSegment(sketch, "E3317.0.440", {"start": v(-17.77, -20.7) * mm, "end": v(-20.05, -25.3) * mm});
            skLineSegment(sketch, "E3317.0.441", {"start": v(-20.05, -25.3) * mm, "end": v(-20.12, -25.46) * mm});
            skLineSegment(sketch, "E3317.0.442", {"start": v(-20.12, -25.46) * mm, "end": v(-20.15, -25.64) * mm});
            skLineSegment(sketch, "E3317.0.443", {"start": v(-20.15, -25.64) * mm, "end": v(-20.15, -25.8) * mm});
            skLineSegment(sketch, "E3317.0.444", {"start": v(-20.15, -25.8) * mm, "end": v(-20.13, -25.98) * mm});
            skLineSegment(sketch, "E3317.0.445", {"start": v(-20.13, -25.98) * mm, "end": v(-20.07, -26.14) * mm});
            skLineSegment(sketch, "E3317.0.446", {"start": v(-20.07, -26.14) * mm, "end": v(-19.99, -26.3) * mm});
            skLineSegment(sketch, "E3317.0.447", {"start": v(-19.99, -26.3) * mm, "end": v(-19.88, -26.43) * mm});
            skLineSegment(sketch, "E3317.0.448", {"start": v(-19.88, -26.43) * mm, "end": v(-19.74, -26.55) * mm});
            skLineSegment(sketch, "E3317.0.449", {"start": v(-19.74, -26.55) * mm, "end": v(-16.9, -28.61) * mm});
            skLineSegment(sketch, "E3317.0.450", {"start": v(-16.9, -28.61) * mm, "end": v(-16.75, -28.7) * mm});
            skLineSegment(sketch, "E3317.0.451", {"start": v(-16.75, -28.7) * mm, "end": v(-16.58, -28.77) * mm});
            skLineSegment(sketch, "E3317.0.452", {"start": v(-16.58, -28.77) * mm, "end": v(-16.41, -28.8) * mm});
            skLineSegment(sketch, "E3317.0.453", {"start": v(-16.41, -28.8) * mm, "end": v(-16.24, -28.8) * mm});
            skLineSegment(sketch, "E3317.0.454", {"start": v(-16.24, -28.8) * mm, "end": v(-16.07, -28.78) * mm});
            skLineSegment(sketch, "E3317.0.455", {"start": v(-16.07, -28.78) * mm, "end": v(-15.9, -28.72) * mm});
            skLineSegment(sketch, "E3317.0.456", {"start": v(-15.9, -28.72) * mm, "end": v(-15.75, -28.63) * mm});
            skLineSegment(sketch, "E3317.0.457", {"start": v(-15.75, -28.63) * mm, "end": v(-15.61, -28.52) * mm});
            skLineSegment(sketch, "E3317.0.458", {"start": v(-15.61, -28.52) * mm, "end": v(-11.94, -24.92) * mm});
            skLineSegment(sketch, "E3317.0.459", {"start": v(-11.94, -24.92) * mm, "end": v(-11.2, -23.9) * mm});
            skLineSegment(sketch, "E3317.0.460", {"start": v(-11.2, -23.9) * mm, "end": v(-11.17, -23.86) * mm});
            skLineSegment(sketch, "E3317.0.461", {"start": v(-11.17, -23.86) * mm, "end": v(-11.15, -23.81) * mm});
            skLineSegment(sketch, "E3317.0.462", {"start": v(-11.15, -23.81) * mm, "end": v(-11.13, -23.76) * mm});
            skLineSegment(sketch, "E3317.0.463", {"start": v(-11.13, -23.76) * mm, "end": v(-11.11, -23.71) * mm});
            skLineSegment(sketch, "E3317.0.464", {"start": v(-11.11, -23.71) * mm, "end": v(-11.1, -23.66) * mm});
            skLineSegment(sketch, "E3317.0.465", {"start": v(-11.1, -23.66) * mm, "end": v(-11.1, -23.61) * mm});
            skLineSegment(sketch, "E3317.0.466", {"start": v(-11.1, -23.61) * mm, "end": v(-11.1, -23.56) * mm});
            skLineSegment(sketch, "E3317.0.467", {"start": v(-11.1, -23.56) * mm, "end": v(-11.14, -23.3) * mm});
            skLineSegment(sketch, "E3317.0.468", {"start": v(-11.14, -23.3) * mm, "end": v(-11.15, -23.1) * mm});
            skLineSegment(sketch, "E3317.0.469", {"start": v(-11.15, -23.1) * mm, "end": v(-11.14, -22.9) * mm});
            skLineSegment(sketch, "E3317.0.470", {"start": v(-11.14, -22.9) * mm, "end": v(-11.1, -22.7) * mm});
            skLineSegment(sketch, "E3317.0.471", {"start": v(-11.1, -22.7) * mm, "end": v(-11.05, -22.5) * mm});
            skLineSegment(sketch, "E3317.0.472", {"start": v(-11.05, -22.5) * mm, "end": v(-10.97, -22.3) * mm});
            skLineSegment(sketch, "E3317.0.473", {"start": v(-10.97, -22.3) * mm, "end": v(-10.88, -22.12) * mm});
            skLineSegment(sketch, "E3317.0.474", {"start": v(-10.88, -22.12) * mm, "end": v(-10.77, -21.95) * mm});
            skLineSegment(sketch, "E3317.0.475", {"start": v(-10.77, -21.95) * mm, "end": v(-10.64, -21.78) * mm});
            skLineSegment(sketch, "E3317.0.476", {"start": v(-10.64, -21.78) * mm, "end": v(-10.5, -21.64) * mm});
            skLineSegment(sketch, "E3317.0.477", {"start": v(-10.5, -21.64) * mm, "end": v(-10.33, -21.51) * mm});
            skLineSegment(sketch, "E3317.0.478", {"start": v(-10.33, -21.51) * mm, "end": v(-10.16, -21.4) * mm});
            skLineSegment(sketch, "E3317.0.479", {"start": v(-10.16, -21.4) * mm, "end": v(-9.98, -21.3) * mm});
            skLineSegment(sketch, "E3317.0.480", {"start": v(-9.98, -21.3) * mm, "end": v(-9.79, -21.23) * mm});
            skLineSegment(sketch, "E3317.0.481", {"start": v(-9.79, -21.23) * mm, "end": v(-9.6, -21.17) * mm});
            skLineSegment(sketch, "E3317.0.482", {"start": v(-9.6, -21.17) * mm, "end": v(-9.34, -21.13) * mm});
            skLineSegment(sketch, "E3317.0.483", {"start": v(-9.34, -21.13) * mm, "end": v(-9.29, -21.11) * mm});
            skLineSegment(sketch, "E3317.0.484", {"start": v(-9.29, -21.11) * mm, "end": v(-9.24, -21.1) * mm});
            skLineSegment(sketch, "E3317.0.485", {"start": v(-9.24, -21.1) * mm, "end": v(-9.2, -21.07) * mm});
            skLineSegment(sketch, "E3317.0.486", {"start": v(-9.2, -21.07) * mm, "end": v(-9.15, -21.04) * mm});
            skLineSegment(sketch, "E3317.0.487", {"start": v(-9.15, -21.04) * mm, "end": v(-9.11, -21.01) * mm});
            skLineSegment(sketch, "E3317.0.488", {"start": v(-9.11, -21.01) * mm, "end": v(-9.07, -20.97) * mm});
            skLineSegment(sketch, "E3317.0.489", {"start": v(-9.07, -20.97) * mm, "end": v(-9.04, -20.93) * mm});
            skLineSegment(sketch, "E3317.0.490", {"start": v(-9.04, -20.93) * mm, "end": v(-6.75, -17.8) * mm});
            skLineSegment(sketch, "E3317.0.491", {"start": v(-6.75, -17.8) * mm, "end": v(-6.7, -17.7) * mm});
            skLineSegment(sketch, "E3317.0.492", {"start": v(-6.7, -17.7) * mm, "end": v(-6.67, -17.6) * mm});
            skLineSegment(sketch, "E3317.0.493", {"start": v(-6.67, -17.6) * mm, "end": v(-6.66, -17.52) * mm});
            skLineSegment(sketch, "E3317.0.494", {"start": v(-6.66, -17.52) * mm, "end": v(-6.66, -17.02) * mm});
            skLineSegment(sketch, "E3317.0.495", {"start": v(-6.66, -17.02) * mm, "end": v(-6.65, -16.9) * mm});
            skLineSegment(sketch, "E3317.0.496", {"start": v(-6.65, -16.9) * mm, "end": v(-6.62, -16.8) * mm});
            skLineSegment(sketch, "E3317.0.497", {"start": v(-6.62, -16.8) * mm, "end": v(-6.58, -16.72) * mm});
            skLineSegment(sketch, "E3317.0.498", {"start": v(-6.58, -16.72) * mm, "end": v(-6.52, -16.65) * mm});
            skLineSegment(sketch, "E3317.0.499", {"start": v(-6.52, -16.65) * mm, "end": v(-6.44, -16.59) * mm});
            skLineSegment(sketch, "E3317.0.500", {"start": v(-6.44, -16.59) * mm, "end": v(-6.36, -16.54) * mm});
            skLineSegment(sketch, "E3317.0.501", {"start": v(-6.36, -16.54) * mm, "end": v(-6.26, -16.51) * mm});
            skLineSegment(sketch, "E3317.0.502", {"start": v(-6.26, -16.51) * mm, "end": v(-6.18, -16.5) * mm});
            skLineSegment(sketch, "E3317.0.503", {"start": v(-6.18, -16.5) * mm, "end": v(-4.7, -16.5) * mm});
            skLineSegment(sketch, "E3317.0.504", {"start": v(-4.7, -16.5) * mm, "end": v(-4.7, -16.5) * mm});
            skLineSegment(sketch, "E3317.0.505", {"start": v(-4.7, -16.5) * mm, "end": v(-4.6, -16.51) * mm});
            skLineSegment(sketch, "E3317.0.506", {"start": v(-4.6, -16.51) * mm, "end": v(-4.51, -16.54) * mm});
            skLineSegment(sketch, "E3317.0.507", {"start": v(-4.51, -16.54) * mm, "end": v(-4.43, -16.59) * mm});
            skLineSegment(sketch, "E3317.0.508", {"start": v(-4.43, -16.59) * mm, "end": v(-4.35, -16.65) * mm});
            skLineSegment(sketch, "E3317.0.509", {"start": v(-4.35, -16.65) * mm, "end": v(-4.3, -16.72) * mm});
            skLineSegment(sketch, "E3317.0.510", {"start": v(-4.3, -16.72) * mm, "end": v(-4.24, -16.8) * mm});
            skLineSegment(sketch, "E3317.0.511", {"start": v(-4.24, -16.8) * mm, "end": v(-4.21, -16.9) * mm});
            skLineSegment(sketch, "E3317.0.512", {"start": v(-4.21, -16.9) * mm, "end": v(-4.2, -17.05) * mm});
            skLineSegment(sketch, "E3317.0.513", {"start": v(-4.2, -17.05) * mm, "end": v(-4.2, -17.37) * mm});
            skLineSegment(sketch, "E3317.0.514", {"start": v(-4.2, -17.37) * mm, "end": v(-4.2, -17.5) * mm});
            skLineSegment(sketch, "E3317.0.515", {"start": v(-4.2, -17.5) * mm, "end": v(-4.17, -17.59) * mm});
            skLineSegment(sketch, "E3317.0.516", {"start": v(-4.17, -17.59) * mm, "end": v(-4.12, -17.67) * mm});
            skLineSegment(sketch, "E3317.0.517", {"start": v(-4.12, -17.67) * mm, "end": v(-4.06, -17.75) * mm});
            skLineSegment(sketch, "E3317.0.518", {"start": v(-4.06, -17.75) * mm, "end": v(-3.99, -17.8) * mm});
            skLineSegment(sketch, "E3317.0.519", {"start": v(-3.99, -17.8) * mm, "end": v(-3.9, -17.85) * mm});
            skLineSegment(sketch, "E3317.0.520", {"start": v(-3.9, -17.85) * mm, "end": v(-3.8, -17.88) * mm});
            skLineSegment(sketch, "E3317.0.521", {"start": v(-3.8, -17.88) * mm, "end": v(-3.7, -17.9) * mm});
            skLineSegment(sketch, "E3317.0.522", {"start": v(-3.7, -17.9) * mm, "end": v(3.71, -17.9) * mm});
            skLineSegment(sketch, "E3317.0.523", {"start": v(3.71, -17.9) * mm, "end": v(3.81, -17.89) * mm});
            skLineSegment(sketch, "E3317.0.524", {"start": v(3.81, -17.89) * mm, "end": v(3.9, -17.86) * mm});
            skLineSegment(sketch, "E3317.0.525", {"start": v(3.9, -17.86) * mm, "end": v(4, -17.81) * mm});
            skLineSegment(sketch, "E3317.0.526", {"start": v(4, -17.81) * mm, "end": v(4.06, -17.75) * mm});
            skLineSegment(sketch, "E3317.0.527", {"start": v(4.06, -17.75) * mm, "end": v(4.13, -17.68) * mm});
            skLineSegment(sketch, "E3317.0.528", {"start": v(4.13, -17.68) * mm, "end": v(4.17, -17.6) * mm});
            skLineSegment(sketch, "E3317.0.529", {"start": v(4.17, -17.6) * mm, "end": v(4.2, -17.5) * mm});
            skLineSegment(sketch, "E3317.0.530", {"start": v(4.2, -17.5) * mm, "end": v(4.21, -17.37) * mm});
            skLineSegment(sketch, "E3317.0.531", {"start": v(4.21, -17.37) * mm, "end": v(4.21, -17) * mm});
            skLineSegment(sketch, "E3317.0.532", {"start": v(4.21, -17) * mm, "end": v(4.22, -16.9) * mm});
            skLineSegment(sketch, "E3317.0.533", {"start": v(4.22, -16.9) * mm, "end": v(4.25, -16.8) * mm});
            skLineSegment(sketch, "E3317.0.534", {"start": v(4.25, -16.8) * mm, "end": v(4.3, -16.72) * mm});
            skLineSegment(sketch, "E3317.0.535", {"start": v(4.3, -16.72) * mm, "end": v(4.36, -16.64) * mm});
            skLineSegment(sketch, "E3317.0.536", {"start": v(4.36, -16.64) * mm, "end": v(4.43, -16.58) * mm});
            skLineSegment(sketch, "E3317.0.537", {"start": v(4.43, -16.58) * mm, "end": v(4.52, -16.54) * mm});
            skLineSegment(sketch, "E3317.0.538", {"start": v(4.52, -16.54) * mm, "end": v(4.6, -16.5) * mm});
            skLineSegment(sketch, "E3317.0.539", {"start": v(4.6, -16.5) * mm, "end": v(4.71, -16.5) * mm});
            skLineSegment(sketch, "E3317.0.540", {"start": v(4.71, -16.5) * mm, "end": v(4.71, -16.5) * mm});
            skLineSegment(sketch, "E3317.0.541", {"start": v(4.71, -16.5) * mm, "end": v(4.71, -16.5) * mm});
            skLineSegment(sketch, "E3317.0.542", {"start": v(4.71, -16.5) * mm, "end": v(6.16, -16.5) * mm});
            skLineSegment(sketch, "E3317.0.543", {"start": v(6.16, -16.5) * mm, "end": v(6.16, -16.5) * mm});
            skLineSegment(sketch, "E3317.0.544", {"start": v(6.16, -16.5) * mm, "end": v(6.26, -16.5) * mm});
            skLineSegment(sketch, "E3317.0.545", {"start": v(6.26, -16.5) * mm, "end": v(6.35, -16.54) * mm});
            skLineSegment(sketch, "E3317.0.546", {"start": v(6.35, -16.54) * mm, "end": v(6.44, -16.58) * mm});
            skLineSegment(sketch, "E3317.0.547", {"start": v(6.44, -16.58) * mm, "end": v(6.51, -16.64) * mm});
            skLineSegment(sketch, "E3317.0.548", {"start": v(6.51, -16.64) * mm, "end": v(6.57, -16.72) * mm});
            skLineSegment(sketch, "E3317.0.549", {"start": v(6.57, -16.72) * mm, "end": v(6.62, -16.8) * mm});
            skLineSegment(sketch, "E3317.0.550", {"start": v(6.62, -16.8) * mm, "end": v(6.65, -16.9) * mm});
            skLineSegment(sketch, "E3317.0.551", {"start": v(6.65, -16.9) * mm, "end": v(6.66, -17) * mm});
            skLineSegment(sketch, "E3317.0.552", {"start": v(6.66, -17) * mm, "end": v(6.66, -17) * mm});
            skLineSegment(sketch, "E3317.0.553", {"start": v(6.66, -17) * mm, "end": v(6.66, -17.52) * mm});
            skLineSegment(sketch, "E3317.0.554", {"start": v(6.66, -17.52) * mm, "end": v(6.67, -17.6) * mm});
            skLineSegment(sketch, "E3317.0.555", {"start": v(6.67, -17.6) * mm, "end": v(6.7, -17.7) * mm});
            skLineSegment(sketch, "E3317.0.556", {"start": v(6.7, -17.7) * mm, "end": v(6.75, -17.79) * mm});
            skLineSegment(sketch, "E3317.0.557", {"start": v(6.75, -17.79) * mm, "end": v(6.76, -17.8) * mm});
            skLineSegment(sketch, "E3317.0.558", {"start": v(6.76, -17.8) * mm, "end": v(9.04, -20.93) * mm});
            skLineSegment(sketch, "E3317.0.559", {"start": v(9.04, -20.93) * mm, "end": v(9.07, -20.97) * mm});
            skLineSegment(sketch, "E3317.0.560", {"start": v(9.07, -20.97) * mm, "end": v(9.1, -21) * mm});
            skLineSegment(sketch, "E3317.0.561", {"start": v(9.1, -21) * mm, "end": v(9.15, -21.04) * mm});
            skLineSegment(sketch, "E3317.0.562", {"start": v(9.15, -21.04) * mm, "end": v(9.2, -21.07) * mm});
            skLineSegment(sketch, "E3317.0.563", {"start": v(9.2, -21.07) * mm, "end": v(9.24, -21.1) * mm});
            skLineSegment(sketch, "E3317.0.564", {"start": v(9.24, -21.1) * mm, "end": v(9.29, -21.1) * mm});
            skLineSegment(sketch, "E3317.0.565", {"start": v(9.29, -21.1) * mm, "end": v(9.33, -21.12) * mm});
            skLineSegment(sketch, "E3317.0.566", {"start": v(9.33, -21.12) * mm, "end": v(9.59, -21.17) * mm});
            skLineSegment(sketch, "E3317.0.567", {"start": v(9.59, -21.17) * mm, "end": v(9.79, -21.22) * mm});
            skLineSegment(sketch, "E3317.0.568", {"start": v(9.79, -21.22) * mm, "end": v(9.98, -21.3) * mm});
            skLineSegment(sketch, "E3317.0.569", {"start": v(9.98, -21.3) * mm, "end": v(10.16, -21.4) * mm});
            skLineSegment(sketch, "E3317.0.570", {"start": v(10.16, -21.4) * mm, "end": v(10.33, -21.5) * mm});
            skLineSegment(sketch, "E3317.0.571", {"start": v(10.33, -21.5) * mm, "end": v(10.49, -21.64) * mm});
            skLineSegment(sketch, "E3317.0.572", {"start": v(10.49, -21.64) * mm, "end": v(10.63, -21.78) * mm});
            skLineSegment(sketch, "E3317.0.573", {"start": v(10.63, -21.78) * mm, "end": v(10.77, -21.94) * mm});
            skLineSegment(sketch, "E3317.0.574", {"start": v(10.77, -21.94) * mm, "end": v(10.88, -22.12) * mm});
            skLineSegment(sketch, "E3317.0.575", {"start": v(10.88, -22.12) * mm, "end": v(10.97, -22.3) * mm});
            skLineSegment(sketch, "E3317.0.576", {"start": v(10.97, -22.3) * mm, "end": v(11.05, -22.5) * mm});
            skLineSegment(sketch, "E3317.0.577", {"start": v(11.05, -22.5) * mm, "end": v(11.1, -22.69) * mm});
            skLineSegment(sketch, "E3317.0.578", {"start": v(11.1, -22.69) * mm, "end": v(11.13, -22.89) * mm});
            skLineSegment(sketch, "E3317.0.579", {"start": v(11.13, -22.89) * mm, "end": v(11.15, -23.1) * mm});
            skLineSegment(sketch, "E3317.0.580", {"start": v(11.15, -23.1) * mm, "end": v(11.14, -23.3) * mm});
            skLineSegment(sketch, "E3317.0.581", {"start": v(11.14, -23.3) * mm, "end": v(11.1, -23.56) * mm});
            skLineSegment(sketch, "E3317.0.582", {"start": v(11.1, -23.56) * mm, "end": v(11.1, -23.6) * mm});
            skLineSegment(sketch, "E3317.0.583", {"start": v(11.1, -23.6) * mm, "end": v(11.1, -23.66) * mm});
            skLineSegment(sketch, "E3317.0.584", {"start": v(11.1, -23.66) * mm, "end": v(11.11, -23.7) * mm});
            skLineSegment(sketch, "E3317.0.585", {"start": v(11.11, -23.7) * mm, "end": v(11.13, -23.76) * mm});
            skLineSegment(sketch, "E3317.0.586", {"start": v(11.13, -23.76) * mm, "end": v(11.14, -23.8) * mm});
            skLineSegment(sketch, "E3317.0.587", {"start": v(11.14, -23.8) * mm, "end": v(11.17, -23.85) * mm});
            skLineSegment(sketch, "E3317.0.588", {"start": v(11.17, -23.85) * mm, "end": v(11.2, -23.9) * mm});
            skLineSegment(sketch, "E3317.0.589", {"start": v(11.2, -23.9) * mm, "end": v(11.94, -24.92) * mm});
            skLineSegment(sketch, "E3317.0.590", {"start": v(11.94, -24.92) * mm, "end": v(15.61, -28.51) * mm});
            skLineSegment(sketch, "E3317.0.591", {"start": v(15.61, -28.51) * mm, "end": v(15.75, -28.63) * mm});
            skLineSegment(sketch, "E3317.0.592", {"start": v(15.75, -28.63) * mm, "end": v(15.9, -28.71) * mm});
            skLineSegment(sketch, "E3317.0.593", {"start": v(15.9, -28.71) * mm, "end": v(16.07, -28.77) * mm});
            skLineSegment(sketch, "E3317.0.594", {"start": v(16.07, -28.77) * mm, "end": v(16.24, -28.8) * mm});
            skLineSegment(sketch, "E3317.0.595", {"start": v(16.24, -28.8) * mm, "end": v(16.41, -28.8) * mm});
            skLineSegment(sketch, "E3317.0.596", {"start": v(16.41, -28.8) * mm, "end": v(16.58, -28.76) * mm});
            skLineSegment(sketch, "E3317.0.597", {"start": v(16.58, -28.76) * mm, "end": v(16.75, -28.7) * mm});
            skLineSegment(sketch, "E3317.0.598", {"start": v(16.75, -28.7) * mm, "end": v(16.9, -28.6) * mm});
            skLineSegment(sketch, "E3317.0.599", {"start": v(16.9, -28.6) * mm, "end": v(19.74, -26.55) * mm});
            skLineSegment(sketch, "E3317.0.600", {"start": v(19.74, -26.55) * mm, "end": v(19.88, -26.43) * mm});
            skLineSegment(sketch, "E3317.0.601", {"start": v(19.88, -26.43) * mm, "end": v(19.99, -26.3) * mm});
            skLineSegment(sketch, "E3317.0.602", {"start": v(19.99, -26.3) * mm, "end": v(20.07, -26.14) * mm});
            skLineSegment(sketch, "E3317.0.603", {"start": v(20.07, -26.14) * mm, "end": v(20.12, -25.97) * mm});
            skLineSegment(sketch, "E3317.0.604", {"start": v(20.12, -25.97) * mm, "end": v(20.15, -25.8) * mm});
            skLineSegment(sketch, "E3317.0.605", {"start": v(20.15, -25.8) * mm, "end": v(20.15, -25.63) * mm});
            skLineSegment(sketch, "E3317.0.606", {"start": v(20.15, -25.63) * mm, "end": v(20.11, -25.46) * mm});
            skLineSegment(sketch, "E3317.0.607", {"start": v(20.11, -25.46) * mm, "end": v(20.05, -25.3) * mm});
            skLineSegment(sketch, "E3317.0.608", {"start": v(20.05, -25.3) * mm, "end": v(17.76, -20.69) * mm});
            skLineSegment(sketch, "E3317.0.609", {"start": v(17.76, -20.69) * mm, "end": v(17.02, -19.66) * mm});
            skLineSegment(sketch, "E3317.0.610", {"start": v(17.02, -19.66) * mm, "end": v(16.99, -19.62) * mm});
            skLineSegment(sketch, "E3317.0.611", {"start": v(16.99, -19.62) * mm, "end": v(16.95, -19.59) * mm});
            skLineSegment(sketch, "E3317.0.612", {"start": v(16.95, -19.59) * mm, "end": v(16.91, -19.55) * mm});
            skLineSegment(sketch, "E3317.0.613", {"start": v(16.91, -19.55) * mm, "end": v(16.87, -19.53) * mm});
            skLineSegment(sketch, "E3317.0.614", {"start": v(16.87, -19.53) * mm, "end": v(16.82, -19.5) * mm});
            skLineSegment(sketch, "E3317.0.615", {"start": v(16.82, -19.5) * mm, "end": v(16.78, -19.48) * mm});
            skLineSegment(sketch, "E3317.0.616", {"start": v(16.78, -19.48) * mm, "end": v(16.73, -19.47) * mm});
            skLineSegment(sketch, "E3317.0.617", {"start": v(16.73, -19.47) * mm, "end": v(16.47, -19.42) * mm});
            skLineSegment(sketch, "E3317.0.618", {"start": v(16.47, -19.42) * mm, "end": v(16.27, -19.37) * mm});
            skLineSegment(sketch, "E3317.0.619", {"start": v(16.27, -19.37) * mm, "end": v(16.08, -19.3) * mm});
            skLineSegment(sketch, "E3317.0.620", {"start": v(16.08, -19.3) * mm, "end": v(15.9, -19.2) * mm});
            skLineSegment(sketch, "E3317.0.621", {"start": v(15.9, -19.2) * mm, "end": v(15.73, -19.09) * mm});
            skLineSegment(sketch, "E3317.0.622", {"start": v(15.73, -19.09) * mm, "end": v(15.57, -18.96) * mm});
            skLineSegment(sketch, "E3317.0.623", {"start": v(15.57, -18.96) * mm, "end": v(15.43, -18.81) * mm});
            skLineSegment(sketch, "E3317.0.624", {"start": v(15.43, -18.81) * mm, "end": v(15.3, -18.65) * mm});
            skLineSegment(sketch, "E3317.0.625", {"start": v(15.3, -18.65) * mm, "end": v(15.18, -18.48) * mm});
            skLineSegment(sketch, "E3317.0.626", {"start": v(15.18, -18.48) * mm, "end": v(15.09, -18.3) * mm});
            skLineSegment(sketch, "E3317.0.627", {"start": v(15.09, -18.3) * mm, "end": v(15.01, -18.1) * mm});
            skLineSegment(sketch, "E3317.0.628", {"start": v(15.01, -18.1) * mm, "end": v(14.96, -17.9) * mm});
            skLineSegment(sketch, "E3317.0.629", {"start": v(14.96, -17.9) * mm, "end": v(14.93, -17.7) * mm});
            skLineSegment(sketch, "E3317.0.630", {"start": v(14.93, -17.7) * mm, "end": v(14.91, -17.5) * mm});
            skLineSegment(sketch, "E3317.0.631", {"start": v(14.91, -17.5) * mm, "end": v(14.92, -17.3) * mm});
            skLineSegment(sketch, "E3317.0.632", {"start": v(14.92, -17.3) * mm, "end": v(14.96, -17.04) * mm});
            skLineSegment(sketch, "E3317.0.633", {"start": v(14.96, -17.04) * mm, "end": v(14.96, -16.98) * mm});
            skLineSegment(sketch, "E3317.0.634", {"start": v(14.96, -16.98) * mm, "end": v(14.96, -16.93) * mm});
            skLineSegment(sketch, "E3317.0.635", {"start": v(14.96, -16.93) * mm, "end": v(14.95, -16.88) * mm});
            skLineSegment(sketch, "E3317.0.636", {"start": v(14.95, -16.88) * mm, "end": v(14.94, -16.83) * mm});
            skLineSegment(sketch, "E3317.0.637", {"start": v(14.94, -16.83) * mm, "end": v(14.92, -16.79) * mm});
            skLineSegment(sketch, "E3317.0.638", {"start": v(14.92, -16.79) * mm, "end": v(14.9, -16.74) * mm});
            skLineSegment(sketch, "E3317.0.639", {"start": v(14.9, -16.74) * mm, "end": v(14.87, -16.7) * mm});
            skLineSegment(sketch, "E3317.0.640", {"start": v(14.87, -16.7) * mm, "end": v(11.63, -12.24) * mm});
            skLineSegment(sketch, "E3317.0.641", {"start": v(11.63, -12.24) * mm, "end": v(11.6, -12.2) * mm});
            skLineSegment(sketch, "E3317.0.642", {"start": v(11.6, -12.2) * mm, "end": v(11.6, -12.16) * mm});
            skLineSegment(sketch, "E3317.0.643", {"start": v(11.6, -12.16) * mm, "end": v(11.58, -12.13) * mm});
            skLineSegment(sketch, "E3317.0.644", {"start": v(11.58, -12.13) * mm, "end": v(11.57, -12.1) * mm});
            skLineSegment(sketch, "E3317.0.645", {"start": v(11.57, -12.1) * mm, "end": v(11.57, -12.06) * mm});
            skLineSegment(sketch, "E3317.0.646", {"start": v(11.57, -12.06) * mm, "end": v(11.57, -12.04) * mm});
            skLineSegment(sketch, "E3317.0.647", {"start": v(11.57, -12.04) * mm, "end": v(11.57, -12) * mm});
            skLineSegment(sketch, "E3317.0.648", {"start": v(11.57, -12) * mm, "end": v(11.57, -11.96) * mm});
            skLineSegment(sketch, "E3317.0.649", {"start": v(11.57, -11.96) * mm, "end": v(11.58, -11.93) * mm});
            skLineSegment(sketch, "E3317.0.650", {"start": v(11.58, -11.93) * mm, "end": v(11.6, -11.9) * mm});
            skLineSegment(sketch, "E3317.0.651", {"start": v(11.6, -11.9) * mm, "end": v(11.6, -11.87) * mm});
            skLineSegment(sketch, "E3317.0.652", {"start": v(11.6, -11.87) * mm, "end": v(11.63, -11.84) * mm});
            skLineSegment(sketch, "E3317.0.653", {"start": v(11.63, -11.84) * mm, "end": v(11.65, -11.81) * mm});
            skLineSegment(sketch, "E3317.0.654", {"start": v(11.65, -11.81) * mm, "end": v(11.67, -11.78) * mm});
            skLineSegment(sketch, "E3317.0.655", {"start": v(11.67, -11.78) * mm, "end": v(12.41, -10.79) * mm});
            skLineSegment(sketch, "E3317.0.656", {"start": v(12.41, -10.79) * mm, "end": v(13.07, -9.73) * mm});
            skLineSegment(sketch, "E3317.0.657", {"start": v(13.07, -9.73) * mm, "end": v(13.64, -8.61) * mm});
            skLineSegment(sketch, "E3317.0.658", {"start": v(13.64, -8.61) * mm, "end": v(14.12, -7.45) * mm});
            skLineSegment(sketch, "E3317.0.659", {"start": v(14.12, -7.45) * mm, "end": v(14.5, -6.23) * mm});
            skLineSegment(sketch, "E3317.0.660", {"start": v(14.5, -6.23) * mm, "end": v(14.77, -4.98) * mm});
            skLineSegment(sketch, "E3317.0.661", {"start": v(14.77, -4.98) * mm, "end": v(14.94, -3.69) * mm});
            skLineSegment(sketch, "E3317.0.662", {"start": v(14.94, -3.69) * mm, "end": v(15, -2.36) * mm});
            skLineSegment(sketch, "E3317.0.663", {"start": v(15, -2.36) * mm, "end": v(15, -2) * mm});
            skLineSegment(sketch, "E3317.0.664", {"start": v(15, -2) * mm, "end": v(14.98, -1.58) * mm});
            skLineSegment(sketch, "E3317.0.665", {"start": v(14.98, -1.58) * mm, "end": v(14.98, -1.55) * mm});
            skLineSegment(sketch, "E3317.0.666", {"start": v(14.98, -1.55) * mm, "end": v(14.98, -1.5) * mm});
            skLineSegment(sketch, "E3317.0.667", {"start": v(14.98, -1.5) * mm, "end": v(14.99, -1.47) * mm});
            skLineSegment(sketch, "E3317.0.668", {"start": v(14.99, -1.47) * mm, "end": v(15, -1.43) * mm});
            skLineSegment(sketch, "E3317.0.669", {"start": v(15, -1.43) * mm, "end": v(15, -1.4) * mm});
            skLineSegment(sketch, "E3317.0.670", {"start": v(15, -1.4) * mm, "end": v(15.02, -1.36) * mm});
            skLineSegment(sketch, "E3317.0.671", {"start": v(15.02, -1.36) * mm, "end": v(15.04, -1.33) * mm});
            skLineSegment(sketch, "E3317.0.672", {"start": v(15.04, -1.33) * mm, "end": v(15.06, -1.3) * mm});
            skLineSegment(sketch, "E3317.0.673", {"start": v(15.06, -1.3) * mm, "end": v(15.1, -1.28) * mm});
            skLineSegment(sketch, "E3317.0.674", {"start": v(15.1, -1.28) * mm, "end": v(15.12, -1.26) * mm});
            skLineSegment(sketch, "E3317.0.675", {"start": v(15.12, -1.26) * mm, "end": v(15.15, -1.24) * mm});
            skLineSegment(sketch, "E3317.0.676", {"start": v(15.15, -1.24) * mm, "end": v(15.18, -1.22) * mm});
            skLineSegment(sketch, "E3317.0.677", {"start": v(15.18, -1.22) * mm, "end": v(15.2, -1.21) * mm});
            skLineSegment(sketch, "E3317.0.678", {"start": v(15.2, -1.21) * mm, "end": v(15.23, -1.2) * mm});
            skLineSegment(sketch, "E3317.0.679", {"start": v(15.23, -1.2) * mm, "end": v(20.45, 0.5) * mm});
            skLineSegment(sketch, "E3317.0.680", {"start": v(20.45, 0.5) * mm, "end": v(20.5, 0.52) * mm});
            skLineSegment(sketch, "E3317.0.681", {"start": v(20.5, 0.52) * mm, "end": v(20.54, 0.54) * mm});
            skLineSegment(sketch, "E3317.0.682", {"start": v(20.54, 0.54) * mm, "end": v(20.59, 0.57) * mm});
            skLineSegment(sketch, "E3317.0.683", {"start": v(20.59, 0.57) * mm, "end": v(20.63, 0.6) * mm});
            skLineSegment(sketch, "E3317.0.684", {"start": v(20.63, 0.6) * mm, "end": v(20.66, 0.63) * mm});
            skLineSegment(sketch, "E3317.0.685", {"start": v(20.66, 0.63) * mm, "end": v(20.7, 0.67) * mm});
            skLineSegment(sketch, "E3317.0.686", {"start": v(20.7, 0.67) * mm, "end": v(20.73, 0.72) * mm});
            skLineSegment(sketch, "E3317.0.687", {"start": v(20.73, 0.72) * mm, "end": v(20.85, 0.95) * mm});
            skLineSegment(sketch, "E3317.0.688", {"start": v(20.85, 0.95) * mm, "end": v(20.96, 1.12) * mm});
            skLineSegment(sketch, "E3317.0.689", {"start": v(20.96, 1.12) * mm, "end": v(21.1, 1.27) * mm});
            skLineSegment(sketch, "E3317.0.690", {"start": v(21.1, 1.27) * mm, "end": v(21.24, 1.42) * mm});
            skLineSegment(sketch, "E3317.0.691", {"start": v(21.24, 1.42) * mm, "end": v(21.4, 1.55) * mm});
            skLineSegment(sketch, "E3317.0.692", {"start": v(21.4, 1.55) * mm, "end": v(21.57, 1.66) * mm});
            skLineSegment(sketch, "E3317.0.693", {"start": v(21.57, 1.66) * mm, "end": v(21.75, 1.75) * mm});
            skLineSegment(sketch, "E3317.0.694", {"start": v(21.75, 1.75) * mm, "end": v(21.95, 1.82) * mm});
            skLineSegment(sketch, "E3317.0.695", {"start": v(21.95, 1.82) * mm, "end": v(22.15, 1.88) * mm});
            skLineSegment(sketch, "E3317.0.696", {"start": v(22.15, 1.88) * mm, "end": v(22.35, 1.91) * mm});
            skLineSegment(sketch, "E3317.0.697", {"start": v(22.35, 1.91) * mm, "end": v(22.55, 1.92) * mm});
            skLineSegment(sketch, "E3317.0.698", {"start": v(22.55, 1.92) * mm, "end": v(22.76, 1.91) * mm});
            skLineSegment(sketch, "E3317.0.699", {"start": v(22.76, 1.91) * mm, "end": v(22.96, 1.88) * mm});
            skLineSegment(sketch, "E3317.0.700", {"start": v(22.96, 1.88) * mm, "end": v(23.16, 1.83) * mm});
            skLineSegment(sketch, "E3317.0.701", {"start": v(23.16, 1.83) * mm, "end": v(23.35, 1.76) * mm});
            skLineSegment(sketch, "E3317.0.702", {"start": v(23.35, 1.76) * mm, "end": v(23.59, 1.65) * mm});
            skLineSegment(sketch, "E3317.0.703", {"start": v(23.59, 1.65) * mm, "end": v(23.63, 1.63) * mm});
            skLineSegment(sketch, "E3317.0.704", {"start": v(23.63, 1.63) * mm, "end": v(23.68, 1.61) * mm});
            skLineSegment(sketch, "E3317.0.705", {"start": v(23.68, 1.61) * mm, "end": v(23.73, 1.6) * mm});
            skLineSegment(sketch, "E3317.0.706", {"start": v(23.73, 1.6) * mm, "end": v(23.79, 1.6) * mm});
            skLineSegment(sketch, "E3317.0.707", {"start": v(23.79, 1.6) * mm, "end": v(23.84, 1.6) * mm});
            skLineSegment(sketch, "E3317.0.708", {"start": v(23.84, 1.6) * mm, "end": v(23.89, 1.62) * mm});
            skLineSegment(sketch, "E3317.0.709", {"start": v(23.89, 1.62) * mm, "end": v(23.94, 1.63) * mm});
            skLineSegment(sketch, "E3317.0.710", {"start": v(23.94, 1.63) * mm, "end": v(25.14, 2.02) * mm});
            skLineSegment(sketch, "E3317.0.711", {"start": v(25.14, 2.02) * mm, "end": v(29.7, 4.4) * mm});
            skLineSegment(sketch, "E3317.0.712", {"start": v(29.7, 4.4) * mm, "end": v(29.85, 4.5) * mm});
            skLineSegment(sketch, "E3317.0.713", {"start": v(29.85, 4.5) * mm, "end": v(29.98, 4.62) * mm});
            skLineSegment(sketch, "E3317.0.714", {"start": v(29.98, 4.62) * mm, "end": v(30.08, 4.76) * mm});
            skLineSegment(sketch, "E3317.0.715", {"start": v(30.08, 4.76) * mm, "end": v(30.16, 4.91) * mm});
            skLineSegment(sketch, "E3317.0.716", {"start": v(30.16, 4.91) * mm, "end": v(30.2, 5.08) * mm});
            skLineSegment(sketch, "E3317.0.717", {"start": v(30.2, 5.08) * mm, "end": v(30.23, 5.25) * mm});
            skCircle(sketch, "E3318.0", {"center": v(0, 25) * mm, "radius": 1.7 * mm});
            skCircle(sketch, "E3319.0", {"center": v(26.03, 6.09) * mm, "radius": 1.7 * mm});
            skCircle(sketch, "E3320.0", {"center": v(-26.02, 6.08) * mm, "radius": 1.7 * mm});
            skCircle(sketch, "E3321.0", {"center": v(16.1, -24.5) * mm, "radius": 1.7 * mm});
            skCircle(sketch, "E3322.0", {"center": v(-16.07, -24.51) * mm, "radius": 1.7 * mm});
            skSolve(sketch);
        }
        {
            var Q0;
            Q0=makeQuery(id+"F1.imprint","IMPRINT",FACE,{"disambiguationData":[TD([[makeQuery(id+"F1.imprint","IMPRINT",EDGE,{"derivedFrom":sQuery(id+"F1.wireOp",EDGE,"E3317.0.0")}),1.0]])]});
            extrude(context, id + "F2", {"entities" : qUnion([Q0]), "depth" : 2 * mm});
        }
    });
